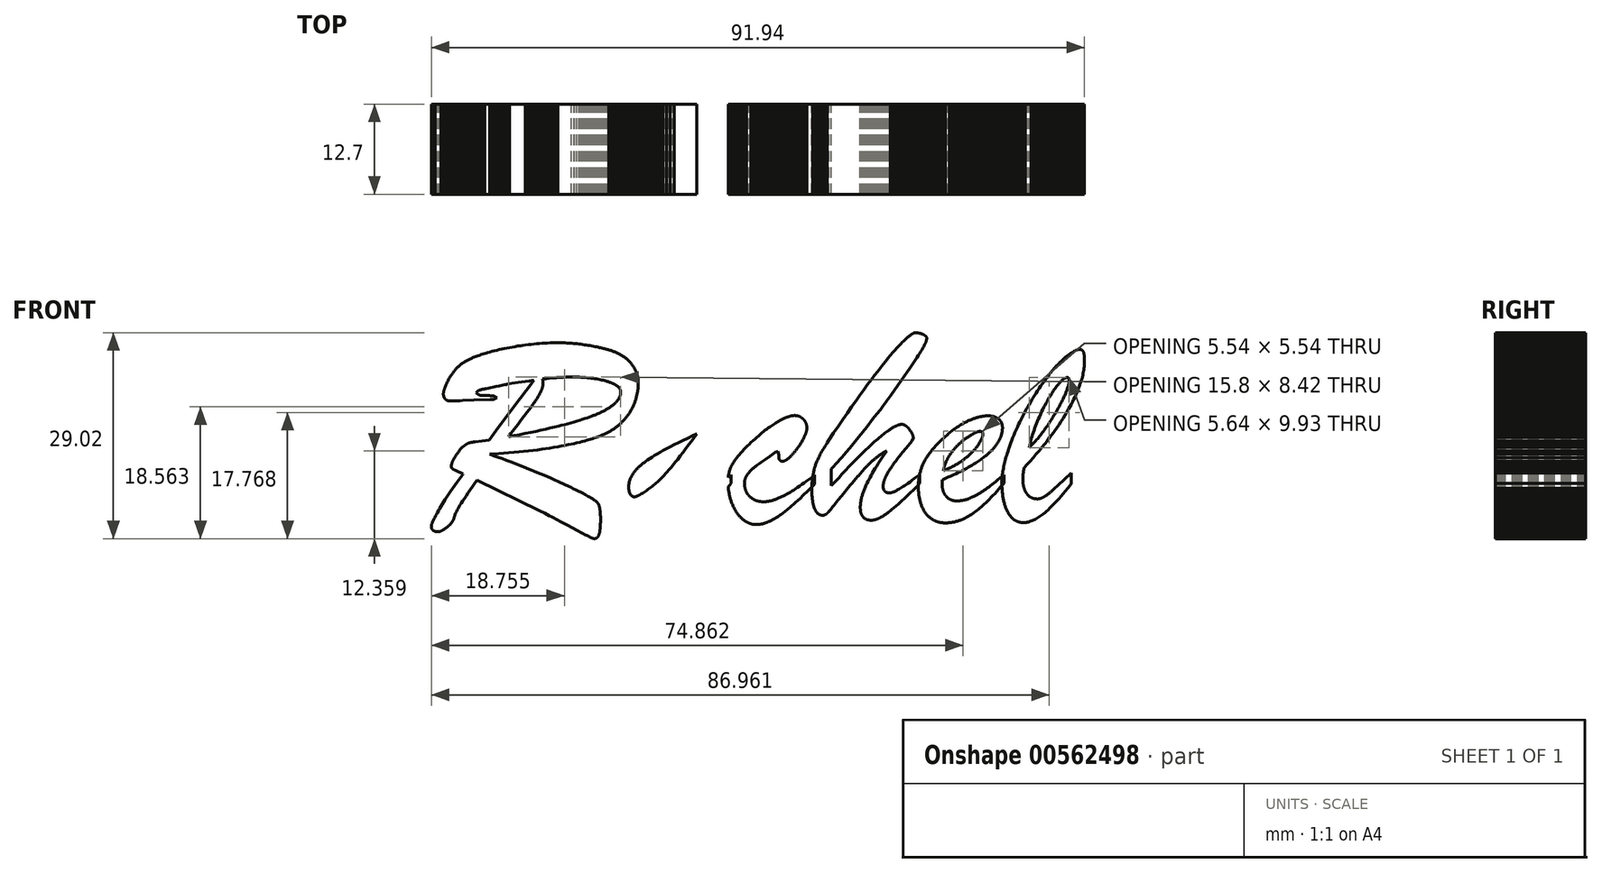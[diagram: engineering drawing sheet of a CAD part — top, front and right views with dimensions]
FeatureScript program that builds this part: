
annotation { "Feature Type Name" : "Feature", "Feature Type Description" : "" }
export const myFeature = defineFeature(function(context is Context, id is Id, definition is map)
    precondition{}
    {
        {
            var Q0;
            Q0=qCreatedBy(makeId("Front.planeOp"),FACE);
            var sketch = newSketch(context, id + "F0", { "sketchPlane" : qUnion([Q0])});
            skLineSegment(sketch, "E0", {"start": v(-45.97, -12.76) * mm, "end": v(-45.97, -12.8) * mm});
            skLineSegment(sketch, "E1", {"start": v(-45.97, -12.8) * mm, "end": v(-45.97, -12.83) * mm});
            skLineSegment(sketch, "E2", {"start": v(-45.97, -12.83) * mm, "end": v(-45.97, -12.86) * mm});
            skLineSegment(sketch, "E3", {"start": v(-45.97, -12.86) * mm, "end": v(-45.97, -12.9) * mm});
            skLineSegment(sketch, "E4", {"start": v(-45.97, -12.9) * mm, "end": v(-45.96, -12.92) * mm});
            skLineSegment(sketch, "E5", {"start": v(-45.96, -12.92) * mm, "end": v(-45.96, -12.95) * mm});
            skLineSegment(sketch, "E6", {"start": v(-45.96, -12.95) * mm, "end": v(-45.95, -12.98) * mm});
            skLineSegment(sketch, "E7", {"start": v(-45.95, -12.98) * mm, "end": v(-45.94, -13) * mm});
            skLineSegment(sketch, "E8", {"start": v(-45.94, -13) * mm, "end": v(-45.94, -13.03) * mm});
            skLineSegment(sketch, "E9", {"start": v(-45.94, -13.03) * mm, "end": v(-45.93, -13.05) * mm});
            skLineSegment(sketch, "E10", {"start": v(-45.93, -13.05) * mm, "end": v(-45.92, -13.08) * mm});
            skLineSegment(sketch, "E11", {"start": v(-45.92, -13.08) * mm, "end": v(-45.9, -13.1) * mm});
            skLineSegment(sketch, "E12", {"start": v(-45.9, -13.1) * mm, "end": v(-45.9, -13.13) * mm});
            skLineSegment(sketch, "E13", {"start": v(-45.9, -13.13) * mm, "end": v(-45.89, -13.15) * mm});
            skLineSegment(sketch, "E14", {"start": v(-45.89, -13.15) * mm, "end": v(-45.87, -13.17) * mm});
            skLineSegment(sketch, "E15", {"start": v(-45.87, -13.17) * mm, "end": v(-45.86, -13.2) * mm});
            skLineSegment(sketch, "E16", {"start": v(-45.86, -13.2) * mm, "end": v(-45.85, -13.21) * mm});
            skLineSegment(sketch, "E17", {"start": v(-45.85, -13.21) * mm, "end": v(-45.83, -13.23) * mm});
            skLineSegment(sketch, "E18", {"start": v(-45.83, -13.23) * mm, "end": v(-45.82, -13.25) * mm});
            skLineSegment(sketch, "E19", {"start": v(-45.82, -13.25) * mm, "end": v(-45.8, -13.27) * mm});
            skLineSegment(sketch, "E20", {"start": v(-45.8, -13.27) * mm, "end": v(-45.78, -13.29) * mm});
            skLineSegment(sketch, "E21", {"start": v(-45.78, -13.29) * mm, "end": v(-45.76, -13.3) * mm});
            skLineSegment(sketch, "E22", {"start": v(-45.76, -13.3) * mm, "end": v(-45.75, -13.32) * mm});
            skLineSegment(sketch, "E23", {"start": v(-45.75, -13.32) * mm, "end": v(-45.73, -13.34) * mm});
            skLineSegment(sketch, "E24", {"start": v(-45.73, -13.34) * mm, "end": v(-45.7, -13.35) * mm});
            skLineSegment(sketch, "E25", {"start": v(-45.7, -13.35) * mm, "end": v(-45.68, -13.37) * mm});
            skLineSegment(sketch, "E26", {"start": v(-45.68, -13.37) * mm, "end": v(-45.66, -13.38) * mm});
            skLineSegment(sketch, "E27", {"start": v(-45.66, -13.38) * mm, "end": v(-45.64, -13.4) * mm});
            skLineSegment(sketch, "E28", {"start": v(-45.64, -13.4) * mm, "end": v(-45.61, -13.4) * mm});
            skLineSegment(sketch, "E29", {"start": v(-45.61, -13.4) * mm, "end": v(-45.59, -13.42) * mm});
            skLineSegment(sketch, "E30", {"start": v(-45.59, -13.42) * mm, "end": v(-45.56, -13.43) * mm});
            skLineSegment(sketch, "E31", {"start": v(-45.56, -13.43) * mm, "end": v(-45.53, -13.45) * mm});
            skLineSegment(sketch, "E32", {"start": v(-45.53, -13.45) * mm, "end": v(-45.5, -13.46) * mm});
            skLineSegment(sketch, "E33", {"start": v(-45.5, -13.46) * mm, "end": v(-45.47, -13.47) * mm});
            skLineSegment(sketch, "E34", {"start": v(-45.47, -13.47) * mm, "end": v(-45.44, -13.48) * mm});
            skLineSegment(sketch, "E35", {"start": v(-45.44, -13.48) * mm, "end": v(-45.4, -13.49) * mm});
            skLineSegment(sketch, "E36", {"start": v(-45.4, -13.49) * mm, "end": v(-45.37, -13.5) * mm});
            skLineSegment(sketch, "E37", {"start": v(-45.37, -13.5) * mm, "end": v(-45.33, -13.5) * mm});
            skLineSegment(sketch, "E38", {"start": v(-45.33, -13.5) * mm, "end": v(-45.3, -13.5) * mm});
            skLineSegment(sketch, "E39", {"start": v(-45.3, -13.5) * mm, "end": v(-45.26, -13.52) * mm});
            skLineSegment(sketch, "E40", {"start": v(-45.26, -13.52) * mm, "end": v(-45.22, -13.52) * mm});
            skLineSegment(sketch, "E41", {"start": v(-45.22, -13.52) * mm, "end": v(-45.17, -13.53) * mm});
            skLineSegment(sketch, "E42", {"start": v(-45.17, -13.53) * mm, "end": v(-45.13, -13.53) * mm});
            skLineSegment(sketch, "E43", {"start": v(-45.13, -13.53) * mm, "end": v(-45.08, -13.53) * mm});
            skLineSegment(sketch, "E44", {"start": v(-45.08, -13.53) * mm, "end": v(-45.04, -13.53) * mm});
            skLineSegment(sketch, "E45", {"start": v(-45.04, -13.53) * mm, "end": v(-44.99, -13.53) * mm});
            skLineSegment(sketch, "E46", {"start": v(-44.99, -13.53) * mm, "end": v(-44.96, -13.53) * mm});
            skLineSegment(sketch, "E47", {"start": v(-44.27, 5.9) * mm, "end": v(-44.27, 5.88) * mm});
            skLineSegment(sketch, "E48", {"start": v(-44.27, 5.88) * mm, "end": v(-44.27, 5.85) * mm});
            skLineSegment(sketch, "E49", {"start": v(-44.27, 5.85) * mm, "end": v(-44.26, 5.81) * mm});
            skLineSegment(sketch, "E50", {"start": v(-44.26, 5.81) * mm, "end": v(-44.26, 5.78) * mm});
            skLineSegment(sketch, "E51", {"start": v(-44.26, 5.78) * mm, "end": v(-44.26, 5.75) * mm});
            skLineSegment(sketch, "E52", {"start": v(-44.26, 5.75) * mm, "end": v(-44.26, 5.72) * mm});
            skLineSegment(sketch, "E53", {"start": v(-44.26, 5.72) * mm, "end": v(-44.25, 5.7) * mm});
            skLineSegment(sketch, "E54", {"start": v(-44.25, 5.7) * mm, "end": v(-44.25, 5.67) * mm});
            skLineSegment(sketch, "E55", {"start": v(-44.25, 5.67) * mm, "end": v(-44.25, 5.64) * mm});
            skLineSegment(sketch, "E56", {"start": v(-44.25, 5.64) * mm, "end": v(-44.24, 5.61) * mm});
            skLineSegment(sketch, "E57", {"start": v(-44.24, 5.61) * mm, "end": v(-44.23, 5.59) * mm});
            skLineSegment(sketch, "E58", {"start": v(-44.23, 5.59) * mm, "end": v(-44.23, 5.56) * mm});
            skLineSegment(sketch, "E59", {"start": v(-44.23, 5.56) * mm, "end": v(-44.22, 5.54) * mm});
            skLineSegment(sketch, "E60", {"start": v(-44.22, 5.54) * mm, "end": v(-44.22, 5.51) * mm});
            skLineSegment(sketch, "E61", {"start": v(-44.22, 5.51) * mm, "end": v(-44.2, 5.5) * mm});
            skLineSegment(sketch, "E62", {"start": v(-44.2, 5.5) * mm, "end": v(-44.2, 5.47) * mm});
            skLineSegment(sketch, "E63", {"start": v(-44.2, 5.47) * mm, "end": v(-44.2, 5.45) * mm});
            skLineSegment(sketch, "E64", {"start": v(-44.2, 5.45) * mm, "end": v(-44.18, 5.42) * mm});
            skLineSegment(sketch, "E65", {"start": v(-44.18, 5.42) * mm, "end": v(-44.17, 5.4) * mm});
            skLineSegment(sketch, "E66", {"start": v(-44.17, 5.4) * mm, "end": v(-44.16, 5.38) * mm});
            skLineSegment(sketch, "E67", {"start": v(-44.16, 5.38) * mm, "end": v(-44.15, 5.36) * mm});
            skLineSegment(sketch, "E68", {"start": v(-44.15, 5.36) * mm, "end": v(-44.14, 5.34) * mm});
            skLineSegment(sketch, "E69", {"start": v(-44.14, 5.34) * mm, "end": v(-44.13, 5.32) * mm});
            skLineSegment(sketch, "E70", {"start": v(-44.13, 5.32) * mm, "end": v(-44.12, 5.3) * mm});
            skLineSegment(sketch, "E71", {"start": v(-44.12, 5.3) * mm, "end": v(-44.1, 5.29) * mm});
            skLineSegment(sketch, "E72", {"start": v(-44.1, 5.29) * mm, "end": v(-44.1, 5.27) * mm});
            skLineSegment(sketch, "E73", {"start": v(-44.1, 5.27) * mm, "end": v(-44.08, 5.25) * mm});
            skLineSegment(sketch, "E74", {"start": v(-44.08, 5.25) * mm, "end": v(-44.07, 5.23) * mm});
            skLineSegment(sketch, "E75", {"start": v(-44.07, 5.23) * mm, "end": v(-44.05, 5.21) * mm});
            skLineSegment(sketch, "E76", {"start": v(-44.05, 5.21) * mm, "end": v(-44.04, 5.2) * mm});
            skLineSegment(sketch, "E77", {"start": v(-44.04, 5.2) * mm, "end": v(-44.02, 5.18) * mm});
            skLineSegment(sketch, "E78", {"start": v(-44.02, 5.18) * mm, "end": v(-44, 5.16) * mm});
            skLineSegment(sketch, "E79", {"start": v(-43.13, -4.13) * mm, "end": v(-43.14, -4.15) * mm});
            skLineSegment(sketch, "E80", {"start": v(-43.14, -4.15) * mm, "end": v(-43.14, -4.18) * mm});
            skLineSegment(sketch, "E81", {"start": v(-43.14, -4.18) * mm, "end": v(-43.14, -4.2) * mm});
            skLineSegment(sketch, "E82", {"start": v(-43.14, -4.2) * mm, "end": v(-43.14, -4.23) * mm});
            skLineSegment(sketch, "E83", {"start": v(-43.14, -4.23) * mm, "end": v(-43.15, -4.25) * mm});
            skLineSegment(sketch, "E84", {"start": v(-43.15, -4.25) * mm, "end": v(-43.15, -4.27) * mm});
            skLineSegment(sketch, "E85", {"start": v(-43.15, -4.27) * mm, "end": v(-43.15, -4.3) * mm});
            skLineSegment(sketch, "E86", {"start": v(-43.15, -4.3) * mm, "end": v(-43.15, -4.32) * mm});
            skLineSegment(sketch, "E87", {"start": v(-43.15, -4.32) * mm, "end": v(-43.14, -4.34) * mm});
            skLineSegment(sketch, "E88", {"start": v(-43.14, -4.34) * mm, "end": v(-43.14, -4.36) * mm});
            skLineSegment(sketch, "E89", {"start": v(-43.14, -4.36) * mm, "end": v(-43.14, -4.38) * mm});
            skLineSegment(sketch, "E90", {"start": v(-43.14, -4.38) * mm, "end": v(-43.14, -4.4) * mm});
            skLineSegment(sketch, "E91", {"start": v(-43.14, -4.4) * mm, "end": v(-43.14, -4.41) * mm});
            skLineSegment(sketch, "E92", {"start": v(-43.14, -4.41) * mm, "end": v(-43.13, -4.43) * mm});
            skLineSegment(sketch, "E93", {"start": v(-43.13, -4.43) * mm, "end": v(-43.13, -4.45) * mm});
            skLineSegment(sketch, "E94", {"start": v(-43.13, -4.45) * mm, "end": v(-43.13, -4.46) * mm});
            skLineSegment(sketch, "E95", {"start": v(-43.13, -4.46) * mm, "end": v(-43.12, -4.48) * mm});
            skLineSegment(sketch, "E96", {"start": v(-43.12, -4.48) * mm, "end": v(-43.12, -4.5) * mm});
            skLineSegment(sketch, "E97", {"start": v(-43.12, -4.5) * mm, "end": v(-43.11, -4.5) * mm});
            skLineSegment(sketch, "E98", {"start": v(-43.11, -4.5) * mm, "end": v(-43.1, -4.52) * mm});
            skLineSegment(sketch, "E99", {"start": v(-43.1, -4.52) * mm, "end": v(-43.1, -4.53) * mm});
            skLineSegment(sketch, "E100", {"start": v(-43.1, -4.53) * mm, "end": v(-43.1, -4.55) * mm});
            skLineSegment(sketch, "E101", {"start": v(-43.1, -4.55) * mm, "end": v(-43.09, -4.56) * mm});
            skLineSegment(sketch, "E102", {"start": v(-43.09, -4.56) * mm, "end": v(-43.08, -4.57) * mm});
            skLineSegment(sketch, "E103", {"start": v(-43.08, -4.57) * mm, "end": v(-43.07, -4.58) * mm});
            skLineSegment(sketch, "E104", {"start": v(-43.07, -4.58) * mm, "end": v(-43.07, -4.6) * mm});
            skLineSegment(sketch, "E105", {"start": v(-43.07, -4.6) * mm, "end": v(-43.06, -4.6) * mm});
            skLineSegment(sketch, "E106", {"start": v(-43.06, -4.6) * mm, "end": v(-43.05, -4.62) * mm});
            skLineSegment(sketch, "E107", {"start": v(-43.05, -4.62) * mm, "end": v(-43.04, -4.63) * mm});
            skLineSegment(sketch, "E108", {"start": v(-43.04, -4.63) * mm, "end": v(-43.03, -4.64) * mm});
            skLineSegment(sketch, "E109", {"start": v(-43.03, -4.64) * mm, "end": v(-43.02, -4.65) * mm});
            skLineSegment(sketch, "E110", {"start": v(-43.02, -4.65) * mm, "end": v(-43.01, -4.66) * mm});
            skLineSegment(sketch, "E111", {"start": v(-43.01, -4.66) * mm, "end": v(-43, -4.67) * mm});
            skLineSegment(sketch, "E112", {"start": v(-43, -4.67) * mm, "end": v(-43, -4.67) * mm});
            skLineSegment(sketch, "E113", {"start": v(-43, -4.67) * mm, "end": v(-42.98, -4.68) * mm});
            skLineSegment(sketch, "E114", {"start": v(-42.98, -4.68) * mm, "end": v(-42.97, -4.7) * mm});
            skLineSegment(sketch, "E115", {"start": v(-42.97, -4.7) * mm, "end": v(-42.96, -4.7) * mm});
            skLineSegment(sketch, "E116", {"start": v(-42.96, -4.7) * mm, "end": v(-42.94, -4.7) * mm});
            skLineSegment(sketch, "E117", {"start": v(-42.94, -4.7) * mm, "end": v(-42.93, -4.71) * mm});
            skLineSegment(sketch, "E118", {"start": v(-42.93, -4.71) * mm, "end": v(-42.92, -4.72) * mm});
            skLineSegment(sketch, "E119", {"start": v(-43.9, 7.15) * mm, "end": v(-43.9, 7.13) * mm});
            skLineSegment(sketch, "E120", {"start": v(-43.9, 7.13) * mm, "end": v(-43.95, 7.02) * mm});
            skLineSegment(sketch, "E121", {"start": v(-43.95, 7.02) * mm, "end": v(-43.99, 6.92) * mm});
            skLineSegment(sketch, "E122", {"start": v(-43.99, 6.92) * mm, "end": v(-44.02, 6.83) * mm});
            skLineSegment(sketch, "E123", {"start": v(-44.02, 6.83) * mm, "end": v(-44.06, 6.74) * mm});
            skLineSegment(sketch, "E124", {"start": v(-44.06, 6.74) * mm, "end": v(-44.09, 6.65) * mm});
            skLineSegment(sketch, "E125", {"start": v(-44.09, 6.65) * mm, "end": v(-44.11, 6.57) * mm});
            skLineSegment(sketch, "E126", {"start": v(-44.11, 6.57) * mm, "end": v(-44.14, 6.5) * mm});
            skLineSegment(sketch, "E127", {"start": v(-44.14, 6.5) * mm, "end": v(-44.16, 6.43) * mm});
            skLineSegment(sketch, "E128", {"start": v(-44.16, 6.43) * mm, "end": v(-44.18, 6.36) * mm});
            skLineSegment(sketch, "E129", {"start": v(-44.18, 6.36) * mm, "end": v(-44.2, 6.3) * mm});
            skLineSegment(sketch, "E130", {"start": v(-44.2, 6.3) * mm, "end": v(-44.21, 6.24) * mm});
            skLineSegment(sketch, "E131", {"start": v(-44.21, 6.24) * mm, "end": v(-44.22, 6.2) * mm});
            skLineSegment(sketch, "E132", {"start": v(-44.22, 6.2) * mm, "end": v(-44.23, 6.14) * mm});
            skLineSegment(sketch, "E133", {"start": v(-44.23, 6.14) * mm, "end": v(-44.24, 6.1) * mm});
            skLineSegment(sketch, "E134", {"start": v(-44.24, 6.1) * mm, "end": v(-44.25, 6.06) * mm});
            skLineSegment(sketch, "E135", {"start": v(-44.25, 6.06) * mm, "end": v(-44.26, 6.02) * mm});
            skLineSegment(sketch, "E136", {"start": v(-44.26, 6.02) * mm, "end": v(-44.26, 5.98) * mm});
            skLineSegment(sketch, "E137", {"start": v(-44.26, 5.98) * mm, "end": v(-44.26, 5.95) * mm});
            skLineSegment(sketch, "E138", {"start": v(-44.26, 5.95) * mm, "end": v(-44.27, 5.92) * mm});
            skLineSegment(sketch, "E139", {"start": v(-44.27, 5.92) * mm, "end": v(-44.27, 5.9) * mm});
            skLineSegment(sketch, "E140", {"start": v(-42.82, 9) * mm, "end": v(-42.88, 8.91) * mm});
            skLineSegment(sketch, "E141", {"start": v(-42.88, 8.91) * mm, "end": v(-42.96, 8.8) * mm});
            skLineSegment(sketch, "E142", {"start": v(-42.96, 8.8) * mm, "end": v(-43.04, 8.7) * mm});
            skLineSegment(sketch, "E143", {"start": v(-43.04, 8.7) * mm, "end": v(-43.11, 8.58) * mm});
            skLineSegment(sketch, "E144", {"start": v(-43.11, 8.58) * mm, "end": v(-43.19, 8.47) * mm});
            skLineSegment(sketch, "E145", {"start": v(-43.19, 8.47) * mm, "end": v(-43.25, 8.37) * mm});
            skLineSegment(sketch, "E146", {"start": v(-43.25, 8.37) * mm, "end": v(-43.32, 8.26) * mm});
            skLineSegment(sketch, "E147", {"start": v(-43.32, 8.26) * mm, "end": v(-43.39, 8.15) * mm});
            skLineSegment(sketch, "E148", {"start": v(-43.39, 8.15) * mm, "end": v(-43.45, 8.05) * mm});
            skLineSegment(sketch, "E149", {"start": v(-43.45, 8.05) * mm, "end": v(-43.5, 7.95) * mm});
            skLineSegment(sketch, "E150", {"start": v(-43.5, 7.95) * mm, "end": v(-43.56, 7.84) * mm});
            skLineSegment(sketch, "E151", {"start": v(-43.56, 7.84) * mm, "end": v(-43.62, 7.74) * mm});
            skLineSegment(sketch, "E152", {"start": v(-43.62, 7.74) * mm, "end": v(-43.67, 7.64) * mm});
            skLineSegment(sketch, "E153", {"start": v(-43.67, 7.64) * mm, "end": v(-43.72, 7.54) * mm});
            skLineSegment(sketch, "E154", {"start": v(-43.72, 7.54) * mm, "end": v(-43.77, 7.44) * mm});
            skLineSegment(sketch, "E155", {"start": v(-43.77, 7.44) * mm, "end": v(-43.81, 7.35) * mm});
            skLineSegment(sketch, "E156", {"start": v(-43.81, 7.35) * mm, "end": v(-43.85, 7.25) * mm});
            skLineSegment(sketch, "E157", {"start": v(-43.85, 7.25) * mm, "end": v(-43.9, 7.15) * mm});
            skLineSegment(sketch, "E158", {"start": v(-42.72, -11.43) * mm, "end": v(-42.7, -11.33) * mm});
            skLineSegment(sketch, "E159", {"start": v(-42.7, -11.33) * mm, "end": v(-42.66, -11.23) * mm});
            skLineSegment(sketch, "E160", {"start": v(-42.66, -11.23) * mm, "end": v(-42.6, -11.1) * mm});
            skLineSegment(sketch, "E161", {"start": v(-42.6, -11.1) * mm, "end": v(-42.55, -10.97) * mm});
            skLineSegment(sketch, "E162", {"start": v(-42.55, -10.97) * mm, "end": v(-42.48, -10.82) * mm});
            skLineSegment(sketch, "E163", {"start": v(-42.48, -10.82) * mm, "end": v(-42.4, -10.65) * mm});
            skLineSegment(sketch, "E164", {"start": v(-42.4, -10.65) * mm, "end": v(-42.3, -10.47) * mm});
            skLineSegment(sketch, "E165", {"start": v(-42.3, -10.47) * mm, "end": v(-42.2, -10.26) * mm});
            skLineSegment(sketch, "E166", {"start": v(-42.2, -10.26) * mm, "end": v(-42.06, -10.03) * mm});
            skLineSegment(sketch, "E167", {"start": v(-42.06, -10.03) * mm, "end": v(-41.91, -9.78) * mm});
            skLineSegment(sketch, "E168", {"start": v(-41.91, -9.78) * mm, "end": v(-41.74, -9.5) * mm});
            skLineSegment(sketch, "E169", {"start": v(-41.74, -9.5) * mm, "end": v(-41.55, -9.2) * mm});
            skLineSegment(sketch, "E170", {"start": v(-41.55, -9.2) * mm, "end": v(-41.33, -8.85) * mm});
            skLineSegment(sketch, "E171", {"start": v(-41.33, -8.85) * mm, "end": v(-41.08, -8.48) * mm});
            skLineSegment(sketch, "E172", {"start": v(-41.08, -8.48) * mm, "end": v(-40.8, -8.07) * mm});
            skLineSegment(sketch, "E173", {"start": v(-40.8, -8.07) * mm, "end": v(-40.5, -7.63) * mm});
            skLineSegment(sketch, "E174", {"start": v(-40.5, -7.63) * mm, "end": v(-40.15, -7.14) * mm});
            skLineSegment(sketch, "E175", {"start": v(-40.15, -7.14) * mm, "end": v(-39.76, -6.6) * mm});
            skLineSegment(sketch, "E176", {"start": v(-39.76, -6.6) * mm, "end": v(-39.52, -6.27) * mm});
            skLineSegment(sketch, "E177", {"start": v(-44.78, -10.26) * mm, "end": v(-44.95, -10.56) * mm});
            skLineSegment(sketch, "E178", {"start": v(-44.95, -10.56) * mm, "end": v(-45.1, -10.83) * mm});
            skLineSegment(sketch, "E179", {"start": v(-45.1, -10.83) * mm, "end": v(-45.24, -11.07) * mm});
            skLineSegment(sketch, "E180", {"start": v(-45.24, -11.07) * mm, "end": v(-45.35, -11.29) * mm});
            skLineSegment(sketch, "E181", {"start": v(-45.35, -11.29) * mm, "end": v(-45.46, -11.48) * mm});
            skLineSegment(sketch, "E182", {"start": v(-45.46, -11.48) * mm, "end": v(-45.54, -11.65) * mm});
            skLineSegment(sketch, "E183", {"start": v(-45.54, -11.65) * mm, "end": v(-45.62, -11.8) * mm});
            skLineSegment(sketch, "E184", {"start": v(-45.62, -11.8) * mm, "end": v(-45.69, -11.95) * mm});
            skLineSegment(sketch, "E185", {"start": v(-45.69, -11.95) * mm, "end": v(-45.75, -12.07) * mm});
            skLineSegment(sketch, "E186", {"start": v(-45.75, -12.07) * mm, "end": v(-45.8, -12.18) * mm});
            skLineSegment(sketch, "E187", {"start": v(-45.8, -12.18) * mm, "end": v(-45.84, -12.28) * mm});
            skLineSegment(sketch, "E188", {"start": v(-45.84, -12.28) * mm, "end": v(-45.87, -12.36) * mm});
            skLineSegment(sketch, "E189", {"start": v(-45.87, -12.36) * mm, "end": v(-45.9, -12.44) * mm});
            skLineSegment(sketch, "E190", {"start": v(-45.9, -12.44) * mm, "end": v(-45.92, -12.5) * mm});
            skLineSegment(sketch, "E191", {"start": v(-45.92, -12.5) * mm, "end": v(-45.94, -12.56) * mm});
            skLineSegment(sketch, "E192", {"start": v(-45.94, -12.56) * mm, "end": v(-45.95, -12.62) * mm});
            skLineSegment(sketch, "E193", {"start": v(-45.95, -12.62) * mm, "end": v(-45.96, -12.66) * mm});
            skLineSegment(sketch, "E194", {"start": v(-45.96, -12.66) * mm, "end": v(-45.97, -12.7) * mm});
            skLineSegment(sketch, "E195", {"start": v(-45.97, -12.7) * mm, "end": v(-45.97, -12.73) * mm});
            skLineSegment(sketch, "E196", {"start": v(-45.97, -12.73) * mm, "end": v(-45.97, -12.76) * mm});
            skLineSegment(sketch, "E197", {"start": v(-42.49, -2.77) * mm, "end": v(-42.55, -2.86) * mm});
            skLineSegment(sketch, "E198", {"start": v(-42.55, -2.86) * mm, "end": v(-42.6, -2.95) * mm});
            skLineSegment(sketch, "E199", {"start": v(-42.6, -2.95) * mm, "end": v(-42.66, -3.04) * mm});
            skLineSegment(sketch, "E200", {"start": v(-42.66, -3.04) * mm, "end": v(-42.7, -3.12) * mm});
            skLineSegment(sketch, "E201", {"start": v(-42.7, -3.12) * mm, "end": v(-42.75, -3.2) * mm});
            skLineSegment(sketch, "E202", {"start": v(-42.75, -3.2) * mm, "end": v(-42.8, -3.28) * mm});
            skLineSegment(sketch, "E203", {"start": v(-42.8, -3.28) * mm, "end": v(-42.84, -3.35) * mm});
            skLineSegment(sketch, "E204", {"start": v(-42.84, -3.35) * mm, "end": v(-42.88, -3.42) * mm});
            skLineSegment(sketch, "E205", {"start": v(-42.88, -3.42) * mm, "end": v(-42.91, -3.5) * mm});
            skLineSegment(sketch, "E206", {"start": v(-42.91, -3.5) * mm, "end": v(-42.94, -3.56) * mm});
            skLineSegment(sketch, "E207", {"start": v(-42.94, -3.56) * mm, "end": v(-42.97, -3.62) * mm});
            skLineSegment(sketch, "E208", {"start": v(-42.97, -3.62) * mm, "end": v(-43, -3.68) * mm});
            skLineSegment(sketch, "E209", {"start": v(-43, -3.68) * mm, "end": v(-43.02, -3.74) * mm});
            skLineSegment(sketch, "E210", {"start": v(-43.02, -3.74) * mm, "end": v(-43.04, -3.79) * mm});
            skLineSegment(sketch, "E211", {"start": v(-43.04, -3.79) * mm, "end": v(-43.06, -3.84) * mm});
            skLineSegment(sketch, "E212", {"start": v(-43.06, -3.84) * mm, "end": v(-43.08, -3.89) * mm});
            skLineSegment(sketch, "E213", {"start": v(-43.08, -3.89) * mm, "end": v(-43.1, -3.93) * mm});
            skLineSegment(sketch, "E214", {"start": v(-43.1, -3.93) * mm, "end": v(-43.1, -3.98) * mm});
            skLineSegment(sketch, "E215", {"start": v(-43.1, -3.98) * mm, "end": v(-43.11, -4.02) * mm});
            skLineSegment(sketch, "E216", {"start": v(-43.11, -4.02) * mm, "end": v(-43.12, -4.06) * mm});
            skLineSegment(sketch, "E217", {"start": v(-43.12, -4.06) * mm, "end": v(-43.13, -4.1) * mm});
            skLineSegment(sketch, "E218", {"start": v(-43.13, -4.1) * mm, "end": v(-43.13, -4.13) * mm});
            skLineSegment(sketch, "E219", {"start": v(-39.68, 6.02) * mm, "end": v(-39.32, 6.37) * mm});
            skLineSegment(sketch, "E220", {"start": v(-30.27, 7.74) * mm, "end": v(-30.3, 8) * mm});
            skLineSegment(sketch, "E221", {"start": v(-30.25, 7.4) * mm, "end": v(-30.27, 7.74) * mm});
            skLineSegment(sketch, "E222", {"start": v(-30.6, 6.12) * mm, "end": v(-30.6, 6.13) * mm});
            skLineSegment(sketch, "E223", {"start": v(-30.6, 6.13) * mm, "end": v(-30.57, 6.2) * mm});
            skLineSegment(sketch, "E224", {"start": v(-30.57, 6.2) * mm, "end": v(-30.53, 6.27) * mm});
            skLineSegment(sketch, "E225", {"start": v(-30.53, 6.27) * mm, "end": v(-30.5, 6.34) * mm});
            skLineSegment(sketch, "E226", {"start": v(-30.5, 6.34) * mm, "end": v(-30.48, 6.4) * mm});
            skLineSegment(sketch, "E227", {"start": v(-30.48, 6.4) * mm, "end": v(-30.45, 6.46) * mm});
            skLineSegment(sketch, "E228", {"start": v(-30.45, 6.46) * mm, "end": v(-30.43, 6.52) * mm});
            skLineSegment(sketch, "E229", {"start": v(-30.43, 6.52) * mm, "end": v(-30.4, 6.58) * mm});
            skLineSegment(sketch, "E230", {"start": v(-30.4, 6.58) * mm, "end": v(-30.38, 6.64) * mm});
            skLineSegment(sketch, "E231", {"start": v(-30.38, 6.64) * mm, "end": v(-30.37, 6.7) * mm});
            skLineSegment(sketch, "E232", {"start": v(-30.37, 6.7) * mm, "end": v(-30.35, 6.75) * mm});
            skLineSegment(sketch, "E233", {"start": v(-30.35, 6.75) * mm, "end": v(-30.33, 6.8) * mm});
            skLineSegment(sketch, "E234", {"start": v(-30.33, 6.8) * mm, "end": v(-30.32, 6.85) * mm});
            skLineSegment(sketch, "E235", {"start": v(-30.32, 6.85) * mm, "end": v(-30.3, 6.9) * mm});
            skLineSegment(sketch, "E236", {"start": v(-30.3, 6.9) * mm, "end": v(-30.3, 6.95) * mm});
            skLineSegment(sketch, "E237", {"start": v(-30.3, 6.95) * mm, "end": v(-30.28, 7) * mm});
            skLineSegment(sketch, "E238", {"start": v(-30.28, 7) * mm, "end": v(-30.28, 7.04) * mm});
            skLineSegment(sketch, "E239", {"start": v(-30.28, 7.04) * mm, "end": v(-30.27, 7.09) * mm});
            skLineSegment(sketch, "E240", {"start": v(-30.27, 7.09) * mm, "end": v(-30.26, 7.13) * mm});
            skLineSegment(sketch, "E241", {"start": v(-30.26, 7.13) * mm, "end": v(-30.26, 7.17) * mm});
            skLineSegment(sketch, "E242", {"start": v(-30.26, 7.17) * mm, "end": v(-30.25, 7.21) * mm});
            skLineSegment(sketch, "E243", {"start": v(-30.25, 7.21) * mm, "end": v(-30.25, 7.25) * mm});
            skLineSegment(sketch, "E244", {"start": v(-30.25, 7.25) * mm, "end": v(-30.25, 7.3) * mm});
            skLineSegment(sketch, "E245", {"start": v(-30.25, 7.3) * mm, "end": v(-30.25, 7.33) * mm});
            skLineSegment(sketch, "E246", {"start": v(-30.25, 7.33) * mm, "end": v(-30.25, 7.37) * mm});
            skLineSegment(sketch, "E247", {"start": v(-30.25, 7.37) * mm, "end": v(-30.25, 7.4) * mm});
            skLineSegment(sketch, "E248", {"start": v(-31.5, 4.63) * mm, "end": v(-31.47, 4.67) * mm});
            skLineSegment(sketch, "E249", {"start": v(-31.47, 4.67) * mm, "end": v(-31.4, 4.79) * mm});
            skLineSegment(sketch, "E250", {"start": v(-31.4, 4.79) * mm, "end": v(-31.31, 4.9) * mm});
            skLineSegment(sketch, "E251", {"start": v(-31.31, 4.9) * mm, "end": v(-31.24, 5.02) * mm});
            skLineSegment(sketch, "E252", {"start": v(-31.24, 5.02) * mm, "end": v(-31.16, 5.14) * mm});
            skLineSegment(sketch, "E253", {"start": v(-31.16, 5.14) * mm, "end": v(-31.1, 5.25) * mm});
            skLineSegment(sketch, "E254", {"start": v(-31.1, 5.25) * mm, "end": v(-31.02, 5.37) * mm});
            skLineSegment(sketch, "E255", {"start": v(-31.02, 5.37) * mm, "end": v(-30.96, 5.48) * mm});
            skLineSegment(sketch, "E256", {"start": v(-30.96, 5.48) * mm, "end": v(-30.9, 5.59) * mm});
            skLineSegment(sketch, "E257", {"start": v(-30.9, 5.59) * mm, "end": v(-30.83, 5.7) * mm});
            skLineSegment(sketch, "E258", {"start": v(-30.83, 5.7) * mm, "end": v(-30.77, 5.8) * mm});
            skLineSegment(sketch, "E259", {"start": v(-30.77, 5.8) * mm, "end": v(-30.72, 5.9) * mm});
            skLineSegment(sketch, "E260", {"start": v(-30.72, 5.9) * mm, "end": v(-30.66, 6.01) * mm});
            skLineSegment(sketch, "E261", {"start": v(-30.66, 6.01) * mm, "end": v(-30.6, 6.12) * mm});
            skLineSegment(sketch, "E262", {"start": v(-36.53, 1.14) * mm, "end": v(-37.81, -0.61) * mm});
            skLineSegment(sketch, "E263", {"start": v(-41.47, -5.36) * mm, "end": v(-41.58, -5.51) * mm});
            skLineSegment(sketch, "E264", {"start": v(-41.58, -5.51) * mm, "end": v(-41.97, -6.03) * mm});
            skLineSegment(sketch, "E265", {"start": v(-41.97, -6.03) * mm, "end": v(-42.32, -6.52) * mm});
            skLineSegment(sketch, "E266", {"start": v(-42.32, -6.52) * mm, "end": v(-42.65, -6.98) * mm});
            skLineSegment(sketch, "E267", {"start": v(-42.65, -6.98) * mm, "end": v(-42.96, -7.42) * mm});
            skLineSegment(sketch, "E268", {"start": v(-42.96, -7.42) * mm, "end": v(-43.25, -7.84) * mm});
            skLineSegment(sketch, "E269", {"start": v(-43.25, -7.84) * mm, "end": v(-43.52, -8.24) * mm});
            skLineSegment(sketch, "E270", {"start": v(-43.52, -8.24) * mm, "end": v(-43.77, -8.62) * mm});
            skLineSegment(sketch, "E271", {"start": v(-43.77, -8.62) * mm, "end": v(-44, -8.98) * mm});
            skLineSegment(sketch, "E272", {"start": v(-44, -8.98) * mm, "end": v(-44.22, -9.32) * mm});
            skLineSegment(sketch, "E273", {"start": v(-44.22, -9.32) * mm, "end": v(-44.42, -9.65) * mm});
            skLineSegment(sketch, "E274", {"start": v(-44.42, -9.65) * mm, "end": v(-44.6, -9.96) * mm});
            skLineSegment(sketch, "E275", {"start": v(-44.6, -9.96) * mm, "end": v(-44.78, -10.26) * mm});
            skLineSegment(sketch, "E276", {"start": v(-35.14, 3) * mm, "end": v(-36.53, 1.14) * mm});
            skLineSegment(sketch, "E277", {"start": v(-31.99, 7.21) * mm, "end": v(-34.06, 4.45) * mm});
            skLineSegment(sketch, "E278", {"start": v(-34.06, 4.45) * mm, "end": v(-35.14, 3) * mm});
            skLineSegment(sketch, "E279", {"start": v(-31.54, 7.8) * mm, "end": v(-31.99, 7.21) * mm});
            skLineSegment(sketch, "E280", {"start": v(-41.6, -1.6) * mm, "end": v(-41.64, -1.64) * mm});
            skLineSegment(sketch, "E281", {"start": v(-41.64, -1.64) * mm, "end": v(-41.68, -1.68) * mm});
            skLineSegment(sketch, "E282", {"start": v(-41.68, -1.68) * mm, "end": v(-41.72, -1.73) * mm});
            skLineSegment(sketch, "E283", {"start": v(-41.72, -1.73) * mm, "end": v(-41.76, -1.77) * mm});
            skLineSegment(sketch, "E284", {"start": v(-41.76, -1.77) * mm, "end": v(-41.8, -1.83) * mm});
            skLineSegment(sketch, "E285", {"start": v(-41.8, -1.83) * mm, "end": v(-41.86, -1.89) * mm});
            skLineSegment(sketch, "E286", {"start": v(-41.86, -1.89) * mm, "end": v(-41.9, -1.95) * mm});
            skLineSegment(sketch, "E287", {"start": v(-41.9, -1.95) * mm, "end": v(-41.96, -2.02) * mm});
            skLineSegment(sketch, "E288", {"start": v(-41.96, -2.02) * mm, "end": v(-42.02, -2.1) * mm});
            skLineSegment(sketch, "E289", {"start": v(-42.02, -2.1) * mm, "end": v(-42.08, -2.18) * mm});
            skLineSegment(sketch, "E290", {"start": v(-42.08, -2.18) * mm, "end": v(-42.15, -2.27) * mm});
            skLineSegment(sketch, "E291", {"start": v(-42.15, -2.27) * mm, "end": v(-42.22, -2.37) * mm});
            skLineSegment(sketch, "E292", {"start": v(-42.22, -2.37) * mm, "end": v(-42.29, -2.47) * mm});
            skLineSegment(sketch, "E293", {"start": v(-42.29, -2.47) * mm, "end": v(-42.36, -2.58) * mm});
            skLineSegment(sketch, "E294", {"start": v(-42.36, -2.58) * mm, "end": v(-42.44, -2.7) * mm});
            skLineSegment(sketch, "E295", {"start": v(-42.44, -2.7) * mm, "end": v(-42.49, -2.77) * mm});
            skLineSegment(sketch, "E296", {"start": v(-41.23, 10.44) * mm, "end": v(-41.25, 10.43) * mm});
            skLineSegment(sketch, "E297", {"start": v(-41.25, 10.43) * mm, "end": v(-41.33, 10.38) * mm});
            skLineSegment(sketch, "E298", {"start": v(-41.33, 10.38) * mm, "end": v(-41.41, 10.33) * mm});
            skLineSegment(sketch, "E299", {"start": v(-41.41, 10.33) * mm, "end": v(-41.5, 10.27) * mm});
            skLineSegment(sketch, "E300", {"start": v(-41.5, 10.27) * mm, "end": v(-41.57, 10.22) * mm});
            skLineSegment(sketch, "E301", {"start": v(-41.57, 10.22) * mm, "end": v(-41.65, 10.16) * mm});
            skLineSegment(sketch, "E302", {"start": v(-41.65, 10.16) * mm, "end": v(-41.72, 10.1) * mm});
            skLineSegment(sketch, "E303", {"start": v(-41.72, 10.1) * mm, "end": v(-41.8, 10.05) * mm});
            skLineSegment(sketch, "E304", {"start": v(-41.8, 10.05) * mm, "end": v(-41.87, 10) * mm});
            skLineSegment(sketch, "E305", {"start": v(-41.87, 10) * mm, "end": v(-41.95, 9.93) * mm});
            skLineSegment(sketch, "E306", {"start": v(-41.95, 9.93) * mm, "end": v(-42.02, 9.87) * mm});
            skLineSegment(sketch, "E307", {"start": v(-42.02, 9.87) * mm, "end": v(-42.1, 9.8) * mm});
            skLineSegment(sketch, "E308", {"start": v(-42.1, 9.8) * mm, "end": v(-42.16, 9.74) * mm});
            skLineSegment(sketch, "E309", {"start": v(-42.16, 9.74) * mm, "end": v(-42.23, 9.67) * mm});
            skLineSegment(sketch, "E310", {"start": v(-42.23, 9.67) * mm, "end": v(-42.3, 9.6) * mm});
            skLineSegment(sketch, "E311", {"start": v(-42.3, 9.6) * mm, "end": v(-42.37, 9.53) * mm});
            skLineSegment(sketch, "E312", {"start": v(-42.37, 9.53) * mm, "end": v(-42.44, 9.46) * mm});
            skLineSegment(sketch, "E313", {"start": v(-42.44, 9.46) * mm, "end": v(-42.5, 9.39) * mm});
            skLineSegment(sketch, "E314", {"start": v(-42.5, 9.39) * mm, "end": v(-42.57, 9.31) * mm});
            skLineSegment(sketch, "E315", {"start": v(-42.57, 9.31) * mm, "end": v(-42.63, 9.24) * mm});
            skLineSegment(sketch, "E316", {"start": v(-42.63, 9.24) * mm, "end": v(-42.7, 9.16) * mm});
            skLineSegment(sketch, "E317", {"start": v(-42.7, 9.16) * mm, "end": v(-42.73, 9.12) * mm});
            skLineSegment(sketch, "E318", {"start": v(-42.73, 9.12) * mm, "end": v(-42.76, 9.08) * mm});
            skLineSegment(sketch, "E319", {"start": v(-42.76, 9.08) * mm, "end": v(-42.82, 9) * mm});
            skLineSegment(sketch, "E320", {"start": v(-44, 5.16) * mm, "end": v(-44, 5.15) * mm});
            skLineSegment(sketch, "E321", {"start": v(-44, 5.15) * mm, "end": v(-43.98, 5.13) * mm});
            skLineSegment(sketch, "E322", {"start": v(-43.98, 5.13) * mm, "end": v(-43.97, 5.12) * mm});
            skLineSegment(sketch, "E323", {"start": v(-43.97, 5.12) * mm, "end": v(-43.96, 5.11) * mm});
            skLineSegment(sketch, "E324", {"start": v(-43.96, 5.11) * mm, "end": v(-43.95, 5.1) * mm});
            skLineSegment(sketch, "E325", {"start": v(-43.95, 5.1) * mm, "end": v(-43.94, 5.09) * mm});
            skLineSegment(sketch, "E326", {"start": v(-43.94, 5.09) * mm, "end": v(-43.92, 5.08) * mm});
            skLineSegment(sketch, "E327", {"start": v(-43.92, 5.08) * mm, "end": v(-43.9, 5.06) * mm});
            skLineSegment(sketch, "E328", {"start": v(-43.9, 5.06) * mm, "end": v(-43.9, 5.05) * mm});
            skLineSegment(sketch, "E329", {"start": v(-43.9, 5.05) * mm, "end": v(-43.88, 5.04) * mm});
            skLineSegment(sketch, "E330", {"start": v(-43.88, 5.04) * mm, "end": v(-43.86, 5.03) * mm});
            skLineSegment(sketch, "E331", {"start": v(-43.86, 5.03) * mm, "end": v(-43.84, 5.02) * mm});
            skLineSegment(sketch, "E332", {"start": v(-43.84, 5.02) * mm, "end": v(-43.83, 5) * mm});
            skLineSegment(sketch, "E333", {"start": v(-43.83, 5) * mm, "end": v(-43.8, 5) * mm});
            skLineSegment(sketch, "E334", {"start": v(-43.8, 5) * mm, "end": v(-43.79, 4.99) * mm});
            skLineSegment(sketch, "E335", {"start": v(-43.79, 4.99) * mm, "end": v(-43.77, 4.98) * mm});
            skLineSegment(sketch, "E336", {"start": v(-43.77, 4.98) * mm, "end": v(-43.75, 4.97) * mm});
            skLineSegment(sketch, "E337", {"start": v(-43.75, 4.97) * mm, "end": v(-43.73, 4.96) * mm});
            skLineSegment(sketch, "E338", {"start": v(-43.73, 4.96) * mm, "end": v(-43.71, 4.95) * mm});
            skLineSegment(sketch, "E339", {"start": v(-43.71, 4.95) * mm, "end": v(-43.7, 4.94) * mm});
            skLineSegment(sketch, "E340", {"start": v(-43.7, 4.94) * mm, "end": v(-43.67, 4.94) * mm});
            skLineSegment(sketch, "E341", {"start": v(-43.67, 4.94) * mm, "end": v(-43.65, 4.93) * mm});
            skLineSegment(sketch, "E342", {"start": v(-43.65, 4.93) * mm, "end": v(-43.62, 4.92) * mm});
            skLineSegment(sketch, "E343", {"start": v(-43.62, 4.92) * mm, "end": v(-43.6, 4.92) * mm});
            skLineSegment(sketch, "E344", {"start": v(-43.6, 4.92) * mm, "end": v(-43.58, 4.91) * mm});
            skLineSegment(sketch, "E345", {"start": v(-43.58, 4.91) * mm, "end": v(-43.55, 4.9) * mm});
            skLineSegment(sketch, "E346", {"start": v(-43.55, 4.9) * mm, "end": v(-43.53, 4.9) * mm});
            skLineSegment(sketch, "E347", {"start": v(-43.53, 4.9) * mm, "end": v(-43.5, 4.9) * mm});
            skLineSegment(sketch, "E348", {"start": v(-43.5, 4.9) * mm, "end": v(-43.47, 4.9) * mm});
            skLineSegment(sketch, "E349", {"start": v(-43.47, 4.9) * mm, "end": v(-43.44, 4.9) * mm});
            skLineSegment(sketch, "E350", {"start": v(-43.44, 4.9) * mm, "end": v(-43.41, 4.9) * mm});
            skLineSegment(sketch, "E351", {"start": v(-43.41, 4.9) * mm, "end": v(-43.38, 4.89) * mm});
            skLineSegment(sketch, "E352", {"start": v(-43.38, 4.89) * mm, "end": v(-43.35, 4.89) * mm});
            skLineSegment(sketch, "E353", {"start": v(-43.35, 4.89) * mm, "end": v(-43.32, 4.89) * mm});
            skLineSegment(sketch, "E354", {"start": v(-43.32, 4.89) * mm, "end": v(-43.3, 4.89) * mm});
            skLineSegment(sketch, "E355", {"start": v(-32, 3.96) * mm, "end": v(-31.85, 4.15) * mm});
            skLineSegment(sketch, "E356", {"start": v(-31.85, 4.15) * mm, "end": v(-31.71, 4.33) * mm});
            skLineSegment(sketch, "E357", {"start": v(-31.71, 4.33) * mm, "end": v(-31.6, 4.5) * mm});
            skLineSegment(sketch, "E358", {"start": v(-31.6, 4.5) * mm, "end": v(-31.5, 4.63) * mm});
            skLineSegment(sketch, "E359", {"start": v(-33.34, 2.16) * mm, "end": v(-32.5, 3.3) * mm});
            skLineSegment(sketch, "E360", {"start": v(-32.5, 3.3) * mm, "end": v(-32, 3.96) * mm});
            skLineSegment(sketch, "E361", {"start": v(-35.12, -0.16) * mm, "end": v(-34.75, 0.33) * mm});
            skLineSegment(sketch, "E362", {"start": v(-33.76, 1.61) * mm, "end": v(-33.34, 2.16) * mm});
            skLineSegment(sketch, "E363", {"start": v(-34.75, 0.33) * mm, "end": v(-33.76, 1.61) * mm});
            skLineSegment(sketch, "E364", {"start": v(-42.92, -4.72) * mm, "end": v(-42.89, -4.74) * mm});
            skLineSegment(sketch, "E365", {"start": v(-42.89, -4.74) * mm, "end": v(-42.86, -4.76) * mm});
            skLineSegment(sketch, "E366", {"start": v(-42.86, -4.76) * mm, "end": v(-42.82, -4.78) * mm});
            skLineSegment(sketch, "E367", {"start": v(-42.82, -4.78) * mm, "end": v(-42.77, -4.8) * mm});
            skLineSegment(sketch, "E368", {"start": v(-42.77, -4.8) * mm, "end": v(-42.71, -4.83) * mm});
            skLineSegment(sketch, "E369", {"start": v(-42.71, -4.83) * mm, "end": v(-42.64, -4.87) * mm});
            skLineSegment(sketch, "E370", {"start": v(-42.64, -4.87) * mm, "end": v(-42.56, -4.9) * mm});
            skLineSegment(sketch, "E371", {"start": v(-42.56, -4.9) * mm, "end": v(-42.46, -4.95) * mm});
            skLineSegment(sketch, "E372", {"start": v(-42.46, -4.95) * mm, "end": v(-42.35, -5) * mm});
            skLineSegment(sketch, "E373", {"start": v(-42.35, -5) * mm, "end": v(-42.2, -5.06) * mm});
            skLineSegment(sketch, "E374", {"start": v(-42.2, -5.06) * mm, "end": v(-42.04, -5.13) * mm});
            skLineSegment(sketch, "E375", {"start": v(-42.04, -5.13) * mm, "end": v(-41.9, -5.18) * mm});
            skLineSegment(sketch, "E376", {"start": v(-41.9, -5.18) * mm, "end": v(-41.47, -5.36) * mm});
            skLineSegment(sketch, "E377", {"start": v(-22.15, -11.79) * mm, "end": v(-22.15, -11.65) * mm});
            skLineSegment(sketch, "E378", {"start": v(-22.15, -11.65) * mm, "end": v(-22.16, -11.5) * mm});
            skLineSegment(sketch, "E379", {"start": v(-22.16, -11.5) * mm, "end": v(-22.16, -11.36) * mm});
            skLineSegment(sketch, "E380", {"start": v(-22.16, -11.36) * mm, "end": v(-22.16, -11.23) * mm});
            skLineSegment(sketch, "E381", {"start": v(-22.16, -11.23) * mm, "end": v(-22.17, -11.1) * mm});
            skLineSegment(sketch, "E382", {"start": v(-22.17, -11.1) * mm, "end": v(-22.18, -10.98) * mm});
            skLineSegment(sketch, "E383", {"start": v(-22.18, -10.98) * mm, "end": v(-22.18, -10.86) * mm});
            skLineSegment(sketch, "E384", {"start": v(-22.18, -10.86) * mm, "end": v(-22.2, -10.75) * mm});
            skLineSegment(sketch, "E385", {"start": v(-22.2, -10.75) * mm, "end": v(-22.2, -10.64) * mm});
            skLineSegment(sketch, "E386", {"start": v(-22.2, -10.64) * mm, "end": v(-22.21, -10.55) * mm});
            skLineSegment(sketch, "E387", {"start": v(-22.21, -10.55) * mm, "end": v(-22.22, -10.45) * mm});
            skLineSegment(sketch, "E388", {"start": v(-22.22, -10.45) * mm, "end": v(-22.24, -10.37) * mm});
            skLineSegment(sketch, "E389", {"start": v(-22.24, -10.37) * mm, "end": v(-22.25, -10.29) * mm});
            skLineSegment(sketch, "E390", {"start": v(-22.25, -10.29) * mm, "end": v(-22.26, -10.21) * mm});
            skLineSegment(sketch, "E391", {"start": v(-22.26, -10.21) * mm, "end": v(-22.27, -10.14) * mm});
            skLineSegment(sketch, "E392", {"start": v(-22.27, -10.14) * mm, "end": v(-22.29, -10.08) * mm});
            skLineSegment(sketch, "E393", {"start": v(-22.29, -10.08) * mm, "end": v(-22.3, -10.02) * mm});
            skLineSegment(sketch, "E394", {"start": v(-40.95, -1.15) * mm, "end": v(-41.6, -1.6) * mm});
            skLineSegment(sketch, "E395", {"start": v(-23.86, -14.18) * mm, "end": v(-23.76, -14.23) * mm});
            skLineSegment(sketch, "E396", {"start": v(-23.76, -14.23) * mm, "end": v(-23.66, -14.28) * mm});
            skLineSegment(sketch, "E397", {"start": v(-23.66, -14.28) * mm, "end": v(-23.58, -14.31) * mm});
            skLineSegment(sketch, "E398", {"start": v(-23.58, -14.31) * mm, "end": v(-23.5, -14.35) * mm});
            skLineSegment(sketch, "E399", {"start": v(-23.5, -14.35) * mm, "end": v(-23.44, -14.38) * mm});
            skLineSegment(sketch, "E400", {"start": v(-23.44, -14.38) * mm, "end": v(-23.38, -14.4) * mm});
            skLineSegment(sketch, "E401", {"start": v(-23.38, -14.4) * mm, "end": v(-23.33, -14.42) * mm});
            skLineSegment(sketch, "E402", {"start": v(-23.33, -14.42) * mm, "end": v(-23.29, -14.44) * mm});
            skLineSegment(sketch, "E403", {"start": v(-23.29, -14.44) * mm, "end": v(-23.25, -14.46) * mm});
            skLineSegment(sketch, "E404", {"start": v(-23.25, -14.46) * mm, "end": v(-23.21, -14.47) * mm});
            skLineSegment(sketch, "E405", {"start": v(-23.21, -14.47) * mm, "end": v(-23.18, -14.48) * mm});
            skLineSegment(sketch, "E406", {"start": v(-23.18, -14.48) * mm, "end": v(-23.15, -14.49) * mm});
            skLineSegment(sketch, "E407", {"start": v(-23.15, -14.49) * mm, "end": v(-23.13, -14.5) * mm});
            skLineSegment(sketch, "E408", {"start": v(-23.13, -14.5) * mm, "end": v(-23.1, -14.5) * mm});
            skLineSegment(sketch, "E409", {"start": v(-23.1, -14.5) * mm, "end": v(-23.09, -14.5) * mm});
            skLineSegment(sketch, "E410", {"start": v(-23.09, -14.5) * mm, "end": v(-23.07, -14.5) * mm});
            skLineSegment(sketch, "E411", {"start": v(-23.07, -14.5) * mm, "end": v(-23.06, -14.5) * mm});
            skLineSegment(sketch, "E412", {"start": v(-23.06, -14.5) * mm, "end": v(-23.05, -14.5) * mm});
            skLineSegment(sketch, "E413", {"start": v(-39.52, -6.27) * mm, "end": v(-30.73, -10.57) * mm});
            skLineSegment(sketch, "E414", {"start": v(-30.73, -10.57) * mm, "end": v(-29.98, -10.94) * mm});
            skLineSegment(sketch, "E415", {"start": v(-24, -14.11) * mm, "end": v(-23.86, -14.18) * mm});
            skLineSegment(sketch, "E416", {"start": v(-29.98, -10.94) * mm, "end": v(-29.34, -11.26) * mm});
            skLineSegment(sketch, "E417", {"start": v(-29.34, -11.26) * mm, "end": v(-29.05, -11.4) * mm});
            skLineSegment(sketch, "E418", {"start": v(-29.05, -11.4) * mm, "end": v(-28.8, -11.54) * mm});
            skLineSegment(sketch, "E419", {"start": v(-24.51, -13.85) * mm, "end": v(-24.33, -13.94) * mm});
            skLineSegment(sketch, "E420", {"start": v(-24.33, -13.94) * mm, "end": v(-24.16, -14.03) * mm});
            skLineSegment(sketch, "E421", {"start": v(-24.16, -14.03) * mm, "end": v(-24, -14.11) * mm});
            skLineSegment(sketch, "E422", {"start": v(-28.8, -11.54) * mm, "end": v(-28.34, -11.78) * mm});
            skLineSegment(sketch, "E423", {"start": v(-28.34, -11.78) * mm, "end": v(-27.64, -12.15) * mm});
            skLineSegment(sketch, "E424", {"start": v(-24.9, -13.63) * mm, "end": v(-24.51, -13.85) * mm});
            skLineSegment(sketch, "E425", {"start": v(-27.64, -12.15) * mm, "end": v(-26.9, -12.55) * mm});
            skLineSegment(sketch, "E426", {"start": v(-25.35, -13.4) * mm, "end": v(-24.9, -13.63) * mm});
            skLineSegment(sketch, "E427", {"start": v(-26.9, -12.55) * mm, "end": v(-25.35, -13.4) * mm});
            skLineSegment(sketch, "E428", {"start": v(-20.17, -9) * mm, "end": v(-20.13, -9.1) * mm});
            skLineSegment(sketch, "E429", {"start": v(-20.13, -9.1) * mm, "end": v(-20.08, -9.21) * mm});
            skLineSegment(sketch, "E430", {"start": v(-20.08, -9.21) * mm, "end": v(-20.02, -9.33) * mm});
            skLineSegment(sketch, "E431", {"start": v(-20.02, -9.33) * mm, "end": v(-19.97, -9.45) * mm});
            skLineSegment(sketch, "E432", {"start": v(-19.97, -9.45) * mm, "end": v(-19.91, -9.56) * mm});
            skLineSegment(sketch, "E433", {"start": v(-19.91, -9.56) * mm, "end": v(-19.85, -9.68) * mm});
            skLineSegment(sketch, "E434", {"start": v(-19.85, -9.68) * mm, "end": v(-19.8, -9.79) * mm});
            skLineSegment(sketch, "E435", {"start": v(-19.8, -9.79) * mm, "end": v(-19.74, -9.9) * mm});
            skLineSegment(sketch, "E436", {"start": v(-19.74, -9.9) * mm, "end": v(-19.68, -10) * mm});
            skLineSegment(sketch, "E437", {"start": v(-19.68, -10) * mm, "end": v(-19.62, -10.1) * mm});
            skLineSegment(sketch, "E438", {"start": v(-19.62, -10.1) * mm, "end": v(-19.56, -10.2) * mm});
            skLineSegment(sketch, "E439", {"start": v(-19.56, -10.2) * mm, "end": v(-19.5, -10.3) * mm});
            skLineSegment(sketch, "E440", {"start": v(-19.5, -10.3) * mm, "end": v(-19.44, -10.38) * mm});
            skLineSegment(sketch, "E441", {"start": v(-19.44, -10.38) * mm, "end": v(-19.38, -10.47) * mm});
            skLineSegment(sketch, "E442", {"start": v(-19.38, -10.47) * mm, "end": v(-19.31, -10.56) * mm});
            skLineSegment(sketch, "E443", {"start": v(-19.31, -10.56) * mm, "end": v(-19.25, -10.65) * mm});
            skLineSegment(sketch, "E444", {"start": v(-19.25, -10.65) * mm, "end": v(-19.19, -10.73) * mm});
            skLineSegment(sketch, "E445", {"start": v(-19.19, -10.73) * mm, "end": v(-19.13, -10.8) * mm});
            skLineSegment(sketch, "E446", {"start": v(-19.13, -10.8) * mm, "end": v(-19.06, -10.88) * mm});
            skLineSegment(sketch, "E447", {"start": v(-19.06, -10.88) * mm, "end": v(-19, -10.96) * mm});
            skLineSegment(sketch, "E448", {"start": v(-22.3, -10.02) * mm, "end": v(-22.31, -9.99) * mm});
            skLineSegment(sketch, "E449", {"start": v(-22.31, -9.99) * mm, "end": v(-22.32, -9.95) * mm});
            skLineSegment(sketch, "E450", {"start": v(-22.32, -9.95) * mm, "end": v(-22.33, -9.92) * mm});
            skLineSegment(sketch, "E451", {"start": v(-22.33, -9.92) * mm, "end": v(-22.34, -9.88) * mm});
            skLineSegment(sketch, "E452", {"start": v(-22.34, -9.88) * mm, "end": v(-22.35, -9.85) * mm});
            skLineSegment(sketch, "E453", {"start": v(-22.35, -9.85) * mm, "end": v(-22.37, -9.82) * mm});
            skLineSegment(sketch, "E454", {"start": v(-22.37, -9.82) * mm, "end": v(-22.38, -9.79) * mm});
            skLineSegment(sketch, "E455", {"start": v(-22.38, -9.79) * mm, "end": v(-22.4, -9.75) * mm});
            skLineSegment(sketch, "E456", {"start": v(-22.4, -9.75) * mm, "end": v(-22.41, -9.72) * mm});
            skLineSegment(sketch, "E457", {"start": v(-22.41, -9.72) * mm, "end": v(-22.43, -9.7) * mm});
            skLineSegment(sketch, "E458", {"start": v(-22.43, -9.7) * mm, "end": v(-22.44, -9.66) * mm});
            skLineSegment(sketch, "E459", {"start": v(-22.44, -9.66) * mm, "end": v(-22.46, -9.63) * mm});
            skLineSegment(sketch, "E460", {"start": v(-22.46, -9.63) * mm, "end": v(-22.48, -9.6) * mm});
            skLineSegment(sketch, "E461", {"start": v(-22.48, -9.6) * mm, "end": v(-22.5, -9.57) * mm});
            skLineSegment(sketch, "E462", {"start": v(-22.5, -9.57) * mm, "end": v(-22.52, -9.54) * mm});
            skLineSegment(sketch, "E463", {"start": v(-22.52, -9.54) * mm, "end": v(-22.54, -9.51) * mm});
            skLineSegment(sketch, "E464", {"start": v(-22.54, -9.51) * mm, "end": v(-22.56, -9.48) * mm});
            skLineSegment(sketch, "E465", {"start": v(-22.56, -9.48) * mm, "end": v(-22.58, -9.45) * mm});
            skLineSegment(sketch, "E466", {"start": v(-22.58, -9.45) * mm, "end": v(-22.6, -9.43) * mm});
            skLineSegment(sketch, "E467", {"start": v(-22.6, -9.43) * mm, "end": v(-22.62, -9.4) * mm});
            skLineSegment(sketch, "E468", {"start": v(-22.62, -9.4) * mm, "end": v(-22.65, -9.37) * mm});
            skLineSegment(sketch, "E469", {"start": v(-22.65, -9.37) * mm, "end": v(-22.67, -9.34) * mm});
            skLineSegment(sketch, "E470", {"start": v(-22.67, -9.34) * mm, "end": v(-22.7, -9.32) * mm});
            skLineSegment(sketch, "E471", {"start": v(-22.7, -9.32) * mm, "end": v(-22.73, -9.29) * mm});
            skLineSegment(sketch, "E472", {"start": v(-22.73, -9.29) * mm, "end": v(-22.76, -9.26) * mm});
            skLineSegment(sketch, "E473", {"start": v(-22.76, -9.26) * mm, "end": v(-22.78, -9.24) * mm});
            skLineSegment(sketch, "E474", {"start": v(-22.78, -9.24) * mm, "end": v(-22.81, -9.2) * mm});
            skLineSegment(sketch, "E475", {"start": v(-22.81, -9.2) * mm, "end": v(-22.85, -9.18) * mm});
            skLineSegment(sketch, "E476", {"start": v(-22.85, -9.18) * mm, "end": v(-22.88, -9.16) * mm});
            skLineSegment(sketch, "E477", {"start": v(-20.66, -6.5) * mm, "end": v(-20.66, -6.57) * mm});
            skLineSegment(sketch, "E478", {"start": v(-20.66, -6.57) * mm, "end": v(-20.66, -6.69) * mm});
            skLineSegment(sketch, "E479", {"start": v(-20.66, -6.69) * mm, "end": v(-20.66, -6.8) * mm});
            skLineSegment(sketch, "E480", {"start": v(-20.66, -6.8) * mm, "end": v(-20.65, -6.93) * mm});
            skLineSegment(sketch, "E481", {"start": v(-20.65, -6.93) * mm, "end": v(-20.64, -7.04) * mm});
            skLineSegment(sketch, "E482", {"start": v(-20.64, -7.04) * mm, "end": v(-20.63, -7.16) * mm});
            skLineSegment(sketch, "E483", {"start": v(-20.63, -7.16) * mm, "end": v(-20.62, -7.27) * mm});
            skLineSegment(sketch, "E484", {"start": v(-20.62, -7.27) * mm, "end": v(-20.6, -7.39) * mm});
            skLineSegment(sketch, "E485", {"start": v(-20.6, -7.39) * mm, "end": v(-20.6, -7.5) * mm});
            skLineSegment(sketch, "E486", {"start": v(-20.6, -7.5) * mm, "end": v(-20.57, -7.61) * mm});
            skLineSegment(sketch, "E487", {"start": v(-20.57, -7.61) * mm, "end": v(-20.55, -7.72) * mm});
            skLineSegment(sketch, "E488", {"start": v(-20.55, -7.72) * mm, "end": v(-20.53, -7.84) * mm});
            skLineSegment(sketch, "E489", {"start": v(-20.53, -7.84) * mm, "end": v(-20.5, -7.95) * mm});
            skLineSegment(sketch, "E490", {"start": v(-20.5, -7.95) * mm, "end": v(-20.48, -8.05) * mm});
            skLineSegment(sketch, "E491", {"start": v(-20.48, -8.05) * mm, "end": v(-20.46, -8.16) * mm});
            skLineSegment(sketch, "E492", {"start": v(-20.46, -8.16) * mm, "end": v(-20.43, -8.27) * mm});
            skLineSegment(sketch, "E493", {"start": v(-20.43, -8.27) * mm, "end": v(-20.4, -8.38) * mm});
            skLineSegment(sketch, "E494", {"start": v(-20.4, -8.38) * mm, "end": v(-20.36, -8.48) * mm});
            skLineSegment(sketch, "E495", {"start": v(-20.36, -8.48) * mm, "end": v(-20.33, -8.6) * mm});
            skLineSegment(sketch, "E496", {"start": v(-20.33, -8.6) * mm, "end": v(-20.3, -8.7) * mm});
            skLineSegment(sketch, "E497", {"start": v(-20.3, -8.7) * mm, "end": v(-20.25, -8.8) * mm});
            skLineSegment(sketch, "E498", {"start": v(-20.25, -8.8) * mm, "end": v(-20.21, -8.9) * mm});
            skLineSegment(sketch, "E499", {"start": v(-20.21, -8.9) * mm, "end": v(-20.17, -9) * mm});
            skLineSegment(sketch, "E500", {"start": v(-19.31, 6.14) * mm, "end": v(-19.32, 6.09) * mm});
            skLineSegment(sketch, "E501", {"start": v(-19.32, 6.09) * mm, "end": v(-19.32, 6.04) * mm});
            skLineSegment(sketch, "E502", {"start": v(-19.32, 6.04) * mm, "end": v(-19.32, 5.99) * mm});
            skLineSegment(sketch, "E503", {"start": v(-19.32, 5.99) * mm, "end": v(-19.33, 5.94) * mm});
            skLineSegment(sketch, "E504", {"start": v(-19.33, 5.94) * mm, "end": v(-19.33, 5.89) * mm});
            skLineSegment(sketch, "E505", {"start": v(-19.33, 5.89) * mm, "end": v(-19.34, 5.84) * mm});
            skLineSegment(sketch, "E506", {"start": v(-19.34, 5.84) * mm, "end": v(-19.35, 5.79) * mm});
            skLineSegment(sketch, "E507", {"start": v(-19.35, 5.79) * mm, "end": v(-19.37, 5.74) * mm});
            skLineSegment(sketch, "E508", {"start": v(-19.37, 5.74) * mm, "end": v(-19.38, 5.69) * mm});
            skLineSegment(sketch, "E509", {"start": v(-19.38, 5.69) * mm, "end": v(-19.4, 5.64) * mm});
            skLineSegment(sketch, "E510", {"start": v(-19.4, 5.64) * mm, "end": v(-19.41, 5.59) * mm});
            skLineSegment(sketch, "E511", {"start": v(-19.41, 5.59) * mm, "end": v(-19.43, 5.54) * mm});
            skLineSegment(sketch, "E512", {"start": v(-19.43, 5.54) * mm, "end": v(-19.45, 5.48) * mm});
            skLineSegment(sketch, "E513", {"start": v(-19.45, 5.48) * mm, "end": v(-19.47, 5.43) * mm});
            skLineSegment(sketch, "E514", {"start": v(-19.47, 5.43) * mm, "end": v(-19.5, 5.38) * mm});
            skLineSegment(sketch, "E515", {"start": v(-19.5, 5.38) * mm, "end": v(-19.52, 5.33) * mm});
            skLineSegment(sketch, "E516", {"start": v(-19.52, 5.33) * mm, "end": v(-19.55, 5.28) * mm});
            skLineSegment(sketch, "E517", {"start": v(-19.55, 5.28) * mm, "end": v(-19.58, 5.23) * mm});
            skLineSegment(sketch, "E518", {"start": v(-19.58, 5.23) * mm, "end": v(-19.61, 5.17) * mm});
            skLineSegment(sketch, "E519", {"start": v(-19.61, 5.17) * mm, "end": v(-19.65, 5.12) * mm});
            skLineSegment(sketch, "E520", {"start": v(-19.65, 5.12) * mm, "end": v(-19.68, 5.07) * mm});
            skLineSegment(sketch, "E521", {"start": v(-19.68, 5.07) * mm, "end": v(-19.72, 5.01) * mm});
            skLineSegment(sketch, "E522", {"start": v(-19.72, 5.01) * mm, "end": v(-19.76, 4.96) * mm});
            skLineSegment(sketch, "E523", {"start": v(-19.76, 4.96) * mm, "end": v(-19.8, 4.9) * mm});
            skLineSegment(sketch, "E524", {"start": v(-19.8, 4.9) * mm, "end": v(-19.85, 4.85) * mm});
            skLineSegment(sketch, "E525", {"start": v(-19.85, 4.85) * mm, "end": v(-19.9, 4.8) * mm});
            skLineSegment(sketch, "E526", {"start": v(-19.9, 4.8) * mm, "end": v(-19.95, 4.74) * mm});
            skLineSegment(sketch, "E527", {"start": v(-19.95, 4.74) * mm, "end": v(-20, 4.68) * mm});
            skLineSegment(sketch, "E528", {"start": v(-20, 4.68) * mm, "end": v(-20.06, 4.62) * mm});
            skLineSegment(sketch, "E529", {"start": v(-20.06, 4.62) * mm, "end": v(-20.11, 4.57) * mm});
            skLineSegment(sketch, "E530", {"start": v(-20.11, 4.57) * mm, "end": v(-20.18, 4.51) * mm});
            skLineSegment(sketch, "E531", {"start": v(-20.18, 4.51) * mm, "end": v(-20.24, 4.45) * mm});
            skLineSegment(sketch, "E532", {"start": v(-20.24, 4.45) * mm, "end": v(-20.29, 4.4) * mm});
            skLineSegment(sketch, "E533", {"start": v(-37.24, 5.12) * mm, "end": v(-36.74, 5.36) * mm});
            skLineSegment(sketch, "E534", {"start": v(-38.1, 11.68) * mm, "end": v(-38.19, 11.65) * mm});
            skLineSegment(sketch, "E535", {"start": v(-38.19, 11.65) * mm, "end": v(-38.45, 11.57) * mm});
            skLineSegment(sketch, "E536", {"start": v(-38.45, 11.57) * mm, "end": v(-38.7, 11.5) * mm});
            skLineSegment(sketch, "E537", {"start": v(-38.7, 11.5) * mm, "end": v(-38.94, 11.41) * mm});
            skLineSegment(sketch, "E538", {"start": v(-38.94, 11.41) * mm, "end": v(-39.16, 11.34) * mm});
            skLineSegment(sketch, "E539", {"start": v(-39.16, 11.34) * mm, "end": v(-39.38, 11.26) * mm});
            skLineSegment(sketch, "E540", {"start": v(-39.38, 11.26) * mm, "end": v(-39.59, 11.19) * mm});
            skLineSegment(sketch, "E541", {"start": v(-39.59, 11.19) * mm, "end": v(-39.78, 11.11) * mm});
            skLineSegment(sketch, "E542", {"start": v(-39.78, 11.11) * mm, "end": v(-39.97, 11.04) * mm});
            skLineSegment(sketch, "E543", {"start": v(-39.97, 11.04) * mm, "end": v(-40.14, 10.97) * mm});
            skLineSegment(sketch, "E544", {"start": v(-40.14, 10.97) * mm, "end": v(-40.3, 10.9) * mm});
            skLineSegment(sketch, "E545", {"start": v(-40.3, 10.9) * mm, "end": v(-40.47, 10.83) * mm});
            skLineSegment(sketch, "E546", {"start": v(-40.47, 10.83) * mm, "end": v(-40.61, 10.76) * mm});
            skLineSegment(sketch, "E547", {"start": v(-40.61, 10.76) * mm, "end": v(-40.75, 10.7) * mm});
            skLineSegment(sketch, "E548", {"start": v(-40.75, 10.7) * mm, "end": v(-40.88, 10.63) * mm});
            skLineSegment(sketch, "E549", {"start": v(-40.88, 10.63) * mm, "end": v(-41, 10.57) * mm});
            skLineSegment(sketch, "E550", {"start": v(-41, 10.57) * mm, "end": v(-41.12, 10.5) * mm});
            skLineSegment(sketch, "E551", {"start": v(-41.12, 10.5) * mm, "end": v(-41.23, 10.44) * mm});
            skLineSegment(sketch, "E552", {"start": v(-22.88, -9.16) * mm, "end": v(-22.92, -9.12) * mm});
            skLineSegment(sketch, "E553", {"start": v(-22.92, -9.12) * mm, "end": v(-22.98, -9.08) * mm});
            skLineSegment(sketch, "E554", {"start": v(-22.98, -9.08) * mm, "end": v(-23.04, -9.04) * mm});
            skLineSegment(sketch, "E555", {"start": v(-23.04, -9.04) * mm, "end": v(-23.11, -9) * mm});
            skLineSegment(sketch, "E556", {"start": v(-23.11, -9) * mm, "end": v(-23.2, -8.94) * mm});
            skLineSegment(sketch, "E557", {"start": v(-23.2, -8.94) * mm, "end": v(-23.3, -8.87) * mm});
            skLineSegment(sketch, "E558", {"start": v(-23.3, -8.87) * mm, "end": v(-23.41, -8.8) * mm});
            skLineSegment(sketch, "E559", {"start": v(-23.41, -8.8) * mm, "end": v(-23.55, -8.73) * mm});
            skLineSegment(sketch, "E560", {"start": v(-23.55, -8.73) * mm, "end": v(-23.7, -8.64) * mm});
            skLineSegment(sketch, "E561", {"start": v(-23.7, -8.64) * mm, "end": v(-23.88, -8.54) * mm});
            skLineSegment(sketch, "E562", {"start": v(-23.88, -8.54) * mm, "end": v(-24.08, -8.43) * mm});
            skLineSegment(sketch, "E563", {"start": v(-24.08, -8.43) * mm, "end": v(-24.32, -8.3) * mm});
            skLineSegment(sketch, "E564", {"start": v(-24.32, -8.3) * mm, "end": v(-24.76, -8.06) * mm});
            skLineSegment(sketch, "E565", {"start": v(-19, -10.96) * mm, "end": v(-18.98, -10.98) * mm});
            skLineSegment(sketch, "E566", {"start": v(-18.98, -10.98) * mm, "end": v(-18.93, -11.04) * mm});
            skLineSegment(sketch, "E567", {"start": v(-18.93, -11.04) * mm, "end": v(-18.88, -11.09) * mm});
            skLineSegment(sketch, "E568", {"start": v(-18.88, -11.09) * mm, "end": v(-18.84, -11.14) * mm});
            skLineSegment(sketch, "E569", {"start": v(-18.84, -11.14) * mm, "end": v(-18.8, -11.19) * mm});
            skLineSegment(sketch, "E570", {"start": v(-18.8, -11.19) * mm, "end": v(-18.75, -11.23) * mm});
            skLineSegment(sketch, "E571", {"start": v(-18.75, -11.23) * mm, "end": v(-18.7, -11.28) * mm});
            skLineSegment(sketch, "E572", {"start": v(-18.7, -11.28) * mm, "end": v(-18.66, -11.32) * mm});
            skLineSegment(sketch, "E573", {"start": v(-18.66, -11.32) * mm, "end": v(-18.62, -11.35) * mm});
            skLineSegment(sketch, "E574", {"start": v(-18.62, -11.35) * mm, "end": v(-18.58, -11.39) * mm});
            skLineSegment(sketch, "E575", {"start": v(-18.58, -11.39) * mm, "end": v(-18.54, -11.42) * mm});
            skLineSegment(sketch, "E576", {"start": v(-18.54, -11.42) * mm, "end": v(-18.5, -11.45) * mm});
            skLineSegment(sketch, "E577", {"start": v(-18.5, -11.45) * mm, "end": v(-18.46, -11.48) * mm});
            skLineSegment(sketch, "E578", {"start": v(-18.46, -11.48) * mm, "end": v(-18.43, -11.5) * mm});
            skLineSegment(sketch, "E579", {"start": v(-18.43, -11.5) * mm, "end": v(-18.4, -11.53) * mm});
            skLineSegment(sketch, "E580", {"start": v(-18.4, -11.53) * mm, "end": v(-18.36, -11.55) * mm});
            skLineSegment(sketch, "E581", {"start": v(-18.36, -11.55) * mm, "end": v(-18.33, -11.57) * mm});
            skLineSegment(sketch, "E582", {"start": v(-18.33, -11.57) * mm, "end": v(-18.3, -11.6) * mm});
            skLineSegment(sketch, "E583", {"start": v(-18.3, -11.6) * mm, "end": v(-18.26, -11.6) * mm});
            skLineSegment(sketch, "E584", {"start": v(-18.26, -11.6) * mm, "end": v(-18.23, -11.62) * mm});
            skLineSegment(sketch, "E585", {"start": v(-18.23, -11.62) * mm, "end": v(-18.2, -11.64) * mm});
            skLineSegment(sketch, "E586", {"start": v(-18.2, -11.64) * mm, "end": v(-18.17, -11.65) * mm});
            skLineSegment(sketch, "E587", {"start": v(-18.17, -11.65) * mm, "end": v(-18.14, -11.66) * mm});
            skLineSegment(sketch, "E588", {"start": v(-18.14, -11.66) * mm, "end": v(-18.11, -11.67) * mm});
            skLineSegment(sketch, "E589", {"start": v(-18.11, -11.67) * mm, "end": v(-18.09, -11.68) * mm});
            skLineSegment(sketch, "E590", {"start": v(-18.09, -11.68) * mm, "end": v(-18.06, -11.69) * mm});
            skLineSegment(sketch, "E591", {"start": v(-18.06, -11.69) * mm, "end": v(-18.03, -11.7) * mm});
            skLineSegment(sketch, "E592", {"start": v(-18.03, -11.7) * mm, "end": v(-18, -11.7) * mm});
            skLineSegment(sketch, "E593", {"start": v(-18, -11.7) * mm, "end": v(-17.98, -11.7) * mm});
            skLineSegment(sketch, "E594", {"start": v(-17.98, -11.7) * mm, "end": v(-17.95, -11.7) * mm});
            skLineSegment(sketch, "E595", {"start": v(-17.95, -11.7) * mm, "end": v(-17.93, -11.7) * mm});
            skLineSegment(sketch, "E596", {"start": v(-17.93, -11.7) * mm, "end": v(-17.9, -11.7) * mm});
            skLineSegment(sketch, "E597", {"start": v(-17.97, -8.22) * mm, "end": v(-17.99, -8.19) * mm});
            skLineSegment(sketch, "E598", {"start": v(-17.99, -8.19) * mm, "end": v(-18, -8.16) * mm});
            skLineSegment(sketch, "E599", {"start": v(-18, -8.16) * mm, "end": v(-18.02, -8.12) * mm});
            skLineSegment(sketch, "E600", {"start": v(-18.02, -8.12) * mm, "end": v(-18.03, -8.1) * mm});
            skLineSegment(sketch, "E601", {"start": v(-18.03, -8.1) * mm, "end": v(-18.05, -8.06) * mm});
            skLineSegment(sketch, "E602", {"start": v(-18.05, -8.06) * mm, "end": v(-18.06, -8.02) * mm});
            skLineSegment(sketch, "E603", {"start": v(-18.06, -8.02) * mm, "end": v(-18.07, -7.99) * mm});
            skLineSegment(sketch, "E604", {"start": v(-18.07, -7.99) * mm, "end": v(-18.08, -7.95) * mm});
            skLineSegment(sketch, "E605", {"start": v(-18.08, -7.95) * mm, "end": v(-18.1, -7.91) * mm});
            skLineSegment(sketch, "E606", {"start": v(-18.1, -7.91) * mm, "end": v(-18.1, -7.88) * mm});
            skLineSegment(sketch, "E607", {"start": v(-18.1, -7.88) * mm, "end": v(-18.11, -7.84) * mm});
            skLineSegment(sketch, "E608", {"start": v(-18.11, -7.84) * mm, "end": v(-18.12, -7.8) * mm});
            skLineSegment(sketch, "E609", {"start": v(-18.12, -7.8) * mm, "end": v(-18.13, -7.76) * mm});
            skLineSegment(sketch, "E610", {"start": v(-18.13, -7.76) * mm, "end": v(-18.14, -7.72) * mm});
            skLineSegment(sketch, "E611", {"start": v(-18.14, -7.72) * mm, "end": v(-18.15, -7.67) * mm});
            skLineSegment(sketch, "E612", {"start": v(-18.15, -7.67) * mm, "end": v(-18.15, -7.63) * mm});
            skLineSegment(sketch, "E613", {"start": v(-18.15, -7.63) * mm, "end": v(-18.16, -7.58) * mm});
            skLineSegment(sketch, "E614", {"start": v(-18.16, -7.58) * mm, "end": v(-18.17, -7.53) * mm});
            skLineSegment(sketch, "E615", {"start": v(-18.17, -7.53) * mm, "end": v(-18.17, -7.48) * mm});
            skLineSegment(sketch, "E616", {"start": v(-18.17, -7.48) * mm, "end": v(-18.17, -7.43) * mm});
            skLineSegment(sketch, "E617", {"start": v(-18.17, -7.43) * mm, "end": v(-18.18, -7.38) * mm});
            skLineSegment(sketch, "E618", {"start": v(-18.18, -7.38) * mm, "end": v(-18.18, -7.32) * mm});
            skLineSegment(sketch, "E619", {"start": v(-18.18, -7.32) * mm, "end": v(-18.18, -7.27) * mm});
            skLineSegment(sketch, "E620", {"start": v(-18.18, -7.27) * mm, "end": v(-18.18, -7.2) * mm});
            skLineSegment(sketch, "E621", {"start": v(-18.18, -7.2) * mm, "end": v(-18.18, -7.16) * mm});
            skLineSegment(sketch, "E622", {"start": v(-16.83, 7.49) * mm, "end": v(-16.83, 7.58) * mm});
            skLineSegment(sketch, "E623", {"start": v(-16.83, 7.58) * mm, "end": v(-16.84, 7.63) * mm});
            skLineSegment(sketch, "E624", {"start": v(-16.84, 7.63) * mm, "end": v(-16.84, 7.68) * mm});
            skLineSegment(sketch, "E625", {"start": v(-16.84, 7.68) * mm, "end": v(-16.84, 7.77) * mm});
            skLineSegment(sketch, "E626", {"start": v(-16.84, 7.77) * mm, "end": v(-16.85, 7.87) * mm});
            skLineSegment(sketch, "E627", {"start": v(-16.85, 7.87) * mm, "end": v(-16.86, 7.96) * mm});
            skLineSegment(sketch, "E628", {"start": v(-16.86, 7.96) * mm, "end": v(-16.87, 8.05) * mm});
            skLineSegment(sketch, "E629", {"start": v(-16.87, 8.05) * mm, "end": v(-16.89, 8.15) * mm});
            skLineSegment(sketch, "E630", {"start": v(-16.89, 8.15) * mm, "end": v(-16.9, 8.24) * mm});
            skLineSegment(sketch, "E631", {"start": v(-16.9, 8.24) * mm, "end": v(-16.92, 8.33) * mm});
            skLineSegment(sketch, "E632", {"start": v(-16.92, 8.33) * mm, "end": v(-16.95, 8.42) * mm});
            skLineSegment(sketch, "E633", {"start": v(-16.95, 8.42) * mm, "end": v(-16.97, 8.51) * mm});
            skLineSegment(sketch, "E634", {"start": v(-16.97, 8.51) * mm, "end": v(-17, 8.6) * mm});
            skLineSegment(sketch, "E635", {"start": v(-17, 8.6) * mm, "end": v(-17.02, 8.7) * mm});
            skLineSegment(sketch, "E636", {"start": v(-17.02, 8.7) * mm, "end": v(-17.05, 8.79) * mm});
            skLineSegment(sketch, "E637", {"start": v(-17.05, 8.79) * mm, "end": v(-17.09, 8.88) * mm});
            skLineSegment(sketch, "E638", {"start": v(-17.09, 8.88) * mm, "end": v(-17.12, 8.97) * mm});
            skLineSegment(sketch, "E639", {"start": v(-17.12, 8.97) * mm, "end": v(-17.16, 9.06) * mm});
            skLineSegment(sketch, "E640", {"start": v(-17.16, 9.06) * mm, "end": v(-17.2, 9.15) * mm});
            skLineSegment(sketch, "E641", {"start": v(-17.2, 9.15) * mm, "end": v(-17.24, 9.24) * mm});
            skLineSegment(sketch, "E642", {"start": v(-17.24, 9.24) * mm, "end": v(-17.28, 9.33) * mm});
            skLineSegment(sketch, "E643", {"start": v(-17.28, 9.33) * mm, "end": v(-17.33, 9.42) * mm});
            skLineSegment(sketch, "E644", {"start": v(-17.33, 9.42) * mm, "end": v(-17.38, 9.5) * mm});
            skLineSegment(sketch, "E645", {"start": v(-17.38, 9.5) * mm, "end": v(-17.43, 9.6) * mm});
            skLineSegment(sketch, "E646", {"start": v(-17.43, 9.6) * mm, "end": v(-17.49, 9.69) * mm});
            skLineSegment(sketch, "E647", {"start": v(-17.49, 9.69) * mm, "end": v(-17.54, 9.77) * mm});
            skLineSegment(sketch, "E648", {"start": v(-17.54, 9.77) * mm, "end": v(-17.6, 9.86) * mm});
            skLineSegment(sketch, "E649", {"start": v(-17.6, 9.86) * mm, "end": v(-17.67, 9.95) * mm});
            skLineSegment(sketch, "E650", {"start": v(-17.67, 9.95) * mm, "end": v(-17.73, 10.04) * mm});
            skLineSegment(sketch, "E651", {"start": v(-17.73, 10.04) * mm, "end": v(-17.8, 10.13) * mm});
            skLineSegment(sketch, "E652", {"start": v(-17.8, 10.13) * mm, "end": v(-17.81, 10.14) * mm});
            skLineSegment(sketch, "E653", {"start": v(-18.18, -7.16) * mm, "end": v(-18.18, -7.07) * mm});
            skLineSegment(sketch, "E654", {"start": v(-18.18, -7.07) * mm, "end": v(-18.18, -6.97) * mm});
            skLineSegment(sketch, "E655", {"start": v(-18.18, -6.97) * mm, "end": v(-18.17, -6.93) * mm});
            skLineSegment(sketch, "E656", {"start": v(-18.17, -6.93) * mm, "end": v(-18.17, -6.88) * mm});
            skLineSegment(sketch, "E657", {"start": v(-18.17, -6.88) * mm, "end": v(-18.16, -6.79) * mm});
            skLineSegment(sketch, "E658", {"start": v(-18.16, -6.79) * mm, "end": v(-18.14, -6.7) * mm});
            skLineSegment(sketch, "E659", {"start": v(-18.14, -6.7) * mm, "end": v(-18.12, -6.6) * mm});
            skLineSegment(sketch, "E660", {"start": v(-18.12, -6.6) * mm, "end": v(-18.1, -6.5) * mm});
            skLineSegment(sketch, "E661", {"start": v(-18.1, -6.5) * mm, "end": v(-18.08, -6.4) * mm});
            skLineSegment(sketch, "E662", {"start": v(-18.08, -6.4) * mm, "end": v(-18.05, -6.31) * mm});
            skLineSegment(sketch, "E663", {"start": v(-18.05, -6.31) * mm, "end": v(-18.02, -6.22) * mm});
            skLineSegment(sketch, "E664", {"start": v(-18.02, -6.22) * mm, "end": v(-17.99, -6.12) * mm});
            skLineSegment(sketch, "E665", {"start": v(-17.99, -6.12) * mm, "end": v(-17.95, -6.03) * mm});
            skLineSegment(sketch, "E666", {"start": v(-17.95, -6.03) * mm, "end": v(-17.9, -5.93) * mm});
            skLineSegment(sketch, "E667", {"start": v(-17.9, -5.93) * mm, "end": v(-17.86, -5.84) * mm});
            skLineSegment(sketch, "E668", {"start": v(-17.86, -5.84) * mm, "end": v(-17.8, -5.74) * mm});
            skLineSegment(sketch, "E669", {"start": v(-17.8, -5.74) * mm, "end": v(-17.76, -5.64) * mm});
            skLineSegment(sketch, "E670", {"start": v(-17.76, -5.64) * mm, "end": v(-17.7, -5.54) * mm});
            skLineSegment(sketch, "E671", {"start": v(-17.7, -5.54) * mm, "end": v(-17.64, -5.45) * mm});
            skLineSegment(sketch, "E672", {"start": v(-17.64, -5.45) * mm, "end": v(-17.57, -5.35) * mm});
            skLineSegment(sketch, "E673", {"start": v(-17.57, -5.35) * mm, "end": v(-17.5, -5.25) * mm});
            skLineSegment(sketch, "E674", {"start": v(-17.5, -5.25) * mm, "end": v(-17.43, -5.15) * mm});
            skLineSegment(sketch, "E675", {"start": v(-17.43, -5.15) * mm, "end": v(-17.35, -5.05) * mm});
            skLineSegment(sketch, "E676", {"start": v(-17.35, -5.05) * mm, "end": v(-17.27, -4.95) * mm});
            skLineSegment(sketch, "E677", {"start": v(-17.27, -4.95) * mm, "end": v(-17.18, -4.84) * mm});
            skLineSegment(sketch, "E678", {"start": v(-17.18, -4.84) * mm, "end": v(-17.08, -4.74) * mm});
            skLineSegment(sketch, "E679", {"start": v(-17.08, -4.74) * mm, "end": v(-16.99, -4.64) * mm});
            skLineSegment(sketch, "E680", {"start": v(-16.99, -4.64) * mm, "end": v(-16.88, -4.53) * mm});
            skLineSegment(sketch, "E681", {"start": v(-16.88, -4.53) * mm, "end": v(-16.77, -4.43) * mm});
            skLineSegment(sketch, "E682", {"start": v(-16.77, -4.43) * mm, "end": v(-16.66, -4.32) * mm});
            skLineSegment(sketch, "E683", {"start": v(-16.66, -4.32) * mm, "end": v(-16.54, -4.21) * mm});
            skLineSegment(sketch, "E684", {"start": v(-16.54, -4.21) * mm, "end": v(-16.41, -4.1) * mm});
            skLineSegment(sketch, "E685", {"start": v(-16.41, -4.1) * mm, "end": v(-16.28, -4) * mm});
            skLineSegment(sketch, "E686", {"start": v(-16.28, -4) * mm, "end": v(-16.14, -3.89) * mm});
            skLineSegment(sketch, "E687", {"start": v(-16.14, -3.89) * mm, "end": v(-16, -3.78) * mm});
            skLineSegment(sketch, "E688", {"start": v(-16, -3.78) * mm, "end": v(-16, -3.77) * mm});
            skLineSegment(sketch, "E689", {"start": v(-22.33, -13.83) * mm, "end": v(-22.32, -13.77) * mm});
            skLineSegment(sketch, "E690", {"start": v(-22.32, -13.77) * mm, "end": v(-22.3, -13.7) * mm});
            skLineSegment(sketch, "E691", {"start": v(-22.3, -13.7) * mm, "end": v(-22.28, -13.63) * mm});
            skLineSegment(sketch, "E692", {"start": v(-22.28, -13.63) * mm, "end": v(-22.27, -13.55) * mm});
            skLineSegment(sketch, "E693", {"start": v(-22.27, -13.55) * mm, "end": v(-22.25, -13.46) * mm});
            skLineSegment(sketch, "E694", {"start": v(-22.25, -13.46) * mm, "end": v(-22.24, -13.37) * mm});
            skLineSegment(sketch, "E695", {"start": v(-22.24, -13.37) * mm, "end": v(-22.23, -13.28) * mm});
            skLineSegment(sketch, "E696", {"start": v(-22.23, -13.28) * mm, "end": v(-22.22, -13.17) * mm});
            skLineSegment(sketch, "E697", {"start": v(-22.22, -13.17) * mm, "end": v(-22.2, -13.06) * mm});
            skLineSegment(sketch, "E698", {"start": v(-22.2, -13.06) * mm, "end": v(-22.2, -12.94) * mm});
            skLineSegment(sketch, "E699", {"start": v(-22.2, -12.94) * mm, "end": v(-22.18, -12.82) * mm});
            skLineSegment(sketch, "E700", {"start": v(-22.18, -12.82) * mm, "end": v(-22.18, -12.68) * mm});
            skLineSegment(sketch, "E701", {"start": v(-22.18, -12.68) * mm, "end": v(-22.17, -12.54) * mm});
            skLineSegment(sketch, "E702", {"start": v(-22.17, -12.54) * mm, "end": v(-22.16, -12.4) * mm});
            skLineSegment(sketch, "E703", {"start": v(-22.16, -12.4) * mm, "end": v(-22.16, -12.24) * mm});
            skLineSegment(sketch, "E704", {"start": v(-22.16, -12.24) * mm, "end": v(-22.15, -12.07) * mm});
            skLineSegment(sketch, "E705", {"start": v(-22.15, -12.07) * mm, "end": v(-22.15, -11.9) * mm});
            skLineSegment(sketch, "E706", {"start": v(-22.15, -11.9) * mm, "end": v(-22.15, -11.79) * mm});
            skLineSegment(sketch, "E707", {"start": v(-20.49, -4.96) * mm, "end": v(-20.5, -5.02) * mm});
            skLineSegment(sketch, "E708", {"start": v(-20.5, -5.02) * mm, "end": v(-20.52, -5.09) * mm});
            skLineSegment(sketch, "E709", {"start": v(-20.52, -5.09) * mm, "end": v(-20.54, -5.15) * mm});
            skLineSegment(sketch, "E710", {"start": v(-20.54, -5.15) * mm, "end": v(-20.55, -5.22) * mm});
            skLineSegment(sketch, "E711", {"start": v(-20.55, -5.22) * mm, "end": v(-20.56, -5.3) * mm});
            skLineSegment(sketch, "E712", {"start": v(-20.56, -5.3) * mm, "end": v(-20.58, -5.37) * mm});
            skLineSegment(sketch, "E713", {"start": v(-20.58, -5.37) * mm, "end": v(-20.6, -5.44) * mm});
            skLineSegment(sketch, "E714", {"start": v(-20.6, -5.44) * mm, "end": v(-20.6, -5.52) * mm});
            skLineSegment(sketch, "E715", {"start": v(-20.6, -5.52) * mm, "end": v(-20.61, -5.6) * mm});
            skLineSegment(sketch, "E716", {"start": v(-20.61, -5.6) * mm, "end": v(-20.62, -5.69) * mm});
            skLineSegment(sketch, "E717", {"start": v(-20.62, -5.69) * mm, "end": v(-20.63, -5.77) * mm});
            skLineSegment(sketch, "E718", {"start": v(-20.63, -5.77) * mm, "end": v(-20.64, -5.86) * mm});
            skLineSegment(sketch, "E719", {"start": v(-20.64, -5.86) * mm, "end": v(-20.65, -5.95) * mm});
            skLineSegment(sketch, "E720", {"start": v(-20.65, -5.95) * mm, "end": v(-20.65, -6.04) * mm});
            skLineSegment(sketch, "E721", {"start": v(-20.65, -6.04) * mm, "end": v(-20.66, -6.14) * mm});
            skLineSegment(sketch, "E722", {"start": v(-20.66, -6.14) * mm, "end": v(-20.66, -6.24) * mm});
            skLineSegment(sketch, "E723", {"start": v(-20.66, -6.24) * mm, "end": v(-20.66, -6.34) * mm});
            skLineSegment(sketch, "E724", {"start": v(-20.66, -6.34) * mm, "end": v(-20.66, -6.45) * mm});
            skLineSegment(sketch, "E725", {"start": v(-20.66, -6.45) * mm, "end": v(-20.66, -6.5) * mm});
            skLineSegment(sketch, "E726", {"start": v(-17.33, 4.73) * mm, "end": v(-17.3, 4.83) * mm});
            skLineSegment(sketch, "E727", {"start": v(-17.3, 4.83) * mm, "end": v(-17.25, 4.97) * mm});
            skLineSegment(sketch, "E728", {"start": v(-17.25, 4.97) * mm, "end": v(-17.2, 5.1) * mm});
            skLineSegment(sketch, "E729", {"start": v(-17.2, 5.1) * mm, "end": v(-17.16, 5.24) * mm});
            skLineSegment(sketch, "E730", {"start": v(-17.16, 5.24) * mm, "end": v(-17.12, 5.38) * mm});
            skLineSegment(sketch, "E731", {"start": v(-17.12, 5.38) * mm, "end": v(-17.09, 5.51) * mm});
            skLineSegment(sketch, "E732", {"start": v(-17.09, 5.51) * mm, "end": v(-17.05, 5.65) * mm});
            skLineSegment(sketch, "E733", {"start": v(-17.05, 5.65) * mm, "end": v(-17.02, 5.78) * mm});
            skLineSegment(sketch, "E734", {"start": v(-17.02, 5.78) * mm, "end": v(-17, 5.91) * mm});
            skLineSegment(sketch, "E735", {"start": v(-17, 5.91) * mm, "end": v(-16.97, 6.05) * mm});
            skLineSegment(sketch, "E736", {"start": v(-16.97, 6.05) * mm, "end": v(-16.95, 6.18) * mm});
            skLineSegment(sketch, "E737", {"start": v(-16.95, 6.18) * mm, "end": v(-16.92, 6.31) * mm});
            skLineSegment(sketch, "E738", {"start": v(-16.92, 6.31) * mm, "end": v(-16.9, 6.44) * mm});
            skLineSegment(sketch, "E739", {"start": v(-16.9, 6.44) * mm, "end": v(-16.89, 6.57) * mm});
            skLineSegment(sketch, "E740", {"start": v(-16.89, 6.57) * mm, "end": v(-16.87, 6.7) * mm});
            skLineSegment(sketch, "E741", {"start": v(-16.87, 6.7) * mm, "end": v(-16.86, 6.83) * mm});
            skLineSegment(sketch, "E742", {"start": v(-16.86, 6.83) * mm, "end": v(-16.85, 6.96) * mm});
            skLineSegment(sketch, "E743", {"start": v(-16.85, 6.96) * mm, "end": v(-16.84, 7.1) * mm});
            skLineSegment(sketch, "E744", {"start": v(-16.84, 7.1) * mm, "end": v(-16.84, 7.23) * mm});
            skLineSegment(sketch, "E745", {"start": v(-16.84, 7.23) * mm, "end": v(-16.83, 7.36) * mm});
            skLineSegment(sketch, "E746", {"start": v(-16.83, 7.36) * mm, "end": v(-16.83, 7.49) * mm});
            skLineSegment(sketch, "E747", {"start": v(-20.29, 4.4) * mm, "end": v(-20.37, 4.34) * mm});
            skLineSegment(sketch, "E748", {"start": v(-20.37, 4.34) * mm, "end": v(-20.46, 4.27) * mm});
            skLineSegment(sketch, "E749", {"start": v(-20.46, 4.27) * mm, "end": v(-20.55, 4.2) * mm});
            skLineSegment(sketch, "E750", {"start": v(-20.55, 4.2) * mm, "end": v(-20.65, 4.12) * mm});
            skLineSegment(sketch, "E751", {"start": v(-20.65, 4.12) * mm, "end": v(-20.75, 4.05) * mm});
            skLineSegment(sketch, "E752", {"start": v(-20.75, 4.05) * mm, "end": v(-20.86, 3.98) * mm});
            skLineSegment(sketch, "E753", {"start": v(-20.86, 3.98) * mm, "end": v(-20.97, 3.9) * mm});
            skLineSegment(sketch, "E754", {"start": v(-20.97, 3.9) * mm, "end": v(-21.09, 3.83) * mm});
            skLineSegment(sketch, "E755", {"start": v(-21.09, 3.83) * mm, "end": v(-21.21, 3.75) * mm});
            skLineSegment(sketch, "E756", {"start": v(-21.21, 3.75) * mm, "end": v(-21.34, 3.68) * mm});
            skLineSegment(sketch, "E757", {"start": v(-21.34, 3.68) * mm, "end": v(-21.48, 3.6) * mm});
            skLineSegment(sketch, "E758", {"start": v(-21.48, 3.6) * mm, "end": v(-21.62, 3.53) * mm});
            skLineSegment(sketch, "E759", {"start": v(-21.62, 3.53) * mm, "end": v(-21.77, 3.45) * mm});
            skLineSegment(sketch, "E760", {"start": v(-21.77, 3.45) * mm, "end": v(-21.93, 3.37) * mm});
            skLineSegment(sketch, "E761", {"start": v(-21.93, 3.37) * mm, "end": v(-22.1, 3.3) * mm});
            skLineSegment(sketch, "E762", {"start": v(-22.1, 3.3) * mm, "end": v(-22.27, 3.21) * mm});
            skLineSegment(sketch, "E763", {"start": v(-22.27, 3.21) * mm, "end": v(-22.45, 3.13) * mm});
            skLineSegment(sketch, "E764", {"start": v(-22.45, 3.13) * mm, "end": v(-22.64, 3.05) * mm});
            skLineSegment(sketch, "E765", {"start": v(-22.64, 3.05) * mm, "end": v(-22.83, 2.97) * mm});
            skLineSegment(sketch, "E766", {"start": v(-22.83, 2.97) * mm, "end": v(-23.04, 2.88) * mm});
            skLineSegment(sketch, "E767", {"start": v(-23.04, 2.88) * mm, "end": v(-23.15, 2.84) * mm});
            skLineSegment(sketch, "E768", {"start": v(-39.32, 6.37) * mm, "end": v(-39.27, 6.4) * mm});
            skLineSegment(sketch, "E769", {"start": v(-39.27, 6.4) * mm, "end": v(-39.2, 6.41) * mm});
            skLineSegment(sketch, "E770", {"start": v(-39.2, 6.41) * mm, "end": v(-39.14, 6.43) * mm});
            skLineSegment(sketch, "E771", {"start": v(-39.14, 6.43) * mm, "end": v(-39.06, 6.45) * mm});
            skLineSegment(sketch, "E772", {"start": v(-39.06, 6.45) * mm, "end": v(-38.97, 6.48) * mm});
            skLineSegment(sketch, "E773", {"start": v(-38.97, 6.48) * mm, "end": v(-38.88, 6.5) * mm});
            skLineSegment(sketch, "E774", {"start": v(-38.88, 6.5) * mm, "end": v(-38.77, 6.53) * mm});
            skLineSegment(sketch, "E775", {"start": v(-38.77, 6.53) * mm, "end": v(-38.66, 6.55) * mm});
            skLineSegment(sketch, "E776", {"start": v(-38.66, 6.55) * mm, "end": v(-38.53, 6.58) * mm});
            skLineSegment(sketch, "E777", {"start": v(-38.53, 6.58) * mm, "end": v(-38.4, 6.61) * mm});
            skLineSegment(sketch, "E778", {"start": v(-38.4, 6.61) * mm, "end": v(-38.25, 6.64) * mm});
            skLineSegment(sketch, "E779", {"start": v(-34.83, -3.68) * mm, "end": v(-35.4, -3.46) * mm});
            skLineSegment(sketch, "E780", {"start": v(-35.4, -3.46) * mm, "end": v(-35.99, -3.24) * mm});
            skLineSegment(sketch, "E781", {"start": v(-35.99, -3.24) * mm, "end": v(-36.57, -3.03) * mm});
            skLineSegment(sketch, "E782", {"start": v(-36.57, -3.03) * mm, "end": v(-37.17, -2.81) * mm});
            skLineSegment(sketch, "E783", {"start": v(-37.17, -2.81) * mm, "end": v(-37.78, -2.6) * mm});
            skLineSegment(sketch, "E784", {"start": v(-33.7, -4.11) * mm, "end": v(-34.83, -3.68) * mm});
            skLineSegment(sketch, "E785", {"start": v(-32.61, -4.55) * mm, "end": v(-33.7, -4.11) * mm});
            skLineSegment(sketch, "E786", {"start": v(-28.78, -6.16) * mm, "end": v(-29.2, -5.97) * mm});
            skLineSegment(sketch, "E787", {"start": v(-29.2, -5.97) * mm, "end": v(-29.64, -5.78) * mm});
            skLineSegment(sketch, "E788", {"start": v(-29.64, -5.78) * mm, "end": v(-30.1, -5.59) * mm});
            skLineSegment(sketch, "E789", {"start": v(-30.1, -5.59) * mm, "end": v(-30.56, -5.39) * mm});
            skLineSegment(sketch, "E790", {"start": v(-30.56, -5.39) * mm, "end": v(-31.05, -5.18) * mm});
            skLineSegment(sketch, "E791", {"start": v(-31.05, -5.18) * mm, "end": v(-31.56, -4.97) * mm});
            skLineSegment(sketch, "E792", {"start": v(-31.56, -4.97) * mm, "end": v(-32.61, -4.55) * mm});
            skLineSegment(sketch, "E793", {"start": v(-27.98, -6.52) * mm, "end": v(-28.78, -6.16) * mm});
            skLineSegment(sketch, "E794", {"start": v(-27.26, -6.85) * mm, "end": v(-27.98, -6.52) * mm});
            skLineSegment(sketch, "E795", {"start": v(-24.76, -8.06) * mm, "end": v(-24.97, -7.95) * mm});
            skLineSegment(sketch, "E796", {"start": v(-24.97, -7.95) * mm, "end": v(-24.97, -7.95) * mm});
            skLineSegment(sketch, "E797", {"start": v(-24.97, -7.95) * mm, "end": v(-25.2, -7.83) * mm});
            skLineSegment(sketch, "E798", {"start": v(-25.2, -7.83) * mm, "end": v(-25.45, -7.71) * mm});
            skLineSegment(sketch, "E799", {"start": v(-25.45, -7.71) * mm, "end": v(-25.71, -7.58) * mm});
            skLineSegment(sketch, "E800", {"start": v(-25.71, -7.58) * mm, "end": v(-25.99, -7.45) * mm});
            skLineSegment(sketch, "E801", {"start": v(-25.99, -7.45) * mm, "end": v(-26.28, -7.3) * mm});
            skLineSegment(sketch, "E802", {"start": v(-26.28, -7.3) * mm, "end": v(-26.6, -7.16) * mm});
            skLineSegment(sketch, "E803", {"start": v(-26.6, -7.16) * mm, "end": v(-27.26, -6.85) * mm});
            skLineSegment(sketch, "E804", {"start": v(-39.24, 5.72) * mm, "end": v(-39.68, 6.02) * mm});
            skLineSegment(sketch, "E805", {"start": v(-12.1, -11.81) * mm, "end": v(-12.07, -11.84) * mm});
            skLineSegment(sketch, "E806", {"start": v(-12.07, -11.84) * mm, "end": v(-12.06, -11.86) * mm});
            skLineSegment(sketch, "E807", {"start": v(-12.06, -11.86) * mm, "end": v(-12.04, -11.9) * mm});
            skLineSegment(sketch, "E808", {"start": v(-12.04, -11.9) * mm, "end": v(-12.01, -11.92) * mm});
            skLineSegment(sketch, "E809", {"start": v(-12.01, -11.92) * mm, "end": v(-12, -11.94) * mm});
            skLineSegment(sketch, "E810", {"start": v(-12, -11.94) * mm, "end": v(-11.97, -11.96) * mm});
            skLineSegment(sketch, "E811", {"start": v(-11.97, -11.96) * mm, "end": v(-11.95, -11.99) * mm});
            skLineSegment(sketch, "E812", {"start": v(-11.95, -11.99) * mm, "end": v(-11.92, -12) * mm});
            skLineSegment(sketch, "E813", {"start": v(-11.92, -12) * mm, "end": v(-11.91, -12.02) * mm});
            skLineSegment(sketch, "E814", {"start": v(-11.91, -12.02) * mm, "end": v(-11.9, -12.03) * mm});
            skLineSegment(sketch, "E815", {"start": v(-11.9, -12.03) * mm, "end": v(-11.88, -12.05) * mm});
            skLineSegment(sketch, "E816", {"start": v(-11.88, -12.05) * mm, "end": v(-11.85, -12.07) * mm});
            skLineSegment(sketch, "E817", {"start": v(-11.85, -12.07) * mm, "end": v(-11.82, -12.09) * mm});
            skLineSegment(sketch, "E818", {"start": v(-11.82, -12.09) * mm, "end": v(-11.8, -12.1) * mm});
            skLineSegment(sketch, "E819", {"start": v(-11.8, -12.1) * mm, "end": v(-11.77, -12.13) * mm});
            skLineSegment(sketch, "E820", {"start": v(-11.77, -12.13) * mm, "end": v(-11.74, -12.14) * mm});
            skLineSegment(sketch, "E821", {"start": v(-11.74, -12.14) * mm, "end": v(-11.71, -12.16) * mm});
            skLineSegment(sketch, "E822", {"start": v(-11.71, -12.16) * mm, "end": v(-11.68, -12.17) * mm});
            skLineSegment(sketch, "E823", {"start": v(-11.68, -12.17) * mm, "end": v(-11.65, -12.19) * mm});
            skLineSegment(sketch, "E824", {"start": v(-11.65, -12.19) * mm, "end": v(-11.62, -12.2) * mm});
            skLineSegment(sketch, "E825", {"start": v(-11.62, -12.2) * mm, "end": v(-11.6, -12.22) * mm});
            skLineSegment(sketch, "E826", {"start": v(-11.6, -12.22) * mm, "end": v(-11.56, -12.23) * mm});
            skLineSegment(sketch, "E827", {"start": v(-11.56, -12.23) * mm, "end": v(-11.52, -12.24) * mm});
            skLineSegment(sketch, "E828", {"start": v(-11.52, -12.24) * mm, "end": v(-11.49, -12.25) * mm});
            skLineSegment(sketch, "E829", {"start": v(-11.49, -12.25) * mm, "end": v(-11.45, -12.26) * mm});
            skLineSegment(sketch, "E830", {"start": v(-11.45, -12.26) * mm, "end": v(-11.42, -12.27) * mm});
            skLineSegment(sketch, "E831", {"start": v(-11.42, -12.27) * mm, "end": v(-11.38, -12.28) * mm});
            skLineSegment(sketch, "E832", {"start": v(-11.38, -12.28) * mm, "end": v(-11.34, -12.29) * mm});
            skLineSegment(sketch, "E833", {"start": v(-11.34, -12.29) * mm, "end": v(-11.3, -12.3) * mm});
            skLineSegment(sketch, "E834", {"start": v(-11.3, -12.3) * mm, "end": v(-11.27, -12.3) * mm});
            skLineSegment(sketch, "E835", {"start": v(-11.27, -12.3) * mm, "end": v(-11.22, -12.3) * mm});
            skLineSegment(sketch, "E836", {"start": v(-11.22, -12.3) * mm, "end": v(-11.18, -12.31) * mm});
            skLineSegment(sketch, "E837", {"start": v(-11.18, -12.31) * mm, "end": v(-11.14, -12.32) * mm});
            skLineSegment(sketch, "E838", {"start": v(-11.14, -12.32) * mm, "end": v(-11.1, -12.32) * mm});
            skLineSegment(sketch, "E839", {"start": v(-11.1, -12.32) * mm, "end": v(-11.05, -12.32) * mm});
            skLineSegment(sketch, "E840", {"start": v(-11.05, -12.32) * mm, "end": v(-11, -12.32) * mm});
            skLineSegment(sketch, "E841", {"start": v(-11, -12.32) * mm, "end": v(-10.98, -12.32) * mm});
            skLineSegment(sketch, "E842", {"start": v(-12.4, -10.32) * mm, "end": v(-12.4, -10.37) * mm});
            skLineSegment(sketch, "E843", {"start": v(-12.4, -10.37) * mm, "end": v(-12.4, -10.45) * mm});
            skLineSegment(sketch, "E844", {"start": v(-12.4, -10.45) * mm, "end": v(-12.4, -10.54) * mm});
            skLineSegment(sketch, "E845", {"start": v(-12.4, -10.54) * mm, "end": v(-12.4, -10.62) * mm});
            skLineSegment(sketch, "E846", {"start": v(-12.4, -10.62) * mm, "end": v(-12.4, -10.7) * mm});
            skLineSegment(sketch, "E847", {"start": v(-12.4, -10.7) * mm, "end": v(-12.39, -10.77) * mm});
            skLineSegment(sketch, "E848", {"start": v(-12.39, -10.77) * mm, "end": v(-12.38, -10.84) * mm});
            skLineSegment(sketch, "E849", {"start": v(-12.38, -10.84) * mm, "end": v(-12.38, -10.91) * mm});
            skLineSegment(sketch, "E850", {"start": v(-12.38, -10.91) * mm, "end": v(-12.37, -10.98) * mm});
            skLineSegment(sketch, "E851", {"start": v(-12.37, -10.98) * mm, "end": v(-12.36, -11.04) * mm});
            skLineSegment(sketch, "E852", {"start": v(-12.36, -11.04) * mm, "end": v(-12.35, -11.1) * mm});
            skLineSegment(sketch, "E853", {"start": v(-12.35, -11.1) * mm, "end": v(-12.34, -11.16) * mm});
            skLineSegment(sketch, "E854", {"start": v(-12.34, -11.16) * mm, "end": v(-12.33, -11.22) * mm});
            skLineSegment(sketch, "E855", {"start": v(-12.33, -11.22) * mm, "end": v(-12.31, -11.27) * mm});
            skLineSegment(sketch, "E856", {"start": v(-12.31, -11.27) * mm, "end": v(-12.3, -11.33) * mm});
            skLineSegment(sketch, "E857", {"start": v(-12.3, -11.33) * mm, "end": v(-12.29, -11.38) * mm});
            skLineSegment(sketch, "E858", {"start": v(-12.29, -11.38) * mm, "end": v(-12.27, -11.42) * mm});
            skLineSegment(sketch, "E859", {"start": v(-12.27, -11.42) * mm, "end": v(-12.26, -11.47) * mm});
            skLineSegment(sketch, "E860", {"start": v(-12.26, -11.47) * mm, "end": v(-12.24, -11.51) * mm});
            skLineSegment(sketch, "E861", {"start": v(-12.24, -11.51) * mm, "end": v(-12.22, -11.56) * mm});
            skLineSegment(sketch, "E862", {"start": v(-12.22, -11.56) * mm, "end": v(-12.2, -11.6) * mm});
            skLineSegment(sketch, "E863", {"start": v(-12.2, -11.6) * mm, "end": v(-12.2, -11.64) * mm});
            skLineSegment(sketch, "E864", {"start": v(-12.2, -11.64) * mm, "end": v(-12.17, -11.68) * mm});
            skLineSegment(sketch, "E865", {"start": v(-12.17, -11.68) * mm, "end": v(-12.15, -11.71) * mm});
            skLineSegment(sketch, "E866", {"start": v(-12.15, -11.71) * mm, "end": v(-12.13, -11.75) * mm});
            skLineSegment(sketch, "E867", {"start": v(-12.13, -11.75) * mm, "end": v(-12.11, -11.78) * mm});
            skLineSegment(sketch, "E868", {"start": v(-12.11, -11.78) * mm, "end": v(-12.1, -11.81) * mm});
            skLineSegment(sketch, "E869", {"start": v(-19.8, -3.66) * mm, "end": v(-19.84, -3.72) * mm});
            skLineSegment(sketch, "E870", {"start": v(-19.84, -3.72) * mm, "end": v(-19.89, -3.78) * mm});
            skLineSegment(sketch, "E871", {"start": v(-19.89, -3.78) * mm, "end": v(-19.93, -3.84) * mm});
            skLineSegment(sketch, "E872", {"start": v(-19.93, -3.84) * mm, "end": v(-19.97, -3.9) * mm});
            skLineSegment(sketch, "E873", {"start": v(-19.97, -3.9) * mm, "end": v(-20.01, -3.96) * mm});
            skLineSegment(sketch, "E874", {"start": v(-20.01, -3.96) * mm, "end": v(-20.05, -4.01) * mm});
            skLineSegment(sketch, "E875", {"start": v(-20.05, -4.01) * mm, "end": v(-20.09, -4.07) * mm});
            skLineSegment(sketch, "E876", {"start": v(-20.09, -4.07) * mm, "end": v(-20.12, -4.13) * mm});
            skLineSegment(sketch, "E877", {"start": v(-20.12, -4.13) * mm, "end": v(-20.16, -4.19) * mm});
            skLineSegment(sketch, "E878", {"start": v(-20.16, -4.19) * mm, "end": v(-20.19, -4.25) * mm});
            skLineSegment(sketch, "E879", {"start": v(-20.19, -4.25) * mm, "end": v(-20.22, -4.3) * mm});
            skLineSegment(sketch, "E880", {"start": v(-20.22, -4.3) * mm, "end": v(-20.25, -4.36) * mm});
            skLineSegment(sketch, "E881", {"start": v(-20.25, -4.36) * mm, "end": v(-20.28, -4.42) * mm});
            skLineSegment(sketch, "E882", {"start": v(-20.28, -4.42) * mm, "end": v(-20.3, -4.48) * mm});
            skLineSegment(sketch, "E883", {"start": v(-20.3, -4.48) * mm, "end": v(-20.33, -4.54) * mm});
            skLineSegment(sketch, "E884", {"start": v(-20.33, -4.54) * mm, "end": v(-20.36, -4.6) * mm});
            skLineSegment(sketch, "E885", {"start": v(-20.36, -4.6) * mm, "end": v(-20.38, -4.65) * mm});
            skLineSegment(sketch, "E886", {"start": v(-20.38, -4.65) * mm, "end": v(-20.4, -4.71) * mm});
            skLineSegment(sketch, "E887", {"start": v(-20.4, -4.71) * mm, "end": v(-20.43, -4.77) * mm});
            skLineSegment(sketch, "E888", {"start": v(-20.43, -4.77) * mm, "end": v(-20.45, -4.83) * mm});
            skLineSegment(sketch, "E889", {"start": v(-20.45, -4.83) * mm, "end": v(-20.46, -4.89) * mm});
            skLineSegment(sketch, "E890", {"start": v(-20.46, -4.89) * mm, "end": v(-20.48, -4.95) * mm});
            skLineSegment(sketch, "E891", {"start": v(-20.48, -4.95) * mm, "end": v(-20.49, -4.96) * mm});
            skLineSegment(sketch, "E892", {"start": v(-18.82, 2.25) * mm, "end": v(-18.8, 2.26) * mm});
            skLineSegment(sketch, "E893", {"start": v(-18.8, 2.26) * mm, "end": v(-18.72, 2.36) * mm});
            skLineSegment(sketch, "E894", {"start": v(-18.72, 2.36) * mm, "end": v(-18.63, 2.46) * mm});
            skLineSegment(sketch, "E895", {"start": v(-18.63, 2.46) * mm, "end": v(-18.54, 2.57) * mm});
            skLineSegment(sketch, "E896", {"start": v(-18.54, 2.57) * mm, "end": v(-18.46, 2.68) * mm});
            skLineSegment(sketch, "E897", {"start": v(-18.46, 2.68) * mm, "end": v(-18.38, 2.78) * mm});
            skLineSegment(sketch, "E898", {"start": v(-18.38, 2.78) * mm, "end": v(-18.3, 2.9) * mm});
            skLineSegment(sketch, "E899", {"start": v(-18.3, 2.9) * mm, "end": v(-18.22, 3) * mm});
            skLineSegment(sketch, "E900", {"start": v(-18.22, 3) * mm, "end": v(-18.15, 3.1) * mm});
            skLineSegment(sketch, "E901", {"start": v(-18.15, 3.1) * mm, "end": v(-18.07, 3.22) * mm});
            skLineSegment(sketch, "E902", {"start": v(-18.07, 3.22) * mm, "end": v(-18, 3.33) * mm});
            skLineSegment(sketch, "E903", {"start": v(-18, 3.33) * mm, "end": v(-17.94, 3.44) * mm});
            skLineSegment(sketch, "E904", {"start": v(-17.94, 3.44) * mm, "end": v(-17.87, 3.55) * mm});
            skLineSegment(sketch, "E905", {"start": v(-17.87, 3.55) * mm, "end": v(-17.8, 3.67) * mm});
            skLineSegment(sketch, "E906", {"start": v(-17.8, 3.67) * mm, "end": v(-17.74, 3.78) * mm});
            skLineSegment(sketch, "E907", {"start": v(-17.74, 3.78) * mm, "end": v(-17.71, 3.84) * mm});
            skLineSegment(sketch, "E908", {"start": v(-17.71, 3.84) * mm, "end": v(-17.68, 3.9) * mm});
            skLineSegment(sketch, "E909", {"start": v(-17.68, 3.9) * mm, "end": v(-17.63, 4.01) * mm});
            skLineSegment(sketch, "E910", {"start": v(-17.63, 4.01) * mm, "end": v(-17.57, 4.13) * mm});
            skLineSegment(sketch, "E911", {"start": v(-17.57, 4.13) * mm, "end": v(-17.52, 4.25) * mm});
            skLineSegment(sketch, "E912", {"start": v(-17.52, 4.25) * mm, "end": v(-17.47, 4.37) * mm});
            skLineSegment(sketch, "E913", {"start": v(-17.47, 4.37) * mm, "end": v(-17.42, 4.49) * mm});
            skLineSegment(sketch, "E914", {"start": v(-17.42, 4.49) * mm, "end": v(-17.37, 4.6) * mm});
            skLineSegment(sketch, "E915", {"start": v(-17.37, 4.6) * mm, "end": v(-17.33, 4.73) * mm});
            skLineSegment(sketch, "E916", {"start": v(-43.79, -12.92) * mm, "end": v(-43.75, -12.89) * mm});
            skLineSegment(sketch, "E917", {"start": v(-43.75, -12.89) * mm, "end": v(-43.7, -12.85) * mm});
            skLineSegment(sketch, "E918", {"start": v(-43.7, -12.85) * mm, "end": v(-43.64, -12.8) * mm});
            skLineSegment(sketch, "E919", {"start": v(-43.64, -12.8) * mm, "end": v(-43.58, -12.76) * mm});
            skLineSegment(sketch, "E920", {"start": v(-43.58, -12.76) * mm, "end": v(-43.53, -12.72) * mm});
            skLineSegment(sketch, "E921", {"start": v(-43.53, -12.72) * mm, "end": v(-43.48, -12.67) * mm});
            skLineSegment(sketch, "E922", {"start": v(-43.48, -12.67) * mm, "end": v(-43.43, -12.63) * mm});
            skLineSegment(sketch, "E923", {"start": v(-43.43, -12.63) * mm, "end": v(-43.39, -12.58) * mm});
            skLineSegment(sketch, "E924", {"start": v(-43.39, -12.58) * mm, "end": v(-43.34, -12.53) * mm});
            skLineSegment(sketch, "E925", {"start": v(-43.34, -12.53) * mm, "end": v(-43.3, -12.49) * mm});
            skLineSegment(sketch, "E926", {"start": v(-43.3, -12.49) * mm, "end": v(-43.26, -12.44) * mm});
            skLineSegment(sketch, "E927", {"start": v(-43.26, -12.44) * mm, "end": v(-43.22, -12.4) * mm});
            skLineSegment(sketch, "E928", {"start": v(-43.22, -12.4) * mm, "end": v(-43.18, -12.34) * mm});
            skLineSegment(sketch, "E929", {"start": v(-43.18, -12.34) * mm, "end": v(-43.14, -12.3) * mm});
            skLineSegment(sketch, "E930", {"start": v(-43.14, -12.3) * mm, "end": v(-43.1, -12.25) * mm});
            skLineSegment(sketch, "E931", {"start": v(-43.1, -12.25) * mm, "end": v(-43.07, -12.2) * mm});
            skLineSegment(sketch, "E932", {"start": v(-43.07, -12.2) * mm, "end": v(-43.03, -12.15) * mm});
            skLineSegment(sketch, "E933", {"start": v(-43.03, -12.15) * mm, "end": v(-43, -12.1) * mm});
            skLineSegment(sketch, "E934", {"start": v(-43, -12.1) * mm, "end": v(-42.97, -12.04) * mm});
            skLineSegment(sketch, "E935", {"start": v(-42.97, -12.04) * mm, "end": v(-42.94, -12) * mm});
            skLineSegment(sketch, "E936", {"start": v(-42.94, -12) * mm, "end": v(-42.91, -11.94) * mm});
            skLineSegment(sketch, "E937", {"start": v(-42.91, -11.94) * mm, "end": v(-42.89, -11.88) * mm});
            skLineSegment(sketch, "E938", {"start": v(-42.89, -11.88) * mm, "end": v(-42.86, -11.83) * mm});
            skLineSegment(sketch, "E939", {"start": v(-42.86, -11.83) * mm, "end": v(-42.84, -11.77) * mm});
            skLineSegment(sketch, "E940", {"start": v(-42.84, -11.77) * mm, "end": v(-42.81, -11.72) * mm});
            skLineSegment(sketch, "E941", {"start": v(-42.81, -11.72) * mm, "end": v(-42.8, -11.66) * mm});
            skLineSegment(sketch, "E942", {"start": v(-42.8, -11.66) * mm, "end": v(-42.77, -11.6) * mm});
            skLineSegment(sketch, "E943", {"start": v(-42.77, -11.6) * mm, "end": v(-42.75, -11.55) * mm});
            skLineSegment(sketch, "E944", {"start": v(-42.75, -11.55) * mm, "end": v(-42.74, -11.49) * mm});
            skLineSegment(sketch, "E945", {"start": v(-42.74, -11.49) * mm, "end": v(-42.72, -11.43) * mm});
            skLineSegment(sketch, "E946", {"start": v(37.36, -12.24) * mm, "end": v(37.49, -12.24) * mm});
            skLineSegment(sketch, "E947", {"start": v(37.49, -12.24) * mm, "end": v(37.62, -12.23) * mm});
            skLineSegment(sketch, "E948", {"start": v(37.62, -12.23) * mm, "end": v(37.76, -12.21) * mm});
            skLineSegment(sketch, "E949", {"start": v(37.76, -12.21) * mm, "end": v(37.9, -12.19) * mm});
            skLineSegment(sketch, "E950", {"start": v(37.9, -12.19) * mm, "end": v(38.05, -12.15) * mm});
            skLineSegment(sketch, "E951", {"start": v(38.05, -12.15) * mm, "end": v(38.2, -12.11) * mm});
            skLineSegment(sketch, "E952", {"start": v(38.2, -12.11) * mm, "end": v(38.35, -12.06) * mm});
            skLineSegment(sketch, "E953", {"start": v(38.35, -12.06) * mm, "end": v(38.5, -12) * mm});
            skLineSegment(sketch, "E954", {"start": v(38.5, -12) * mm, "end": v(38.67, -11.94) * mm});
            skLineSegment(sketch, "E955", {"start": v(38.67, -11.94) * mm, "end": v(38.84, -11.86) * mm});
            skLineSegment(sketch, "E956", {"start": v(38.84, -11.86) * mm, "end": v(39.01, -11.77) * mm});
            skLineSegment(sketch, "E957", {"start": v(39.01, -11.77) * mm, "end": v(39.2, -11.67) * mm});
            skLineSegment(sketch, "E958", {"start": v(39.2, -11.67) * mm, "end": v(39.38, -11.56) * mm});
            skLineSegment(sketch, "E959", {"start": v(39.38, -11.56) * mm, "end": v(39.57, -11.44) * mm});
            skLineSegment(sketch, "E960", {"start": v(39.57, -11.44) * mm, "end": v(39.76, -11.3) * mm});
            skLineSegment(sketch, "E961", {"start": v(39.76, -11.3) * mm, "end": v(39.96, -11.16) * mm});
            skLineSegment(sketch, "E962", {"start": v(39.96, -11.16) * mm, "end": v(40.17, -11) * mm});
            skLineSegment(sketch, "E963", {"start": v(40.17, -11) * mm, "end": v(40.39, -10.83) * mm});
            skLineSegment(sketch, "E964", {"start": v(40.39, -10.83) * mm, "end": v(40.61, -10.64) * mm});
            skLineSegment(sketch, "E965", {"start": v(40.61, -10.64) * mm, "end": v(40.84, -10.44) * mm});
            skLineSegment(sketch, "E966", {"start": v(40.84, -10.44) * mm, "end": v(41.08, -10.22) * mm});
            skLineSegment(sketch, "E967", {"start": v(41.08, -10.22) * mm, "end": v(41.33, -9.98) * mm});
            skLineSegment(sketch, "E968", {"start": v(41.33, -9.98) * mm, "end": v(41.58, -9.73) * mm});
            skLineSegment(sketch, "E969", {"start": v(41.58, -9.73) * mm, "end": v(41.85, -9.45) * mm});
            skLineSegment(sketch, "E970", {"start": v(41.85, -9.45) * mm, "end": v(42.12, -9.16) * mm});
            skLineSegment(sketch, "E971", {"start": v(42.12, -9.16) * mm, "end": v(42.4, -8.85) * mm});
            skLineSegment(sketch, "E972", {"start": v(42.4, -8.85) * mm, "end": v(42.69, -8.52) * mm});
            skLineSegment(sketch, "E973", {"start": v(42.69, -8.52) * mm, "end": v(42.99, -8.16) * mm});
            skLineSegment(sketch, "E974", {"start": v(42.99, -8.16) * mm, "end": v(43.3, -7.78) * mm});
            skLineSegment(sketch, "E975", {"start": v(43.3, -7.78) * mm, "end": v(43.62, -7.38) * mm});
            skLineSegment(sketch, "E976", {"start": v(43.62, -7.38) * mm, "end": v(43.95, -6.96) * mm});
            skLineSegment(sketch, "E977", {"start": v(43.95, -6.96) * mm, "end": v(44.1, -6.75) * mm});
            skLineSegment(sketch, "E978", {"start": v(-23.05, -14.5) * mm, "end": v(-23.02, -14.5) * mm});
            skLineSegment(sketch, "E979", {"start": v(-23.02, -14.5) * mm, "end": v(-23, -14.5) * mm});
            skLineSegment(sketch, "E980", {"start": v(-23, -14.5) * mm, "end": v(-22.97, -14.5) * mm});
            skLineSegment(sketch, "E981", {"start": v(-22.97, -14.5) * mm, "end": v(-22.95, -14.5) * mm});
            skLineSegment(sketch, "E982", {"start": v(-22.95, -14.5) * mm, "end": v(-22.93, -14.5) * mm});
            skLineSegment(sketch, "E983", {"start": v(-22.93, -14.5) * mm, "end": v(-22.9, -14.5) * mm});
            skLineSegment(sketch, "E984", {"start": v(-22.9, -14.5) * mm, "end": v(-22.88, -14.49) * mm});
            skLineSegment(sketch, "E985", {"start": v(-22.88, -14.49) * mm, "end": v(-22.86, -14.48) * mm});
            skLineSegment(sketch, "E986", {"start": v(-22.86, -14.48) * mm, "end": v(-22.84, -14.48) * mm});
            skLineSegment(sketch, "E987", {"start": v(-22.84, -14.48) * mm, "end": v(-22.82, -14.47) * mm});
            skLineSegment(sketch, "E988", {"start": v(-22.82, -14.47) * mm, "end": v(-22.8, -14.46) * mm});
            skLineSegment(sketch, "E989", {"start": v(-22.8, -14.46) * mm, "end": v(-22.79, -14.46) * mm});
            skLineSegment(sketch, "E990", {"start": v(-22.79, -14.46) * mm, "end": v(-22.78, -14.45) * mm});
            skLineSegment(sketch, "E991", {"start": v(-22.78, -14.45) * mm, "end": v(-22.76, -14.45) * mm});
            skLineSegment(sketch, "E992", {"start": v(-22.76, -14.45) * mm, "end": v(-22.74, -14.44) * mm});
            skLineSegment(sketch, "E993", {"start": v(-22.74, -14.44) * mm, "end": v(-22.72, -14.43) * mm});
            skLineSegment(sketch, "E994", {"start": v(-22.72, -14.43) * mm, "end": v(-22.7, -14.41) * mm});
            skLineSegment(sketch, "E995", {"start": v(-22.7, -14.41) * mm, "end": v(-22.68, -14.4) * mm});
            skLineSegment(sketch, "E996", {"start": v(-22.68, -14.4) * mm, "end": v(-22.67, -14.39) * mm});
            skLineSegment(sketch, "E997", {"start": v(-22.67, -14.39) * mm, "end": v(-22.65, -14.38) * mm});
            skLineSegment(sketch, "E998", {"start": v(-22.65, -14.38) * mm, "end": v(-22.63, -14.36) * mm});
            skLineSegment(sketch, "E999", {"start": v(-22.63, -14.36) * mm, "end": v(-22.61, -14.35) * mm});
            skLineSegment(sketch, "E1000", {"start": v(-22.61, -14.35) * mm, "end": v(-22.6, -14.33) * mm});
            skLineSegment(sketch, "E1001", {"start": v(-22.6, -14.33) * mm, "end": v(-22.58, -14.32) * mm});
            skLineSegment(sketch, "E1002", {"start": v(-22.58, -14.32) * mm, "end": v(-22.56, -14.3) * mm});
            skLineSegment(sketch, "E1003", {"start": v(-22.56, -14.3) * mm, "end": v(-22.55, -14.28) * mm});
            skLineSegment(sketch, "E1004", {"start": v(-22.55, -14.28) * mm, "end": v(-22.53, -14.26) * mm});
            skLineSegment(sketch, "E1005", {"start": v(-22.53, -14.26) * mm, "end": v(-22.52, -14.24) * mm});
            skLineSegment(sketch, "E1006", {"start": v(-22.52, -14.24) * mm, "end": v(-22.5, -14.22) * mm});
            skLineSegment(sketch, "E1007", {"start": v(-22.5, -14.22) * mm, "end": v(-22.49, -14.2) * mm});
            skLineSegment(sketch, "E1008", {"start": v(-22.49, -14.2) * mm, "end": v(-22.47, -14.18) * mm});
            skLineSegment(sketch, "E1009", {"start": v(-22.47, -14.18) * mm, "end": v(-22.46, -14.15) * mm});
            skLineSegment(sketch, "E1010", {"start": v(-22.46, -14.15) * mm, "end": v(-22.45, -14.13) * mm});
            skLineSegment(sketch, "E1011", {"start": v(-22.45, -14.13) * mm, "end": v(-22.43, -14.1) * mm});
            skLineSegment(sketch, "E1012", {"start": v(-22.43, -14.1) * mm, "end": v(-22.42, -14.08) * mm});
            skLineSegment(sketch, "E1013", {"start": v(-22.42, -14.08) * mm, "end": v(-22.4, -14.05) * mm});
            skLineSegment(sketch, "E1014", {"start": v(-22.4, -14.05) * mm, "end": v(-22.4, -14.02) * mm});
            skLineSegment(sketch, "E1015", {"start": v(-22.4, -14.02) * mm, "end": v(-22.38, -13.99) * mm});
            skLineSegment(sketch, "E1016", {"start": v(-22.38, -13.99) * mm, "end": v(-22.37, -13.96) * mm});
            skLineSegment(sketch, "E1017", {"start": v(-22.37, -13.96) * mm, "end": v(-22.36, -13.92) * mm});
            skLineSegment(sketch, "E1018", {"start": v(-22.36, -13.92) * mm, "end": v(-22.35, -13.9) * mm});
            skLineSegment(sketch, "E1019", {"start": v(-22.35, -13.9) * mm, "end": v(-22.34, -13.86) * mm});
            skLineSegment(sketch, "E1020", {"start": v(-22.34, -13.86) * mm, "end": v(-22.33, -13.83) * mm});
            skLineSegment(sketch, "E1021", {"start": v(26.42, -12.28) * mm, "end": v(26.56, -12.28) * mm});
            skLineSegment(sketch, "E1022", {"start": v(26.56, -12.28) * mm, "end": v(26.7, -12.28) * mm});
            skLineSegment(sketch, "E1023", {"start": v(26.7, -12.28) * mm, "end": v(26.83, -12.27) * mm});
            skLineSegment(sketch, "E1024", {"start": v(26.83, -12.27) * mm, "end": v(26.97, -12.26) * mm});
            skLineSegment(sketch, "E1025", {"start": v(26.97, -12.26) * mm, "end": v(27.1, -12.24) * mm});
            skLineSegment(sketch, "E1026", {"start": v(27.1, -12.24) * mm, "end": v(27.24, -12.22) * mm});
            skLineSegment(sketch, "E1027", {"start": v(27.24, -12.22) * mm, "end": v(27.38, -12.2) * mm});
            skLineSegment(sketch, "E1028", {"start": v(27.38, -12.2) * mm, "end": v(27.52, -12.18) * mm});
            skLineSegment(sketch, "E1029", {"start": v(27.52, -12.18) * mm, "end": v(27.66, -12.15) * mm});
            skLineSegment(sketch, "E1030", {"start": v(27.66, -12.15) * mm, "end": v(27.8, -12.11) * mm});
            skLineSegment(sketch, "E1031", {"start": v(27.8, -12.11) * mm, "end": v(27.93, -12.08) * mm});
            skLineSegment(sketch, "E1032", {"start": v(27.93, -12.08) * mm, "end": v(28.07, -12.04) * mm});
            skLineSegment(sketch, "E1033", {"start": v(28.07, -12.04) * mm, "end": v(28.21, -12) * mm});
            skLineSegment(sketch, "E1034", {"start": v(28.21, -12) * mm, "end": v(28.35, -11.95) * mm});
            skLineSegment(sketch, "E1035", {"start": v(28.35, -11.95) * mm, "end": v(28.5, -11.9) * mm});
            skLineSegment(sketch, "E1036", {"start": v(28.5, -11.9) * mm, "end": v(28.63, -11.84) * mm});
            skLineSegment(sketch, "E1037", {"start": v(28.63, -11.84) * mm, "end": v(28.78, -11.78) * mm});
            skLineSegment(sketch, "E1038", {"start": v(28.78, -11.78) * mm, "end": v(28.92, -11.72) * mm});
            skLineSegment(sketch, "E1039", {"start": v(28.92, -11.72) * mm, "end": v(29.06, -11.65) * mm});
            skLineSegment(sketch, "E1040", {"start": v(29.06, -11.65) * mm, "end": v(29.2, -11.58) * mm});
            skLineSegment(sketch, "E1041", {"start": v(29.2, -11.58) * mm, "end": v(29.35, -11.5) * mm});
            skLineSegment(sketch, "E1042", {"start": v(29.35, -11.5) * mm, "end": v(29.5, -11.43) * mm});
            skLineSegment(sketch, "E1043", {"start": v(29.5, -11.43) * mm, "end": v(29.64, -11.34) * mm});
            skLineSegment(sketch, "E1044", {"start": v(29.64, -11.34) * mm, "end": v(29.8, -11.26) * mm});
            skLineSegment(sketch, "E1045", {"start": v(29.8, -11.26) * mm, "end": v(29.94, -11.16) * mm});
            skLineSegment(sketch, "E1046", {"start": v(29.94, -11.16) * mm, "end": v(30.09, -11.07) * mm});
            skLineSegment(sketch, "E1047", {"start": v(30.09, -11.07) * mm, "end": v(30.24, -10.97) * mm});
            skLineSegment(sketch, "E1048", {"start": v(30.24, -10.97) * mm, "end": v(30.4, -10.86) * mm});
            skLineSegment(sketch, "E1049", {"start": v(30.4, -10.86) * mm, "end": v(30.4, -10.85) * mm});
            skLineSegment(sketch, "E1050", {"start": v(-0.26, -12.52) * mm, "end": v(-0.33, -12.52) * mm});
            skLineSegment(sketch, "E1051", {"start": v(-0.33, -12.52) * mm, "end": v(-0.4, -12.52) * mm});
            skLineSegment(sketch, "E1052", {"start": v(-0.4, -12.52) * mm, "end": v(-0.46, -12.51) * mm});
            skLineSegment(sketch, "E1053", {"start": v(-0.46, -12.51) * mm, "end": v(-0.53, -12.5) * mm});
            skLineSegment(sketch, "E1054", {"start": v(-0.53, -12.5) * mm, "end": v(-0.6, -12.5) * mm});
            skLineSegment(sketch, "E1055", {"start": v(-0.6, -12.5) * mm, "end": v(-0.66, -12.5) * mm});
            skLineSegment(sketch, "E1056", {"start": v(-0.66, -12.5) * mm, "end": v(-0.73, -12.48) * mm});
            skLineSegment(sketch, "E1057", {"start": v(-0.73, -12.48) * mm, "end": v(-0.8, -12.47) * mm});
            skLineSegment(sketch, "E1058", {"start": v(-0.8, -12.47) * mm, "end": v(-0.86, -12.45) * mm});
            skLineSegment(sketch, "E1059", {"start": v(-0.86, -12.45) * mm, "end": v(-0.93, -12.44) * mm});
            skLineSegment(sketch, "E1060", {"start": v(-0.93, -12.44) * mm, "end": v(-1, -12.42) * mm});
            skLineSegment(sketch, "E1061", {"start": v(-1, -12.42) * mm, "end": v(-1.06, -12.4) * mm});
            skLineSegment(sketch, "E1062", {"start": v(-1.06, -12.4) * mm, "end": v(-1.13, -12.38) * mm});
            skLineSegment(sketch, "E1063", {"start": v(-1.13, -12.38) * mm, "end": v(-1.19, -12.35) * mm});
            skLineSegment(sketch, "E1064", {"start": v(-1.19, -12.35) * mm, "end": v(-1.25, -12.33) * mm});
            skLineSegment(sketch, "E1065", {"start": v(-1.25, -12.33) * mm, "end": v(-1.32, -12.3) * mm});
            skLineSegment(sketch, "E1066", {"start": v(-1.32, -12.3) * mm, "end": v(-1.38, -12.27) * mm});
            skLineSegment(sketch, "E1067", {"start": v(-1.38, -12.27) * mm, "end": v(-1.45, -12.24) * mm});
            skLineSegment(sketch, "E1068", {"start": v(-1.45, -12.24) * mm, "end": v(-1.51, -12.2) * mm});
            skLineSegment(sketch, "E1069", {"start": v(-1.51, -12.2) * mm, "end": v(-1.57, -12.18) * mm});
            skLineSegment(sketch, "E1070", {"start": v(-1.57, -12.18) * mm, "end": v(-1.64, -12.14) * mm});
            skLineSegment(sketch, "E1071", {"start": v(-1.64, -12.14) * mm, "end": v(-1.7, -12.1) * mm});
            skLineSegment(sketch, "E1072", {"start": v(-1.7, -12.1) * mm, "end": v(-1.76, -12.06) * mm});
            skLineSegment(sketch, "E1073", {"start": v(-1.76, -12.06) * mm, "end": v(-1.83, -12.02) * mm});
            skLineSegment(sketch, "E1074", {"start": v(-1.83, -12.02) * mm, "end": v(-1.89, -11.98) * mm});
            skLineSegment(sketch, "E1075", {"start": v(-1.89, -11.98) * mm, "end": v(-1.95, -11.93) * mm});
            skLineSegment(sketch, "E1076", {"start": v(-1.95, -11.93) * mm, "end": v(-2.01, -11.88) * mm});
            skLineSegment(sketch, "E1077", {"start": v(-2.01, -11.88) * mm, "end": v(-2.08, -11.83) * mm});
            skLineSegment(sketch, "E1078", {"start": v(-2.08, -11.83) * mm, "end": v(-2.14, -11.78) * mm});
            skLineSegment(sketch, "E1079", {"start": v(-2.14, -11.78) * mm, "end": v(-2.2, -11.73) * mm});
            skLineSegment(sketch, "E1080", {"start": v(-2.2, -11.73) * mm, "end": v(-2.26, -11.67) * mm});
            skLineSegment(sketch, "E1081", {"start": v(-2.26, -11.67) * mm, "end": v(-2.26, -11.67) * mm});
            skLineSegment(sketch, "E1082", {"start": v(-36.74, 5.36) * mm, "end": v(-37.12, 5.58) * mm});
            skLineSegment(sketch, "E1083", {"start": v(-9.49, -6.67) * mm, "end": v(-9.49, -6.62) * mm});
            skLineSegment(sketch, "E1084", {"start": v(-9.49, -6.62) * mm, "end": v(-9.49, -6.54) * mm});
            skLineSegment(sketch, "E1085", {"start": v(-9.49, -6.54) * mm, "end": v(-9.48, -6.47) * mm});
            skLineSegment(sketch, "E1086", {"start": v(-9.48, -6.47) * mm, "end": v(-9.48, -6.4) * mm});
            skLineSegment(sketch, "E1087", {"start": v(-9.48, -6.4) * mm, "end": v(-9.48, -6.34) * mm});
            skLineSegment(sketch, "E1088", {"start": v(-9.48, -6.34) * mm, "end": v(-9.47, -6.27) * mm});
            skLineSegment(sketch, "E1089", {"start": v(-9.47, -6.27) * mm, "end": v(-9.46, -6.2) * mm});
            skLineSegment(sketch, "E1090", {"start": v(-9.46, -6.2) * mm, "end": v(-9.45, -6.15) * mm});
            skLineSegment(sketch, "E1091", {"start": v(-9.45, -6.15) * mm, "end": v(-9.44, -6.08) * mm});
            skLineSegment(sketch, "E1092", {"start": v(-9.44, -6.08) * mm, "end": v(-9.43, -6.02) * mm});
            skLineSegment(sketch, "E1093", {"start": v(-9.43, -6.02) * mm, "end": v(-9.42, -5.97) * mm});
            skLineSegment(sketch, "E1094", {"start": v(-9.42, -5.97) * mm, "end": v(-9.41, -5.9) * mm});
            skLineSegment(sketch, "E1095", {"start": v(-9.41, -5.9) * mm, "end": v(-9.4, -5.85) * mm});
            skLineSegment(sketch, "E1096", {"start": v(-9.4, -5.85) * mm, "end": v(-9.38, -5.8) * mm});
            skLineSegment(sketch, "E1097", {"start": v(-9.38, -5.8) * mm, "end": v(-9.37, -5.74) * mm});
            skLineSegment(sketch, "E1098", {"start": v(-9.37, -5.74) * mm, "end": v(-9.35, -5.69) * mm});
            skLineSegment(sketch, "E1099", {"start": v(-9.35, -5.69) * mm, "end": v(-9.33, -5.64) * mm});
            skLineSegment(sketch, "E1100", {"start": v(-9.33, -5.64) * mm, "end": v(-9.32, -5.59) * mm});
            skLineSegment(sketch, "E1101", {"start": v(-9.32, -5.59) * mm, "end": v(-9.3, -5.54) * mm});
            skLineSegment(sketch, "E1102", {"start": v(-9.3, -5.54) * mm, "end": v(-9.28, -5.49) * mm});
            skLineSegment(sketch, "E1103", {"start": v(-9.28, -5.49) * mm, "end": v(-9.26, -5.44) * mm});
            skLineSegment(sketch, "E1104", {"start": v(-9.26, -5.44) * mm, "end": v(-9.23, -5.39) * mm});
            skLineSegment(sketch, "E1105", {"start": v(-9.23, -5.39) * mm, "end": v(-9.2, -5.34) * mm});
            skLineSegment(sketch, "E1106", {"start": v(-9.2, -5.34) * mm, "end": v(-9.19, -5.3) * mm});
            skLineSegment(sketch, "E1107", {"start": v(-9.19, -5.3) * mm, "end": v(-9.16, -5.25) * mm});
            skLineSegment(sketch, "E1108", {"start": v(-9.16, -5.25) * mm, "end": v(-9.13, -5.2) * mm});
            skLineSegment(sketch, "E1109", {"start": v(-9.13, -5.2) * mm, "end": v(-9.1, -5.16) * mm});
            skLineSegment(sketch, "E1110", {"start": v(-18.14, -1.94) * mm, "end": v(-18.33, -2.12) * mm});
            skLineSegment(sketch, "E1111", {"start": v(-18.33, -2.12) * mm, "end": v(-18.51, -2.3) * mm});
            skLineSegment(sketch, "E1112", {"start": v(-18.51, -2.3) * mm, "end": v(-18.69, -2.47) * mm});
            skLineSegment(sketch, "E1113", {"start": v(-18.69, -2.47) * mm, "end": v(-18.85, -2.63) * mm});
            skLineSegment(sketch, "E1114", {"start": v(-18.85, -2.63) * mm, "end": v(-19, -2.78) * mm});
            skLineSegment(sketch, "E1115", {"start": v(-19, -2.78) * mm, "end": v(-19.13, -2.92) * mm});
            skLineSegment(sketch, "E1116", {"start": v(-19.13, -2.92) * mm, "end": v(-19.26, -3.05) * mm});
            skLineSegment(sketch, "E1117", {"start": v(-19.26, -3.05) * mm, "end": v(-19.37, -3.17) * mm});
            skLineSegment(sketch, "E1118", {"start": v(-19.37, -3.17) * mm, "end": v(-19.47, -3.28) * mm});
            skLineSegment(sketch, "E1119", {"start": v(-19.47, -3.28) * mm, "end": v(-19.57, -3.39) * mm});
            skLineSegment(sketch, "E1120", {"start": v(-19.57, -3.39) * mm, "end": v(-19.65, -3.49) * mm});
            skLineSegment(sketch, "E1121", {"start": v(-19.65, -3.49) * mm, "end": v(-19.73, -3.58) * mm});
            skLineSegment(sketch, "E1122", {"start": v(-19.73, -3.58) * mm, "end": v(-19.8, -3.66) * mm});
            skLineSegment(sketch, "E1123", {"start": v(-21.22, 0.4) * mm, "end": v(-21.1, 0.47) * mm});
            skLineSegment(sketch, "E1124", {"start": v(-21.1, 0.47) * mm, "end": v(-20.96, 0.54) * mm});
            skLineSegment(sketch, "E1125", {"start": v(-20.96, 0.54) * mm, "end": v(-20.84, 0.6) * mm});
            skLineSegment(sketch, "E1126", {"start": v(-20.84, 0.6) * mm, "end": v(-20.71, 0.68) * mm});
            skLineSegment(sketch, "E1127", {"start": v(-20.71, 0.68) * mm, "end": v(-20.6, 0.75) * mm});
            skLineSegment(sketch, "E1128", {"start": v(-20.6, 0.75) * mm, "end": v(-20.47, 0.83) * mm});
            skLineSegment(sketch, "E1129", {"start": v(-20.47, 0.83) * mm, "end": v(-20.35, 0.9) * mm});
            skLineSegment(sketch, "E1130", {"start": v(-20.35, 0.9) * mm, "end": v(-20.24, 0.99) * mm});
            skLineSegment(sketch, "E1131", {"start": v(-20.24, 0.99) * mm, "end": v(-20.12, 1.07) * mm});
            skLineSegment(sketch, "E1132", {"start": v(-20.12, 1.07) * mm, "end": v(-20.01, 1.15) * mm});
            skLineSegment(sketch, "E1133", {"start": v(-20.01, 1.15) * mm, "end": v(-19.9, 1.24) * mm});
            skLineSegment(sketch, "E1134", {"start": v(-19.9, 1.24) * mm, "end": v(-19.79, 1.32) * mm});
            skLineSegment(sketch, "E1135", {"start": v(-19.79, 1.32) * mm, "end": v(-19.68, 1.41) * mm});
            skLineSegment(sketch, "E1136", {"start": v(-19.68, 1.41) * mm, "end": v(-19.57, 1.5) * mm});
            skLineSegment(sketch, "E1137", {"start": v(-19.57, 1.5) * mm, "end": v(-19.47, 1.6) * mm});
            skLineSegment(sketch, "E1138", {"start": v(-19.47, 1.6) * mm, "end": v(-19.37, 1.69) * mm});
            skLineSegment(sketch, "E1139", {"start": v(-19.37, 1.69) * mm, "end": v(-19.26, 1.79) * mm});
            skLineSegment(sketch, "E1140", {"start": v(-19.26, 1.79) * mm, "end": v(-19.16, 1.88) * mm});
            skLineSegment(sketch, "E1141", {"start": v(-19.16, 1.88) * mm, "end": v(-19.06, 1.98) * mm});
            skLineSegment(sketch, "E1142", {"start": v(-19.06, 1.98) * mm, "end": v(-18.96, 2.09) * mm});
            skLineSegment(sketch, "E1143", {"start": v(-18.96, 2.09) * mm, "end": v(-18.87, 2.2) * mm});
            skLineSegment(sketch, "E1144", {"start": v(-18.87, 2.2) * mm, "end": v(-18.82, 2.25) * mm});
            skLineSegment(sketch, "E1145", {"start": v(-23.15, 2.84) * mm, "end": v(-23.43, 2.73) * mm});
            skLineSegment(sketch, "E1146", {"start": v(-23.43, 2.73) * mm, "end": v(-23.72, 2.62) * mm});
            skLineSegment(sketch, "E1147", {"start": v(-23.72, 2.62) * mm, "end": v(-24.04, 2.51) * mm});
            skLineSegment(sketch, "E1148", {"start": v(-24.04, 2.51) * mm, "end": v(-24.37, 2.4) * mm});
            skLineSegment(sketch, "E1149", {"start": v(-24.37, 2.4) * mm, "end": v(-24.72, 2.29) * mm});
            skLineSegment(sketch, "E1150", {"start": v(-24.72, 2.29) * mm, "end": v(-25.08, 2.17) * mm});
            skLineSegment(sketch, "E1151", {"start": v(-25.08, 2.17) * mm, "end": v(-25.47, 2.05) * mm});
            skLineSegment(sketch, "E1152", {"start": v(-25.47, 2.05) * mm, "end": v(-25.87, 1.93) * mm});
            skLineSegment(sketch, "E1153", {"start": v(-25.87, 1.93) * mm, "end": v(-26.3, 1.81) * mm});
            skLineSegment(sketch, "E1154", {"start": v(-26.3, 1.81) * mm, "end": v(-26.73, 1.7) * mm});
            skLineSegment(sketch, "E1155", {"start": v(-26.73, 1.7) * mm, "end": v(-27.2, 1.57) * mm});
            skLineSegment(sketch, "E1156", {"start": v(-27.2, 1.57) * mm, "end": v(-27.68, 1.45) * mm});
            skLineSegment(sketch, "E1157", {"start": v(-27.68, 1.45) * mm, "end": v(-28, 1.36) * mm});
            skLineSegment(sketch, "E1158", {"start": v(-10.98, -12.32) * mm, "end": v(-10.87, -12.32) * mm});
            skLineSegment(sketch, "E1159", {"start": v(-10.87, -12.32) * mm, "end": v(-10.75, -12.3) * mm});
            skLineSegment(sketch, "E1160", {"start": v(-10.75, -12.3) * mm, "end": v(-10.62, -12.29) * mm});
            skLineSegment(sketch, "E1161", {"start": v(-10.62, -12.29) * mm, "end": v(-10.5, -12.26) * mm});
            skLineSegment(sketch, "E1162", {"start": v(-10.5, -12.26) * mm, "end": v(-10.35, -12.23) * mm});
            skLineSegment(sketch, "E1163", {"start": v(-10.35, -12.23) * mm, "end": v(-10.2, -12.18) * mm});
            skLineSegment(sketch, "E1164", {"start": v(-10.2, -12.18) * mm, "end": v(-10.05, -12.12) * mm});
            skLineSegment(sketch, "E1165", {"start": v(-10.05, -12.12) * mm, "end": v(-9.9, -12.05) * mm});
            skLineSegment(sketch, "E1166", {"start": v(-9.9, -12.05) * mm, "end": v(-9.72, -11.97) * mm});
            skLineSegment(sketch, "E1167", {"start": v(-9.72, -11.97) * mm, "end": v(-9.54, -11.88) * mm});
            skLineSegment(sketch, "E1168", {"start": v(-9.54, -11.88) * mm, "end": v(-9.34, -11.78) * mm});
            skLineSegment(sketch, "E1169", {"start": v(-9.34, -11.78) * mm, "end": v(-9.14, -11.66) * mm});
            skLineSegment(sketch, "E1170", {"start": v(-9.14, -11.66) * mm, "end": v(-8.93, -11.52) * mm});
            skLineSegment(sketch, "E1171", {"start": v(-8.93, -11.52) * mm, "end": v(-8.7, -11.37) * mm});
            skLineSegment(sketch, "E1172", {"start": v(-8.7, -11.37) * mm, "end": v(-8.46, -11.2) * mm});
            skLineSegment(sketch, "E1173", {"start": v(-8.46, -11.2) * mm, "end": v(-8.21, -11.02) * mm});
            skLineSegment(sketch, "E1174", {"start": v(-8.21, -11.02) * mm, "end": v(-7.95, -10.8) * mm});
            skLineSegment(sketch, "E1175", {"start": v(-7.95, -10.8) * mm, "end": v(-7.67, -10.58) * mm});
            skLineSegment(sketch, "E1176", {"start": v(-7.67, -10.58) * mm, "end": v(-7.38, -10.34) * mm});
            skLineSegment(sketch, "E1177", {"start": v(-7.38, -10.34) * mm, "end": v(-7.07, -10.07) * mm});
            skLineSegment(sketch, "E1178", {"start": v(-7.07, -10.07) * mm, "end": v(-6.74, -9.77) * mm});
            skLineSegment(sketch, "E1179", {"start": v(-6.74, -9.77) * mm, "end": v(-6.4, -9.46) * mm});
            skLineSegment(sketch, "E1180", {"start": v(-6.4, -9.46) * mm, "end": v(-6.05, -9.11) * mm});
            skLineSegment(sketch, "E1181", {"start": v(-6.05, -9.11) * mm, "end": v(-5.67, -8.74) * mm});
            skLineSegment(sketch, "E1182", {"start": v(-5.67, -8.74) * mm, "end": v(-5.28, -8.35) * mm});
            skLineSegment(sketch, "E1183", {"start": v(-5.28, -8.35) * mm, "end": v(-4.87, -7.92) * mm});
            skLineSegment(sketch, "E1184", {"start": v(-4.87, -7.92) * mm, "end": v(-4.44, -7.46) * mm});
            skLineSegment(sketch, "E1185", {"start": v(-4.44, -7.46) * mm, "end": v(-4, -6.97) * mm});
            skLineSegment(sketch, "E1186", {"start": v(-4, -6.97) * mm, "end": v(-3.8, -6.75) * mm});
            skLineSegment(sketch, "E1187", {"start": v(-44.96, -13.53) * mm, "end": v(-44.94, -13.53) * mm});
            skLineSegment(sketch, "E1188", {"start": v(-44.94, -13.53) * mm, "end": v(-44.92, -13.53) * mm});
            skLineSegment(sketch, "E1189", {"start": v(-44.92, -13.53) * mm, "end": v(-44.9, -13.53) * mm});
            skLineSegment(sketch, "E1190", {"start": v(-44.9, -13.53) * mm, "end": v(-44.87, -13.53) * mm});
            skLineSegment(sketch, "E1191", {"start": v(-44.87, -13.53) * mm, "end": v(-44.85, -13.52) * mm});
            skLineSegment(sketch, "E1192", {"start": v(-44.85, -13.52) * mm, "end": v(-44.82, -13.51) * mm});
            skLineSegment(sketch, "E1193", {"start": v(-44.82, -13.51) * mm, "end": v(-44.79, -13.5) * mm});
            skLineSegment(sketch, "E1194", {"start": v(-44.79, -13.5) * mm, "end": v(-44.76, -13.5) * mm});
            skLineSegment(sketch, "E1195", {"start": v(-44.76, -13.5) * mm, "end": v(-44.73, -13.48) * mm});
            skLineSegment(sketch, "E1196", {"start": v(-44.73, -13.48) * mm, "end": v(-44.7, -13.47) * mm});
            skLineSegment(sketch, "E1197", {"start": v(-44.7, -13.47) * mm, "end": v(-44.66, -13.46) * mm});
            skLineSegment(sketch, "E1198", {"start": v(-44.66, -13.46) * mm, "end": v(-44.62, -13.44) * mm});
            skLineSegment(sketch, "E1199", {"start": v(-44.62, -13.44) * mm, "end": v(-44.58, -13.42) * mm});
            skLineSegment(sketch, "E1200", {"start": v(-44.58, -13.42) * mm, "end": v(-44.53, -13.4) * mm});
            skLineSegment(sketch, "E1201", {"start": v(-44.53, -13.4) * mm, "end": v(-44.48, -13.37) * mm});
            skLineSegment(sketch, "E1202", {"start": v(-44.48, -13.37) * mm, "end": v(-44.43, -13.34) * mm});
            skLineSegment(sketch, "E1203", {"start": v(-44.43, -13.34) * mm, "end": v(-44.38, -13.31) * mm});
            skLineSegment(sketch, "E1204", {"start": v(-44.38, -13.31) * mm, "end": v(-44.32, -13.28) * mm});
            skLineSegment(sketch, "E1205", {"start": v(-44.32, -13.28) * mm, "end": v(-44.26, -13.24) * mm});
            skLineSegment(sketch, "E1206", {"start": v(-44.26, -13.24) * mm, "end": v(-44.2, -13.2) * mm});
            skLineSegment(sketch, "E1207", {"start": v(-44.2, -13.2) * mm, "end": v(-44.12, -13.15) * mm});
            skLineSegment(sketch, "E1208", {"start": v(-44.12, -13.15) * mm, "end": v(-44.04, -13.1) * mm});
            skLineSegment(sketch, "E1209", {"start": v(-44.04, -13.1) * mm, "end": v(-43.96, -13.04) * mm});
            skLineSegment(sketch, "E1210", {"start": v(-43.96, -13.04) * mm, "end": v(-43.86, -12.97) * mm});
            skLineSegment(sketch, "E1211", {"start": v(-43.86, -12.97) * mm, "end": v(-43.79, -12.92) * mm});
            skLineSegment(sketch, "E1212", {"start": v(-17.9, -11.7) * mm, "end": v(-17.85, -11.7) * mm});
            skLineSegment(sketch, "E1213", {"start": v(-17.85, -11.7) * mm, "end": v(-17.8, -11.7) * mm});
            skLineSegment(sketch, "E1214", {"start": v(-17.8, -11.7) * mm, "end": v(-17.75, -11.7) * mm});
            skLineSegment(sketch, "E1215", {"start": v(-17.75, -11.7) * mm, "end": v(-17.7, -11.7) * mm});
            skLineSegment(sketch, "E1216", {"start": v(-17.7, -11.7) * mm, "end": v(-17.63, -11.68) * mm});
            skLineSegment(sketch, "E1217", {"start": v(-17.63, -11.68) * mm, "end": v(-17.58, -11.67) * mm});
            skLineSegment(sketch, "E1218", {"start": v(-17.58, -11.67) * mm, "end": v(-17.51, -11.65) * mm});
            skLineSegment(sketch, "E1219", {"start": v(-17.51, -11.65) * mm, "end": v(-17.45, -11.63) * mm});
            skLineSegment(sketch, "E1220", {"start": v(-17.45, -11.63) * mm, "end": v(-17.39, -11.61) * mm});
            skLineSegment(sketch, "E1221", {"start": v(-17.39, -11.61) * mm, "end": v(-17.32, -11.6) * mm});
            skLineSegment(sketch, "E1222", {"start": v(-17.32, -11.6) * mm, "end": v(-17.26, -11.56) * mm});
            skLineSegment(sketch, "E1223", {"start": v(-17.26, -11.56) * mm, "end": v(-17.19, -11.53) * mm});
            skLineSegment(sketch, "E1224", {"start": v(-17.19, -11.53) * mm, "end": v(-17.12, -11.5) * mm});
            skLineSegment(sketch, "E1225", {"start": v(-17.12, -11.5) * mm, "end": v(-17.04, -11.47) * mm});
            skLineSegment(sketch, "E1226", {"start": v(-17.04, -11.47) * mm, "end": v(-16.97, -11.43) * mm});
            skLineSegment(sketch, "E1227", {"start": v(-16.97, -11.43) * mm, "end": v(-16.9, -11.38) * mm});
            skLineSegment(sketch, "E1228", {"start": v(-16.9, -11.38) * mm, "end": v(-16.81, -11.34) * mm});
            skLineSegment(sketch, "E1229", {"start": v(-16.81, -11.34) * mm, "end": v(-16.73, -11.29) * mm});
            skLineSegment(sketch, "E1230", {"start": v(-16.73, -11.29) * mm, "end": v(-16.65, -11.23) * mm});
            skLineSegment(sketch, "E1231", {"start": v(-16.65, -11.23) * mm, "end": v(-16.56, -11.17) * mm});
            skLineSegment(sketch, "E1232", {"start": v(-16.56, -11.17) * mm, "end": v(-16.47, -11.11) * mm});
            skLineSegment(sketch, "E1233", {"start": v(-16.47, -11.11) * mm, "end": v(-16.38, -11.04) * mm});
            skLineSegment(sketch, "E1234", {"start": v(-16.38, -11.04) * mm, "end": v(-16.3, -10.97) * mm});
            skLineSegment(sketch, "E1235", {"start": v(-16.3, -10.97) * mm, "end": v(-16.2, -10.9) * mm});
            skLineSegment(sketch, "E1236", {"start": v(-16.2, -10.9) * mm, "end": v(-16.1, -10.81) * mm});
            skLineSegment(sketch, "E1237", {"start": v(-16.1, -10.81) * mm, "end": v(-16, -10.73) * mm});
            skLineSegment(sketch, "E1238", {"start": v(-16, -10.73) * mm, "end": v(-15.9, -10.64) * mm});
            skLineSegment(sketch, "E1239", {"start": v(-15.9, -10.64) * mm, "end": v(-15.79, -10.54) * mm});
            skLineSegment(sketch, "E1240", {"start": v(-15.79, -10.54) * mm, "end": v(-15.68, -10.44) * mm});
            skLineSegment(sketch, "E1241", {"start": v(-15.68, -10.44) * mm, "end": v(-15.59, -10.35) * mm});
            skLineSegment(sketch, "E1242", {"start": v(9.13, -11.21) * mm, "end": v(9.15, -11.21) * mm});
            skLineSegment(sketch, "E1243", {"start": v(9.15, -11.21) * mm, "end": v(9.17, -11.21) * mm});
            skLineSegment(sketch, "E1244", {"start": v(9.17, -11.21) * mm, "end": v(9.2, -11.2) * mm});
            skLineSegment(sketch, "E1245", {"start": v(9.2, -11.2) * mm, "end": v(9.22, -11.2) * mm});
            skLineSegment(sketch, "E1246", {"start": v(9.22, -11.2) * mm, "end": v(9.24, -11.2) * mm});
            skLineSegment(sketch, "E1247", {"start": v(9.24, -11.2) * mm, "end": v(9.26, -11.2) * mm});
            skLineSegment(sketch, "E1248", {"start": v(9.26, -11.2) * mm, "end": v(9.29, -11.2) * mm});
            skLineSegment(sketch, "E1249", {"start": v(9.29, -11.2) * mm, "end": v(9.3, -11.19) * mm});
            skLineSegment(sketch, "E1250", {"start": v(9.3, -11.19) * mm, "end": v(9.33, -11.18) * mm});
            skLineSegment(sketch, "E1251", {"start": v(9.33, -11.18) * mm, "end": v(9.35, -11.17) * mm});
            skLineSegment(sketch, "E1252", {"start": v(9.35, -11.17) * mm, "end": v(9.38, -11.17) * mm});
            skLineSegment(sketch, "E1253", {"start": v(9.38, -11.17) * mm, "end": v(9.4, -11.16) * mm});
            skLineSegment(sketch, "E1254", {"start": v(9.4, -11.16) * mm, "end": v(9.43, -11.15) * mm});
            skLineSegment(sketch, "E1255", {"start": v(9.43, -11.15) * mm, "end": v(9.45, -11.14) * mm});
            skLineSegment(sketch, "E1256", {"start": v(9.45, -11.14) * mm, "end": v(9.48, -11.12) * mm});
            skLineSegment(sketch, "E1257", {"start": v(9.48, -11.12) * mm, "end": v(9.5, -11.11) * mm});
            skLineSegment(sketch, "E1258", {"start": v(9.5, -11.11) * mm, "end": v(9.53, -11.1) * mm});
            skLineSegment(sketch, "E1259", {"start": v(9.53, -11.1) * mm, "end": v(9.55, -11.08) * mm});
            skLineSegment(sketch, "E1260", {"start": v(9.55, -11.08) * mm, "end": v(9.58, -11.07) * mm});
            skLineSegment(sketch, "E1261", {"start": v(9.58, -11.07) * mm, "end": v(9.6, -11.05) * mm});
            skLineSegment(sketch, "E1262", {"start": v(9.6, -11.05) * mm, "end": v(9.63, -11.03) * mm});
            skLineSegment(sketch, "E1263", {"start": v(9.63, -11.03) * mm, "end": v(9.65, -11.01) * mm});
            skLineSegment(sketch, "E1264", {"start": v(9.65, -11.01) * mm, "end": v(9.68, -11) * mm});
            skLineSegment(sketch, "E1265", {"start": v(9.68, -11) * mm, "end": v(9.7, -10.97) * mm});
            skLineSegment(sketch, "E1266", {"start": v(9.7, -10.97) * mm, "end": v(9.73, -10.95) * mm});
            skLineSegment(sketch, "E1267", {"start": v(9.73, -10.95) * mm, "end": v(9.76, -10.93) * mm});
            skLineSegment(sketch, "E1268", {"start": v(9.76, -10.93) * mm, "end": v(9.79, -10.9) * mm});
            skLineSegment(sketch, "E1269", {"start": v(9.79, -10.9) * mm, "end": v(9.81, -10.88) * mm});
            skLineSegment(sketch, "E1270", {"start": v(9.81, -10.88) * mm, "end": v(9.84, -10.85) * mm});
            skLineSegment(sketch, "E1271", {"start": v(9.84, -10.85) * mm, "end": v(9.87, -10.82) * mm});
            skLineSegment(sketch, "E1272", {"start": v(9.87, -10.82) * mm, "end": v(9.9, -10.8) * mm});
            skLineSegment(sketch, "E1273", {"start": v(9.9, -10.8) * mm, "end": v(9.93, -10.77) * mm});
            skLineSegment(sketch, "E1274", {"start": v(9.93, -10.77) * mm, "end": v(9.93, -10.76) * mm});
            skLineSegment(sketch, "E1275", {"start": v(15.96, -11.9) * mm, "end": v(16, -11.9) * mm});
            skLineSegment(sketch, "E1276", {"start": v(16, -11.9) * mm, "end": v(16.05, -11.9) * mm});
            skLineSegment(sketch, "E1277", {"start": v(16.05, -11.9) * mm, "end": v(16.1, -11.9) * mm});
            skLineSegment(sketch, "E1278", {"start": v(16.1, -11.9) * mm, "end": v(16.15, -11.9) * mm});
            skLineSegment(sketch, "E1279", {"start": v(16.15, -11.9) * mm, "end": v(16.2, -11.89) * mm});
            skLineSegment(sketch, "E1280", {"start": v(16.2, -11.89) * mm, "end": v(16.25, -11.88) * mm});
            skLineSegment(sketch, "E1281", {"start": v(16.25, -11.88) * mm, "end": v(16.3, -11.87) * mm});
            skLineSegment(sketch, "E1282", {"start": v(16.3, -11.87) * mm, "end": v(16.36, -11.86) * mm});
            skLineSegment(sketch, "E1283", {"start": v(16.36, -11.86) * mm, "end": v(16.41, -11.85) * mm});
            skLineSegment(sketch, "E1284", {"start": v(16.41, -11.85) * mm, "end": v(16.47, -11.83) * mm});
            skLineSegment(sketch, "E1285", {"start": v(16.47, -11.83) * mm, "end": v(16.53, -11.82) * mm});
            skLineSegment(sketch, "E1286", {"start": v(16.53, -11.82) * mm, "end": v(16.58, -11.8) * mm});
            skLineSegment(sketch, "E1287", {"start": v(16.58, -11.8) * mm, "end": v(16.64, -11.78) * mm});
            skLineSegment(sketch, "E1288", {"start": v(16.64, -11.78) * mm, "end": v(16.7, -11.76) * mm});
            skLineSegment(sketch, "E1289", {"start": v(16.7, -11.76) * mm, "end": v(16.77, -11.74) * mm});
            skLineSegment(sketch, "E1290", {"start": v(16.77, -11.74) * mm, "end": v(16.83, -11.71) * mm});
            skLineSegment(sketch, "E1291", {"start": v(16.83, -11.71) * mm, "end": v(16.9, -11.68) * mm});
            skLineSegment(sketch, "E1292", {"start": v(16.9, -11.68) * mm, "end": v(16.96, -11.65) * mm});
            skLineSegment(sketch, "E1293", {"start": v(16.96, -11.65) * mm, "end": v(17.03, -11.62) * mm});
            skLineSegment(sketch, "E1294", {"start": v(17.03, -11.62) * mm, "end": v(17.1, -11.59) * mm});
            skLineSegment(sketch, "E1295", {"start": v(17.1, -11.59) * mm, "end": v(17.18, -11.55) * mm});
            skLineSegment(sketch, "E1296", {"start": v(17.18, -11.55) * mm, "end": v(17.25, -11.51) * mm});
            skLineSegment(sketch, "E1297", {"start": v(17.25, -11.51) * mm, "end": v(17.33, -11.47) * mm});
            skLineSegment(sketch, "E1298", {"start": v(17.33, -11.47) * mm, "end": v(17.4, -11.43) * mm});
            skLineSegment(sketch, "E1299", {"start": v(17.4, -11.43) * mm, "end": v(17.49, -11.38) * mm});
            skLineSegment(sketch, "E1300", {"start": v(17.49, -11.38) * mm, "end": v(17.55, -11.34) * mm});
            skLineSegment(sketch, "E1301", {"start": v(0.83, -9.3) * mm, "end": v(0.93, -9.3) * mm});
            skLineSegment(sketch, "E1302", {"start": v(0.93, -9.3) * mm, "end": v(1.02, -9.3) * mm});
            skLineSegment(sketch, "E1303", {"start": v(1.02, -9.3) * mm, "end": v(1.11, -9.3) * mm});
            skLineSegment(sketch, "E1304", {"start": v(1.11, -9.3) * mm, "end": v(1.21, -9.29) * mm});
            skLineSegment(sketch, "E1305", {"start": v(1.21, -9.29) * mm, "end": v(1.31, -9.27) * mm});
            skLineSegment(sketch, "E1306", {"start": v(1.31, -9.27) * mm, "end": v(1.41, -9.26) * mm});
            skLineSegment(sketch, "E1307", {"start": v(1.41, -9.26) * mm, "end": v(1.52, -9.24) * mm});
            skLineSegment(sketch, "E1308", {"start": v(1.52, -9.24) * mm, "end": v(1.62, -9.22) * mm});
            skLineSegment(sketch, "E1309", {"start": v(1.62, -9.22) * mm, "end": v(1.73, -9.2) * mm});
            skLineSegment(sketch, "E1310", {"start": v(1.73, -9.2) * mm, "end": v(1.84, -9.17) * mm});
            skLineSegment(sketch, "E1311", {"start": v(1.84, -9.17) * mm, "end": v(1.96, -9.14) * mm});
            skLineSegment(sketch, "E1312", {"start": v(1.96, -9.14) * mm, "end": v(2.08, -9.1) * mm});
            skLineSegment(sketch, "E1313", {"start": v(2.08, -9.1) * mm, "end": v(2.2, -9.07) * mm});
            skLineSegment(sketch, "E1314", {"start": v(2.2, -9.07) * mm, "end": v(2.32, -9.03) * mm});
            skLineSegment(sketch, "E1315", {"start": v(2.32, -9.03) * mm, "end": v(2.44, -8.99) * mm});
            skLineSegment(sketch, "E1316", {"start": v(2.44, -8.99) * mm, "end": v(2.57, -8.94) * mm});
            skLineSegment(sketch, "E1317", {"start": v(2.57, -8.94) * mm, "end": v(2.7, -8.89) * mm});
            skLineSegment(sketch, "E1318", {"start": v(2.7, -8.89) * mm, "end": v(2.84, -8.83) * mm});
            skLineSegment(sketch, "E1319", {"start": v(2.84, -8.83) * mm, "end": v(2.98, -8.77) * mm});
            skLineSegment(sketch, "E1320", {"start": v(2.98, -8.77) * mm, "end": v(3.12, -8.7) * mm});
            skLineSegment(sketch, "E1321", {"start": v(3.12, -8.7) * mm, "end": v(3.27, -8.64) * mm});
            skLineSegment(sketch, "E1322", {"start": v(3.27, -8.64) * mm, "end": v(3.42, -8.57) * mm});
            skLineSegment(sketch, "E1323", {"start": v(3.42, -8.57) * mm, "end": v(3.57, -8.5) * mm});
            skLineSegment(sketch, "E1324", {"start": v(3.57, -8.5) * mm, "end": v(3.73, -8.4) * mm});
            skLineSegment(sketch, "E1325", {"start": v(3.73, -8.4) * mm, "end": v(3.83, -8.35) * mm});
            skLineSegment(sketch, "E1326", {"start": v(-2.26, -11.67) * mm, "end": v(-2.34, -11.6) * mm});
            skLineSegment(sketch, "E1327", {"start": v(-2.34, -11.6) * mm, "end": v(-2.4, -11.53) * mm});
            skLineSegment(sketch, "E1328", {"start": v(-2.4, -11.53) * mm, "end": v(-2.48, -11.45) * mm});
            skLineSegment(sketch, "E1329", {"start": v(-2.48, -11.45) * mm, "end": v(-2.55, -11.38) * mm});
            skLineSegment(sketch, "E1330", {"start": v(-2.55, -11.38) * mm, "end": v(-2.61, -11.3) * mm});
            skLineSegment(sketch, "E1331", {"start": v(-2.61, -11.3) * mm, "end": v(-2.68, -11.22) * mm});
            skLineSegment(sketch, "E1332", {"start": v(-2.68, -11.22) * mm, "end": v(-2.75, -11.14) * mm});
            skLineSegment(sketch, "E1333", {"start": v(-2.75, -11.14) * mm, "end": v(-2.81, -11.06) * mm});
            skLineSegment(sketch, "E1334", {"start": v(-2.81, -11.06) * mm, "end": v(-2.88, -10.97) * mm});
            skLineSegment(sketch, "E1335", {"start": v(-2.88, -10.97) * mm, "end": v(-2.94, -10.89) * mm});
            skLineSegment(sketch, "E1336", {"start": v(-2.94, -10.89) * mm, "end": v(-3, -10.8) * mm});
            skLineSegment(sketch, "E1337", {"start": v(-3, -10.8) * mm, "end": v(-3.06, -10.7) * mm});
            skLineSegment(sketch, "E1338", {"start": v(-3.06, -10.7) * mm, "end": v(-3.12, -10.61) * mm});
            skLineSegment(sketch, "E1339", {"start": v(-3.12, -10.61) * mm, "end": v(-3.18, -10.52) * mm});
            skLineSegment(sketch, "E1340", {"start": v(-3.18, -10.52) * mm, "end": v(-3.23, -10.42) * mm});
            skLineSegment(sketch, "E1341", {"start": v(-3.23, -10.42) * mm, "end": v(-3.29, -10.32) * mm});
            skLineSegment(sketch, "E1342", {"start": v(-3.29, -10.32) * mm, "end": v(-3.34, -10.22) * mm});
            skLineSegment(sketch, "E1343", {"start": v(-3.34, -10.22) * mm, "end": v(-3.4, -10.11) * mm});
            skLineSegment(sketch, "E1344", {"start": v(-3.4, -10.11) * mm, "end": v(-3.45, -10) * mm});
            skLineSegment(sketch, "E1345", {"start": v(-3.45, -10) * mm, "end": v(-3.5, -9.9) * mm});
            skLineSegment(sketch, "E1346", {"start": v(-3.5, -9.9) * mm, "end": v(-3.55, -9.78) * mm});
            skLineSegment(sketch, "E1347", {"start": v(-3.55, -9.78) * mm, "end": v(-3.6, -9.67) * mm});
            skLineSegment(sketch, "E1348", {"start": v(-3.6, -9.67) * mm, "end": v(-3.65, -9.55) * mm});
            skLineSegment(sketch, "E1349", {"start": v(-3.65, -9.55) * mm, "end": v(-3.7, -9.43) * mm});
            skLineSegment(sketch, "E1350", {"start": v(-3.7, -9.43) * mm, "end": v(-3.7, -9.4) * mm});
            skLineSegment(sketch, "E1351", {"start": v(-6.35, 1.63) * mm, "end": v(-6.35, 1.65) * mm});
            skLineSegment(sketch, "E1352", {"start": v(-6.35, 1.65) * mm, "end": v(-6.35, 1.66) * mm});
            skLineSegment(sketch, "E1353", {"start": v(-6.35, 1.66) * mm, "end": v(-6.35, 1.68) * mm});
            skLineSegment(sketch, "E1354", {"start": v(-6.35, 1.68) * mm, "end": v(-6.36, 1.7) * mm});
            skLineSegment(sketch, "E1355", {"start": v(-6.36, 1.7) * mm, "end": v(-6.36, 1.71) * mm});
            skLineSegment(sketch, "E1356", {"start": v(-6.36, 1.71) * mm, "end": v(-6.36, 1.73) * mm});
            skLineSegment(sketch, "E1357", {"start": v(-6.36, 1.73) * mm, "end": v(-6.37, 1.76) * mm});
            skLineSegment(sketch, "E1358", {"start": v(-6.37, 1.76) * mm, "end": v(-6.37, 1.78) * mm});
            skLineSegment(sketch, "E1359", {"start": v(-6.37, 1.78) * mm, "end": v(-6.38, 1.8) * mm});
            skLineSegment(sketch, "E1360", {"start": v(-6.38, 1.8) * mm, "end": v(-6.39, 1.83) * mm});
            skLineSegment(sketch, "E1361", {"start": v(-6.39, 1.83) * mm, "end": v(-6.4, 1.86) * mm});
            skLineSegment(sketch, "E1362", {"start": v(-6.4, 1.86) * mm, "end": v(-6.4, 1.89) * mm});
            skLineSegment(sketch, "E1363", {"start": v(-6.4, 1.89) * mm, "end": v(-6.42, 1.92) * mm});
            skLineSegment(sketch, "E1364", {"start": v(-6.42, 1.92) * mm, "end": v(-6.43, 1.96) * mm});
            skLineSegment(sketch, "E1365", {"start": v(-6.43, 1.96) * mm, "end": v(-6.44, 2) * mm});
            skLineSegment(sketch, "E1366", {"start": v(-6.44, 2) * mm, "end": v(-6.46, 2.03) * mm});
            skLineSegment(sketch, "E1367", {"start": v(-6.46, 2.03) * mm, "end": v(-6.48, 2.08) * mm});
            skLineSegment(sketch, "E1368", {"start": v(-6.48, 2.08) * mm, "end": v(-6.5, 2.13) * mm});
            skLineSegment(sketch, "E1369", {"start": v(-6.5, 2.13) * mm, "end": v(-6.52, 2.18) * mm});
            skLineSegment(sketch, "E1370", {"start": v(-6.52, 2.18) * mm, "end": v(-6.54, 2.24) * mm});
            skLineSegment(sketch, "E1371", {"start": v(-6.54, 2.24) * mm, "end": v(-6.57, 2.3) * mm});
            skLineSegment(sketch, "E1372", {"start": v(-11.27, -5.77) * mm, "end": v(-11.34, -5.96) * mm});
            skLineSegment(sketch, "E1373", {"start": v(-11.34, -5.96) * mm, "end": v(-11.46, -6.28) * mm});
            skLineSegment(sketch, "E1374", {"start": v(-11.46, -6.28) * mm, "end": v(-11.57, -6.6) * mm});
            skLineSegment(sketch, "E1375", {"start": v(-11.57, -6.6) * mm, "end": v(-11.68, -6.9) * mm});
            skLineSegment(sketch, "E1376", {"start": v(-11.68, -6.9) * mm, "end": v(-11.77, -7.18) * mm});
            skLineSegment(sketch, "E1377", {"start": v(-11.77, -7.18) * mm, "end": v(-11.86, -7.45) * mm});
            skLineSegment(sketch, "E1378", {"start": v(-11.86, -7.45) * mm, "end": v(-11.94, -7.72) * mm});
            skLineSegment(sketch, "E1379", {"start": v(-11.94, -7.72) * mm, "end": v(-12, -7.97) * mm});
            skLineSegment(sketch, "E1380", {"start": v(-12, -7.97) * mm, "end": v(-12.07, -8.2) * mm});
            skLineSegment(sketch, "E1381", {"start": v(-12.07, -8.2) * mm, "end": v(-12.13, -8.44) * mm});
            skLineSegment(sketch, "E1382", {"start": v(-12.13, -8.44) * mm, "end": v(-12.18, -8.66) * mm});
            skLineSegment(sketch, "E1383", {"start": v(-12.18, -8.66) * mm, "end": v(-12.23, -8.86) * mm});
            skLineSegment(sketch, "E1384", {"start": v(-12.23, -8.86) * mm, "end": v(-12.27, -9.06) * mm});
            skLineSegment(sketch, "E1385", {"start": v(-12.27, -9.06) * mm, "end": v(-12.3, -9.25) * mm});
            skLineSegment(sketch, "E1386", {"start": v(-12.3, -9.25) * mm, "end": v(-12.33, -9.43) * mm});
            skLineSegment(sketch, "E1387", {"start": v(-12.33, -9.43) * mm, "end": v(-12.36, -9.6) * mm});
            skLineSegment(sketch, "E1388", {"start": v(-12.36, -9.6) * mm, "end": v(-12.37, -9.76) * mm});
            skLineSegment(sketch, "E1389", {"start": v(-12.37, -9.76) * mm, "end": v(-12.39, -9.91) * mm});
            skLineSegment(sketch, "E1390", {"start": v(-12.39, -9.91) * mm, "end": v(-12.4, -10.05) * mm});
            skLineSegment(sketch, "E1391", {"start": v(-12.4, -10.05) * mm, "end": v(-12.4, -10.2) * mm});
            skLineSegment(sketch, "E1392", {"start": v(-12.4, -10.2) * mm, "end": v(-12.4, -10.32) * mm});
            skLineSegment(sketch, "E1393", {"start": v(-6.63, 1.1) * mm, "end": v(-6.35, 1.63) * mm});
            skLineSegment(sketch, "E1394", {"start": v(-8.63, 0.24) * mm, "end": v(-9.2, -0.53) * mm});
            skLineSegment(sketch, "E1395", {"start": v(-9.2, -0.53) * mm, "end": v(-9.66, -1.16) * mm});
            skLineSegment(sketch, "E1396", {"start": v(-9.66, -1.16) * mm, "end": v(-10.1, -1.77) * mm});
            skLineSegment(sketch, "E1397", {"start": v(-10.1, -1.77) * mm, "end": v(-10.53, -2.34) * mm});
            skLineSegment(sketch, "E1398", {"start": v(-10.53, -2.34) * mm, "end": v(-10.93, -2.86) * mm});
            skLineSegment(sketch, "E1399", {"start": v(-10.93, -2.86) * mm, "end": v(-11.3, -3.33) * mm});
            skLineSegment(sketch, "E1400", {"start": v(-11.3, -3.33) * mm, "end": v(-11.63, -3.76) * mm});
            skLineSegment(sketch, "E1401", {"start": v(-11.63, -3.76) * mm, "end": v(-11.95, -4.15) * mm});
            skLineSegment(sketch, "E1402", {"start": v(-11.95, -4.15) * mm, "end": v(-12.25, -4.5) * mm});
            skLineSegment(sketch, "E1403", {"start": v(-12.25, -4.5) * mm, "end": v(-12.52, -4.84) * mm});
            skLineSegment(sketch, "E1404", {"start": v(-12.52, -4.84) * mm, "end": v(-12.78, -5.14) * mm});
            skLineSegment(sketch, "E1405", {"start": v(-12.78, -5.14) * mm, "end": v(-12.85, -5.21) * mm});
            skLineSegment(sketch, "E1406", {"start": v(-12.85, -5.21) * mm, "end": v(-13.03, -5.4) * mm});
            skLineSegment(sketch, "E1407", {"start": v(-13.03, -5.4) * mm, "end": v(-13.2, -5.6) * mm});
            skLineSegment(sketch, "E1408", {"start": v(-13.2, -5.6) * mm, "end": v(-13.39, -5.8) * mm});
            skLineSegment(sketch, "E1409", {"start": v(-13.39, -5.8) * mm, "end": v(-13.57, -5.98) * mm});
            skLineSegment(sketch, "E1410", {"start": v(-13.57, -5.98) * mm, "end": v(-13.75, -6.16) * mm});
            skLineSegment(sketch, "E1411", {"start": v(-13.75, -6.16) * mm, "end": v(-13.94, -6.33) * mm});
            skLineSegment(sketch, "E1412", {"start": v(-13.94, -6.33) * mm, "end": v(-14.12, -6.5) * mm});
            skLineSegment(sketch, "E1413", {"start": v(-14.12, -6.5) * mm, "end": v(-14.3, -6.67) * mm});
            skLineSegment(sketch, "E1414", {"start": v(-14.3, -6.67) * mm, "end": v(-14.5, -6.83) * mm});
            skLineSegment(sketch, "E1415", {"start": v(-14.5, -6.83) * mm, "end": v(-14.68, -6.99) * mm});
            skLineSegment(sketch, "E1416", {"start": v(-14.68, -6.99) * mm, "end": v(-14.87, -7.14) * mm});
            skLineSegment(sketch, "E1417", {"start": v(-14.87, -7.14) * mm, "end": v(-15.06, -7.29) * mm});
            skLineSegment(sketch, "E1418", {"start": v(-15.06, -7.29) * mm, "end": v(-15.25, -7.43) * mm});
            skLineSegment(sketch, "E1419", {"start": v(-15.25, -7.43) * mm, "end": v(-15.44, -7.57) * mm});
            skLineSegment(sketch, "E1420", {"start": v(-15.44, -7.57) * mm, "end": v(-15.63, -7.7) * mm});
            skLineSegment(sketch, "E1421", {"start": v(-15.63, -7.7) * mm, "end": v(-15.82, -7.84) * mm});
            skLineSegment(sketch, "E1422", {"start": v(-15.82, -7.84) * mm, "end": v(-16.02, -7.96) * mm});
            skLineSegment(sketch, "E1423", {"start": v(-16.02, -7.96) * mm, "end": v(-16.2, -8.09) * mm});
            skLineSegment(sketch, "E1424", {"start": v(-16.2, -8.09) * mm, "end": v(-16.4, -8.2) * mm});
            skLineSegment(sketch, "E1425", {"start": v(-16.4, -8.2) * mm, "end": v(-16.6, -8.32) * mm});
            skLineSegment(sketch, "E1426", {"start": v(-16, -3.77) * mm, "end": v(-15.75, -3.6) * mm});
            skLineSegment(sketch, "E1427", {"start": v(-15.75, -3.6) * mm, "end": v(-15.5, -3.41) * mm});
            skLineSegment(sketch, "E1428", {"start": v(-15.5, -3.41) * mm, "end": v(-15.2, -3.22) * mm});
            skLineSegment(sketch, "E1429", {"start": v(-15.2, -3.22) * mm, "end": v(-14.89, -3.02) * mm});
            skLineSegment(sketch, "E1430", {"start": v(-14.89, -3.02) * mm, "end": v(-14.55, -2.8) * mm});
            skLineSegment(sketch, "E1431", {"start": v(-14.55, -2.8) * mm, "end": v(-14.17, -2.58) * mm});
            skLineSegment(sketch, "E1432", {"start": v(-14.17, -2.58) * mm, "end": v(-13.77, -2.35) * mm});
            skLineSegment(sketch, "E1433", {"start": v(-13.77, -2.35) * mm, "end": v(-13.33, -2.1) * mm});
            skLineSegment(sketch, "E1434", {"start": v(-13.33, -2.1) * mm, "end": v(-12.86, -1.84) * mm});
            skLineSegment(sketch, "E1435", {"start": v(-12.86, -1.84) * mm, "end": v(-12.35, -1.57) * mm});
            skLineSegment(sketch, "E1436", {"start": v(-12.35, -1.57) * mm, "end": v(-11.8, -1.29) * mm});
            skLineSegment(sketch, "E1437", {"start": v(-11.8, -1.29) * mm, "end": v(-11.21, -0.99) * mm});
            skLineSegment(sketch, "E1438", {"start": v(-11.21, -0.99) * mm, "end": v(-10.58, -0.68) * mm});
            skLineSegment(sketch, "E1439", {"start": v(-10.58, -0.68) * mm, "end": v(-9.9, -0.35) * mm});
            skLineSegment(sketch, "E1440", {"start": v(-9.9, -0.35) * mm, "end": v(-9.17, 0) * mm});
            skLineSegment(sketch, "E1441", {"start": v(-9.17, 0) * mm, "end": v(-8.63, 0.24) * mm});
            skLineSegment(sketch, "E1442", {"start": v(-12.29, 2.12) * mm, "end": v(-12.56, 1.99) * mm});
            skLineSegment(sketch, "E1443", {"start": v(-12.56, 1.99) * mm, "end": v(-12.84, 1.85) * mm});
            skLineSegment(sketch, "E1444", {"start": v(-12.84, 1.85) * mm, "end": v(-13.13, 1.7) * mm});
            skLineSegment(sketch, "E1445", {"start": v(-13.13, 1.7) * mm, "end": v(-13.41, 1.55) * mm});
            skLineSegment(sketch, "E1446", {"start": v(-13.41, 1.55) * mm, "end": v(-13.7, 1.38) * mm});
            skLineSegment(sketch, "E1447", {"start": v(-13.7, 1.38) * mm, "end": v(-13.99, 1.21) * mm});
            skLineSegment(sketch, "E1448", {"start": v(-13.99, 1.21) * mm, "end": v(-14.28, 1.03) * mm});
            skLineSegment(sketch, "E1449", {"start": v(-14.28, 1.03) * mm, "end": v(-14.57, 0.85) * mm});
            skLineSegment(sketch, "E1450", {"start": v(-14.57, 0.85) * mm, "end": v(-14.87, 0.65) * mm});
            skLineSegment(sketch, "E1451", {"start": v(-14.87, 0.65) * mm, "end": v(-15.17, 0.45) * mm});
            skLineSegment(sketch, "E1452", {"start": v(-15.17, 0.45) * mm, "end": v(-15.47, 0.23) * mm});
            skLineSegment(sketch, "E1453", {"start": v(-15.47, 0.23) * mm, "end": v(-15.78, 0.01) * mm});
            skLineSegment(sketch, "E1454", {"start": v(-15.78, 0.01) * mm, "end": v(-16.09, -0.22) * mm});
            skLineSegment(sketch, "E1455", {"start": v(-16.09, -0.22) * mm, "end": v(-16.4, -0.46) * mm});
            skLineSegment(sketch, "E1456", {"start": v(-16.4, -0.46) * mm, "end": v(-16.71, -0.71) * mm});
            skLineSegment(sketch, "E1457", {"start": v(-16.71, -0.71) * mm, "end": v(-17.03, -0.97) * mm});
            skLineSegment(sketch, "E1458", {"start": v(-17.03, -0.97) * mm, "end": v(-17.35, -1.24) * mm});
            skLineSegment(sketch, "E1459", {"start": v(-17.35, -1.24) * mm, "end": v(-17.67, -1.52) * mm});
            skLineSegment(sketch, "E1460", {"start": v(-17.67, -1.52) * mm, "end": v(-18, -1.81) * mm});
            skLineSegment(sketch, "E1461", {"start": v(-18, -1.81) * mm, "end": v(-18.14, -1.94) * mm});
            skLineSegment(sketch, "E1462", {"start": v(28, -9.19) * mm, "end": v(28, -9.19) * mm});
            skLineSegment(sketch, "E1463", {"start": v(28, -9.19) * mm, "end": v(27.95, -9.19) * mm});
            skLineSegment(sketch, "E1464", {"start": v(27.95, -9.19) * mm, "end": v(27.89, -9.18) * mm});
            skLineSegment(sketch, "E1465", {"start": v(27.89, -9.18) * mm, "end": v(27.83, -9.18) * mm});
            skLineSegment(sketch, "E1466", {"start": v(27.83, -9.18) * mm, "end": v(27.77, -9.18) * mm});
            skLineSegment(sketch, "E1467", {"start": v(27.77, -9.18) * mm, "end": v(27.72, -9.17) * mm});
            skLineSegment(sketch, "E1468", {"start": v(27.72, -9.17) * mm, "end": v(27.67, -9.16) * mm});
            skLineSegment(sketch, "E1469", {"start": v(27.67, -9.16) * mm, "end": v(27.61, -9.16) * mm});
            skLineSegment(sketch, "E1470", {"start": v(27.61, -9.16) * mm, "end": v(27.56, -9.15) * mm});
            skLineSegment(sketch, "E1471", {"start": v(27.56, -9.15) * mm, "end": v(27.5, -9.14) * mm});
            skLineSegment(sketch, "E1472", {"start": v(27.5, -9.14) * mm, "end": v(27.46, -9.13) * mm});
            skLineSegment(sketch, "E1473", {"start": v(27.46, -9.13) * mm, "end": v(27.4, -9.11) * mm});
            skLineSegment(sketch, "E1474", {"start": v(27.4, -9.11) * mm, "end": v(27.36, -9.1) * mm});
            skLineSegment(sketch, "E1475", {"start": v(27.36, -9.1) * mm, "end": v(27.31, -9.08) * mm});
            skLineSegment(sketch, "E1476", {"start": v(27.31, -9.08) * mm, "end": v(27.27, -9.07) * mm});
            skLineSegment(sketch, "E1477", {"start": v(27.27, -9.07) * mm, "end": v(27.22, -9.05) * mm});
            skLineSegment(sketch, "E1478", {"start": v(27.22, -9.05) * mm, "end": v(27.17, -9.03) * mm});
            skLineSegment(sketch, "E1479", {"start": v(27.17, -9.03) * mm, "end": v(27.13, -9.01) * mm});
            skLineSegment(sketch, "E1480", {"start": v(27.13, -9.01) * mm, "end": v(27.09, -9) * mm});
            skLineSegment(sketch, "E1481", {"start": v(27.09, -9) * mm, "end": v(27.04, -8.97) * mm});
            skLineSegment(sketch, "E1482", {"start": v(27.04, -8.97) * mm, "end": v(27, -8.95) * mm});
            skLineSegment(sketch, "E1483", {"start": v(27, -8.95) * mm, "end": v(26.96, -8.92) * mm});
            skLineSegment(sketch, "E1484", {"start": v(26.96, -8.92) * mm, "end": v(26.92, -8.9) * mm});
            skLineSegment(sketch, "E1485", {"start": v(26.92, -8.9) * mm, "end": v(26.87, -8.87) * mm});
            skLineSegment(sketch, "E1486", {"start": v(26.87, -8.87) * mm, "end": v(26.83, -8.84) * mm});
            skLineSegment(sketch, "E1487", {"start": v(26.83, -8.84) * mm, "end": v(26.8, -8.81) * mm});
            skLineSegment(sketch, "E1488", {"start": v(26.8, -8.81) * mm, "end": v(26.76, -8.78) * mm});
            skLineSegment(sketch, "E1489", {"start": v(26.76, -8.78) * mm, "end": v(26.72, -8.75) * mm});
            skLineSegment(sketch, "E1490", {"start": v(26.72, -8.75) * mm, "end": v(26.68, -8.72) * mm});
            skLineSegment(sketch, "E1491", {"start": v(26.68, -8.72) * mm, "end": v(26.64, -8.69) * mm});
            skLineSegment(sketch, "E1492", {"start": v(26.64, -8.69) * mm, "end": v(26.6, -8.65) * mm});
            skLineSegment(sketch, "E1493", {"start": v(26.6, -8.65) * mm, "end": v(26.57, -8.62) * mm});
            skLineSegment(sketch, "E1494", {"start": v(26.57, -8.62) * mm, "end": v(26.53, -8.58) * mm});
            skLineSegment(sketch, "E1495", {"start": v(26.53, -8.58) * mm, "end": v(26.5, -8.54) * mm});
            skLineSegment(sketch, "E1496", {"start": v(39.34, -8.9) * mm, "end": v(39.3, -8.9) * mm});
            skLineSegment(sketch, "E1497", {"start": v(39.3, -8.9) * mm, "end": v(39.25, -8.9) * mm});
            skLineSegment(sketch, "E1498", {"start": v(39.25, -8.9) * mm, "end": v(39.2, -8.9) * mm});
            skLineSegment(sketch, "E1499", {"start": v(39.2, -8.9) * mm, "end": v(39.14, -8.9) * mm});
            skLineSegment(sketch, "E1500", {"start": v(39.14, -8.9) * mm, "end": v(39.08, -8.9) * mm});
            skLineSegment(sketch, "E1501", {"start": v(39.08, -8.9) * mm, "end": v(39.03, -8.89) * mm});
            skLineSegment(sketch, "E1502", {"start": v(39.03, -8.89) * mm, "end": v(38.98, -8.88) * mm});
            skLineSegment(sketch, "E1503", {"start": v(38.98, -8.88) * mm, "end": v(38.93, -8.87) * mm});
            skLineSegment(sketch, "E1504", {"start": v(38.93, -8.87) * mm, "end": v(38.88, -8.86) * mm});
            skLineSegment(sketch, "E1505", {"start": v(38.88, -8.86) * mm, "end": v(38.83, -8.85) * mm});
            skLineSegment(sketch, "E1506", {"start": v(38.83, -8.85) * mm, "end": v(38.78, -8.84) * mm});
            skLineSegment(sketch, "E1507", {"start": v(38.78, -8.84) * mm, "end": v(38.73, -8.82) * mm});
            skLineSegment(sketch, "E1508", {"start": v(38.73, -8.82) * mm, "end": v(38.69, -8.8) * mm});
            skLineSegment(sketch, "E1509", {"start": v(38.69, -8.8) * mm, "end": v(38.64, -8.8) * mm});
            skLineSegment(sketch, "E1510", {"start": v(38.64, -8.8) * mm, "end": v(38.6, -8.77) * mm});
            skLineSegment(sketch, "E1511", {"start": v(38.6, -8.77) * mm, "end": v(38.55, -8.75) * mm});
            skLineSegment(sketch, "E1512", {"start": v(38.55, -8.75) * mm, "end": v(38.5, -8.73) * mm});
            skLineSegment(sketch, "E1513", {"start": v(38.5, -8.73) * mm, "end": v(38.47, -8.71) * mm});
            skLineSegment(sketch, "E1514", {"start": v(38.47, -8.71) * mm, "end": v(38.42, -8.7) * mm});
            skLineSegment(sketch, "E1515", {"start": v(38.42, -8.7) * mm, "end": v(38.38, -8.67) * mm});
            skLineSegment(sketch, "E1516", {"start": v(38.38, -8.67) * mm, "end": v(38.34, -8.64) * mm});
            skLineSegment(sketch, "E1517", {"start": v(38.34, -8.64) * mm, "end": v(38.32, -8.63) * mm});
            skLineSegment(sketch, "E1518", {"start": v(38.32, -8.63) * mm, "end": v(38.3, -8.62) * mm});
            skLineSegment(sketch, "E1519", {"start": v(38.3, -8.62) * mm, "end": v(38.26, -8.59) * mm});
            skLineSegment(sketch, "E1520", {"start": v(38.26, -8.59) * mm, "end": v(38.22, -8.56) * mm});
            skLineSegment(sketch, "E1521", {"start": v(38.22, -8.56) * mm, "end": v(38.19, -8.53) * mm});
            skLineSegment(sketch, "E1522", {"start": v(38.19, -8.53) * mm, "end": v(38.15, -8.5) * mm});
            skLineSegment(sketch, "E1523", {"start": v(38.15, -8.5) * mm, "end": v(38.11, -8.47) * mm});
            skLineSegment(sketch, "E1524", {"start": v(38.11, -8.47) * mm, "end": v(38.08, -8.44) * mm});
            skLineSegment(sketch, "E1525", {"start": v(38.08, -8.44) * mm, "end": v(38.04, -8.4) * mm});
            skLineSegment(sketch, "E1526", {"start": v(38.04, -8.4) * mm, "end": v(38, -8.37) * mm});
            skLineSegment(sketch, "E1527", {"start": v(38, -8.37) * mm, "end": v(37.97, -8.33) * mm});
            skLineSegment(sketch, "E1528", {"start": v(37.97, -8.33) * mm, "end": v(37.94, -8.29) * mm});
            skLineSegment(sketch, "E1529", {"start": v(37.94, -8.29) * mm, "end": v(37.9, -8.25) * mm});
            skLineSegment(sketch, "E1530", {"start": v(37.9, -8.25) * mm, "end": v(37.87, -8.2) * mm});
            skLineSegment(sketch, "E1531", {"start": v(37.87, -8.2) * mm, "end": v(37.84, -8.16) * mm});
            skLineSegment(sketch, "E1532", {"start": v(37.84, -8.16) * mm, "end": v(37.81, -8.12) * mm});
            skLineSegment(sketch, "E1533", {"start": v(18.52, -8.06) * mm, "end": v(18.48, -8.06) * mm});
            skLineSegment(sketch, "E1534", {"start": v(18.48, -8.06) * mm, "end": v(18.44, -8.05) * mm});
            skLineSegment(sketch, "E1535", {"start": v(18.44, -8.05) * mm, "end": v(18.4, -8.05) * mm});
            skLineSegment(sketch, "E1536", {"start": v(18.4, -8.05) * mm, "end": v(18.36, -8.05) * mm});
            skLineSegment(sketch, "E1537", {"start": v(18.36, -8.05) * mm, "end": v(18.33, -8.04) * mm});
            skLineSegment(sketch, "E1538", {"start": v(18.33, -8.04) * mm, "end": v(18.3, -8.04) * mm});
            skLineSegment(sketch, "E1539", {"start": v(18.3, -8.04) * mm, "end": v(18.26, -8.03) * mm});
            skLineSegment(sketch, "E1540", {"start": v(18.26, -8.03) * mm, "end": v(18.23, -8.03) * mm});
            skLineSegment(sketch, "E1541", {"start": v(18.23, -8.03) * mm, "end": v(18.2, -8.02) * mm});
            skLineSegment(sketch, "E1542", {"start": v(18.2, -8.02) * mm, "end": v(18.16, -8.01) * mm});
            skLineSegment(sketch, "E1543", {"start": v(18.16, -8.01) * mm, "end": v(18.14, -8) * mm});
            skLineSegment(sketch, "E1544", {"start": v(18.14, -8) * mm, "end": v(18.1, -8) * mm});
            skLineSegment(sketch, "E1545", {"start": v(18.1, -8) * mm, "end": v(18.08, -7.98) * mm});
            skLineSegment(sketch, "E1546", {"start": v(18.08, -7.98) * mm, "end": v(18.05, -7.97) * mm});
            skLineSegment(sketch, "E1547", {"start": v(18.05, -7.97) * mm, "end": v(18.03, -7.96) * mm});
            skLineSegment(sketch, "E1548", {"start": v(18.03, -7.96) * mm, "end": v(18, -7.95) * mm});
            skLineSegment(sketch, "E1549", {"start": v(18, -7.95) * mm, "end": v(17.98, -7.93) * mm});
            skLineSegment(sketch, "E1550", {"start": v(17.98, -7.93) * mm, "end": v(17.96, -7.92) * mm});
            skLineSegment(sketch, "E1551", {"start": v(17.96, -7.92) * mm, "end": v(17.94, -7.9) * mm});
            skLineSegment(sketch, "E1552", {"start": v(17.94, -7.9) * mm, "end": v(17.92, -7.89) * mm});
            skLineSegment(sketch, "E1553", {"start": v(17.92, -7.89) * mm, "end": v(17.9, -7.87) * mm});
            skLineSegment(sketch, "E1554", {"start": v(17.9, -7.87) * mm, "end": v(17.88, -7.86) * mm});
            skLineSegment(sketch, "E1555", {"start": v(17.88, -7.86) * mm, "end": v(17.86, -7.84) * mm});
            skLineSegment(sketch, "E1556", {"start": v(17.86, -7.84) * mm, "end": v(17.84, -7.82) * mm});
            skLineSegment(sketch, "E1557", {"start": v(17.84, -7.82) * mm, "end": v(17.83, -7.8) * mm});
            skLineSegment(sketch, "E1558", {"start": v(17.83, -7.8) * mm, "end": v(17.8, -7.78) * mm});
            skLineSegment(sketch, "E1559", {"start": v(17.8, -7.78) * mm, "end": v(17.8, -7.76) * mm});
            skLineSegment(sketch, "E1560", {"start": v(17.8, -7.76) * mm, "end": v(17.78, -7.74) * mm});
            skLineSegment(sketch, "E1561", {"start": v(17.78, -7.74) * mm, "end": v(17.76, -7.72) * mm});
            skLineSegment(sketch, "E1562", {"start": v(17.76, -7.72) * mm, "end": v(17.75, -7.7) * mm});
            skLineSegment(sketch, "E1563", {"start": v(17.75, -7.7) * mm, "end": v(17.74, -7.67) * mm});
            skLineSegment(sketch, "E1564", {"start": v(17.74, -7.67) * mm, "end": v(17.72, -7.64) * mm});
            skLineSegment(sketch, "E1565", {"start": v(17.72, -7.64) * mm, "end": v(17.71, -7.62) * mm});
            skLineSegment(sketch, "E1566", {"start": v(17.71, -7.62) * mm, "end": v(17.7, -7.6) * mm});
            skLineSegment(sketch, "E1567", {"start": v(17.7, -7.6) * mm, "end": v(17.7, -7.56) * mm});
            skLineSegment(sketch, "E1568", {"start": v(17.7, -7.56) * mm, "end": v(17.68, -7.53) * mm});
            skLineSegment(sketch, "E1569", {"start": v(17.68, -7.53) * mm, "end": v(17.67, -7.5) * mm});
            skLineSegment(sketch, "E1570", {"start": v(17.67, -7.5) * mm, "end": v(17.66, -7.47) * mm});
            skLineSegment(sketch, "E1571", {"start": v(17.66, -7.47) * mm, "end": v(17.66, -7.44) * mm});
            skLineSegment(sketch, "E1572", {"start": v(17.66, -7.44) * mm, "end": v(17.65, -7.4) * mm});
            skLineSegment(sketch, "E1573", {"start": v(17.65, -7.4) * mm, "end": v(17.64, -7.37) * mm});
            skLineSegment(sketch, "E1574", {"start": v(17.64, -7.37) * mm, "end": v(17.64, -7.33) * mm});
            skLineSegment(sketch, "E1575", {"start": v(17.64, -7.33) * mm, "end": v(17.63, -7.3) * mm});
            skLineSegment(sketch, "E1576", {"start": v(17.63, -7.3) * mm, "end": v(17.63, -7.25) * mm});
            skLineSegment(sketch, "E1577", {"start": v(17.63, -7.25) * mm, "end": v(17.63, -7.21) * mm});
            skLineSegment(sketch, "E1578", {"start": v(17.63, -7.21) * mm, "end": v(17.63, -7.17) * mm});
            skLineSegment(sketch, "E1579", {"start": v(17.63, -7.17) * mm, "end": v(17.63, -7.12) * mm});
            skLineSegment(sketch, "E1580", {"start": v(17.63, -7.12) * mm, "end": v(17.63, -7.12) * mm});
            skLineSegment(sketch, "E1581", {"start": v(-8.14, -8.14) * mm, "end": v(-8.2, -8.13) * mm});
            skLineSegment(sketch, "E1582", {"start": v(-8.2, -8.13) * mm, "end": v(-8.26, -8.13) * mm});
            skLineSegment(sketch, "E1583", {"start": v(-8.26, -8.13) * mm, "end": v(-8.32, -8.13) * mm});
            skLineSegment(sketch, "E1584", {"start": v(-8.32, -8.13) * mm, "end": v(-8.38, -8.12) * mm});
            skLineSegment(sketch, "E1585", {"start": v(-8.38, -8.12) * mm, "end": v(-8.43, -8.12) * mm});
            skLineSegment(sketch, "E1586", {"start": v(-8.43, -8.12) * mm, "end": v(-8.48, -8.1) * mm});
            skLineSegment(sketch, "E1587", {"start": v(-8.48, -8.1) * mm, "end": v(-8.53, -8.1) * mm});
            skLineSegment(sketch, "E1588", {"start": v(-8.53, -8.1) * mm, "end": v(-8.58, -8.09) * mm});
            skLineSegment(sketch, "E1589", {"start": v(-8.58, -8.09) * mm, "end": v(-8.63, -8.08) * mm});
            skLineSegment(sketch, "E1590", {"start": v(-8.63, -8.08) * mm, "end": v(-8.67, -8.07) * mm});
            skLineSegment(sketch, "E1591", {"start": v(-8.67, -8.07) * mm, "end": v(-8.72, -8.05) * mm});
            skLineSegment(sketch, "E1592", {"start": v(-8.72, -8.05) * mm, "end": v(-8.76, -8.04) * mm});
            skLineSegment(sketch, "E1593", {"start": v(-8.76, -8.04) * mm, "end": v(-8.8, -8.02) * mm});
            skLineSegment(sketch, "E1594", {"start": v(-8.8, -8.02) * mm, "end": v(-8.84, -8) * mm});
            skLineSegment(sketch, "E1595", {"start": v(-8.84, -8) * mm, "end": v(-8.88, -7.98) * mm});
            skLineSegment(sketch, "E1596", {"start": v(-8.88, -7.98) * mm, "end": v(-8.91, -7.96) * mm});
            skLineSegment(sketch, "E1597", {"start": v(-8.91, -7.96) * mm, "end": v(-8.95, -7.94) * mm});
            skLineSegment(sketch, "E1598", {"start": v(-8.95, -7.94) * mm, "end": v(-8.98, -7.92) * mm});
            skLineSegment(sketch, "E1599", {"start": v(-8.98, -7.92) * mm, "end": v(-9.01, -7.9) * mm});
            skLineSegment(sketch, "E1600", {"start": v(-9.01, -7.9) * mm, "end": v(-9.05, -7.88) * mm});
            skLineSegment(sketch, "E1601", {"start": v(-9.05, -7.88) * mm, "end": v(-9.08, -7.85) * mm});
            skLineSegment(sketch, "E1602", {"start": v(-9.08, -7.85) * mm, "end": v(-9.1, -7.82) * mm});
            skLineSegment(sketch, "E1603", {"start": v(-9.1, -7.82) * mm, "end": v(-9.13, -7.8) * mm});
            skLineSegment(sketch, "E1604", {"start": v(-9.13, -7.8) * mm, "end": v(-9.16, -7.77) * mm});
            skLineSegment(sketch, "E1605", {"start": v(-9.16, -7.77) * mm, "end": v(-9.19, -7.74) * mm});
            skLineSegment(sketch, "E1606", {"start": v(-9.19, -7.74) * mm, "end": v(-9.21, -7.7) * mm});
            skLineSegment(sketch, "E1607", {"start": v(-9.21, -7.7) * mm, "end": v(-9.24, -7.67) * mm});
            skLineSegment(sketch, "E1608", {"start": v(-9.24, -7.67) * mm, "end": v(-9.26, -7.64) * mm});
            skLineSegment(sketch, "E1609", {"start": v(-9.26, -7.64) * mm, "end": v(-9.28, -7.6) * mm});
            skLineSegment(sketch, "E1610", {"start": v(-9.28, -7.6) * mm, "end": v(-9.3, -7.57) * mm});
            skLineSegment(sketch, "E1611", {"start": v(-9.3, -7.57) * mm, "end": v(-9.32, -7.53) * mm});
            skLineSegment(sketch, "E1612", {"start": v(-9.32, -7.53) * mm, "end": v(-9.34, -7.5) * mm});
            skLineSegment(sketch, "E1613", {"start": v(-9.34, -7.5) * mm, "end": v(-9.36, -7.45) * mm});
            skLineSegment(sketch, "E1614", {"start": v(-9.36, -7.45) * mm, "end": v(-9.37, -7.4) * mm});
            skLineSegment(sketch, "E1615", {"start": v(-9.37, -7.4) * mm, "end": v(-9.4, -7.36) * mm});
            skLineSegment(sketch, "E1616", {"start": v(-9.4, -7.36) * mm, "end": v(-9.4, -7.32) * mm});
            skLineSegment(sketch, "E1617", {"start": v(-9.4, -7.32) * mm, "end": v(-9.42, -7.27) * mm});
            skLineSegment(sketch, "E1618", {"start": v(-9.42, -7.27) * mm, "end": v(-9.43, -7.22) * mm});
            skLineSegment(sketch, "E1619", {"start": v(-9.43, -7.22) * mm, "end": v(-9.44, -7.17) * mm});
            skLineSegment(sketch, "E1620", {"start": v(-9.44, -7.17) * mm, "end": v(-9.45, -7.11) * mm});
            skLineSegment(sketch, "E1621", {"start": v(-9.45, -7.11) * mm, "end": v(-9.46, -7.06) * mm});
            skLineSegment(sketch, "E1622", {"start": v(-9.46, -7.06) * mm, "end": v(-9.47, -7) * mm});
            skLineSegment(sketch, "E1623", {"start": v(-9.47, -7) * mm, "end": v(-9.48, -6.94) * mm});
            skLineSegment(sketch, "E1624", {"start": v(-9.48, -6.94) * mm, "end": v(-9.48, -6.87) * mm});
            skLineSegment(sketch, "E1625", {"start": v(-9.48, -6.87) * mm, "end": v(-9.49, -6.8) * mm});
            skLineSegment(sketch, "E1626", {"start": v(-9.49, -6.8) * mm, "end": v(-9.49, -6.74) * mm});
            skLineSegment(sketch, "E1627", {"start": v(-9.49, -6.74) * mm, "end": v(-9.49, -6.67) * mm});
            skLineSegment(sketch, "E1628", {"start": v(-17.37, -8.61) * mm, "end": v(-17.4, -8.61) * mm});
            skLineSegment(sketch, "E1629", {"start": v(-17.4, -8.61) * mm, "end": v(-17.41, -8.61) * mm});
            skLineSegment(sketch, "E1630", {"start": v(-17.41, -8.61) * mm, "end": v(-17.43, -8.6) * mm});
            skLineSegment(sketch, "E1631", {"start": v(-17.43, -8.6) * mm, "end": v(-17.45, -8.6) * mm});
            skLineSegment(sketch, "E1632", {"start": v(-17.45, -8.6) * mm, "end": v(-17.47, -8.6) * mm});
            skLineSegment(sketch, "E1633", {"start": v(-17.47, -8.6) * mm, "end": v(-17.5, -8.6) * mm});
            skLineSegment(sketch, "E1634", {"start": v(-17.5, -8.6) * mm, "end": v(-17.51, -8.6) * mm});
            skLineSegment(sketch, "E1635", {"start": v(-17.51, -8.6) * mm, "end": v(-17.53, -8.6) * mm});
            skLineSegment(sketch, "E1636", {"start": v(-17.53, -8.6) * mm, "end": v(-17.55, -8.6) * mm});
            skLineSegment(sketch, "E1637", {"start": v(-17.55, -8.6) * mm, "end": v(-17.57, -8.59) * mm});
            skLineSegment(sketch, "E1638", {"start": v(-17.57, -8.59) * mm, "end": v(-17.58, -8.58) * mm});
            skLineSegment(sketch, "E1639", {"start": v(-17.58, -8.58) * mm, "end": v(-17.6, -8.57) * mm});
            skLineSegment(sketch, "E1640", {"start": v(-17.6, -8.57) * mm, "end": v(-17.62, -8.57) * mm});
            skLineSegment(sketch, "E1641", {"start": v(-17.62, -8.57) * mm, "end": v(-17.63, -8.56) * mm});
            skLineSegment(sketch, "E1642", {"start": v(-17.63, -8.56) * mm, "end": v(-17.65, -8.55) * mm});
            skLineSegment(sketch, "E1643", {"start": v(-17.65, -8.55) * mm, "end": v(-17.67, -8.54) * mm});
            skLineSegment(sketch, "E1644", {"start": v(-17.67, -8.54) * mm, "end": v(-17.68, -8.54) * mm});
            skLineSegment(sketch, "E1645", {"start": v(-17.68, -8.54) * mm, "end": v(-17.7, -8.53) * mm});
            skLineSegment(sketch, "E1646", {"start": v(-17.7, -8.53) * mm, "end": v(-17.71, -8.52) * mm});
            skLineSegment(sketch, "E1647", {"start": v(-17.71, -8.52) * mm, "end": v(-17.73, -8.5) * mm});
            skLineSegment(sketch, "E1648", {"start": v(-17.73, -8.5) * mm, "end": v(-17.74, -8.5) * mm});
            skLineSegment(sketch, "E1649", {"start": v(-17.74, -8.5) * mm, "end": v(-17.76, -8.48) * mm});
            skLineSegment(sketch, "E1650", {"start": v(-17.76, -8.48) * mm, "end": v(-17.77, -8.47) * mm});
            skLineSegment(sketch, "E1651", {"start": v(-17.77, -8.47) * mm, "end": v(-17.79, -8.46) * mm});
            skLineSegment(sketch, "E1652", {"start": v(-17.79, -8.46) * mm, "end": v(-17.8, -8.45) * mm});
            skLineSegment(sketch, "E1653", {"start": v(-17.8, -8.45) * mm, "end": v(-17.82, -8.43) * mm});
            skLineSegment(sketch, "E1654", {"start": v(-17.82, -8.43) * mm, "end": v(-17.83, -8.42) * mm});
            skLineSegment(sketch, "E1655", {"start": v(-17.83, -8.42) * mm, "end": v(-17.85, -8.4) * mm});
            skLineSegment(sketch, "E1656", {"start": v(-17.85, -8.4) * mm, "end": v(-17.86, -8.39) * mm});
            skLineSegment(sketch, "E1657", {"start": v(-17.86, -8.39) * mm, "end": v(-17.87, -8.37) * mm});
            skLineSegment(sketch, "E1658", {"start": v(-17.87, -8.37) * mm, "end": v(-17.89, -8.35) * mm});
            skLineSegment(sketch, "E1659", {"start": v(-17.89, -8.35) * mm, "end": v(-17.9, -8.34) * mm});
            skLineSegment(sketch, "E1660", {"start": v(-17.9, -8.34) * mm, "end": v(-17.91, -8.32) * mm});
            skLineSegment(sketch, "E1661", {"start": v(-17.91, -8.32) * mm, "end": v(-17.93, -8.3) * mm});
            skLineSegment(sketch, "E1662", {"start": v(-17.93, -8.3) * mm, "end": v(-17.94, -8.28) * mm});
            skLineSegment(sketch, "E1663", {"start": v(-17.94, -8.28) * mm, "end": v(-17.95, -8.26) * mm});
            skLineSegment(sketch, "E1664", {"start": v(-17.95, -8.26) * mm, "end": v(-17.96, -8.23) * mm});
            skLineSegment(sketch, "E1665", {"start": v(-17.96, -8.23) * mm, "end": v(-17.97, -8.22) * mm});
            skLineSegment(sketch, "E1666", {"start": v(-1.14, -8.58) * mm, "end": v(-1.1, -8.63) * mm});
            skLineSegment(sketch, "E1667", {"start": v(-1.1, -8.63) * mm, "end": v(-1.04, -8.67) * mm});
            skLineSegment(sketch, "E1668", {"start": v(-1.04, -8.67) * mm, "end": v(-1, -8.71) * mm});
            skLineSegment(sketch, "E1669", {"start": v(-1, -8.71) * mm, "end": v(-0.94, -8.75) * mm});
            skLineSegment(sketch, "E1670", {"start": v(-0.94, -8.75) * mm, "end": v(-0.9, -8.8) * mm});
            skLineSegment(sketch, "E1671", {"start": v(-0.9, -8.8) * mm, "end": v(-0.84, -8.83) * mm});
            skLineSegment(sketch, "E1672", {"start": v(-0.84, -8.83) * mm, "end": v(-0.79, -8.87) * mm});
            skLineSegment(sketch, "E1673", {"start": v(-0.79, -8.87) * mm, "end": v(-0.76, -8.88) * mm});
            skLineSegment(sketch, "E1674", {"start": v(-0.76, -8.88) * mm, "end": v(-0.73, -8.9) * mm});
            skLineSegment(sketch, "E1675", {"start": v(-0.73, -8.9) * mm, "end": v(-0.68, -8.93) * mm});
            skLineSegment(sketch, "E1676", {"start": v(-0.68, -8.93) * mm, "end": v(-0.62, -8.97) * mm});
            skLineSegment(sketch, "E1677", {"start": v(-0.62, -8.97) * mm, "end": v(-0.57, -9) * mm});
            skLineSegment(sketch, "E1678", {"start": v(-0.57, -9) * mm, "end": v(-0.5, -9.03) * mm});
            skLineSegment(sketch, "E1679", {"start": v(-0.5, -9.03) * mm, "end": v(-0.45, -9.05) * mm});
            skLineSegment(sketch, "E1680", {"start": v(-0.45, -9.05) * mm, "end": v(-0.4, -9.08) * mm});
            skLineSegment(sketch, "E1681", {"start": v(-0.4, -9.08) * mm, "end": v(-0.33, -9.1) * mm});
            skLineSegment(sketch, "E1682", {"start": v(-0.33, -9.1) * mm, "end": v(-0.27, -9.13) * mm});
            skLineSegment(sketch, "E1683", {"start": v(-0.27, -9.13) * mm, "end": v(-0.2, -9.15) * mm});
            skLineSegment(sketch, "E1684", {"start": v(-0.2, -9.15) * mm, "end": v(-0.14, -9.17) * mm});
            skLineSegment(sketch, "E1685", {"start": v(-0.14, -9.17) * mm, "end": v(-0.08, -9.19) * mm});
            skLineSegment(sketch, "E1686", {"start": v(-0.08, -9.19) * mm, "end": v(-0.01, -9.2) * mm});
            skLineSegment(sketch, "E1687", {"start": v(-0.01, -9.2) * mm, "end": v(0.06, -9.22) * mm});
            skLineSegment(sketch, "E1688", {"start": v(0.06, -9.22) * mm, "end": v(0.13, -9.24) * mm});
            skLineSegment(sketch, "E1689", {"start": v(0.13, -9.24) * mm, "end": v(0.2, -9.25) * mm});
            skLineSegment(sketch, "E1690", {"start": v(0.2, -9.25) * mm, "end": v(0.27, -9.26) * mm});
            skLineSegment(sketch, "E1691", {"start": v(0.27, -9.26) * mm, "end": v(0.34, -9.27) * mm});
            skLineSegment(sketch, "E1692", {"start": v(0.34, -9.27) * mm, "end": v(0.41, -9.28) * mm});
            skLineSegment(sketch, "E1693", {"start": v(0.41, -9.28) * mm, "end": v(0.5, -9.3) * mm});
            skLineSegment(sketch, "E1694", {"start": v(0.5, -9.3) * mm, "end": v(0.57, -9.3) * mm});
            skLineSegment(sketch, "E1695", {"start": v(0.57, -9.3) * mm, "end": v(0.65, -9.3) * mm});
            skLineSegment(sketch, "E1696", {"start": v(0.65, -9.3) * mm, "end": v(0.73, -9.3) * mm});
            skLineSegment(sketch, "E1697", {"start": v(0.73, -9.3) * mm, "end": v(0.8, -9.3) * mm});
            skLineSegment(sketch, "E1698", {"start": v(0.8, -9.3) * mm, "end": v(0.83, -9.3) * mm});
            skLineSegment(sketch, "E1699", {"start": v(-17.81, 10.14) * mm, "end": v(-17.88, 10.23) * mm});
            skLineSegment(sketch, "E1700", {"start": v(-17.88, 10.23) * mm, "end": v(-17.95, 10.3) * mm});
            skLineSegment(sketch, "E1701", {"start": v(-17.95, 10.3) * mm, "end": v(-18.02, 10.4) * mm});
            skLineSegment(sketch, "E1702", {"start": v(-18.02, 10.4) * mm, "end": v(-18.1, 10.47) * mm});
            skLineSegment(sketch, "E1703", {"start": v(-18.1, 10.47) * mm, "end": v(-18.18, 10.55) * mm});
            skLineSegment(sketch, "E1704", {"start": v(-18.18, 10.55) * mm, "end": v(-18.26, 10.63) * mm});
            skLineSegment(sketch, "E1705", {"start": v(-18.26, 10.63) * mm, "end": v(-18.34, 10.7) * mm});
            skLineSegment(sketch, "E1706", {"start": v(-18.34, 10.7) * mm, "end": v(-18.42, 10.78) * mm});
            skLineSegment(sketch, "E1707", {"start": v(-18.42, 10.78) * mm, "end": v(-18.51, 10.86) * mm});
            skLineSegment(sketch, "E1708", {"start": v(-18.51, 10.86) * mm, "end": v(-18.6, 10.93) * mm});
            skLineSegment(sketch, "E1709", {"start": v(-18.6, 10.93) * mm, "end": v(-18.7, 11) * mm});
            skLineSegment(sketch, "E1710", {"start": v(-18.7, 11) * mm, "end": v(-18.8, 11.07) * mm});
            skLineSegment(sketch, "E1711", {"start": v(-18.8, 11.07) * mm, "end": v(-18.9, 11.14) * mm});
            skLineSegment(sketch, "E1712", {"start": v(-18.9, 11.14) * mm, "end": v(-19, 11.2) * mm});
            skLineSegment(sketch, "E1713", {"start": v(-19, 11.2) * mm, "end": v(-19.1, 11.27) * mm});
            skLineSegment(sketch, "E1714", {"start": v(-19.1, 11.27) * mm, "end": v(-19.2, 11.34) * mm});
            skLineSegment(sketch, "E1715", {"start": v(-19.2, 11.34) * mm, "end": v(-19.31, 11.4) * mm});
            skLineSegment(sketch, "E1716", {"start": v(-19.31, 11.4) * mm, "end": v(-19.42, 11.46) * mm});
            skLineSegment(sketch, "E1717", {"start": v(-19.42, 11.46) * mm, "end": v(-19.54, 11.52) * mm});
            skLineSegment(sketch, "E1718", {"start": v(-19.54, 11.52) * mm, "end": v(-19.65, 11.58) * mm});
            skLineSegment(sketch, "E1719", {"start": v(-19.65, 11.58) * mm, "end": v(-19.77, 11.64) * mm});
            skLineSegment(sketch, "E1720", {"start": v(-19.77, 11.64) * mm, "end": v(-19.9, 11.7) * mm});
            skLineSegment(sketch, "E1721", {"start": v(-19.9, 11.7) * mm, "end": v(-20.02, 11.75) * mm});
            skLineSegment(sketch, "E1722", {"start": v(-20.02, 11.75) * mm, "end": v(-20.15, 11.8) * mm});
            skLineSegment(sketch, "E1723", {"start": v(-20.15, 11.8) * mm, "end": v(-20.28, 11.85) * mm});
            skLineSegment(sketch, "E1724", {"start": v(-20.28, 11.85) * mm, "end": v(-20.42, 11.9) * mm});
            skLineSegment(sketch, "E1725", {"start": v(-20.42, 11.9) * mm, "end": v(-20.56, 11.95) * mm});
            skLineSegment(sketch, "E1726", {"start": v(-20.56, 11.95) * mm, "end": v(-20.56, 11.95) * mm});
            skLineSegment(sketch, "E1727", {"start": v(-7.21, -0.22) * mm, "end": v(-7.32, 0.02) * mm});
            skLineSegment(sketch, "E1728", {"start": v(-7.32, 0.02) * mm, "end": v(-7.36, 0.1) * mm});
            skLineSegment(sketch, "E1729", {"start": v(-7.36, 0.1) * mm, "end": v(-7.4, 0.2) * mm});
            skLineSegment(sketch, "E1730", {"start": v(-7.4, 0.2) * mm, "end": v(-7.44, 0.28) * mm});
            skLineSegment(sketch, "E1731", {"start": v(-7.44, 0.28) * mm, "end": v(-7.47, 0.36) * mm});
            skLineSegment(sketch, "E1732", {"start": v(-7.47, 0.36) * mm, "end": v(-7.5, 0.44) * mm});
            skLineSegment(sketch, "E1733", {"start": v(-7.5, 0.44) * mm, "end": v(-7.53, 0.51) * mm});
            skLineSegment(sketch, "E1734", {"start": v(-7.53, 0.51) * mm, "end": v(-7.56, 0.58) * mm});
            skLineSegment(sketch, "E1735", {"start": v(-7.56, 0.58) * mm, "end": v(-7.58, 0.64) * mm});
            skLineSegment(sketch, "E1736", {"start": v(-7.58, 0.64) * mm, "end": v(-7.6, 0.7) * mm});
            skLineSegment(sketch, "E1737", {"start": v(-7.13, -0.4) * mm, "end": v(-7.21, -0.22) * mm});
            skLineSegment(sketch, "E1738", {"start": v(-6.9, -0.93) * mm, "end": v(-6.93, -0.87) * mm});
            skLineSegment(sketch, "E1739", {"start": v(-6.93, -0.87) * mm, "end": v(-6.96, -0.8) * mm});
            skLineSegment(sketch, "E1740", {"start": v(-6.96, -0.8) * mm, "end": v(-6.99, -0.73) * mm});
            skLineSegment(sketch, "E1741", {"start": v(-6.99, -0.73) * mm, "end": v(-7.02, -0.66) * mm});
            skLineSegment(sketch, "E1742", {"start": v(-7.02, -0.66) * mm, "end": v(-7.06, -0.58) * mm});
            skLineSegment(sketch, "E1743", {"start": v(-7.06, -0.58) * mm, "end": v(-7.13, -0.4) * mm});
            skLineSegment(sketch, "E1744", {"start": v(-3.7, -9.4) * mm, "end": v(-3.75, -9.28) * mm});
            skLineSegment(sketch, "E1745", {"start": v(-3.75, -9.28) * mm, "end": v(-3.8, -9.15) * mm});
            skLineSegment(sketch, "E1746", {"start": v(-3.8, -9.15) * mm, "end": v(-3.83, -9.02) * mm});
            skLineSegment(sketch, "E1747", {"start": v(-3.83, -9.02) * mm, "end": v(-3.87, -8.9) * mm});
            skLineSegment(sketch, "E1748", {"start": v(-3.87, -8.9) * mm, "end": v(-3.9, -8.76) * mm});
            skLineSegment(sketch, "E1749", {"start": v(-3.9, -8.76) * mm, "end": v(-3.94, -8.63) * mm});
            skLineSegment(sketch, "E1750", {"start": v(-3.94, -8.63) * mm, "end": v(-3.98, -8.5) * mm});
            skLineSegment(sketch, "E1751", {"start": v(-3.98, -8.5) * mm, "end": v(-4, -8.36) * mm});
            skLineSegment(sketch, "E1752", {"start": v(-4, -8.36) * mm, "end": v(-4.04, -8.22) * mm});
            skLineSegment(sketch, "E1753", {"start": v(-4.04, -8.22) * mm, "end": v(-4.06, -8.09) * mm});
            skLineSegment(sketch, "E1754", {"start": v(-4.06, -8.09) * mm, "end": v(-4.09, -7.95) * mm});
            skLineSegment(sketch, "E1755", {"start": v(-4.09, -7.95) * mm, "end": v(-4.11, -7.8) * mm});
            skLineSegment(sketch, "E1756", {"start": v(-4.11, -7.8) * mm, "end": v(-4.13, -7.66) * mm});
            skLineSegment(sketch, "E1757", {"start": v(-4.13, -7.66) * mm, "end": v(-4.15, -7.52) * mm});
            skLineSegment(sketch, "E1758", {"start": v(-4.15, -7.52) * mm, "end": v(-4.16, -7.37) * mm});
            skLineSegment(sketch, "E1759", {"start": v(-4.16, -7.37) * mm, "end": v(-4.18, -7.22) * mm});
            skLineSegment(sketch, "E1760", {"start": v(-4.18, -7.22) * mm, "end": v(-4.19, -7.08) * mm});
            skLineSegment(sketch, "E1761", {"start": v(-4.19, -7.08) * mm, "end": v(-4.2, -6.92) * mm});
            skLineSegment(sketch, "E1762", {"start": v(-4.2, -6.92) * mm, "end": v(-4.2, -6.77) * mm});
            skLineSegment(sketch, "E1763", {"start": v(-4.2, -6.77) * mm, "end": v(-4.2, -6.62) * mm});
            skLineSegment(sketch, "E1764", {"start": v(-4.2, -6.62) * mm, "end": v(-4.2, -6.46) * mm});
            skLineSegment(sketch, "E1765", {"start": v(-4.2, -6.46) * mm, "end": v(-4.2, -6.43) * mm});
            skLineSegment(sketch, "E1766", {"start": v(-6.79, -1.47) * mm, "end": v(-6.9, -0.93) * mm});
            skLineSegment(sketch, "E1767", {"start": v(-3.8, -6.75) * mm, "end": v(-3.8, -5.54) * mm});
            skLineSegment(sketch, "E1768", {"start": v(-4.2, -6.43) * mm, "end": v(-4.2, -6.38) * mm});
            skLineSegment(sketch, "E1769", {"start": v(-4.2, -6.38) * mm, "end": v(-4.2, -6.27) * mm});
            skLineSegment(sketch, "E1770", {"start": v(-4.2, -6.27) * mm, "end": v(-4.2, -6.16) * mm});
            skLineSegment(sketch, "E1771", {"start": v(-4.2, -6.16) * mm, "end": v(-4.2, -6.06) * mm});
            skLineSegment(sketch, "E1772", {"start": v(-4.2, -6.06) * mm, "end": v(-4.19, -5.96) * mm});
            skLineSegment(sketch, "E1773", {"start": v(-4.19, -5.96) * mm, "end": v(-4.18, -5.85) * mm});
            skLineSegment(sketch, "E1774", {"start": v(-4.18, -5.85) * mm, "end": v(-4.17, -5.75) * mm});
            skLineSegment(sketch, "E1775", {"start": v(-4.17, -5.75) * mm, "end": v(-4.15, -5.65) * mm});
            skLineSegment(sketch, "E1776", {"start": v(-4.15, -5.65) * mm, "end": v(-4.14, -5.55) * mm});
            skLineSegment(sketch, "E1777", {"start": v(-4.14, -5.55) * mm, "end": v(-4.12, -5.46) * mm});
            skLineSegment(sketch, "E1778", {"start": v(-4.12, -5.46) * mm, "end": v(-4.1, -5.36) * mm});
            skLineSegment(sketch, "E1779", {"start": v(-4.1, -5.36) * mm, "end": v(-4.08, -5.27) * mm});
            skLineSegment(sketch, "E1780", {"start": v(-4.08, -5.27) * mm, "end": v(-4.06, -5.17) * mm});
            skLineSegment(sketch, "E1781", {"start": v(-4.06, -5.17) * mm, "end": v(-4.04, -5.08) * mm});
            skLineSegment(sketch, "E1782", {"start": v(-4.04, -5.08) * mm, "end": v(-4.01, -4.99) * mm});
            skLineSegment(sketch, "E1783", {"start": v(-4.01, -4.99) * mm, "end": v(-3.98, -4.9) * mm});
            skLineSegment(sketch, "E1784", {"start": v(-3.98, -4.9) * mm, "end": v(-3.96, -4.8) * mm});
            skLineSegment(sketch, "E1785", {"start": v(-3.96, -4.8) * mm, "end": v(-3.92, -4.72) * mm});
            skLineSegment(sketch, "E1786", {"start": v(-3.92, -4.72) * mm, "end": v(-3.9, -4.63) * mm});
            skLineSegment(sketch, "E1787", {"start": v(-3.9, -4.63) * mm, "end": v(-3.87, -4.58) * mm});
            skLineSegment(sketch, "E1788", {"start": v(-3.87, -4.58) * mm, "end": v(-3.86, -4.54) * mm});
            skLineSegment(sketch, "E1789", {"start": v(-3.86, -4.54) * mm, "end": v(-3.82, -4.45) * mm});
            skLineSegment(sketch, "E1790", {"start": v(-3.82, -4.45) * mm, "end": v(-3.78, -4.37) * mm});
            skLineSegment(sketch, "E1791", {"start": v(-3.78, -4.37) * mm, "end": v(-3.74, -4.28) * mm});
            skLineSegment(sketch, "E1792", {"start": v(-3.74, -4.28) * mm, "end": v(-3.7, -4.2) * mm});
            skLineSegment(sketch, "E1793", {"start": v(-3.7, -4.2) * mm, "end": v(-3.65, -4.11) * mm});
            skLineSegment(sketch, "E1794", {"start": v(-3.65, -4.11) * mm, "end": v(-3.6, -4.03) * mm});
            skLineSegment(sketch, "E1795", {"start": v(-9.1, -5.16) * mm, "end": v(-9.04, -5.06) * mm});
            skLineSegment(sketch, "E1796", {"start": v(-9.04, -5.06) * mm, "end": v(-8.96, -4.93) * mm});
            skLineSegment(sketch, "E1797", {"start": v(-8.96, -4.93) * mm, "end": v(-8.86, -4.79) * mm});
            skLineSegment(sketch, "E1798", {"start": v(-8.86, -4.79) * mm, "end": v(-8.82, -4.74) * mm});
            skLineSegment(sketch, "E1799", {"start": v(-8.82, -4.74) * mm, "end": v(-8.7, -4.57) * mm});
            skLineSegment(sketch, "E1800", {"start": v(-8.7, -4.57) * mm, "end": v(-8.58, -4.38) * mm});
            skLineSegment(sketch, "E1801", {"start": v(-7.71, -3.19) * mm, "end": v(-7.61, -3.05) * mm});
            skLineSegment(sketch, "E1802", {"start": v(-7.61, -3.05) * mm, "end": v(-7.52, -2.91) * mm});
            skLineSegment(sketch, "E1803", {"start": v(-7.52, -2.91) * mm, "end": v(-7.43, -2.79) * mm});
            skLineSegment(sketch, "E1804", {"start": v(-7.43, -2.79) * mm, "end": v(-7.36, -2.67) * mm});
            skLineSegment(sketch, "E1805", {"start": v(-7.36, -2.67) * mm, "end": v(-7.28, -2.56) * mm});
            skLineSegment(sketch, "E1806", {"start": v(-7.28, -2.56) * mm, "end": v(-7.22, -2.46) * mm});
            skLineSegment(sketch, "E1807", {"start": v(-7.22, -2.46) * mm, "end": v(-7.16, -2.37) * mm});
            skLineSegment(sketch, "E1808", {"start": v(-7.16, -2.37) * mm, "end": v(-7.1, -2.28) * mm});
            skLineSegment(sketch, "E1809", {"start": v(-7.1, -2.28) * mm, "end": v(-7.06, -2.2) * mm});
            skLineSegment(sketch, "E1810", {"start": v(-7.06, -2.2) * mm, "end": v(-7.02, -2.12) * mm});
            skLineSegment(sketch, "E1811", {"start": v(-7.02, -2.12) * mm, "end": v(-6.98, -2.05) * mm});
            skLineSegment(sketch, "E1812", {"start": v(-6.98, -2.05) * mm, "end": v(-6.95, -1.98) * mm});
            skLineSegment(sketch, "E1813", {"start": v(-6.95, -1.98) * mm, "end": v(-6.92, -1.92) * mm});
            skLineSegment(sketch, "E1814", {"start": v(-6.92, -1.92) * mm, "end": v(-6.9, -1.86) * mm});
            skLineSegment(sketch, "E1815", {"start": v(-6.9, -1.86) * mm, "end": v(-6.87, -1.8) * mm});
            skLineSegment(sketch, "E1816", {"start": v(-6.87, -1.8) * mm, "end": v(-6.85, -1.76) * mm});
            skLineSegment(sketch, "E1817", {"start": v(-6.85, -1.76) * mm, "end": v(-6.84, -1.71) * mm});
            skLineSegment(sketch, "E1818", {"start": v(-6.84, -1.71) * mm, "end": v(-6.82, -1.67) * mm});
            skLineSegment(sketch, "E1819", {"start": v(-6.82, -1.67) * mm, "end": v(-6.81, -1.63) * mm});
            skLineSegment(sketch, "E1820", {"start": v(-6.81, -1.63) * mm, "end": v(-6.8, -1.6) * mm});
            skLineSegment(sketch, "E1821", {"start": v(-6.8, -1.6) * mm, "end": v(-6.8, -1.56) * mm});
            skLineSegment(sketch, "E1822", {"start": v(-6.8, -1.56) * mm, "end": v(-6.8, -1.52) * mm});
            skLineSegment(sketch, "E1823", {"start": v(-6.8, -1.52) * mm, "end": v(-6.79, -1.5) * mm});
            skLineSegment(sketch, "E1824", {"start": v(-6.79, -1.5) * mm, "end": v(-6.79, -1.47) * mm});
            skLineSegment(sketch, "E1825", {"start": v(-8.58, -4.38) * mm, "end": v(-8.28, -3.97) * mm});
            skLineSegment(sketch, "E1826", {"start": v(-8.28, -3.97) * mm, "end": v(-7.71, -3.19) * mm});
            skLineSegment(sketch, "E1827", {"start": v(-12.38, -6.99) * mm, "end": v(-11.27, -5.77) * mm});
            skLineSegment(sketch, "E1828", {"start": v(-15.59, -10.35) * mm, "end": v(-15.32, -10.1) * mm});
            skLineSegment(sketch, "E1829", {"start": v(-15.32, -10.1) * mm, "end": v(-15.01, -9.78) * mm});
            skLineSegment(sketch, "E1830", {"start": v(-15.01, -9.78) * mm, "end": v(-14.97, -9.73) * mm});
            skLineSegment(sketch, "E1831", {"start": v(-14.97, -9.73) * mm, "end": v(-14.6, -9.37) * mm});
            skLineSegment(sketch, "E1832", {"start": v(-14.6, -9.37) * mm, "end": v(-14.22, -8.97) * mm});
            skLineSegment(sketch, "E1833", {"start": v(-14.22, -8.97) * mm, "end": v(-13.8, -8.53) * mm});
            skLineSegment(sketch, "E1834", {"start": v(-13.8, -8.53) * mm, "end": v(-13.36, -8.05) * mm});
            skLineSegment(sketch, "E1835", {"start": v(-13.36, -8.05) * mm, "end": v(-12.38, -6.99) * mm});
            skLineSegment(sketch, "E1836", {"start": v(-7.6, 0.7) * mm, "end": v(-7.47, 0.74) * mm});
            skLineSegment(sketch, "E1837", {"start": v(-7.47, 0.74) * mm, "end": v(-7.35, 0.79) * mm});
            skLineSegment(sketch, "E1838", {"start": v(-7.35, 0.79) * mm, "end": v(-7.25, 0.82) * mm});
            skLineSegment(sketch, "E1839", {"start": v(-7.25, 0.82) * mm, "end": v(-7.16, 0.86) * mm});
            skLineSegment(sketch, "E1840", {"start": v(-7.16, 0.86) * mm, "end": v(-7.09, 0.88) * mm});
            skLineSegment(sketch, "E1841", {"start": v(-7.09, 0.88) * mm, "end": v(-7.02, 0.91) * mm});
            skLineSegment(sketch, "E1842", {"start": v(-7.02, 0.91) * mm, "end": v(-6.96, 0.94) * mm});
            skLineSegment(sketch, "E1843", {"start": v(-6.96, 0.94) * mm, "end": v(-6.9, 0.96) * mm});
            skLineSegment(sketch, "E1844", {"start": v(-6.9, 0.96) * mm, "end": v(-6.85, 0.98) * mm});
            skLineSegment(sketch, "E1845", {"start": v(-6.85, 0.98) * mm, "end": v(-6.8, 1) * mm});
            skLineSegment(sketch, "E1846", {"start": v(-6.8, 1) * mm, "end": v(-6.76, 1.02) * mm});
            skLineSegment(sketch, "E1847", {"start": v(-6.76, 1.02) * mm, "end": v(-6.73, 1.04) * mm});
            skLineSegment(sketch, "E1848", {"start": v(-6.73, 1.04) * mm, "end": v(-6.7, 1.06) * mm});
            skLineSegment(sketch, "E1849", {"start": v(-6.7, 1.06) * mm, "end": v(-6.66, 1.08) * mm});
            skLineSegment(sketch, "E1850", {"start": v(-6.66, 1.08) * mm, "end": v(-6.63, 1.1) * mm});
            skLineSegment(sketch, "E1851", {"start": v(3.47, -3.6) * mm, "end": v(3.45, -3.6) * mm});
            skLineSegment(sketch, "E1852", {"start": v(3.45, -3.6) * mm, "end": v(3.43, -3.6) * mm});
            skLineSegment(sketch, "E1853", {"start": v(3.43, -3.6) * mm, "end": v(3.4, -3.6) * mm});
            skLineSegment(sketch, "E1854", {"start": v(3.4, -3.6) * mm, "end": v(3.38, -3.6) * mm});
            skLineSegment(sketch, "E1855", {"start": v(3.38, -3.6) * mm, "end": v(3.36, -3.6) * mm});
            skLineSegment(sketch, "E1856", {"start": v(3.36, -3.6) * mm, "end": v(3.34, -3.6) * mm});
            skLineSegment(sketch, "E1857", {"start": v(3.34, -3.6) * mm, "end": v(3.32, -3.6) * mm});
            skLineSegment(sketch, "E1858", {"start": v(3.32, -3.6) * mm, "end": v(3.3, -3.6) * mm});
            skLineSegment(sketch, "E1859", {"start": v(3.3, -3.6) * mm, "end": v(3.28, -3.59) * mm});
            skLineSegment(sketch, "E1860", {"start": v(3.28, -3.59) * mm, "end": v(3.27, -3.58) * mm});
            skLineSegment(sketch, "E1861", {"start": v(3.27, -3.58) * mm, "end": v(3.25, -3.58) * mm});
            skLineSegment(sketch, "E1862", {"start": v(3.25, -3.58) * mm, "end": v(3.23, -3.57) * mm});
            skLineSegment(sketch, "E1863", {"start": v(3.23, -3.57) * mm, "end": v(3.22, -3.57) * mm});
            skLineSegment(sketch, "E1864", {"start": v(3.22, -3.57) * mm, "end": v(3.2, -3.56) * mm});
            skLineSegment(sketch, "E1865", {"start": v(3.2, -3.56) * mm, "end": v(3.19, -3.55) * mm});
            skLineSegment(sketch, "E1866", {"start": v(3.19, -3.55) * mm, "end": v(3.17, -3.55) * mm});
            skLineSegment(sketch, "E1867", {"start": v(3.17, -3.55) * mm, "end": v(3.16, -3.54) * mm});
            skLineSegment(sketch, "E1868", {"start": v(3.16, -3.54) * mm, "end": v(3.15, -3.53) * mm});
            skLineSegment(sketch, "E1869", {"start": v(3.15, -3.53) * mm, "end": v(3.14, -3.52) * mm});
            skLineSegment(sketch, "E1870", {"start": v(3.14, -3.52) * mm, "end": v(3.12, -3.51) * mm});
            skLineSegment(sketch, "E1871", {"start": v(3.12, -3.51) * mm, "end": v(3.11, -3.5) * mm});
            skLineSegment(sketch, "E1872", {"start": v(3.11, -3.5) * mm, "end": v(3.1, -3.5) * mm});
            skLineSegment(sketch, "E1873", {"start": v(3.1, -3.5) * mm, "end": v(3.1, -3.48) * mm});
            skLineSegment(sketch, "E1874", {"start": v(3.1, -3.48) * mm, "end": v(3.08, -3.47) * mm});
            skLineSegment(sketch, "E1875", {"start": v(3.08, -3.47) * mm, "end": v(3.07, -3.46) * mm});
            skLineSegment(sketch, "E1876", {"start": v(3.07, -3.46) * mm, "end": v(3.06, -3.45) * mm});
            skLineSegment(sketch, "E1877", {"start": v(3.06, -3.45) * mm, "end": v(3.05, -3.44) * mm});
            skLineSegment(sketch, "E1878", {"start": v(3.05, -3.44) * mm, "end": v(3.04, -3.42) * mm});
            skLineSegment(sketch, "E1879", {"start": v(3.04, -3.42) * mm, "end": v(3.04, -3.41) * mm});
            skLineSegment(sketch, "E1880", {"start": v(3.04, -3.41) * mm, "end": v(3.03, -3.4) * mm});
            skLineSegment(sketch, "E1881", {"start": v(3.03, -3.4) * mm, "end": v(3.02, -3.38) * mm});
            skLineSegment(sketch, "E1882", {"start": v(3.02, -3.38) * mm, "end": v(3.01, -3.37) * mm});
            skLineSegment(sketch, "E1883", {"start": v(3.01, -3.37) * mm, "end": v(3, -3.35) * mm});
            skLineSegment(sketch, "E1884", {"start": v(3, -3.35) * mm, "end": v(3, -3.34) * mm});
            skLineSegment(sketch, "E1885", {"start": v(3, -3.34) * mm, "end": v(3, -3.32) * mm});
            skLineSegment(sketch, "E1886", {"start": v(3, -3.32) * mm, "end": v(2.99, -3.3) * mm});
            skLineSegment(sketch, "E1887", {"start": v(2.99, -3.3) * mm, "end": v(2.98, -3.28) * mm});
            skLineSegment(sketch, "E1888", {"start": v(2.98, -3.28) * mm, "end": v(2.98, -3.27) * mm});
            skLineSegment(sketch, "E1889", {"start": v(2.98, -3.27) * mm, "end": v(2.97, -3.25) * mm});
            skLineSegment(sketch, "E1890", {"start": v(2.97, -3.25) * mm, "end": v(2.97, -3.22) * mm});
            skLineSegment(sketch, "E1891", {"start": v(2.97, -3.22) * mm, "end": v(2.97, -3.2) * mm});
            skLineSegment(sketch, "E1892", {"start": v(2.97, -3.2) * mm, "end": v(2.96, -3.18) * mm});
            skLineSegment(sketch, "E1893", {"start": v(2.96, -3.18) * mm, "end": v(2.96, -3.16) * mm});
            skLineSegment(sketch, "E1894", {"start": v(2.96, -3.16) * mm, "end": v(2.96, -3.13) * mm});
            skLineSegment(sketch, "E1895", {"start": v(2.96, -3.13) * mm, "end": v(2.96, -3.1) * mm});
            skLineSegment(sketch, "E1896", {"start": v(2.96, -3.1) * mm, "end": v(2.96, -3.08) * mm});
            skLineSegment(sketch, "E1897", {"start": v(2.96, -3.08) * mm, "end": v(2.96, -3.05) * mm});
            skLineSegment(sketch, "E1898", {"start": v(-7.13, 3.1) * mm, "end": v(-7.14, 3.12) * mm});
            skLineSegment(sketch, "E1899", {"start": v(-7.14, 3.12) * mm, "end": v(-7.17, 3.14) * mm});
            skLineSegment(sketch, "E1900", {"start": v(-7.17, 3.14) * mm, "end": v(-7.2, 3.16) * mm});
            skLineSegment(sketch, "E1901", {"start": v(-7.2, 3.16) * mm, "end": v(-7.22, 3.18) * mm});
            skLineSegment(sketch, "E1902", {"start": v(-7.22, 3.18) * mm, "end": v(-7.24, 3.2) * mm});
            skLineSegment(sketch, "E1903", {"start": v(-7.24, 3.2) * mm, "end": v(-7.26, 3.22) * mm});
            skLineSegment(sketch, "E1904", {"start": v(-7.26, 3.22) * mm, "end": v(-7.29, 3.24) * mm});
            skLineSegment(sketch, "E1905", {"start": v(-7.29, 3.24) * mm, "end": v(-7.31, 3.26) * mm});
            skLineSegment(sketch, "E1906", {"start": v(-7.31, 3.26) * mm, "end": v(-7.34, 3.27) * mm});
            skLineSegment(sketch, "E1907", {"start": v(-7.34, 3.27) * mm, "end": v(-7.36, 3.3) * mm});
            skLineSegment(sketch, "E1908", {"start": v(-7.36, 3.3) * mm, "end": v(-7.38, 3.3) * mm});
            skLineSegment(sketch, "E1909", {"start": v(-7.38, 3.3) * mm, "end": v(-7.4, 3.32) * mm});
            skLineSegment(sketch, "E1910", {"start": v(-7.4, 3.32) * mm, "end": v(-7.43, 3.33) * mm});
            skLineSegment(sketch, "E1911", {"start": v(-7.43, 3.33) * mm, "end": v(-7.46, 3.35) * mm});
            skLineSegment(sketch, "E1912", {"start": v(-7.46, 3.35) * mm, "end": v(-7.48, 3.36) * mm});
            skLineSegment(sketch, "E1913", {"start": v(-7.48, 3.36) * mm, "end": v(-7.5, 3.37) * mm});
            skLineSegment(sketch, "E1914", {"start": v(-7.5, 3.37) * mm, "end": v(-7.53, 3.38) * mm});
            skLineSegment(sketch, "E1915", {"start": v(-7.53, 3.38) * mm, "end": v(-7.55, 3.4) * mm});
            skLineSegment(sketch, "E1916", {"start": v(-7.55, 3.4) * mm, "end": v(-7.58, 3.4) * mm});
            skLineSegment(sketch, "E1917", {"start": v(-7.58, 3.4) * mm, "end": v(-7.6, 3.4) * mm});
            skLineSegment(sketch, "E1918", {"start": v(-7.6, 3.4) * mm, "end": v(-7.63, 3.42) * mm});
            skLineSegment(sketch, "E1919", {"start": v(-7.63, 3.42) * mm, "end": v(-7.65, 3.42) * mm});
            skLineSegment(sketch, "E1920", {"start": v(-7.65, 3.42) * mm, "end": v(-7.67, 3.43) * mm});
            skLineSegment(sketch, "E1921", {"start": v(-7.67, 3.43) * mm, "end": v(-7.7, 3.44) * mm});
            skLineSegment(sketch, "E1922", {"start": v(-7.7, 3.44) * mm, "end": v(-7.72, 3.44) * mm});
            skLineSegment(sketch, "E1923", {"start": v(-7.72, 3.44) * mm, "end": v(-7.75, 3.44) * mm});
            skLineSegment(sketch, "E1924", {"start": v(-7.75, 3.44) * mm, "end": v(-7.77, 3.45) * mm});
            skLineSegment(sketch, "E1925", {"start": v(-7.77, 3.45) * mm, "end": v(-7.8, 3.45) * mm});
            skLineSegment(sketch, "E1926", {"start": v(-7.8, 3.45) * mm, "end": v(-7.82, 3.45) * mm});
            skLineSegment(sketch, "E1927", {"start": v(-7.82, 3.45) * mm, "end": v(-7.85, 3.46) * mm});
            skLineSegment(sketch, "E1928", {"start": v(-7.85, 3.46) * mm, "end": v(-7.87, 3.46) * mm});
            skLineSegment(sketch, "E1929", {"start": v(-7.87, 3.46) * mm, "end": v(-7.9, 3.46) * mm});
            skLineSegment(sketch, "E1930", {"start": v(-6.57, 2.3) * mm, "end": v(-6.6, 2.35) * mm});
            skLineSegment(sketch, "E1931", {"start": v(-6.6, 2.35) * mm, "end": v(-6.61, 2.39) * mm});
            skLineSegment(sketch, "E1932", {"start": v(-6.61, 2.39) * mm, "end": v(-6.63, 2.43) * mm});
            skLineSegment(sketch, "E1933", {"start": v(-6.63, 2.43) * mm, "end": v(-6.66, 2.47) * mm});
            skLineSegment(sketch, "E1934", {"start": v(-6.66, 2.47) * mm, "end": v(-6.68, 2.5) * mm});
            skLineSegment(sketch, "E1935", {"start": v(-6.68, 2.5) * mm, "end": v(-6.7, 2.55) * mm});
            skLineSegment(sketch, "E1936", {"start": v(-6.7, 2.55) * mm, "end": v(-6.72, 2.59) * mm});
            skLineSegment(sketch, "E1937", {"start": v(-6.72, 2.59) * mm, "end": v(-6.75, 2.62) * mm});
            skLineSegment(sketch, "E1938", {"start": v(-6.75, 2.62) * mm, "end": v(-6.77, 2.66) * mm});
            skLineSegment(sketch, "E1939", {"start": v(-6.77, 2.66) * mm, "end": v(-6.8, 2.7) * mm});
            skLineSegment(sketch, "E1940", {"start": v(-6.8, 2.7) * mm, "end": v(-6.82, 2.74) * mm});
            skLineSegment(sketch, "E1941", {"start": v(-6.82, 2.74) * mm, "end": v(-6.85, 2.77) * mm});
            skLineSegment(sketch, "E1942", {"start": v(-6.85, 2.77) * mm, "end": v(-6.87, 2.8) * mm});
            skLineSegment(sketch, "E1943", {"start": v(-6.87, 2.8) * mm, "end": v(-6.9, 2.84) * mm});
            skLineSegment(sketch, "E1944", {"start": v(-6.9, 2.84) * mm, "end": v(-6.93, 2.88) * mm});
            skLineSegment(sketch, "E1945", {"start": v(-6.93, 2.88) * mm, "end": v(-6.96, 2.92) * mm});
            skLineSegment(sketch, "E1946", {"start": v(-6.96, 2.92) * mm, "end": v(-6.99, 2.95) * mm});
            skLineSegment(sketch, "E1947", {"start": v(-6.99, 2.95) * mm, "end": v(-7.02, 2.99) * mm});
            skLineSegment(sketch, "E1948", {"start": v(-7.02, 2.99) * mm, "end": v(-7.05, 3.02) * mm});
            skLineSegment(sketch, "E1949", {"start": v(-7.05, 3.02) * mm, "end": v(-7.08, 3.05) * mm});
            skLineSegment(sketch, "E1950", {"start": v(-7.08, 3.05) * mm, "end": v(-7.11, 3.09) * mm});
            skLineSegment(sketch, "E1951", {"start": v(-7.11, 3.09) * mm, "end": v(-7.13, 3.1) * mm});
            skLineSegment(sketch, "E1952", {"start": v(-1.89, -6.67) * mm, "end": v(-1.89, -6.68) * mm});
            skLineSegment(sketch, "E1953", {"start": v(-1.89, -6.68) * mm, "end": v(-1.88, -6.76) * mm});
            skLineSegment(sketch, "E1954", {"start": v(-1.88, -6.76) * mm, "end": v(-1.88, -6.84) * mm});
            skLineSegment(sketch, "E1955", {"start": v(-1.88, -6.84) * mm, "end": v(-1.88, -6.91) * mm});
            skLineSegment(sketch, "E1956", {"start": v(-1.88, -6.91) * mm, "end": v(-1.87, -6.99) * mm});
            skLineSegment(sketch, "E1957", {"start": v(-1.87, -6.99) * mm, "end": v(-1.86, -7.06) * mm});
            skLineSegment(sketch, "E1958", {"start": v(-1.86, -7.06) * mm, "end": v(-1.86, -7.13) * mm});
            skLineSegment(sketch, "E1959", {"start": v(-1.86, -7.13) * mm, "end": v(-1.85, -7.2) * mm});
            skLineSegment(sketch, "E1960", {"start": v(-1.85, -7.2) * mm, "end": v(-1.83, -7.27) * mm});
            skLineSegment(sketch, "E1961", {"start": v(-1.83, -7.27) * mm, "end": v(-1.82, -7.33) * mm});
            skLineSegment(sketch, "E1962", {"start": v(-1.82, -7.33) * mm, "end": v(-1.8, -7.4) * mm});
            skLineSegment(sketch, "E1963", {"start": v(-1.8, -7.4) * mm, "end": v(-1.8, -7.46) * mm});
            skLineSegment(sketch, "E1964", {"start": v(-1.8, -7.46) * mm, "end": v(-1.77, -7.53) * mm});
            skLineSegment(sketch, "E1965", {"start": v(-1.77, -7.53) * mm, "end": v(-1.76, -7.59) * mm});
            skLineSegment(sketch, "E1966", {"start": v(-1.76, -7.59) * mm, "end": v(-1.74, -7.65) * mm});
            skLineSegment(sketch, "E1967", {"start": v(-1.74, -7.65) * mm, "end": v(-1.71, -7.71) * mm});
            skLineSegment(sketch, "E1968", {"start": v(-1.71, -7.71) * mm, "end": v(-1.7, -7.77) * mm});
            skLineSegment(sketch, "E1969", {"start": v(-1.7, -7.77) * mm, "end": v(-1.67, -7.83) * mm});
            skLineSegment(sketch, "E1970", {"start": v(-1.67, -7.83) * mm, "end": v(-1.64, -7.88) * mm});
            skLineSegment(sketch, "E1971", {"start": v(-1.64, -7.88) * mm, "end": v(-1.62, -7.94) * mm});
            skLineSegment(sketch, "E1972", {"start": v(-1.62, -7.94) * mm, "end": v(-1.59, -8) * mm});
            skLineSegment(sketch, "E1973", {"start": v(-1.59, -8) * mm, "end": v(-1.56, -8.05) * mm});
            skLineSegment(sketch, "E1974", {"start": v(-1.56, -8.05) * mm, "end": v(-1.53, -8.1) * mm});
            skLineSegment(sketch, "E1975", {"start": v(-1.53, -8.1) * mm, "end": v(-1.5, -8.15) * mm});
            skLineSegment(sketch, "E1976", {"start": v(-1.5, -8.15) * mm, "end": v(-1.46, -8.2) * mm});
            skLineSegment(sketch, "E1977", {"start": v(-1.46, -8.2) * mm, "end": v(-1.43, -8.25) * mm});
            skLineSegment(sketch, "E1978", {"start": v(-1.43, -8.25) * mm, "end": v(-1.4, -8.3) * mm});
            skLineSegment(sketch, "E1979", {"start": v(-1.4, -8.3) * mm, "end": v(-1.35, -8.35) * mm});
            skLineSegment(sketch, "E1980", {"start": v(-1.35, -8.35) * mm, "end": v(-1.31, -8.4) * mm});
            skLineSegment(sketch, "E1981", {"start": v(-1.31, -8.4) * mm, "end": v(-1.27, -8.45) * mm});
            skLineSegment(sketch, "E1982", {"start": v(-1.27, -8.45) * mm, "end": v(-1.23, -8.5) * mm});
            skLineSegment(sketch, "E1983", {"start": v(-1.23, -8.5) * mm, "end": v(-1.19, -8.54) * mm});
            skLineSegment(sketch, "E1984", {"start": v(-1.19, -8.54) * mm, "end": v(-1.14, -8.58) * mm});
            skLineSegment(sketch, "E1985", {"start": v(-3.6, -4.03) * mm, "end": v(-3.55, -3.93) * mm});
            skLineSegment(sketch, "E1986", {"start": v(-3.55, -3.93) * mm, "end": v(-3.49, -3.82) * mm});
            skLineSegment(sketch, "E1987", {"start": v(-3.49, -3.82) * mm, "end": v(-3.41, -3.71) * mm});
            skLineSegment(sketch, "E1988", {"start": v(-3.41, -3.71) * mm, "end": v(-3.34, -3.6) * mm});
            skLineSegment(sketch, "E1989", {"start": v(-3.34, -3.6) * mm, "end": v(-3.25, -3.47) * mm});
            skLineSegment(sketch, "E1990", {"start": v(-3.25, -3.47) * mm, "end": v(-3.16, -3.35) * mm});
            skLineSegment(sketch, "E1991", {"start": v(-3.16, -3.35) * mm, "end": v(-3.06, -3.22) * mm});
            skLineSegment(sketch, "E1992", {"start": v(-3.06, -3.22) * mm, "end": v(-2.95, -3.08) * mm});
            skLineSegment(sketch, "E1993", {"start": v(-2.95, -3.08) * mm, "end": v(-2.84, -2.94) * mm});
            skLineSegment(sketch, "E1994", {"start": v(-2.84, -2.94) * mm, "end": v(-2.72, -2.79) * mm});
            skLineSegment(sketch, "E1995", {"start": v(-2.72, -2.79) * mm, "end": v(-2.58, -2.64) * mm});
            skLineSegment(sketch, "E1996", {"start": v(-2.58, -2.64) * mm, "end": v(-2.44, -2.48) * mm});
            skLineSegment(sketch, "E1997", {"start": v(-2.44, -2.48) * mm, "end": v(-2.3, -2.31) * mm});
            skLineSegment(sketch, "E1998", {"start": v(-2.3, -2.31) * mm, "end": v(-2.14, -2.14) * mm});
            skLineSegment(sketch, "E1999", {"start": v(-2.14, -2.14) * mm, "end": v(-1.97, -1.96) * mm});
            skLineSegment(sketch, "E2000", {"start": v(-1.97, -1.96) * mm, "end": v(-1.8, -1.78) * mm});
            skLineSegment(sketch, "E2001", {"start": v(-1.8, -1.78) * mm, "end": v(-1.6, -1.6) * mm});
            skLineSegment(sketch, "E2002", {"start": v(-1.6, -1.6) * mm, "end": v(-1.4, -1.4) * mm});
            skLineSegment(sketch, "E2003", {"start": v(-1.4, -1.4) * mm, "end": v(-1.24, -1.24) * mm});
            skLineSegment(sketch, "E2004", {"start": v(-1.24, -1.24) * mm, "end": v(-0.96, -0.97) * mm});
            skLineSegment(sketch, "E2005", {"start": v(-0.96, -0.97) * mm, "end": v(-0.69, -0.72) * mm});
            skLineSegment(sketch, "E2006", {"start": v(-0.69, -0.72) * mm, "end": v(-0.43, -0.47) * mm});
            skLineSegment(sketch, "E2007", {"start": v(-0.43, -0.47) * mm, "end": v(-0.17, -0.24) * mm});
            skLineSegment(sketch, "E2008", {"start": v(-0.17, -0.24) * mm, "end": v(0.08, -0.03) * mm});
            skLineSegment(sketch, "E2009", {"start": v(0.08, -0.03) * mm, "end": v(0.32, 0.18) * mm});
            skLineSegment(sketch, "E2010", {"start": v(0.32, 0.18) * mm, "end": v(0.56, 0.38) * mm});
            skLineSegment(sketch, "E2011", {"start": v(0.56, 0.38) * mm, "end": v(0.8, 0.57) * mm});
            skLineSegment(sketch, "E2012", {"start": v(0.8, 0.57) * mm, "end": v(1.02, 0.75) * mm});
            skLineSegment(sketch, "E2013", {"start": v(1.02, 0.75) * mm, "end": v(1.24, 0.91) * mm});
            skLineSegment(sketch, "E2014", {"start": v(1.24, 0.91) * mm, "end": v(1.45, 1.07) * mm});
            skLineSegment(sketch, "E2015", {"start": v(1.45, 1.07) * mm, "end": v(1.66, 1.23) * mm});
            skLineSegment(sketch, "E2016", {"start": v(1.66, 1.23) * mm, "end": v(1.86, 1.37) * mm});
            skLineSegment(sketch, "E2017", {"start": v(1.86, 1.37) * mm, "end": v(2.06, 1.5) * mm});
            skLineSegment(sketch, "E2018", {"start": v(2.06, 1.5) * mm, "end": v(2.25, 1.63) * mm});
            skLineSegment(sketch, "E2019", {"start": v(2.25, 1.63) * mm, "end": v(2.44, 1.75) * mm});
            skLineSegment(sketch, "E2020", {"start": v(2.44, 1.75) * mm, "end": v(2.5, 1.78) * mm});
            skLineSegment(sketch, "E2021", {"start": v(2.5, 1.78) * mm, "end": v(2.66, 1.88) * mm});
            skLineSegment(sketch, "E2022", {"start": v(2.66, 1.88) * mm, "end": v(2.82, 1.98) * mm});
            skLineSegment(sketch, "E2023", {"start": v(2.82, 1.98) * mm, "end": v(2.97, 2.06) * mm});
            skLineSegment(sketch, "E2024", {"start": v(2.97, 2.06) * mm, "end": v(3.11, 2.14) * mm});
            skLineSegment(sketch, "E2025", {"start": v(3.11, 2.14) * mm, "end": v(3.26, 2.22) * mm});
            skLineSegment(sketch, "E2026", {"start": v(3.26, 2.22) * mm, "end": v(3.4, 2.29) * mm});
            skLineSegment(sketch, "E2027", {"start": v(3.4, 2.29) * mm, "end": v(3.52, 2.35) * mm});
            skLineSegment(sketch, "E2028", {"start": v(3.52, 2.35) * mm, "end": v(3.64, 2.41) * mm});
            skLineSegment(sketch, "E2029", {"start": v(3.64, 2.41) * mm, "end": v(3.76, 2.47) * mm});
            skLineSegment(sketch, "E2030", {"start": v(3.76, 2.47) * mm, "end": v(3.88, 2.52) * mm});
            skLineSegment(sketch, "E2031", {"start": v(3.88, 2.52) * mm, "end": v(4, 2.56) * mm});
            skLineSegment(sketch, "E2032", {"start": v(4, 2.56) * mm, "end": v(4.1, 2.6) * mm});
            skLineSegment(sketch, "E2033", {"start": v(4.1, 2.6) * mm, "end": v(4.2, 2.64) * mm});
            skLineSegment(sketch, "E2034", {"start": v(4.2, 2.64) * mm, "end": v(4.3, 2.68) * mm});
            skLineSegment(sketch, "E2035", {"start": v(4.3, 2.68) * mm, "end": v(4.4, 2.7) * mm});
            skLineSegment(sketch, "E2036", {"start": v(4.4, 2.7) * mm, "end": v(4.49, 2.74) * mm});
            skLineSegment(sketch, "E2037", {"start": v(4.49, 2.74) * mm, "end": v(4.58, 2.76) * mm});
            skLineSegment(sketch, "E2038", {"start": v(4.58, 2.76) * mm, "end": v(4.66, 2.78) * mm});
            skLineSegment(sketch, "E2039", {"start": v(4.66, 2.78) * mm, "end": v(4.75, 2.8) * mm});
            skLineSegment(sketch, "E2040", {"start": v(4.75, 2.8) * mm, "end": v(4.83, 2.81) * mm});
            skLineSegment(sketch, "E2041", {"start": v(4.83, 2.81) * mm, "end": v(4.9, 2.82) * mm});
            skLineSegment(sketch, "E2042", {"start": v(4.9, 2.82) * mm, "end": v(4.98, 2.83) * mm});
            skLineSegment(sketch, "E2043", {"start": v(4.98, 2.83) * mm, "end": v(5.05, 2.84) * mm});
            skLineSegment(sketch, "E2044", {"start": v(5.05, 2.84) * mm, "end": v(5.11, 2.84) * mm});
            skLineSegment(sketch, "E2045", {"start": v(5.11, 2.84) * mm, "end": v(5.18, 2.84) * mm});
            skLineSegment(sketch, "E2046", {"start": v(-16.6, -8.32) * mm, "end": v(-16.65, -8.35) * mm});
            skLineSegment(sketch, "E2047", {"start": v(-16.65, -8.35) * mm, "end": v(-16.7, -8.37) * mm});
            skLineSegment(sketch, "E2048", {"start": v(-16.7, -8.37) * mm, "end": v(-16.74, -8.4) * mm});
            skLineSegment(sketch, "E2049", {"start": v(-16.74, -8.4) * mm, "end": v(-16.78, -8.42) * mm});
            skLineSegment(sketch, "E2050", {"start": v(-16.78, -8.42) * mm, "end": v(-16.83, -8.44) * mm});
            skLineSegment(sketch, "E2051", {"start": v(-16.83, -8.44) * mm, "end": v(-16.83, -8.44) * mm});
            skLineSegment(sketch, "E2052", {"start": v(-16.83, -8.44) * mm, "end": v(-16.87, -8.46) * mm});
            skLineSegment(sketch, "E2053", {"start": v(-16.87, -8.46) * mm, "end": v(-16.9, -8.48) * mm});
            skLineSegment(sketch, "E2054", {"start": v(-16.9, -8.48) * mm, "end": v(-16.95, -8.5) * mm});
            skLineSegment(sketch, "E2055", {"start": v(-16.95, -8.5) * mm, "end": v(-16.98, -8.51) * mm});
            skLineSegment(sketch, "E2056", {"start": v(-16.98, -8.51) * mm, "end": v(-17.02, -8.53) * mm});
            skLineSegment(sketch, "E2057", {"start": v(-17.02, -8.53) * mm, "end": v(-17.05, -8.54) * mm});
            skLineSegment(sketch, "E2058", {"start": v(-17.05, -8.54) * mm, "end": v(-17.09, -8.55) * mm});
            skLineSegment(sketch, "E2059", {"start": v(-17.09, -8.55) * mm, "end": v(-17.12, -8.56) * mm});
            skLineSegment(sketch, "E2060", {"start": v(-17.12, -8.56) * mm, "end": v(-17.15, -8.57) * mm});
            skLineSegment(sketch, "E2061", {"start": v(-17.15, -8.57) * mm, "end": v(-17.18, -8.58) * mm});
            skLineSegment(sketch, "E2062", {"start": v(-17.18, -8.58) * mm, "end": v(-17.2, -8.59) * mm});
            skLineSegment(sketch, "E2063", {"start": v(-17.2, -8.59) * mm, "end": v(-17.23, -8.6) * mm});
            skLineSegment(sketch, "E2064", {"start": v(-17.23, -8.6) * mm, "end": v(-17.25, -8.6) * mm});
            skLineSegment(sketch, "E2065", {"start": v(-17.25, -8.6) * mm, "end": v(-17.28, -8.6) * mm});
            skLineSegment(sketch, "E2066", {"start": v(-17.28, -8.6) * mm, "end": v(-17.3, -8.6) * mm});
            skLineSegment(sketch, "E2067", {"start": v(-17.3, -8.6) * mm, "end": v(-17.32, -8.6) * mm});
            skLineSegment(sketch, "E2068", {"start": v(-17.32, -8.6) * mm, "end": v(-17.34, -8.61) * mm});
            skLineSegment(sketch, "E2069", {"start": v(-17.34, -8.61) * mm, "end": v(-17.35, -8.61) * mm});
            skLineSegment(sketch, "E2070", {"start": v(-17.35, -8.61) * mm, "end": v(-17.37, -8.61) * mm});
            skLineSegment(sketch, "E2071", {"start": v(-37.78, -2.6) * mm, "end": v(-37.26, -2.57) * mm});
            skLineSegment(sketch, "E2072", {"start": v(-37.26, -2.57) * mm, "end": v(-36.5, -2.52) * mm});
            skLineSegment(sketch, "E2073", {"start": v(-36.5, -2.52) * mm, "end": v(-35.77, -2.47) * mm});
            skLineSegment(sketch, "E2074", {"start": v(-35.77, -2.47) * mm, "end": v(-35.05, -2.42) * mm});
            skLineSegment(sketch, "E2075", {"start": v(-35.05, -2.42) * mm, "end": v(-34.34, -2.36) * mm});
            skLineSegment(sketch, "E2076", {"start": v(-34.34, -2.36) * mm, "end": v(-33.65, -2.3) * mm});
            skLineSegment(sketch, "E2077", {"start": v(-33.65, -2.3) * mm, "end": v(-32.96, -2.22) * mm});
            skLineSegment(sketch, "E2078", {"start": v(-32.96, -2.22) * mm, "end": v(-32.3, -2.15) * mm});
            skLineSegment(sketch, "E2079", {"start": v(-32.3, -2.15) * mm, "end": v(-31.64, -2.07) * mm});
            skLineSegment(sketch, "E2080", {"start": v(-31.64, -2.07) * mm, "end": v(-31, -1.99) * mm});
            skLineSegment(sketch, "E2081", {"start": v(-31, -1.99) * mm, "end": v(-30.37, -1.9) * mm});
            skLineSegment(sketch, "E2082", {"start": v(-37.12, 5.58) * mm, "end": v(-37.16, 5.59) * mm});
            skLineSegment(sketch, "E2083", {"start": v(-37.16, 5.59) * mm, "end": v(-37.21, 5.6) * mm});
            skLineSegment(sketch, "E2084", {"start": v(-37.21, 5.6) * mm, "end": v(-37.26, 5.6) * mm});
            skLineSegment(sketch, "E2085", {"start": v(-37.26, 5.6) * mm, "end": v(-37.32, 5.6) * mm});
            skLineSegment(sketch, "E2086", {"start": v(-37.32, 5.6) * mm, "end": v(-37.38, 5.61) * mm});
            skLineSegment(sketch, "E2087", {"start": v(-37.38, 5.61) * mm, "end": v(-37.45, 5.62) * mm});
            skLineSegment(sketch, "E2088", {"start": v(-37.45, 5.62) * mm, "end": v(-37.52, 5.62) * mm});
            skLineSegment(sketch, "E2089", {"start": v(-37.52, 5.62) * mm, "end": v(-37.6, 5.63) * mm});
            skLineSegment(sketch, "E2090", {"start": v(-37.6, 5.63) * mm, "end": v(-37.67, 5.63) * mm});
            skLineSegment(sketch, "E2091", {"start": v(-37.67, 5.63) * mm, "end": v(-37.76, 5.63) * mm});
            skLineSegment(sketch, "E2092", {"start": v(-37.76, 5.63) * mm, "end": v(-37.85, 5.64) * mm});
            skLineSegment(sketch, "E2093", {"start": v(-37.85, 5.64) * mm, "end": v(-37.94, 5.64) * mm});
            skLineSegment(sketch, "E2094", {"start": v(-37.94, 5.64) * mm, "end": v(-38.04, 5.64) * mm});
            skLineSegment(sketch, "E2095", {"start": v(-38.04, 5.64) * mm, "end": v(-38.25, 5.64) * mm});
            skLineSegment(sketch, "E2096", {"start": v(2.98, -2.76) * mm, "end": v(2.96, -3.05) * mm});
            skLineSegment(sketch, "E2097", {"start": v(-1.46, -5.46) * mm, "end": v(-1.47, -5.46) * mm});
            skLineSegment(sketch, "E2098", {"start": v(-1.47, -5.46) * mm, "end": v(-1.5, -5.5) * mm});
            skLineSegment(sketch, "E2099", {"start": v(-1.5, -5.5) * mm, "end": v(-1.53, -5.55) * mm});
            skLineSegment(sketch, "E2100", {"start": v(-1.53, -5.55) * mm, "end": v(-1.56, -5.6) * mm});
            skLineSegment(sketch, "E2101", {"start": v(-1.56, -5.6) * mm, "end": v(-1.58, -5.64) * mm});
            skLineSegment(sketch, "E2102", {"start": v(-1.58, -5.64) * mm, "end": v(-1.6, -5.68) * mm});
            skLineSegment(sketch, "E2103", {"start": v(-1.6, -5.68) * mm, "end": v(-1.63, -5.73) * mm});
            skLineSegment(sketch, "E2104", {"start": v(-1.63, -5.73) * mm, "end": v(-1.66, -5.77) * mm});
            skLineSegment(sketch, "E2105", {"start": v(-1.66, -5.77) * mm, "end": v(-1.68, -5.81) * mm});
            skLineSegment(sketch, "E2106", {"start": v(-1.68, -5.81) * mm, "end": v(-1.7, -5.86) * mm});
            skLineSegment(sketch, "E2107", {"start": v(-1.7, -5.86) * mm, "end": v(-1.72, -5.9) * mm});
            skLineSegment(sketch, "E2108", {"start": v(-1.72, -5.9) * mm, "end": v(-1.74, -5.94) * mm});
            skLineSegment(sketch, "E2109", {"start": v(-1.74, -5.94) * mm, "end": v(-1.75, -5.98) * mm});
            skLineSegment(sketch, "E2110", {"start": v(-1.75, -5.98) * mm, "end": v(-1.77, -6.03) * mm});
            skLineSegment(sketch, "E2111", {"start": v(-1.77, -6.03) * mm, "end": v(-1.79, -6.07) * mm});
            skLineSegment(sketch, "E2112", {"start": v(-1.79, -6.07) * mm, "end": v(-1.8, -6.11) * mm});
            skLineSegment(sketch, "E2113", {"start": v(-1.8, -6.11) * mm, "end": v(-1.81, -6.15) * mm});
            skLineSegment(sketch, "E2114", {"start": v(-1.81, -6.15) * mm, "end": v(-1.82, -6.2) * mm});
            skLineSegment(sketch, "E2115", {"start": v(-1.82, -6.2) * mm, "end": v(-1.83, -6.24) * mm});
            skLineSegment(sketch, "E2116", {"start": v(-1.83, -6.24) * mm, "end": v(-1.84, -6.28) * mm});
            skLineSegment(sketch, "E2117", {"start": v(-1.84, -6.28) * mm, "end": v(-1.85, -6.32) * mm});
            skLineSegment(sketch, "E2118", {"start": v(-1.85, -6.32) * mm, "end": v(-1.86, -6.36) * mm});
            skLineSegment(sketch, "E2119", {"start": v(-1.86, -6.36) * mm, "end": v(-1.87, -6.4) * mm});
            skLineSegment(sketch, "E2120", {"start": v(-1.87, -6.4) * mm, "end": v(-1.87, -6.45) * mm});
            skLineSegment(sketch, "E2121", {"start": v(-1.87, -6.45) * mm, "end": v(-1.88, -6.5) * mm});
            skLineSegment(sketch, "E2122", {"start": v(-1.88, -6.5) * mm, "end": v(-1.88, -6.54) * mm});
            skLineSegment(sketch, "E2123", {"start": v(-1.88, -6.54) * mm, "end": v(-1.88, -6.58) * mm});
            skLineSegment(sketch, "E2124", {"start": v(-1.88, -6.58) * mm, "end": v(-1.89, -6.62) * mm});
            skLineSegment(sketch, "E2125", {"start": v(-1.89, -6.62) * mm, "end": v(-1.89, -6.67) * mm});
            skLineSegment(sketch, "E2126", {"start": v(-3.8, -5.54) * mm, "end": v(-3.93, -5.66) * mm});
            skLineSegment(sketch, "E2127", {"start": v(-3.93, -5.66) * mm, "end": v(-4.2, -5.88) * mm});
            skLineSegment(sketch, "E2128", {"start": v(-4.2, -5.88) * mm, "end": v(-4.45, -6.1) * mm});
            skLineSegment(sketch, "E2129", {"start": v(-4.45, -6.1) * mm, "end": v(-4.69, -6.3) * mm});
            skLineSegment(sketch, "E2130", {"start": v(-4.69, -6.3) * mm, "end": v(-4.92, -6.48) * mm});
            skLineSegment(sketch, "E2131", {"start": v(-4.92, -6.48) * mm, "end": v(-5.14, -6.65) * mm});
            skLineSegment(sketch, "E2132", {"start": v(-5.14, -6.65) * mm, "end": v(-5.35, -6.8) * mm});
            skLineSegment(sketch, "E2133", {"start": v(-5.35, -6.8) * mm, "end": v(-5.56, -6.96) * mm});
            skLineSegment(sketch, "E2134", {"start": v(-5.56, -6.96) * mm, "end": v(-5.75, -7.1) * mm});
            skLineSegment(sketch, "E2135", {"start": v(-5.75, -7.1) * mm, "end": v(-5.94, -7.22) * mm});
            skLineSegment(sketch, "E2136", {"start": v(-5.94, -7.22) * mm, "end": v(-6.11, -7.33) * mm});
            skLineSegment(sketch, "E2137", {"start": v(-6.11, -7.33) * mm, "end": v(-6.28, -7.44) * mm});
            skLineSegment(sketch, "E2138", {"start": v(-6.28, -7.44) * mm, "end": v(-6.45, -7.54) * mm});
            skLineSegment(sketch, "E2139", {"start": v(-6.45, -7.54) * mm, "end": v(-6.6, -7.63) * mm});
            skLineSegment(sketch, "E2140", {"start": v(-6.6, -7.63) * mm, "end": v(-6.75, -7.7) * mm});
            skLineSegment(sketch, "E2141", {"start": v(-6.75, -7.7) * mm, "end": v(-6.89, -7.78) * mm});
            skLineSegment(sketch, "E2142", {"start": v(-6.89, -7.78) * mm, "end": v(-7.02, -7.84) * mm});
            skLineSegment(sketch, "E2143", {"start": v(-7.02, -7.84) * mm, "end": v(-7.15, -7.9) * mm});
            skLineSegment(sketch, "E2144", {"start": v(-7.15, -7.9) * mm, "end": v(-7.27, -7.95) * mm});
            skLineSegment(sketch, "E2145", {"start": v(-7.27, -7.95) * mm, "end": v(-7.4, -7.99) * mm});
            skLineSegment(sketch, "E2146", {"start": v(-7.4, -7.99) * mm, "end": v(-7.5, -8.02) * mm});
            skLineSegment(sketch, "E2147", {"start": v(-7.5, -8.02) * mm, "end": v(-7.6, -8.06) * mm});
            skLineSegment(sketch, "E2148", {"start": v(-7.6, -8.06) * mm, "end": v(-7.7, -8.08) * mm});
            skLineSegment(sketch, "E2149", {"start": v(-7.7, -8.08) * mm, "end": v(-7.8, -8.1) * mm});
            skLineSegment(sketch, "E2150", {"start": v(-7.8, -8.1) * mm, "end": v(-7.9, -8.12) * mm});
            skLineSegment(sketch, "E2151", {"start": v(-7.9, -8.12) * mm, "end": v(-7.98, -8.13) * mm});
            skLineSegment(sketch, "E2152", {"start": v(-7.98, -8.13) * mm, "end": v(-8.06, -8.13) * mm});
            skLineSegment(sketch, "E2153", {"start": v(-8.06, -8.13) * mm, "end": v(-8.14, -8.14) * mm});
            skLineSegment(sketch, "E2154", {"start": v(-0.3, -4.32) * mm, "end": v(-0.38, -4.38) * mm});
            skLineSegment(sketch, "E2155", {"start": v(-0.38, -4.38) * mm, "end": v(-0.47, -4.45) * mm});
            skLineSegment(sketch, "E2156", {"start": v(-0.47, -4.45) * mm, "end": v(-0.55, -4.52) * mm});
            skLineSegment(sketch, "E2157", {"start": v(-0.55, -4.52) * mm, "end": v(-0.63, -4.59) * mm});
            skLineSegment(sketch, "E2158", {"start": v(-0.63, -4.59) * mm, "end": v(-0.7, -4.65) * mm});
            skLineSegment(sketch, "E2159", {"start": v(-0.7, -4.65) * mm, "end": v(-0.78, -4.72) * mm});
            skLineSegment(sketch, "E2160", {"start": v(-0.78, -4.72) * mm, "end": v(-0.85, -4.78) * mm});
            skLineSegment(sketch, "E2161", {"start": v(-0.85, -4.78) * mm, "end": v(-0.91, -4.84) * mm});
            skLineSegment(sketch, "E2162", {"start": v(-0.91, -4.84) * mm, "end": v(-0.98, -4.9) * mm});
            skLineSegment(sketch, "E2163", {"start": v(-0.98, -4.9) * mm, "end": v(-1.04, -4.96) * mm});
            skLineSegment(sketch, "E2164", {"start": v(-1.04, -4.96) * mm, "end": v(-1.1, -5.02) * mm});
            skLineSegment(sketch, "E2165", {"start": v(-1.1, -5.02) * mm, "end": v(-1.15, -5.08) * mm});
            skLineSegment(sketch, "E2166", {"start": v(-1.15, -5.08) * mm, "end": v(-1.2, -5.13) * mm});
            skLineSegment(sketch, "E2167", {"start": v(-1.2, -5.13) * mm, "end": v(-1.25, -5.19) * mm});
            skLineSegment(sketch, "E2168", {"start": v(-1.25, -5.19) * mm, "end": v(-1.3, -5.25) * mm});
            skLineSegment(sketch, "E2169", {"start": v(-1.3, -5.25) * mm, "end": v(-1.34, -5.3) * mm});
            skLineSegment(sketch, "E2170", {"start": v(-1.34, -5.3) * mm, "end": v(-1.39, -5.35) * mm});
            skLineSegment(sketch, "E2171", {"start": v(-1.39, -5.35) * mm, "end": v(-1.43, -5.4) * mm});
            skLineSegment(sketch, "E2172", {"start": v(-1.43, -5.4) * mm, "end": v(-1.46, -5.46) * mm});
            skLineSegment(sketch, "E2173", {"start": v(0.48, -3.74) * mm, "end": v(0.25, -3.9) * mm});
            skLineSegment(sketch, "E2174", {"start": v(0.25, -3.9) * mm, "end": v(0.04, -4.06) * mm});
            skLineSegment(sketch, "E2175", {"start": v(0.04, -4.06) * mm, "end": v(-0.14, -4.2) * mm});
            skLineSegment(sketch, "E2176", {"start": v(-0.14, -4.2) * mm, "end": v(-0.3, -4.32) * mm});
            skLineSegment(sketch, "E2177", {"start": v(1.03, -3.34) * mm, "end": v(0.48, -3.74) * mm});
            skLineSegment(sketch, "E2178", {"start": v(1.67, -2.89) * mm, "end": v(1.03, -3.34) * mm});
            skLineSegment(sketch, "E2179", {"start": v(2.42, -2.36) * mm, "end": v(1.67, -2.89) * mm});
            skLineSegment(sketch, "E2180", {"start": v(2.42, -2.36) * mm, "end": v(2.82, -2.22) * mm});
            skLineSegment(sketch, "E2181", {"start": v(-30.37, -1.9) * mm, "end": v(-29.85, -1.83) * mm});
            skLineSegment(sketch, "E2182", {"start": v(-29.85, -1.83) * mm, "end": v(-29.27, -1.74) * mm});
            skLineSegment(sketch, "E2183", {"start": v(-29.27, -1.74) * mm, "end": v(-28.71, -1.65) * mm});
            skLineSegment(sketch, "E2184", {"start": v(-28.71, -1.65) * mm, "end": v(-28.18, -1.56) * mm});
            skLineSegment(sketch, "E2185", {"start": v(-28.18, -1.56) * mm, "end": v(-27.68, -1.46) * mm});
            skLineSegment(sketch, "E2186", {"start": v(-27.68, -1.46) * mm, "end": v(-27.2, -1.37) * mm});
            skLineSegment(sketch, "E2187", {"start": v(-27.2, -1.37) * mm, "end": v(-26.73, -1.28) * mm});
            skLineSegment(sketch, "E2188", {"start": v(-26.73, -1.28) * mm, "end": v(-26.29, -1.19) * mm});
            skLineSegment(sketch, "E2189", {"start": v(-26.29, -1.19) * mm, "end": v(-25.87, -1.1) * mm});
            skLineSegment(sketch, "E2190", {"start": v(-25.87, -1.1) * mm, "end": v(-25.46, -1) * mm});
            skLineSegment(sketch, "E2191", {"start": v(-25.46, -1) * mm, "end": v(-25.08, -0.91) * mm});
            skLineSegment(sketch, "E2192", {"start": v(-25.08, -0.91) * mm, "end": v(-24.71, -0.82) * mm});
            skLineSegment(sketch, "E2193", {"start": v(20.23, 1.6) * mm, "end": v(20.19, 1.6) * mm});
            skLineSegment(sketch, "E2194", {"start": v(20.19, 1.6) * mm, "end": v(20.15, 1.59) * mm});
            skLineSegment(sketch, "E2195", {"start": v(20.15, 1.59) * mm, "end": v(20.1, 1.58) * mm});
            skLineSegment(sketch, "E2196", {"start": v(20.1, 1.58) * mm, "end": v(20.06, 1.58) * mm});
            skLineSegment(sketch, "E2197", {"start": v(20.06, 1.58) * mm, "end": v(20.01, 1.57) * mm});
            skLineSegment(sketch, "E2198", {"start": v(20.01, 1.57) * mm, "end": v(19.96, 1.56) * mm});
            skLineSegment(sketch, "E2199", {"start": v(19.96, 1.56) * mm, "end": v(19.9, 1.54) * mm});
            skLineSegment(sketch, "E2200", {"start": v(19.9, 1.54) * mm, "end": v(19.85, 1.53) * mm});
            skLineSegment(sketch, "E2201", {"start": v(19.85, 1.53) * mm, "end": v(19.8, 1.5) * mm});
            skLineSegment(sketch, "E2202", {"start": v(19.8, 1.5) * mm, "end": v(19.74, 1.49) * mm});
            skLineSegment(sketch, "E2203", {"start": v(19.74, 1.49) * mm, "end": v(19.67, 1.46) * mm});
            skLineSegment(sketch, "E2204", {"start": v(19.67, 1.46) * mm, "end": v(19.6, 1.44) * mm});
            skLineSegment(sketch, "E2205", {"start": v(19.6, 1.44) * mm, "end": v(19.53, 1.4) * mm});
            skLineSegment(sketch, "E2206", {"start": v(19.53, 1.4) * mm, "end": v(19.46, 1.37) * mm});
            skLineSegment(sketch, "E2207", {"start": v(19.46, 1.37) * mm, "end": v(19.38, 1.33) * mm});
            skLineSegment(sketch, "E2208", {"start": v(19.38, 1.33) * mm, "end": v(19.3, 1.29) * mm});
            skLineSegment(sketch, "E2209", {"start": v(19.3, 1.29) * mm, "end": v(19.21, 1.24) * mm});
            skLineSegment(sketch, "E2210", {"start": v(19.21, 1.24) * mm, "end": v(19.12, 1.2) * mm});
            skLineSegment(sketch, "E2211", {"start": v(19.12, 1.2) * mm, "end": v(19.02, 1.14) * mm});
            skLineSegment(sketch, "E2212", {"start": v(19.02, 1.14) * mm, "end": v(18.92, 1.07) * mm});
            skLineSegment(sketch, "E2213", {"start": v(18.92, 1.07) * mm, "end": v(18.81, 1) * mm});
            skLineSegment(sketch, "E2214", {"start": v(18.81, 1) * mm, "end": v(18.7, 0.94) * mm});
            skLineSegment(sketch, "E2215", {"start": v(18.7, 0.94) * mm, "end": v(18.58, 0.86) * mm});
            skLineSegment(sketch, "E2216", {"start": v(18.58, 0.86) * mm, "end": v(18.45, 0.77) * mm});
            skLineSegment(sketch, "E2217", {"start": v(18.45, 0.77) * mm, "end": v(18.32, 0.68) * mm});
            skLineSegment(sketch, "E2218", {"start": v(18.32, 0.68) * mm, "end": v(18.24, 0.62) * mm});
            skLineSegment(sketch, "E2219", {"start": v(-7.9, 3.46) * mm, "end": v(-8.02, 3.46) * mm});
            skLineSegment(sketch, "E2220", {"start": v(-8.02, 3.46) * mm, "end": v(-8.14, 3.45) * mm});
            skLineSegment(sketch, "E2221", {"start": v(-8.14, 3.45) * mm, "end": v(-8.26, 3.44) * mm});
            skLineSegment(sketch, "E2222", {"start": v(-8.26, 3.44) * mm, "end": v(-8.4, 3.43) * mm});
            skLineSegment(sketch, "E2223", {"start": v(-8.4, 3.43) * mm, "end": v(-8.53, 3.4) * mm});
            skLineSegment(sketch, "E2224", {"start": v(-8.53, 3.4) * mm, "end": v(-8.68, 3.39) * mm});
            skLineSegment(sketch, "E2225", {"start": v(-8.68, 3.39) * mm, "end": v(-8.83, 3.36) * mm});
            skLineSegment(sketch, "E2226", {"start": v(-8.83, 3.36) * mm, "end": v(-9, 3.33) * mm});
            skLineSegment(sketch, "E2227", {"start": v(-9, 3.33) * mm, "end": v(-9.16, 3.29) * mm});
            skLineSegment(sketch, "E2228", {"start": v(-9.16, 3.29) * mm, "end": v(-9.33, 3.24) * mm});
            skLineSegment(sketch, "E2229", {"start": v(-9.33, 3.24) * mm, "end": v(-9.51, 3.2) * mm});
            skLineSegment(sketch, "E2230", {"start": v(-9.51, 3.2) * mm, "end": v(-9.7, 3.14) * mm});
            skLineSegment(sketch, "E2231", {"start": v(-9.7, 3.14) * mm, "end": v(-9.9, 3.08) * mm});
            skLineSegment(sketch, "E2232", {"start": v(-9.9, 3.08) * mm, "end": v(-10.11, 3.01) * mm});
            skLineSegment(sketch, "E2233", {"start": v(-10.11, 3.01) * mm, "end": v(-10.33, 2.94) * mm});
            skLineSegment(sketch, "E2234", {"start": v(-10.33, 2.94) * mm, "end": v(-10.56, 2.85) * mm});
            skLineSegment(sketch, "E2235", {"start": v(-10.56, 2.85) * mm, "end": v(-10.8, 2.76) * mm});
            skLineSegment(sketch, "E2236", {"start": v(-10.8, 2.76) * mm, "end": v(-11.04, 2.67) * mm});
            skLineSegment(sketch, "E2237", {"start": v(-11.04, 2.67) * mm, "end": v(-11.3, 2.56) * mm});
            skLineSegment(sketch, "E2238", {"start": v(-11.3, 2.56) * mm, "end": v(-11.57, 2.44) * mm});
            skLineSegment(sketch, "E2239", {"start": v(-11.57, 2.44) * mm, "end": v(-11.85, 2.32) * mm});
            skLineSegment(sketch, "E2240", {"start": v(-11.85, 2.32) * mm, "end": v(-12.14, 2.19) * mm});
            skLineSegment(sketch, "E2241", {"start": v(-12.14, 2.19) * mm, "end": v(-12.29, 2.12) * mm});
            skLineSegment(sketch, "E2242", {"start": v(32.4, 2.8) * mm, "end": v(32.3, 2.8) * mm});
            skLineSegment(sketch, "E2243", {"start": v(32.3, 2.8) * mm, "end": v(32.2, 2.8) * mm});
            skLineSegment(sketch, "E2244", {"start": v(32.2, 2.8) * mm, "end": v(32.1, 2.8) * mm});
            skLineSegment(sketch, "E2245", {"start": v(32.1, 2.8) * mm, "end": v(32, 2.78) * mm});
            skLineSegment(sketch, "E2246", {"start": v(32, 2.78) * mm, "end": v(31.9, 2.77) * mm});
            skLineSegment(sketch, "E2247", {"start": v(31.9, 2.77) * mm, "end": v(31.79, 2.76) * mm});
            skLineSegment(sketch, "E2248", {"start": v(31.79, 2.76) * mm, "end": v(31.68, 2.75) * mm});
            skLineSegment(sketch, "E2249", {"start": v(31.68, 2.75) * mm, "end": v(31.57, 2.73) * mm});
            skLineSegment(sketch, "E2250", {"start": v(31.57, 2.73) * mm, "end": v(31.46, 2.7) * mm});
            skLineSegment(sketch, "E2251", {"start": v(31.46, 2.7) * mm, "end": v(31.35, 2.69) * mm});
            skLineSegment(sketch, "E2252", {"start": v(31.35, 2.69) * mm, "end": v(31.24, 2.66) * mm});
            skLineSegment(sketch, "E2253", {"start": v(31.24, 2.66) * mm, "end": v(31.12, 2.63) * mm});
            skLineSegment(sketch, "E2254", {"start": v(31.12, 2.63) * mm, "end": v(31, 2.6) * mm});
            skLineSegment(sketch, "E2255", {"start": v(31, 2.6) * mm, "end": v(30.89, 2.57) * mm});
            skLineSegment(sketch, "E2256", {"start": v(30.89, 2.57) * mm, "end": v(30.76, 2.53) * mm});
            skLineSegment(sketch, "E2257", {"start": v(30.76, 2.53) * mm, "end": v(30.64, 2.5) * mm});
            skLineSegment(sketch, "E2258", {"start": v(30.64, 2.5) * mm, "end": v(30.51, 2.45) * mm});
            skLineSegment(sketch, "E2259", {"start": v(30.51, 2.45) * mm, "end": v(30.38, 2.4) * mm});
            skLineSegment(sketch, "E2260", {"start": v(30.38, 2.4) * mm, "end": v(30.25, 2.36) * mm});
            skLineSegment(sketch, "E2261", {"start": v(30.25, 2.36) * mm, "end": v(30.12, 2.3) * mm});
            skLineSegment(sketch, "E2262", {"start": v(30.12, 2.3) * mm, "end": v(29.98, 2.25) * mm});
            skLineSegment(sketch, "E2263", {"start": v(29.98, 2.25) * mm, "end": v(29.84, 2.2) * mm});
            skLineSegment(sketch, "E2264", {"start": v(29.84, 2.2) * mm, "end": v(29.74, 2.15) * mm});
            skLineSegment(sketch, "E2265", {"start": v(5.18, 2.84) * mm, "end": v(5.23, 2.84) * mm});
            skLineSegment(sketch, "E2266", {"start": v(5.23, 2.84) * mm, "end": v(5.27, 2.84) * mm});
            skLineSegment(sketch, "E2267", {"start": v(5.27, 2.84) * mm, "end": v(5.31, 2.84) * mm});
            skLineSegment(sketch, "E2268", {"start": v(5.31, 2.84) * mm, "end": v(5.35, 2.83) * mm});
            skLineSegment(sketch, "E2269", {"start": v(5.35, 2.83) * mm, "end": v(5.4, 2.83) * mm});
            skLineSegment(sketch, "E2270", {"start": v(5.4, 2.83) * mm, "end": v(5.44, 2.82) * mm});
            skLineSegment(sketch, "E2271", {"start": v(5.44, 2.82) * mm, "end": v(5.48, 2.82) * mm});
            skLineSegment(sketch, "E2272", {"start": v(5.48, 2.82) * mm, "end": v(5.52, 2.8) * mm});
            skLineSegment(sketch, "E2273", {"start": v(5.52, 2.8) * mm, "end": v(5.56, 2.8) * mm});
            skLineSegment(sketch, "E2274", {"start": v(5.56, 2.8) * mm, "end": v(5.6, 2.8) * mm});
            skLineSegment(sketch, "E2275", {"start": v(5.6, 2.8) * mm, "end": v(5.64, 2.78) * mm});
            skLineSegment(sketch, "E2276", {"start": v(5.64, 2.78) * mm, "end": v(5.68, 2.77) * mm});
            skLineSegment(sketch, "E2277", {"start": v(5.68, 2.77) * mm, "end": v(5.72, 2.76) * mm});
            skLineSegment(sketch, "E2278", {"start": v(5.72, 2.76) * mm, "end": v(5.76, 2.74) * mm});
            skLineSegment(sketch, "E2279", {"start": v(5.76, 2.74) * mm, "end": v(5.8, 2.73) * mm});
            skLineSegment(sketch, "E2280", {"start": v(5.8, 2.73) * mm, "end": v(5.83, 2.71) * mm});
            skLineSegment(sketch, "E2281", {"start": v(5.83, 2.71) * mm, "end": v(5.87, 2.7) * mm});
            skLineSegment(sketch, "E2282", {"start": v(5.87, 2.7) * mm, "end": v(5.9, 2.68) * mm});
            skLineSegment(sketch, "E2283", {"start": v(5.9, 2.68) * mm, "end": v(5.94, 2.66) * mm});
            skLineSegment(sketch, "E2284", {"start": v(5.94, 2.66) * mm, "end": v(5.98, 2.64) * mm});
            skLineSegment(sketch, "E2285", {"start": v(5.98, 2.64) * mm, "end": v(6.01, 2.62) * mm});
            skLineSegment(sketch, "E2286", {"start": v(6.01, 2.62) * mm, "end": v(6.05, 2.6) * mm});
            skLineSegment(sketch, "E2287", {"start": v(6.05, 2.6) * mm, "end": v(6.08, 2.58) * mm});
            skLineSegment(sketch, "E2288", {"start": v(6.08, 2.58) * mm, "end": v(6.12, 2.56) * mm});
            skLineSegment(sketch, "E2289", {"start": v(6.12, 2.56) * mm, "end": v(6.15, 2.53) * mm});
            skLineSegment(sketch, "E2290", {"start": v(6.15, 2.53) * mm, "end": v(6.19, 2.5) * mm});
            skLineSegment(sketch, "E2291", {"start": v(6.19, 2.5) * mm, "end": v(6.22, 2.48) * mm});
            skLineSegment(sketch, "E2292", {"start": v(6.22, 2.48) * mm, "end": v(6.26, 2.45) * mm});
            skLineSegment(sketch, "E2293", {"start": v(6.26, 2.45) * mm, "end": v(6.29, 2.42) * mm});
            skLineSegment(sketch, "E2294", {"start": v(6.29, 2.42) * mm, "end": v(6.32, 2.4) * mm});
            skLineSegment(sketch, "E2295", {"start": v(6.32, 2.4) * mm, "end": v(6.36, 2.36) * mm});
            skLineSegment(sketch, "E2296", {"start": v(6.36, 2.36) * mm, "end": v(6.38, 2.34) * mm});
            skLineSegment(sketch, "E2297", {"start": v(31.24, 0.62) * mm, "end": v(31.26, 0.62) * mm});
            skLineSegment(sketch, "E2298", {"start": v(31.26, 0.62) * mm, "end": v(31.28, 0.62) * mm});
            skLineSegment(sketch, "E2299", {"start": v(31.28, 0.62) * mm, "end": v(31.3, 0.62) * mm});
            skLineSegment(sketch, "E2300", {"start": v(31.3, 0.62) * mm, "end": v(31.32, 0.61) * mm});
            skLineSegment(sketch, "E2301", {"start": v(31.32, 0.61) * mm, "end": v(31.33, 0.61) * mm});
            skLineSegment(sketch, "E2302", {"start": v(31.33, 0.61) * mm, "end": v(31.35, 0.61) * mm});
            skLineSegment(sketch, "E2303", {"start": v(31.35, 0.61) * mm, "end": v(31.36, 0.6) * mm});
            skLineSegment(sketch, "E2304", {"start": v(31.36, 0.6) * mm, "end": v(31.38, 0.6) * mm});
            skLineSegment(sketch, "E2305", {"start": v(31.38, 0.6) * mm, "end": v(31.4, 0.6) * mm});
            skLineSegment(sketch, "E2306", {"start": v(31.4, 0.6) * mm, "end": v(31.4, 0.6) * mm});
            skLineSegment(sketch, "E2307", {"start": v(31.4, 0.6) * mm, "end": v(31.42, 0.6) * mm});
            skLineSegment(sketch, "E2308", {"start": v(31.42, 0.6) * mm, "end": v(31.43, 0.59) * mm});
            skLineSegment(sketch, "E2309", {"start": v(31.43, 0.59) * mm, "end": v(31.44, 0.58) * mm});
            skLineSegment(sketch, "E2310", {"start": v(31.44, 0.58) * mm, "end": v(31.46, 0.58) * mm});
            skLineSegment(sketch, "E2311", {"start": v(31.46, 0.58) * mm, "end": v(31.47, 0.57) * mm});
            skLineSegment(sketch, "E2312", {"start": v(31.47, 0.57) * mm, "end": v(31.48, 0.56) * mm});
            skLineSegment(sketch, "E2313", {"start": v(31.48, 0.56) * mm, "end": v(31.5, 0.56) * mm});
            skLineSegment(sketch, "E2314", {"start": v(31.5, 0.56) * mm, "end": v(31.5, 0.55) * mm});
            skLineSegment(sketch, "E2315", {"start": v(31.5, 0.55) * mm, "end": v(31.51, 0.54) * mm});
            skLineSegment(sketch, "E2316", {"start": v(31.51, 0.54) * mm, "end": v(31.52, 0.54) * mm});
            skLineSegment(sketch, "E2317", {"start": v(31.52, 0.54) * mm, "end": v(31.53, 0.53) * mm});
            skLineSegment(sketch, "E2318", {"start": v(31.53, 0.53) * mm, "end": v(31.54, 0.52) * mm});
            skLineSegment(sketch, "E2319", {"start": v(31.54, 0.52) * mm, "end": v(31.55, 0.51) * mm});
            skLineSegment(sketch, "E2320", {"start": v(31.55, 0.51) * mm, "end": v(31.56, 0.5) * mm});
            skLineSegment(sketch, "E2321", {"start": v(31.56, 0.5) * mm, "end": v(31.57, 0.5) * mm});
            skLineSegment(sketch, "E2322", {"start": v(31.57, 0.5) * mm, "end": v(31.57, 0.48) * mm});
            skLineSegment(sketch, "E2323", {"start": v(31.57, 0.48) * mm, "end": v(31.58, 0.47) * mm});
            skLineSegment(sketch, "E2324", {"start": v(31.58, 0.47) * mm, "end": v(31.59, 0.46) * mm});
            skLineSegment(sketch, "E2325", {"start": v(31.59, 0.46) * mm, "end": v(31.6, 0.45) * mm});
            skLineSegment(sketch, "E2326", {"start": v(31.6, 0.45) * mm, "end": v(31.6, 0.44) * mm});
            skLineSegment(sketch, "E2327", {"start": v(31.6, 0.44) * mm, "end": v(31.6, 0.43) * mm});
            skLineSegment(sketch, "E2328", {"start": v(31.6, 0.43) * mm, "end": v(31.61, 0.41) * mm});
            skLineSegment(sketch, "E2329", {"start": v(31.61, 0.41) * mm, "end": v(31.62, 0.4) * mm});
            skLineSegment(sketch, "E2330", {"start": v(31.62, 0.4) * mm, "end": v(31.63, 0.39) * mm});
            skLineSegment(sketch, "E2331", {"start": v(31.63, 0.39) * mm, "end": v(31.63, 0.37) * mm});
            skLineSegment(sketch, "E2332", {"start": v(31.63, 0.37) * mm, "end": v(31.63, 0.36) * mm});
            skLineSegment(sketch, "E2333", {"start": v(31.63, 0.36) * mm, "end": v(31.64, 0.34) * mm});
            skLineSegment(sketch, "E2334", {"start": v(31.64, 0.34) * mm, "end": v(31.64, 0.33) * mm});
            skLineSegment(sketch, "E2335", {"start": v(31.64, 0.33) * mm, "end": v(31.65, 0.31) * mm});
            skLineSegment(sketch, "E2336", {"start": v(31.65, 0.31) * mm, "end": v(31.65, 0.3) * mm});
            skLineSegment(sketch, "E2337", {"start": v(31.65, 0.3) * mm, "end": v(31.65, 0.28) * mm});
            skLineSegment(sketch, "E2338", {"start": v(31.65, 0.28) * mm, "end": v(31.66, 0.26) * mm});
            skLineSegment(sketch, "E2339", {"start": v(31.66, 0.26) * mm, "end": v(31.66, 0.24) * mm});
            skLineSegment(sketch, "E2340", {"start": v(31.66, 0.24) * mm, "end": v(31.66, 0.22) * mm});
            skLineSegment(sketch, "E2341", {"start": v(31.66, 0.22) * mm, "end": v(31.66, 0.2) * mm});
            skLineSegment(sketch, "E2342", {"start": v(31.66, 0.2) * mm, "end": v(31.66, 0.18) * mm});
            skLineSegment(sketch, "E2343", {"start": v(31.66, 0.18) * mm, "end": v(31.66, 0.16) * mm});
            skLineSegment(sketch, "E2344", {"start": v(-21.34, 7.69) * mm, "end": v(-21.34, 7.68) * mm});
            skLineSegment(sketch, "E2345", {"start": v(-21.34, 7.68) * mm, "end": v(-21.2, 7.65) * mm});
            skLineSegment(sketch, "E2346", {"start": v(-21.2, 7.65) * mm, "end": v(-21.08, 7.6) * mm});
            skLineSegment(sketch, "E2347", {"start": v(-21.08, 7.6) * mm, "end": v(-20.97, 7.57) * mm});
            skLineSegment(sketch, "E2348", {"start": v(-20.97, 7.57) * mm, "end": v(-20.86, 7.53) * mm});
            skLineSegment(sketch, "E2349", {"start": v(-20.86, 7.53) * mm, "end": v(-20.75, 7.5) * mm});
            skLineSegment(sketch, "E2350", {"start": v(-20.75, 7.5) * mm, "end": v(-20.65, 7.46) * mm});
            skLineSegment(sketch, "E2351", {"start": v(-20.65, 7.46) * mm, "end": v(-20.55, 7.42) * mm});
            skLineSegment(sketch, "E2352", {"start": v(-20.55, 7.42) * mm, "end": v(-20.46, 7.38) * mm});
            skLineSegment(sketch, "E2353", {"start": v(-20.46, 7.38) * mm, "end": v(-20.38, 7.34) * mm});
            skLineSegment(sketch, "E2354", {"start": v(-20.38, 7.34) * mm, "end": v(-20.3, 7.3) * mm});
            skLineSegment(sketch, "E2355", {"start": v(-20.3, 7.3) * mm, "end": v(-20.22, 7.26) * mm});
            skLineSegment(sketch, "E2356", {"start": v(-20.22, 7.26) * mm, "end": v(-20.15, 7.22) * mm});
            skLineSegment(sketch, "E2357", {"start": v(-20.15, 7.22) * mm, "end": v(-20.08, 7.19) * mm});
            skLineSegment(sketch, "E2358", {"start": v(-20.08, 7.19) * mm, "end": v(-20.01, 7.15) * mm});
            skLineSegment(sketch, "E2359", {"start": v(-20.01, 7.15) * mm, "end": v(-19.95, 7.1) * mm});
            skLineSegment(sketch, "E2360", {"start": v(-19.95, 7.1) * mm, "end": v(-19.9, 7.07) * mm});
            skLineSegment(sketch, "E2361", {"start": v(-19.9, 7.07) * mm, "end": v(-19.84, 7.03) * mm});
            skLineSegment(sketch, "E2362", {"start": v(-19.84, 7.03) * mm, "end": v(-19.79, 6.99) * mm});
            skLineSegment(sketch, "E2363", {"start": v(-19.79, 6.99) * mm, "end": v(-19.74, 6.95) * mm});
            skLineSegment(sketch, "E2364", {"start": v(-19.74, 6.95) * mm, "end": v(-19.7, 6.91) * mm});
            skLineSegment(sketch, "E2365", {"start": v(-19.7, 6.91) * mm, "end": v(-19.65, 6.87) * mm});
            skLineSegment(sketch, "E2366", {"start": v(-19.65, 6.87) * mm, "end": v(-19.61, 6.83) * mm});
            skLineSegment(sketch, "E2367", {"start": v(-19.61, 6.83) * mm, "end": v(-19.58, 6.8) * mm});
            skLineSegment(sketch, "E2368", {"start": v(-19.58, 6.8) * mm, "end": v(-19.55, 6.75) * mm});
            skLineSegment(sketch, "E2369", {"start": v(-19.55, 6.75) * mm, "end": v(-19.51, 6.71) * mm});
            skLineSegment(sketch, "E2370", {"start": v(-19.51, 6.71) * mm, "end": v(-19.49, 6.67) * mm});
            skLineSegment(sketch, "E2371", {"start": v(-19.49, 6.67) * mm, "end": v(-19.46, 6.63) * mm});
            skLineSegment(sketch, "E2372", {"start": v(-19.46, 6.63) * mm, "end": v(-19.44, 6.6) * mm});
            skLineSegment(sketch, "E2373", {"start": v(-19.44, 6.6) * mm, "end": v(-19.41, 6.55) * mm});
            skLineSegment(sketch, "E2374", {"start": v(-19.41, 6.55) * mm, "end": v(-19.4, 6.51) * mm});
            skLineSegment(sketch, "E2375", {"start": v(-19.4, 6.51) * mm, "end": v(-19.38, 6.47) * mm});
            skLineSegment(sketch, "E2376", {"start": v(-19.38, 6.47) * mm, "end": v(-19.36, 6.43) * mm});
            skLineSegment(sketch, "E2377", {"start": v(-19.36, 6.43) * mm, "end": v(-19.35, 6.4) * mm});
            skLineSegment(sketch, "E2378", {"start": v(-19.35, 6.4) * mm, "end": v(-19.34, 6.35) * mm});
            skLineSegment(sketch, "E2379", {"start": v(-19.34, 6.35) * mm, "end": v(-19.33, 6.33) * mm});
            skLineSegment(sketch, "E2380", {"start": v(-19.33, 6.33) * mm, "end": v(-19.33, 6.3) * mm});
            skLineSegment(sketch, "E2381", {"start": v(-19.33, 6.3) * mm, "end": v(-19.32, 6.27) * mm});
            skLineSegment(sketch, "E2382", {"start": v(-19.32, 6.27) * mm, "end": v(-19.32, 6.22) * mm});
            skLineSegment(sketch, "E2383", {"start": v(-19.32, 6.22) * mm, "end": v(-19.32, 6.18) * mm});
            skLineSegment(sketch, "E2384", {"start": v(-19.32, 6.18) * mm, "end": v(-19.31, 6.14) * mm});
            skLineSegment(sketch, "E2385", {"start": v(2.82, -2.22) * mm, "end": v(2.98, -2.76) * mm});
            skLineSegment(sketch, "E2386", {"start": v(6.24, -0.71) * mm, "end": v(6.16, -0.85) * mm});
            skLineSegment(sketch, "E2387", {"start": v(6.16, -0.85) * mm, "end": v(6.09, -0.98) * mm});
            skLineSegment(sketch, "E2388", {"start": v(6.09, -0.98) * mm, "end": v(6, -1.1) * mm});
            skLineSegment(sketch, "E2389", {"start": v(6, -1.1) * mm, "end": v(5.93, -1.23) * mm});
            skLineSegment(sketch, "E2390", {"start": v(5.93, -1.23) * mm, "end": v(5.85, -1.36) * mm});
            skLineSegment(sketch, "E2391", {"start": v(5.85, -1.36) * mm, "end": v(5.77, -1.48) * mm});
            skLineSegment(sketch, "E2392", {"start": v(5.77, -1.48) * mm, "end": v(5.69, -1.6) * mm});
            skLineSegment(sketch, "E2393", {"start": v(5.69, -1.6) * mm, "end": v(5.6, -1.72) * mm});
            skLineSegment(sketch, "E2394", {"start": v(5.6, -1.72) * mm, "end": v(5.52, -1.83) * mm});
            skLineSegment(sketch, "E2395", {"start": v(5.52, -1.83) * mm, "end": v(5.44, -1.94) * mm});
            skLineSegment(sketch, "E2396", {"start": v(5.44, -1.94) * mm, "end": v(5.36, -2.06) * mm});
            skLineSegment(sketch, "E2397", {"start": v(5.36, -2.06) * mm, "end": v(5.27, -2.16) * mm});
            skLineSegment(sketch, "E2398", {"start": v(5.27, -2.16) * mm, "end": v(5.18, -2.27) * mm});
            skLineSegment(sketch, "E2399", {"start": v(5.18, -2.27) * mm, "end": v(5.1, -2.38) * mm});
            skLineSegment(sketch, "E2400", {"start": v(5.1, -2.38) * mm, "end": v(5, -2.48) * mm});
            skLineSegment(sketch, "E2401", {"start": v(5, -2.48) * mm, "end": v(4.92, -2.58) * mm});
            skLineSegment(sketch, "E2402", {"start": v(4.92, -2.58) * mm, "end": v(4.82, -2.68) * mm});
            skLineSegment(sketch, "E2403", {"start": v(4.82, -2.68) * mm, "end": v(4.76, -2.75) * mm});
            skLineSegment(sketch, "E2404", {"start": v(20.02, 12.85) * mm, "end": v(19.78, 12.6) * mm});
            skLineSegment(sketch, "E2405", {"start": v(19.78, 12.6) * mm, "end": v(19.52, 12.31) * mm});
            skLineSegment(sketch, "E2406", {"start": v(19.52, 12.31) * mm, "end": v(19.25, 12) * mm});
            skLineSegment(sketch, "E2407", {"start": v(19.25, 12) * mm, "end": v(18.96, 11.67) * mm});
            skLineSegment(sketch, "E2408", {"start": v(18.96, 11.67) * mm, "end": v(18.65, 11.31) * mm});
            skLineSegment(sketch, "E2409", {"start": v(18.65, 11.31) * mm, "end": v(18.33, 10.92) * mm});
            skLineSegment(sketch, "E2410", {"start": v(18.33, 10.92) * mm, "end": v(17.98, 10.5) * mm});
            skLineSegment(sketch, "E2411", {"start": v(17.98, 10.5) * mm, "end": v(17.62, 10.05) * mm});
            skLineSegment(sketch, "E2412", {"start": v(17.62, 10.05) * mm, "end": v(17.24, 9.57) * mm});
            skLineSegment(sketch, "E2413", {"start": v(17.24, 9.57) * mm, "end": v(16.83, 9.05) * mm});
            skLineSegment(sketch, "E2414", {"start": v(16.83, 9.05) * mm, "end": v(16.4, 8.5) * mm});
            skLineSegment(sketch, "E2415", {"start": v(16.4, 8.5) * mm, "end": v(15.96, 7.9) * mm});
            skLineSegment(sketch, "E2416", {"start": v(15.96, 7.9) * mm, "end": v(15.42, 7.16) * mm});
            skLineSegment(sketch, "E2417", {"start": v(4.76, -2.75) * mm, "end": v(4.7, -2.81) * mm});
            skLineSegment(sketch, "E2418", {"start": v(4.7, -2.81) * mm, "end": v(4.63, -2.88) * mm});
            skLineSegment(sketch, "E2419", {"start": v(4.63, -2.88) * mm, "end": v(4.57, -2.94) * mm});
            skLineSegment(sketch, "E2420", {"start": v(4.57, -2.94) * mm, "end": v(4.5, -3) * mm});
            skLineSegment(sketch, "E2421", {"start": v(4.5, -3) * mm, "end": v(4.45, -3.06) * mm});
            skLineSegment(sketch, "E2422", {"start": v(4.45, -3.06) * mm, "end": v(4.4, -3.11) * mm});
            skLineSegment(sketch, "E2423", {"start": v(4.4, -3.11) * mm, "end": v(4.34, -3.16) * mm});
            skLineSegment(sketch, "E2424", {"start": v(4.34, -3.16) * mm, "end": v(4.28, -3.2) * mm});
            skLineSegment(sketch, "E2425", {"start": v(4.28, -3.2) * mm, "end": v(4.23, -3.25) * mm});
            skLineSegment(sketch, "E2426", {"start": v(4.23, -3.25) * mm, "end": v(4.18, -3.29) * mm});
            skLineSegment(sketch, "E2427", {"start": v(4.18, -3.29) * mm, "end": v(4.13, -3.32) * mm});
            skLineSegment(sketch, "E2428", {"start": v(4.13, -3.32) * mm, "end": v(4.09, -3.36) * mm});
            skLineSegment(sketch, "E2429", {"start": v(4.09, -3.36) * mm, "end": v(4.04, -3.39) * mm});
            skLineSegment(sketch, "E2430", {"start": v(4.04, -3.39) * mm, "end": v(4, -3.42) * mm});
            skLineSegment(sketch, "E2431", {"start": v(4, -3.42) * mm, "end": v(3.96, -3.44) * mm});
            skLineSegment(sketch, "E2432", {"start": v(3.96, -3.44) * mm, "end": v(3.92, -3.47) * mm});
            skLineSegment(sketch, "E2433", {"start": v(3.92, -3.47) * mm, "end": v(3.88, -3.49) * mm});
            skLineSegment(sketch, "E2434", {"start": v(3.88, -3.49) * mm, "end": v(3.84, -3.5) * mm});
            skLineSegment(sketch, "E2435", {"start": v(3.84, -3.5) * mm, "end": v(3.8, -3.53) * mm});
            skLineSegment(sketch, "E2436", {"start": v(3.8, -3.53) * mm, "end": v(3.77, -3.54) * mm});
            skLineSegment(sketch, "E2437", {"start": v(3.77, -3.54) * mm, "end": v(3.74, -3.55) * mm});
            skLineSegment(sketch, "E2438", {"start": v(3.74, -3.55) * mm, "end": v(3.7, -3.57) * mm});
            skLineSegment(sketch, "E2439", {"start": v(3.7, -3.57) * mm, "end": v(3.67, -3.58) * mm});
            skLineSegment(sketch, "E2440", {"start": v(3.67, -3.58) * mm, "end": v(3.64, -3.59) * mm});
            skLineSegment(sketch, "E2441", {"start": v(3.64, -3.59) * mm, "end": v(3.61, -3.6) * mm});
            skLineSegment(sketch, "E2442", {"start": v(3.61, -3.6) * mm, "end": v(3.58, -3.6) * mm});
            skLineSegment(sketch, "E2443", {"start": v(3.58, -3.6) * mm, "end": v(3.55, -3.6) * mm});
            skLineSegment(sketch, "E2444", {"start": v(3.55, -3.6) * mm, "end": v(3.53, -3.6) * mm});
            skLineSegment(sketch, "E2445", {"start": v(3.53, -3.6) * mm, "end": v(3.5, -3.6) * mm});
            skLineSegment(sketch, "E2446", {"start": v(3.5, -3.6) * mm, "end": v(3.47, -3.6) * mm});
            skLineSegment(sketch, "E2447", {"start": v(-24.71, -0.82) * mm, "end": v(-24.66, -0.8) * mm});
            skLineSegment(sketch, "E2448", {"start": v(-24.66, -0.8) * mm, "end": v(-24.36, -0.72) * mm});
            skLineSegment(sketch, "E2449", {"start": v(-24.36, -0.72) * mm, "end": v(-24.06, -0.64) * mm});
            skLineSegment(sketch, "E2450", {"start": v(-24.06, -0.64) * mm, "end": v(-23.78, -0.56) * mm});
            skLineSegment(sketch, "E2451", {"start": v(-23.78, -0.56) * mm, "end": v(-23.52, -0.48) * mm});
            skLineSegment(sketch, "E2452", {"start": v(-23.52, -0.48) * mm, "end": v(-23.26, -0.4) * mm});
            skLineSegment(sketch, "E2453", {"start": v(-23.26, -0.4) * mm, "end": v(-23.02, -0.32) * mm});
            skLineSegment(sketch, "E2454", {"start": v(-23.02, -0.32) * mm, "end": v(-22.79, -0.24) * mm});
            skLineSegment(sketch, "E2455", {"start": v(-22.79, -0.24) * mm, "end": v(-22.57, -0.17) * mm});
            skLineSegment(sketch, "E2456", {"start": v(-22.57, -0.17) * mm, "end": v(-22.36, -0.1) * mm});
            skLineSegment(sketch, "E2457", {"start": v(-22.36, -0.1) * mm, "end": v(-22.16, -0.02) * mm});
            skLineSegment(sketch, "E2458", {"start": v(-22.16, -0.02) * mm, "end": v(-21.98, 0.06) * mm});
            skLineSegment(sketch, "E2459", {"start": v(-21.98, 0.06) * mm, "end": v(-21.8, 0.13) * mm});
            skLineSegment(sketch, "E2460", {"start": v(-21.8, 0.13) * mm, "end": v(-21.64, 0.2) * mm});
            skLineSegment(sketch, "E2461", {"start": v(-21.64, 0.2) * mm, "end": v(-21.5, 0.27) * mm});
            skLineSegment(sketch, "E2462", {"start": v(-21.5, 0.27) * mm, "end": v(-21.35, 0.33) * mm});
            skLineSegment(sketch, "E2463", {"start": v(-21.35, 0.33) * mm, "end": v(-21.22, 0.4) * mm});
            skLineSegment(sketch, "E2464", {"start": v(-40.16, -0.91) * mm, "end": v(-40.16, -0.91) * mm});
            skLineSegment(sketch, "E2465", {"start": v(-40.16, -0.91) * mm, "end": v(-40.2, -0.92) * mm});
            skLineSegment(sketch, "E2466", {"start": v(-40.2, -0.92) * mm, "end": v(-40.25, -0.92) * mm});
            skLineSegment(sketch, "E2467", {"start": v(-40.25, -0.92) * mm, "end": v(-40.3, -0.93) * mm});
            skLineSegment(sketch, "E2468", {"start": v(-40.3, -0.93) * mm, "end": v(-40.34, -0.94) * mm});
            skLineSegment(sketch, "E2469", {"start": v(-40.34, -0.94) * mm, "end": v(-40.38, -0.95) * mm});
            skLineSegment(sketch, "E2470", {"start": v(-40.38, -0.95) * mm, "end": v(-40.42, -0.96) * mm});
            skLineSegment(sketch, "E2471", {"start": v(-40.42, -0.96) * mm, "end": v(-40.47, -0.97) * mm});
            skLineSegment(sketch, "E2472", {"start": v(-40.47, -0.97) * mm, "end": v(-40.5, -0.98) * mm});
            skLineSegment(sketch, "E2473", {"start": v(-40.5, -0.98) * mm, "end": v(-40.55, -1) * mm});
            skLineSegment(sketch, "E2474", {"start": v(-40.55, -1) * mm, "end": v(-40.59, -1) * mm});
            skLineSegment(sketch, "E2475", {"start": v(-40.59, -1) * mm, "end": v(-40.63, -1.02) * mm});
            skLineSegment(sketch, "E2476", {"start": v(-40.63, -1.02) * mm, "end": v(-40.67, -1.03) * mm});
            skLineSegment(sketch, "E2477", {"start": v(-40.67, -1.03) * mm, "end": v(-40.7, -1.04) * mm});
            skLineSegment(sketch, "E2478", {"start": v(-40.7, -1.04) * mm, "end": v(-40.74, -1.06) * mm});
            skLineSegment(sketch, "E2479", {"start": v(-40.74, -1.06) * mm, "end": v(-40.78, -1.07) * mm});
            skLineSegment(sketch, "E2480", {"start": v(-40.78, -1.07) * mm, "end": v(-40.81, -1.09) * mm});
            skLineSegment(sketch, "E2481", {"start": v(-40.81, -1.09) * mm, "end": v(-40.85, -1.1) * mm});
            skLineSegment(sketch, "E2482", {"start": v(-40.85, -1.1) * mm, "end": v(-40.88, -1.12) * mm});
            skLineSegment(sketch, "E2483", {"start": v(-40.88, -1.12) * mm, "end": v(-40.92, -1.13) * mm});
            skLineSegment(sketch, "E2484", {"start": v(-40.92, -1.13) * mm, "end": v(-40.95, -1.15) * mm});
            skLineSegment(sketch, "E2485", {"start": v(-40.06, -0.9) * mm, "end": v(-40.16, -0.91) * mm});
            skLineSegment(sketch, "E2486", {"start": v(-39.77, -0.86) * mm, "end": v(-40.06, -0.9) * mm});
            skLineSegment(sketch, "E2487", {"start": v(-38.84, -0.74) * mm, "end": v(-39.77, -0.86) * mm});
            skLineSegment(sketch, "E2488", {"start": v(-37.81, -0.61) * mm, "end": v(-38.84, -0.74) * mm});
            skLineSegment(sketch, "E2489", {"start": v(-39.96, 5) * mm, "end": v(-37.69, 5.1) * mm});
            skLineSegment(sketch, "E2490", {"start": v(-41.93, 4.92) * mm, "end": v(-41.55, 4.94) * mm});
            skLineSegment(sketch, "E2491", {"start": v(-41.55, 4.94) * mm, "end": v(-39.96, 5) * mm});
            skLineSegment(sketch, "E2492", {"start": v(-43.02, 4.89) * mm, "end": v(-42.92, 4.89) * mm});
            skLineSegment(sketch, "E2493", {"start": v(-42.92, 4.89) * mm, "end": v(-42.8, 4.9) * mm});
            skLineSegment(sketch, "E2494", {"start": v(-42.8, 4.9) * mm, "end": v(-42.67, 4.9) * mm});
            skLineSegment(sketch, "E2495", {"start": v(-42.67, 4.9) * mm, "end": v(-42.54, 4.9) * mm});
            skLineSegment(sketch, "E2496", {"start": v(-42.54, 4.9) * mm, "end": v(-42.4, 4.9) * mm});
            skLineSegment(sketch, "E2497", {"start": v(-42.4, 4.9) * mm, "end": v(-42.25, 4.9) * mm});
            skLineSegment(sketch, "E2498", {"start": v(-42.25, 4.9) * mm, "end": v(-41.93, 4.92) * mm});
            skLineSegment(sketch, "E2499", {"start": v(-43.2, 4.89) * mm, "end": v(-43.02, 4.89) * mm});
            skLineSegment(sketch, "E2500", {"start": v(-43.3, 4.89) * mm, "end": v(-43.2, 4.89) * mm});
            skLineSegment(sketch, "E2501", {"start": v(-38.25, 5.64) * mm, "end": v(-38.35, 5.64) * mm});
            skLineSegment(sketch, "E2502", {"start": v(-38.35, 5.64) * mm, "end": v(-38.44, 5.64) * mm});
            skLineSegment(sketch, "E2503", {"start": v(-38.44, 5.64) * mm, "end": v(-38.53, 5.65) * mm});
            skLineSegment(sketch, "E2504", {"start": v(-38.53, 5.65) * mm, "end": v(-38.6, 5.65) * mm});
            skLineSegment(sketch, "E2505", {"start": v(-38.6, 5.65) * mm, "end": v(-38.69, 5.65) * mm});
            skLineSegment(sketch, "E2506", {"start": v(-38.69, 5.65) * mm, "end": v(-38.76, 5.66) * mm});
            skLineSegment(sketch, "E2507", {"start": v(-38.76, 5.66) * mm, "end": v(-38.83, 5.66) * mm});
            skLineSegment(sketch, "E2508", {"start": v(-38.83, 5.66) * mm, "end": v(-38.89, 5.67) * mm});
            skLineSegment(sketch, "E2509", {"start": v(-38.89, 5.67) * mm, "end": v(-38.95, 5.67) * mm});
            skLineSegment(sketch, "E2510", {"start": v(-38.95, 5.67) * mm, "end": v(-39, 5.68) * mm});
            skLineSegment(sketch, "E2511", {"start": v(-39, 5.68) * mm, "end": v(-39.06, 5.69) * mm});
            skLineSegment(sketch, "E2512", {"start": v(-39.06, 5.69) * mm, "end": v(-39.1, 5.7) * mm});
            skLineSegment(sketch, "E2513", {"start": v(-39.1, 5.7) * mm, "end": v(-39.16, 5.7) * mm});
            skLineSegment(sketch, "E2514", {"start": v(-39.16, 5.7) * mm, "end": v(-39.2, 5.71) * mm});
            skLineSegment(sketch, "E2515", {"start": v(-39.2, 5.71) * mm, "end": v(-39.24, 5.72) * mm});
            skLineSegment(sketch, "E2516", {"start": v(-20.56, 11.95) * mm, "end": v(-20.68, 12) * mm});
            skLineSegment(sketch, "E2517", {"start": v(-20.68, 12) * mm, "end": v(-20.82, 12.03) * mm});
            skLineSegment(sketch, "E2518", {"start": v(-20.82, 12.03) * mm, "end": v(-20.96, 12.08) * mm});
            skLineSegment(sketch, "E2519", {"start": v(-20.96, 12.08) * mm, "end": v(-21.11, 12.12) * mm});
            skLineSegment(sketch, "E2520", {"start": v(-21.11, 12.12) * mm, "end": v(-21.27, 12.17) * mm});
            skLineSegment(sketch, "E2521", {"start": v(-21.27, 12.17) * mm, "end": v(-21.43, 12.2) * mm});
            skLineSegment(sketch, "E2522", {"start": v(-21.43, 12.2) * mm, "end": v(-21.6, 12.25) * mm});
            skLineSegment(sketch, "E2523", {"start": v(-21.6, 12.25) * mm, "end": v(-21.76, 12.3) * mm});
            skLineSegment(sketch, "E2524", {"start": v(-21.76, 12.3) * mm, "end": v(-21.93, 12.34) * mm});
            skLineSegment(sketch, "E2525", {"start": v(-21.93, 12.34) * mm, "end": v(-22.1, 12.38) * mm});
            skLineSegment(sketch, "E2526", {"start": v(-22.1, 12.38) * mm, "end": v(-22.29, 12.42) * mm});
            skLineSegment(sketch, "E2527", {"start": v(-22.29, 12.42) * mm, "end": v(-22.47, 12.46) * mm});
            skLineSegment(sketch, "E2528", {"start": v(6.38, 2.34) * mm, "end": v(6.4, 2.31) * mm});
            skLineSegment(sketch, "E2529", {"start": v(6.4, 2.31) * mm, "end": v(6.44, 2.28) * mm});
            skLineSegment(sketch, "E2530", {"start": v(6.44, 2.28) * mm, "end": v(6.47, 2.25) * mm});
            skLineSegment(sketch, "E2531", {"start": v(6.47, 2.25) * mm, "end": v(6.5, 2.21) * mm});
            skLineSegment(sketch, "E2532", {"start": v(6.5, 2.21) * mm, "end": v(6.52, 2.18) * mm});
            skLineSegment(sketch, "E2533", {"start": v(6.52, 2.18) * mm, "end": v(6.55, 2.14) * mm});
            skLineSegment(sketch, "E2534", {"start": v(6.55, 2.14) * mm, "end": v(6.57, 2.1) * mm});
            skLineSegment(sketch, "E2535", {"start": v(6.57, 2.1) * mm, "end": v(6.6, 2.07) * mm});
            skLineSegment(sketch, "E2536", {"start": v(6.6, 2.07) * mm, "end": v(6.62, 2.04) * mm});
            skLineSegment(sketch, "E2537", {"start": v(6.62, 2.04) * mm, "end": v(6.64, 2) * mm});
            skLineSegment(sketch, "E2538", {"start": v(6.64, 2) * mm, "end": v(6.67, 1.97) * mm});
            skLineSegment(sketch, "E2539", {"start": v(6.67, 1.97) * mm, "end": v(6.69, 1.93) * mm});
            skLineSegment(sketch, "E2540", {"start": v(6.69, 1.93) * mm, "end": v(6.7, 1.9) * mm});
            skLineSegment(sketch, "E2541", {"start": v(6.7, 1.9) * mm, "end": v(6.72, 1.86) * mm});
            skLineSegment(sketch, "E2542", {"start": v(6.72, 1.86) * mm, "end": v(6.74, 1.82) * mm});
            skLineSegment(sketch, "E2543", {"start": v(6.74, 1.82) * mm, "end": v(6.76, 1.78) * mm});
            skLineSegment(sketch, "E2544", {"start": v(6.76, 1.78) * mm, "end": v(6.77, 1.74) * mm});
            skLineSegment(sketch, "E2545", {"start": v(6.77, 1.74) * mm, "end": v(6.79, 1.7) * mm});
            skLineSegment(sketch, "E2546", {"start": v(6.79, 1.7) * mm, "end": v(6.8, 1.66) * mm});
            skLineSegment(sketch, "E2547", {"start": v(6.8, 1.66) * mm, "end": v(6.81, 1.62) * mm});
            skLineSegment(sketch, "E2548", {"start": v(6.81, 1.62) * mm, "end": v(6.83, 1.58) * mm});
            skLineSegment(sketch, "E2549", {"start": v(6.83, 1.58) * mm, "end": v(6.84, 1.54) * mm});
            skLineSegment(sketch, "E2550", {"start": v(6.84, 1.54) * mm, "end": v(6.85, 1.5) * mm});
            skLineSegment(sketch, "E2551", {"start": v(6.85, 1.5) * mm, "end": v(6.85, 1.45) * mm});
            skLineSegment(sketch, "E2552", {"start": v(6.85, 1.45) * mm, "end": v(6.86, 1.41) * mm});
            skLineSegment(sketch, "E2553", {"start": v(6.86, 1.41) * mm, "end": v(6.87, 1.37) * mm});
            skLineSegment(sketch, "E2554", {"start": v(6.87, 1.37) * mm, "end": v(6.87, 1.32) * mm});
            skLineSegment(sketch, "E2555", {"start": v(6.87, 1.32) * mm, "end": v(6.88, 1.28) * mm});
            skLineSegment(sketch, "E2556", {"start": v(6.88, 1.28) * mm, "end": v(6.88, 1.23) * mm});
            skLineSegment(sketch, "E2557", {"start": v(6.88, 1.23) * mm, "end": v(6.89, 1.19) * mm});
            skLineSegment(sketch, "E2558", {"start": v(6.89, 1.19) * mm, "end": v(6.89, 1.14) * mm});
            skLineSegment(sketch, "E2559", {"start": v(6.89, 1.14) * mm, "end": v(6.89, 1.1) * mm});
            skLineSegment(sketch, "E2560", {"start": v(7.58, -7.4) * mm, "end": v(7.58, -7.6) * mm});
            skLineSegment(sketch, "E2561", {"start": v(7.58, -7.6) * mm, "end": v(7.59, -7.82) * mm});
            skLineSegment(sketch, "E2562", {"start": v(7.59, -7.82) * mm, "end": v(7.6, -8.04) * mm});
            skLineSegment(sketch, "E2563", {"start": v(7.6, -8.04) * mm, "end": v(7.6, -8.25) * mm});
            skLineSegment(sketch, "E2564", {"start": v(7.6, -8.25) * mm, "end": v(7.62, -8.45) * mm});
            skLineSegment(sketch, "E2565", {"start": v(7.62, -8.45) * mm, "end": v(7.63, -8.64) * mm});
            skLineSegment(sketch, "E2566", {"start": v(7.63, -8.64) * mm, "end": v(7.65, -8.82) * mm});
            skLineSegment(sketch, "E2567", {"start": v(7.65, -8.82) * mm, "end": v(7.67, -8.99) * mm});
            skLineSegment(sketch, "E2568", {"start": v(7.67, -8.99) * mm, "end": v(7.7, -9.15) * mm});
            skLineSegment(sketch, "E2569", {"start": v(7.7, -9.15) * mm, "end": v(7.71, -9.3) * mm});
            skLineSegment(sketch, "E2570", {"start": v(7.71, -9.3) * mm, "end": v(7.74, -9.45) * mm});
            skLineSegment(sketch, "E2571", {"start": v(7.74, -9.45) * mm, "end": v(7.77, -9.58) * mm});
            skLineSegment(sketch, "E2572", {"start": v(7.77, -9.58) * mm, "end": v(7.8, -9.7) * mm});
            skLineSegment(sketch, "E2573", {"start": v(7.8, -9.7) * mm, "end": v(7.83, -9.83) * mm});
            skLineSegment(sketch, "E2574", {"start": v(7.83, -9.83) * mm, "end": v(7.86, -9.94) * mm});
            skLineSegment(sketch, "E2575", {"start": v(7.86, -9.94) * mm, "end": v(7.9, -10.05) * mm});
            skLineSegment(sketch, "E2576", {"start": v(7.9, -10.05) * mm, "end": v(7.93, -10.15) * mm});
            skLineSegment(sketch, "E2577", {"start": v(7.93, -10.15) * mm, "end": v(7.96, -10.25) * mm});
            skLineSegment(sketch, "E2578", {"start": v(7.96, -10.25) * mm, "end": v(8, -10.33) * mm});
            skLineSegment(sketch, "E2579", {"start": v(8, -10.33) * mm, "end": v(8.04, -10.42) * mm});
            skLineSegment(sketch, "E2580", {"start": v(8.04, -10.42) * mm, "end": v(8.08, -10.5) * mm});
            skLineSegment(sketch, "E2581", {"start": v(8.08, -10.5) * mm, "end": v(8.12, -10.57) * mm});
            skLineSegment(sketch, "E2582", {"start": v(8.12, -10.57) * mm, "end": v(8.16, -10.63) * mm});
            skLineSegment(sketch, "E2583", {"start": v(8.16, -10.63) * mm, "end": v(8.2, -10.7) * mm});
            skLineSegment(sketch, "E2584", {"start": v(8.2, -10.7) * mm, "end": v(8.25, -10.76) * mm});
            skLineSegment(sketch, "E2585", {"start": v(8.25, -10.76) * mm, "end": v(8.29, -10.81) * mm});
            skLineSegment(sketch, "E2586", {"start": v(8.29, -10.81) * mm, "end": v(8.33, -10.86) * mm});
            skLineSegment(sketch, "E2587", {"start": v(8.33, -10.86) * mm, "end": v(8.38, -10.9) * mm});
            skLineSegment(sketch, "E2588", {"start": v(8.38, -10.9) * mm, "end": v(8.43, -10.95) * mm});
            skLineSegment(sketch, "E2589", {"start": v(8.43, -10.95) * mm, "end": v(8.47, -10.99) * mm});
            skLineSegment(sketch, "E2590", {"start": v(8.47, -10.99) * mm, "end": v(8.52, -11.03) * mm});
            skLineSegment(sketch, "E2591", {"start": v(8.52, -11.03) * mm, "end": v(8.57, -11.06) * mm});
            skLineSegment(sketch, "E2592", {"start": v(8.57, -11.06) * mm, "end": v(8.62, -11.09) * mm});
            skLineSegment(sketch, "E2593", {"start": v(8.62, -11.09) * mm, "end": v(8.67, -11.11) * mm});
            skLineSegment(sketch, "E2594", {"start": v(8.67, -11.11) * mm, "end": v(8.72, -11.14) * mm});
            skLineSegment(sketch, "E2595", {"start": v(8.72, -11.14) * mm, "end": v(8.78, -11.16) * mm});
            skLineSegment(sketch, "E2596", {"start": v(8.78, -11.16) * mm, "end": v(8.83, -11.17) * mm});
            skLineSegment(sketch, "E2597", {"start": v(8.83, -11.17) * mm, "end": v(8.89, -11.19) * mm});
            skLineSegment(sketch, "E2598", {"start": v(8.89, -11.19) * mm, "end": v(8.95, -11.2) * mm});
            skLineSegment(sketch, "E2599", {"start": v(8.95, -11.2) * mm, "end": v(9, -11.2) * mm});
            skLineSegment(sketch, "E2600", {"start": v(9, -11.2) * mm, "end": v(9.07, -11.21) * mm});
            skLineSegment(sketch, "E2601", {"start": v(9.07, -11.21) * mm, "end": v(9.13, -11.21) * mm});
            skLineSegment(sketch, "E2602", {"start": v(7.98, -6.87) * mm, "end": v(7.98, -5.54) * mm});
            skLineSegment(sketch, "E2603", {"start": v(6.89, 1.1) * mm, "end": v(6.89, 1.05) * mm});
            skLineSegment(sketch, "E2604", {"start": v(6.89, 1.05) * mm, "end": v(6.88, 1) * mm});
            skLineSegment(sketch, "E2605", {"start": v(6.88, 1) * mm, "end": v(6.88, 0.95) * mm});
            skLineSegment(sketch, "E2606", {"start": v(6.88, 0.95) * mm, "end": v(6.88, 0.9) * mm});
            skLineSegment(sketch, "E2607", {"start": v(6.88, 0.9) * mm, "end": v(6.87, 0.85) * mm});
            skLineSegment(sketch, "E2608", {"start": v(6.87, 0.85) * mm, "end": v(6.86, 0.8) * mm});
            skLineSegment(sketch, "E2609", {"start": v(6.86, 0.8) * mm, "end": v(6.85, 0.74) * mm});
            skLineSegment(sketch, "E2610", {"start": v(6.85, 0.74) * mm, "end": v(6.83, 0.68) * mm});
            skLineSegment(sketch, "E2611", {"start": v(6.83, 0.68) * mm, "end": v(6.82, 0.62) * mm});
            skLineSegment(sketch, "E2612", {"start": v(6.82, 0.62) * mm, "end": v(6.8, 0.55) * mm});
            skLineSegment(sketch, "E2613", {"start": v(6.8, 0.55) * mm, "end": v(6.78, 0.48) * mm});
            skLineSegment(sketch, "E2614", {"start": v(6.78, 0.48) * mm, "end": v(6.76, 0.41) * mm});
            skLineSegment(sketch, "E2615", {"start": v(6.76, 0.41) * mm, "end": v(6.73, 0.34) * mm});
            skLineSegment(sketch, "E2616", {"start": v(6.73, 0.34) * mm, "end": v(6.7, 0.27) * mm});
            skLineSegment(sketch, "E2617", {"start": v(6.7, 0.27) * mm, "end": v(6.68, 0.19) * mm});
            skLineSegment(sketch, "E2618", {"start": v(6.68, 0.19) * mm, "end": v(6.64, 0.1) * mm});
            skLineSegment(sketch, "E2619", {"start": v(6.64, 0.1) * mm, "end": v(6.6, 0.02) * mm});
            skLineSegment(sketch, "E2620", {"start": v(6.6, 0.02) * mm, "end": v(6.57, -0.07) * mm});
            skLineSegment(sketch, "E2621", {"start": v(6.57, -0.07) * mm, "end": v(6.52, -0.16) * mm});
            skLineSegment(sketch, "E2622", {"start": v(6.52, -0.16) * mm, "end": v(6.48, -0.26) * mm});
            skLineSegment(sketch, "E2623", {"start": v(6.48, -0.26) * mm, "end": v(6.43, -0.36) * mm});
            skLineSegment(sketch, "E2624", {"start": v(6.43, -0.36) * mm, "end": v(6.37, -0.46) * mm});
            skLineSegment(sketch, "E2625", {"start": v(6.37, -0.46) * mm, "end": v(6.32, -0.57) * mm});
            skLineSegment(sketch, "E2626", {"start": v(6.32, -0.57) * mm, "end": v(6.25, -0.69) * mm});
            skLineSegment(sketch, "E2627", {"start": v(6.25, -0.69) * mm, "end": v(6.24, -0.71) * mm});
            skLineSegment(sketch, "E2628", {"start": v(7.95, -4.64) * mm, "end": v(7.93, -4.71) * mm});
            skLineSegment(sketch, "E2629", {"start": v(7.93, -4.71) * mm, "end": v(7.9, -4.9) * mm});
            skLineSegment(sketch, "E2630", {"start": v(7.9, -4.9) * mm, "end": v(7.85, -5.07) * mm});
            skLineSegment(sketch, "E2631", {"start": v(7.85, -5.07) * mm, "end": v(7.82, -5.24) * mm});
            skLineSegment(sketch, "E2632", {"start": v(7.82, -5.24) * mm, "end": v(7.78, -5.41) * mm});
            skLineSegment(sketch, "E2633", {"start": v(7.78, -5.41) * mm, "end": v(7.75, -5.58) * mm});
            skLineSegment(sketch, "E2634", {"start": v(7.75, -5.58) * mm, "end": v(7.72, -5.74) * mm});
            skLineSegment(sketch, "E2635", {"start": v(7.72, -5.74) * mm, "end": v(7.7, -5.9) * mm});
            skLineSegment(sketch, "E2636", {"start": v(7.7, -5.9) * mm, "end": v(7.68, -6.06) * mm});
            skLineSegment(sketch, "E2637", {"start": v(7.68, -6.06) * mm, "end": v(7.66, -6.22) * mm});
            skLineSegment(sketch, "E2638", {"start": v(7.66, -6.22) * mm, "end": v(7.64, -6.38) * mm});
            skLineSegment(sketch, "E2639", {"start": v(7.64, -6.38) * mm, "end": v(7.62, -6.53) * mm});
            skLineSegment(sketch, "E2640", {"start": v(7.62, -6.53) * mm, "end": v(7.61, -6.68) * mm});
            skLineSegment(sketch, "E2641", {"start": v(7.61, -6.68) * mm, "end": v(7.6, -6.83) * mm});
            skLineSegment(sketch, "E2642", {"start": v(7.6, -6.83) * mm, "end": v(7.6, -6.97) * mm});
            skLineSegment(sketch, "E2643", {"start": v(7.6, -6.97) * mm, "end": v(7.59, -7.12) * mm});
            skLineSegment(sketch, "E2644", {"start": v(7.59, -7.12) * mm, "end": v(7.58, -7.26) * mm});
            skLineSegment(sketch, "E2645", {"start": v(7.58, -7.26) * mm, "end": v(7.58, -7.4) * mm});
            skLineSegment(sketch, "E2646", {"start": v(9.96, -0.7) * mm, "end": v(9.77, -0.97) * mm});
            skLineSegment(sketch, "E2647", {"start": v(9.77, -0.97) * mm, "end": v(9.6, -1.25) * mm});
            skLineSegment(sketch, "E2648", {"start": v(9.6, -1.25) * mm, "end": v(9.43, -1.5) * mm});
            skLineSegment(sketch, "E2649", {"start": v(9.43, -1.5) * mm, "end": v(9.28, -1.76) * mm});
            skLineSegment(sketch, "E2650", {"start": v(9.28, -1.76) * mm, "end": v(9.14, -2) * mm});
            skLineSegment(sketch, "E2651", {"start": v(9.14, -2) * mm, "end": v(9, -2.23) * mm});
            skLineSegment(sketch, "E2652", {"start": v(9, -2.23) * mm, "end": v(8.88, -2.46) * mm});
            skLineSegment(sketch, "E2653", {"start": v(8.88, -2.46) * mm, "end": v(8.76, -2.67) * mm});
            skLineSegment(sketch, "E2654", {"start": v(8.76, -2.67) * mm, "end": v(8.66, -2.88) * mm});
            skLineSegment(sketch, "E2655", {"start": v(8.66, -2.88) * mm, "end": v(8.56, -3.07) * mm});
            skLineSegment(sketch, "E2656", {"start": v(8.56, -3.07) * mm, "end": v(8.47, -3.26) * mm});
            skLineSegment(sketch, "E2657", {"start": v(8.47, -3.26) * mm, "end": v(8.38, -3.44) * mm});
            skLineSegment(sketch, "E2658", {"start": v(8.38, -3.44) * mm, "end": v(8.3, -3.62) * mm});
            skLineSegment(sketch, "E2659", {"start": v(8.3, -3.62) * mm, "end": v(8.24, -3.78) * mm});
            skLineSegment(sketch, "E2660", {"start": v(8.24, -3.78) * mm, "end": v(8.18, -3.94) * mm});
            skLineSegment(sketch, "E2661", {"start": v(8.18, -3.94) * mm, "end": v(8.12, -4.1) * mm});
            skLineSegment(sketch, "E2662", {"start": v(8.12, -4.1) * mm, "end": v(8.07, -4.24) * mm});
            skLineSegment(sketch, "E2663", {"start": v(8.07, -4.24) * mm, "end": v(8.02, -4.38) * mm});
            skLineSegment(sketch, "E2664", {"start": v(8.02, -4.38) * mm, "end": v(7.99, -4.51) * mm});
            skLineSegment(sketch, "E2665", {"start": v(7.99, -4.51) * mm, "end": v(7.95, -4.64) * mm});
            skLineSegment(sketch, "E2666", {"start": v(15.42, 7.16) * mm, "end": v(14.9, 6.45) * mm});
            skLineSegment(sketch, "E2667", {"start": v(14.9, 6.45) * mm, "end": v(14.35, 5.69) * mm});
            skLineSegment(sketch, "E2668", {"start": v(14.35, 5.69) * mm, "end": v(13.78, 4.9) * mm});
            skLineSegment(sketch, "E2669", {"start": v(13.78, 4.9) * mm, "end": v(13.2, 4.06) * mm});
            skLineSegment(sketch, "E2670", {"start": v(13.2, 4.06) * mm, "end": v(12.6, 3.2) * mm});
            skLineSegment(sketch, "E2671", {"start": v(12.6, 3.2) * mm, "end": v(11.97, 2.29) * mm});
            skLineSegment(sketch, "E2672", {"start": v(11.97, 2.29) * mm, "end": v(11.33, 1.35) * mm});
            skLineSegment(sketch, "E2673", {"start": v(11.33, 1.35) * mm, "end": v(10.67, 0.37) * mm});
            skLineSegment(sketch, "E2674", {"start": v(10.67, 0.37) * mm, "end": v(9.96, -0.7) * mm});
            skLineSegment(sketch, "E2675", {"start": v(3.83, -8.35) * mm, "end": v(4.05, -8.23) * mm});
            skLineSegment(sketch, "E2676", {"start": v(4.05, -8.23) * mm, "end": v(4.28, -8.1) * mm});
            skLineSegment(sketch, "E2677", {"start": v(4.28, -8.1) * mm, "end": v(4.52, -7.96) * mm});
            skLineSegment(sketch, "E2678", {"start": v(4.52, -7.96) * mm, "end": v(4.77, -7.8) * mm});
            skLineSegment(sketch, "E2679", {"start": v(4.77, -7.8) * mm, "end": v(5.03, -7.64) * mm});
            skLineSegment(sketch, "E2680", {"start": v(5.03, -7.64) * mm, "end": v(5.3, -7.47) * mm});
            skLineSegment(sketch, "E2681", {"start": v(5.3, -7.47) * mm, "end": v(5.58, -7.28) * mm});
            skLineSegment(sketch, "E2682", {"start": v(5.58, -7.28) * mm, "end": v(5.88, -7.08) * mm});
            skLineSegment(sketch, "E2683", {"start": v(5.88, -7.08) * mm, "end": v(6.19, -6.86) * mm});
            skLineSegment(sketch, "E2684", {"start": v(6.19, -6.86) * mm, "end": v(6.5, -6.64) * mm});
            skLineSegment(sketch, "E2685", {"start": v(6.5, -6.64) * mm, "end": v(6.84, -6.4) * mm});
            skLineSegment(sketch, "E2686", {"start": v(6.84, -6.4) * mm, "end": v(7.2, -6.13) * mm});
            skLineSegment(sketch, "E2687", {"start": v(7.2, -6.13) * mm, "end": v(7.56, -5.86) * mm});
            skLineSegment(sketch, "E2688", {"start": v(7.56, -5.86) * mm, "end": v(7.94, -5.57) * mm});
            skLineSegment(sketch, "E2689", {"start": v(7.94, -5.57) * mm, "end": v(7.98, -5.54) * mm});
            skLineSegment(sketch, "E2690", {"start": v(-28, 1.36) * mm, "end": v(-28.6, 1.22) * mm});
            skLineSegment(sketch, "E2691", {"start": v(-28.6, 1.22) * mm, "end": v(-29.23, 1.07) * mm});
            skLineSegment(sketch, "E2692", {"start": v(-29.23, 1.07) * mm, "end": v(-29.88, 0.92) * mm});
            skLineSegment(sketch, "E2693", {"start": v(-29.88, 0.92) * mm, "end": v(-30.56, 0.77) * mm});
            skLineSegment(sketch, "E2694", {"start": v(-30.56, 0.77) * mm, "end": v(-31.26, 0.61) * mm});
            skLineSegment(sketch, "E2695", {"start": v(-31.26, 0.61) * mm, "end": v(-31.98, 0.46) * mm});
            skLineSegment(sketch, "E2696", {"start": v(-31.98, 0.46) * mm, "end": v(-32.73, 0.3) * mm});
            skLineSegment(sketch, "E2697", {"start": v(-32.73, 0.3) * mm, "end": v(-33.5, 0.15) * mm});
            skLineSegment(sketch, "E2698", {"start": v(-33.5, 0.15) * mm, "end": v(-34.3, 0) * mm});
            skLineSegment(sketch, "E2699", {"start": v(-34.3, 0) * mm, "end": v(-35.12, -0.16) * mm});
            skLineSegment(sketch, "E2700", {"start": v(-37.35, 5.12) * mm, "end": v(-37.24, 5.12) * mm});
            skLineSegment(sketch, "E2701", {"start": v(-37.69, 5.1) * mm, "end": v(-37.35, 5.12) * mm});
            skLineSegment(sketch, "E2702", {"start": v(-27.67, 8.21) * mm, "end": v(-27.39, 8.23) * mm});
            skLineSegment(sketch, "E2703", {"start": v(-27.39, 8.23) * mm, "end": v(-27, 8.24) * mm});
            skLineSegment(sketch, "E2704", {"start": v(-27, 8.24) * mm, "end": v(-26.87, 8.25) * mm});
            skLineSegment(sketch, "E2705", {"start": v(-26.87, 8.25) * mm, "end": v(-26.74, 8.25) * mm});
            skLineSegment(sketch, "E2706", {"start": v(-26.74, 8.25) * mm, "end": v(-26.62, 8.26) * mm});
            skLineSegment(sketch, "E2707", {"start": v(-26.62, 8.26) * mm, "end": v(-26.5, 8.26) * mm});
            skLineSegment(sketch, "E2708", {"start": v(-26.5, 8.26) * mm, "end": v(-26.37, 8.26) * mm});
            skLineSegment(sketch, "E2709", {"start": v(-26.37, 8.26) * mm, "end": v(-26.26, 8.26) * mm});
            skLineSegment(sketch, "E2710", {"start": v(-30.3, 8) * mm, "end": v(-30.26, 8) * mm});
            skLineSegment(sketch, "E2711", {"start": v(-30.26, 8) * mm, "end": v(-30.22, 8) * mm});
            skLineSegment(sketch, "E2712", {"start": v(-30.22, 8) * mm, "end": v(-30.16, 8) * mm});
            skLineSegment(sketch, "E2713", {"start": v(-30.16, 8) * mm, "end": v(-30.09, 8.01) * mm});
            skLineSegment(sketch, "E2714", {"start": v(-30.09, 8.01) * mm, "end": v(-30, 8.02) * mm});
            skLineSegment(sketch, "E2715", {"start": v(-30, 8.02) * mm, "end": v(-29.88, 8.03) * mm});
            skLineSegment(sketch, "E2716", {"start": v(-26.26, 8.26) * mm, "end": v(-26.13, 8.26) * mm});
            skLineSegment(sketch, "E2717", {"start": v(-26.13, 8.26) * mm, "end": v(-25.8, 8.26) * mm});
            skLineSegment(sketch, "E2718", {"start": v(-25.8, 8.26) * mm, "end": v(-25.48, 8.25) * mm});
            skLineSegment(sketch, "E2719", {"start": v(-25.48, 8.25) * mm, "end": v(-25.17, 8.24) * mm});
            skLineSegment(sketch, "E2720", {"start": v(-25.17, 8.24) * mm, "end": v(-24.87, 8.22) * mm});
            skLineSegment(sketch, "E2721", {"start": v(-24.87, 8.22) * mm, "end": v(-24.57, 8.2) * mm});
            skLineSegment(sketch, "E2722", {"start": v(-24.57, 8.2) * mm, "end": v(-24.28, 8.18) * mm});
            skLineSegment(sketch, "E2723", {"start": v(-24.28, 8.18) * mm, "end": v(-24, 8.16) * mm});
            skLineSegment(sketch, "E2724", {"start": v(-24, 8.16) * mm, "end": v(-23.73, 8.13) * mm});
            skLineSegment(sketch, "E2725", {"start": v(-23.73, 8.13) * mm, "end": v(-23.46, 8.1) * mm});
            skLineSegment(sketch, "E2726", {"start": v(-23.46, 8.1) * mm, "end": v(-23.2, 8.07) * mm});
            skLineSegment(sketch, "E2727", {"start": v(-23.2, 8.07) * mm, "end": v(-22.94, 8.03) * mm});
            skLineSegment(sketch, "E2728", {"start": v(-22.94, 8.03) * mm, "end": v(-22.7, 7.99) * mm});
            skLineSegment(sketch, "E2729", {"start": v(-22.7, 7.99) * mm, "end": v(-22.46, 7.94) * mm});
            skLineSegment(sketch, "E2730", {"start": v(-22.46, 7.94) * mm, "end": v(-22.22, 7.9) * mm});
            skLineSegment(sketch, "E2731", {"start": v(-22.22, 7.9) * mm, "end": v(-22, 7.85) * mm});
            skLineSegment(sketch, "E2732", {"start": v(-22, 7.85) * mm, "end": v(-21.77, 7.8) * mm});
            skLineSegment(sketch, "E2733", {"start": v(-21.77, 7.8) * mm, "end": v(-21.55, 7.74) * mm});
            skLineSegment(sketch, "E2734", {"start": v(-21.55, 7.74) * mm, "end": v(-21.34, 7.69) * mm});
            skLineSegment(sketch, "E2735", {"start": v(43.5, 8.22) * mm, "end": v(43.5, 8.22) * mm});
            skLineSegment(sketch, "E2736", {"start": v(43.5, 8.22) * mm, "end": v(43.52, 8.22) * mm});
            skLineSegment(sketch, "E2737", {"start": v(43.52, 8.22) * mm, "end": v(43.53, 8.22) * mm});
            skLineSegment(sketch, "E2738", {"start": v(43.53, 8.22) * mm, "end": v(43.54, 8.22) * mm});
            skLineSegment(sketch, "E2739", {"start": v(43.54, 8.22) * mm, "end": v(43.55, 8.22) * mm});
            skLineSegment(sketch, "E2740", {"start": v(43.55, 8.22) * mm, "end": v(43.56, 8.21) * mm});
            skLineSegment(sketch, "E2741", {"start": v(43.56, 8.21) * mm, "end": v(43.57, 8.21) * mm});
            skLineSegment(sketch, "E2742", {"start": v(43.57, 8.21) * mm, "end": v(43.59, 8.2) * mm});
            skLineSegment(sketch, "E2743", {"start": v(43.59, 8.2) * mm, "end": v(43.6, 8.2) * mm});
            skLineSegment(sketch, "E2744", {"start": v(43.6, 8.2) * mm, "end": v(43.6, 8.2) * mm});
            skLineSegment(sketch, "E2745", {"start": v(43.6, 8.2) * mm, "end": v(43.62, 8.2) * mm});
            skLineSegment(sketch, "E2746", {"start": v(43.62, 8.2) * mm, "end": v(43.63, 8.2) * mm});
            skLineSegment(sketch, "E2747", {"start": v(43.63, 8.2) * mm, "end": v(43.63, 8.19) * mm});
            skLineSegment(sketch, "E2748", {"start": v(43.63, 8.19) * mm, "end": v(43.64, 8.18) * mm});
            skLineSegment(sketch, "E2749", {"start": v(43.64, 8.18) * mm, "end": v(43.65, 8.18) * mm});
            skLineSegment(sketch, "E2750", {"start": v(43.65, 8.18) * mm, "end": v(43.66, 8.17) * mm});
            skLineSegment(sketch, "E2751", {"start": v(43.66, 8.17) * mm, "end": v(43.67, 8.16) * mm});
            skLineSegment(sketch, "E2752", {"start": v(43.67, 8.16) * mm, "end": v(43.68, 8.16) * mm});
            skLineSegment(sketch, "E2753", {"start": v(43.68, 8.16) * mm, "end": v(43.69, 8.15) * mm});
            skLineSegment(sketch, "E2754", {"start": v(43.69, 8.15) * mm, "end": v(43.7, 8.14) * mm});
            skLineSegment(sketch, "E2755", {"start": v(43.7, 8.14) * mm, "end": v(43.7, 8.13) * mm});
            skLineSegment(sketch, "E2756", {"start": v(43.7, 8.13) * mm, "end": v(43.7, 8.12) * mm});
            skLineSegment(sketch, "E2757", {"start": v(43.7, 8.12) * mm, "end": v(43.72, 8.12) * mm});
            skLineSegment(sketch, "E2758", {"start": v(43.72, 8.12) * mm, "end": v(43.72, 8.1) * mm});
            skLineSegment(sketch, "E2759", {"start": v(43.72, 8.1) * mm, "end": v(43.73, 8.1) * mm});
            skLineSegment(sketch, "E2760", {"start": v(43.73, 8.1) * mm, "end": v(43.74, 8.09) * mm});
            skLineSegment(sketch, "E2761", {"start": v(43.74, 8.09) * mm, "end": v(43.74, 8.07) * mm});
            skLineSegment(sketch, "E2762", {"start": v(43.74, 8.07) * mm, "end": v(43.75, 8.06) * mm});
            skLineSegment(sketch, "E2763", {"start": v(43.75, 8.06) * mm, "end": v(43.76, 8.05) * mm});
            skLineSegment(sketch, "E2764", {"start": v(43.76, 8.05) * mm, "end": v(43.76, 8.04) * mm});
            skLineSegment(sketch, "E2765", {"start": v(43.76, 8.04) * mm, "end": v(43.77, 8.03) * mm});
            skLineSegment(sketch, "E2766", {"start": v(43.77, 8.03) * mm, "end": v(43.77, 8.01) * mm});
            skLineSegment(sketch, "E2767", {"start": v(43.77, 8.01) * mm, "end": v(43.78, 8) * mm});
            skLineSegment(sketch, "E2768", {"start": v(43.78, 8) * mm, "end": v(43.78, 7.99) * mm});
            skLineSegment(sketch, "E2769", {"start": v(43.78, 7.99) * mm, "end": v(43.79, 7.97) * mm});
            skLineSegment(sketch, "E2770", {"start": v(43.79, 7.97) * mm, "end": v(43.79, 7.95) * mm});
            skLineSegment(sketch, "E2771", {"start": v(43.79, 7.95) * mm, "end": v(43.8, 7.94) * mm});
            skLineSegment(sketch, "E2772", {"start": v(43.8, 7.94) * mm, "end": v(43.8, 7.92) * mm});
            skLineSegment(sketch, "E2773", {"start": v(43.8, 7.92) * mm, "end": v(43.8, 7.9) * mm});
            skLineSegment(sketch, "E2774", {"start": v(43.8, 7.9) * mm, "end": v(43.8, 7.89) * mm});
            skLineSegment(sketch, "E2775", {"start": v(43.8, 7.89) * mm, "end": v(43.8, 7.87) * mm});
            skLineSegment(sketch, "E2776", {"start": v(43.8, 7.87) * mm, "end": v(43.8, 7.85) * mm});
            skLineSegment(sketch, "E2777", {"start": v(43.8, 7.85) * mm, "end": v(43.8, 7.83) * mm});
            skLineSegment(sketch, "E2778", {"start": v(43.8, 7.83) * mm, "end": v(43.8, 7.8) * mm});
            skLineSegment(sketch, "E2779", {"start": v(43.8, 7.8) * mm, "end": v(43.8, 7.79) * mm});
            skLineSegment(sketch, "E2780", {"start": v(43.8, 7.79) * mm, "end": v(43.8, 7.77) * mm});
            skLineSegment(sketch, "E2781", {"start": v(43.8, 7.77) * mm, "end": v(43.8, 7.76) * mm});
            skLineSegment(sketch, "E2782", {"start": v(-25.15, 12.9) * mm, "end": v(-25.2, 12.91) * mm});
            skLineSegment(sketch, "E2783", {"start": v(-25.2, 12.91) * mm, "end": v(-25.45, 12.94) * mm});
            skLineSegment(sketch, "E2784", {"start": v(-25.45, 12.94) * mm, "end": v(-25.7, 12.97) * mm});
            skLineSegment(sketch, "E2785", {"start": v(-25.7, 12.97) * mm, "end": v(-25.94, 12.99) * mm});
            skLineSegment(sketch, "E2786", {"start": v(-25.94, 12.99) * mm, "end": v(-26.18, 13) * mm});
            skLineSegment(sketch, "E2787", {"start": v(-26.18, 13) * mm, "end": v(-26.43, 13.03) * mm});
            skLineSegment(sketch, "E2788", {"start": v(-26.43, 13.03) * mm, "end": v(-26.67, 13.04) * mm});
            skLineSegment(sketch, "E2789", {"start": v(-26.67, 13.04) * mm, "end": v(-26.8, 13.05) * mm});
            skLineSegment(sketch, "E2790", {"start": v(-26.8, 13.05) * mm, "end": v(-26.92, 13.05) * mm});
            skLineSegment(sketch, "E2791", {"start": v(-26.92, 13.05) * mm, "end": v(-27.17, 13.07) * mm});
            skLineSegment(sketch, "E2792", {"start": v(-27.17, 13.07) * mm, "end": v(-27.41, 13.07) * mm});
            skLineSegment(sketch, "E2793", {"start": v(-27.41, 13.07) * mm, "end": v(-27.66, 13.08) * mm});
            skLineSegment(sketch, "E2794", {"start": v(-27.66, 13.08) * mm, "end": v(-27.91, 13.08) * mm});
            skLineSegment(sketch, "E2795", {"start": v(-27.91, 13.08) * mm, "end": v(-28.17, 13.08) * mm});
            skLineSegment(sketch, "E2796", {"start": v(-22.47, 12.46) * mm, "end": v(-22.67, 12.5) * mm});
            skLineSegment(sketch, "E2797", {"start": v(-22.67, 12.5) * mm, "end": v(-22.91, 12.55) * mm});
            skLineSegment(sketch, "E2798", {"start": v(-22.91, 12.55) * mm, "end": v(-23.16, 12.6) * mm});
            skLineSegment(sketch, "E2799", {"start": v(-23.16, 12.6) * mm, "end": v(-23.41, 12.64) * mm});
            skLineSegment(sketch, "E2800", {"start": v(-23.41, 12.64) * mm, "end": v(-23.66, 12.69) * mm});
            skLineSegment(sketch, "E2801", {"start": v(-23.66, 12.69) * mm, "end": v(-23.9, 12.73) * mm});
            skLineSegment(sketch, "E2802", {"start": v(-23.9, 12.73) * mm, "end": v(-24.16, 12.77) * mm});
            skLineSegment(sketch, "E2803", {"start": v(-24.16, 12.77) * mm, "end": v(-24.4, 12.8) * mm});
            skLineSegment(sketch, "E2804", {"start": v(-24.4, 12.8) * mm, "end": v(-24.65, 12.84) * mm});
            skLineSegment(sketch, "E2805", {"start": v(-24.65, 12.84) * mm, "end": v(-24.9, 12.87) * mm});
            skLineSegment(sketch, "E2806", {"start": v(-24.9, 12.87) * mm, "end": v(-25.15, 12.9) * mm});
            skLineSegment(sketch, "E2807", {"start": v(10.34, -7.06) * mm, "end": v(10.34, -4.68) * mm});
            skLineSegment(sketch, "E2808", {"start": v(21.04, 9.01) * mm, "end": v(21.35, 9.46) * mm});
            skLineSegment(sketch, "E2809", {"start": v(21.35, 9.46) * mm, "end": v(21.63, 9.88) * mm});
            skLineSegment(sketch, "E2810", {"start": v(21.63, 9.88) * mm, "end": v(21.9, 10.27) * mm});
            skLineSegment(sketch, "E2811", {"start": v(21.9, 10.27) * mm, "end": v(22.14, 10.64) * mm});
            skLineSegment(sketch, "E2812", {"start": v(22.14, 10.64) * mm, "end": v(22.36, 10.98) * mm});
            skLineSegment(sketch, "E2813", {"start": v(22.36, 10.98) * mm, "end": v(22.57, 11.3) * mm});
            skLineSegment(sketch, "E2814", {"start": v(22.57, 11.3) * mm, "end": v(22.75, 11.59) * mm});
            skLineSegment(sketch, "E2815", {"start": v(22.75, 11.59) * mm, "end": v(22.92, 11.85) * mm});
            skLineSegment(sketch, "E2816", {"start": v(22.92, 11.85) * mm, "end": v(23.07, 12.1) * mm});
            skLineSegment(sketch, "E2817", {"start": v(19.73, 7.14) * mm, "end": v(21.04, 9.01) * mm});
            skLineSegment(sketch, "E2818", {"start": v(18.7, 5.7) * mm, "end": v(19.73, 7.14) * mm});
            skLineSegment(sketch, "E2819", {"start": v(18.16, 4.93) * mm, "end": v(18.32, 5.15) * mm});
            skLineSegment(sketch, "E2820", {"start": v(18.32, 5.15) * mm, "end": v(18.7, 5.7) * mm});
            skLineSegment(sketch, "E2821", {"start": v(18, 4.71) * mm, "end": v(18.16, 4.93) * mm});
            skLineSegment(sketch, "E2822", {"start": v(17.63, 4.22) * mm, "end": v(18, 4.71) * mm});
            skLineSegment(sketch, "E2823", {"start": v(17.2, 3.66) * mm, "end": v(17.63, 4.22) * mm});
            skLineSegment(sketch, "E2824", {"start": v(16.73, 3.04) * mm, "end": v(17.2, 3.66) * mm});
            skLineSegment(sketch, "E2825", {"start": v(16.2, 2.34) * mm, "end": v(16.73, 3.04) * mm});
            skLineSegment(sketch, "E2826", {"start": v(15.31, 1.22) * mm, "end": v(16.2, 2.34) * mm});
            skLineSegment(sketch, "E2827", {"start": v(14.75, 0.5) * mm, "end": v(15.31, 1.22) * mm});
            skLineSegment(sketch, "E2828", {"start": v(13.41, -1.14) * mm, "end": v(13.67, -0.83) * mm});
            skLineSegment(sketch, "E2829", {"start": v(13.67, -0.83) * mm, "end": v(13.93, -0.51) * mm});
            skLineSegment(sketch, "E2830", {"start": v(13.93, -0.51) * mm, "end": v(14.2, -0.18) * mm});
            skLineSegment(sketch, "E2831", {"start": v(14.2, -0.18) * mm, "end": v(14.75, 0.5) * mm});
            skLineSegment(sketch, "E2832", {"start": v(12.9, -1.75) * mm, "end": v(13.41, -1.14) * mm});
            skLineSegment(sketch, "E2833", {"start": v(12.38, -2.36) * mm, "end": v(12.9, -1.75) * mm});
            skLineSegment(sketch, "E2834", {"start": v(10.34, -4.68) * mm, "end": v(10.65, -4.34) * mm});
            skLineSegment(sketch, "E2835", {"start": v(10.65, -4.34) * mm, "end": v(10.96, -4) * mm});
            skLineSegment(sketch, "E2836", {"start": v(10.96, -4) * mm, "end": v(11.26, -3.66) * mm});
            skLineSegment(sketch, "E2837", {"start": v(11.26, -3.66) * mm, "end": v(11.55, -3.33) * mm});
            skLineSegment(sketch, "E2838", {"start": v(11.55, -3.33) * mm, "end": v(11.83, -3) * mm});
            skLineSegment(sketch, "E2839", {"start": v(11.83, -3) * mm, "end": v(12.38, -2.36) * mm});
            skLineSegment(sketch, "E2840", {"start": v(14.95, -2.22) * mm, "end": v(14.55, -2.6) * mm});
            skLineSegment(sketch, "E2841", {"start": v(14.55, -2.6) * mm, "end": v(14.55, -2.61) * mm});
            skLineSegment(sketch, "E2842", {"start": v(14.55, -2.61) * mm, "end": v(14.13, -3.02) * mm});
            skLineSegment(sketch, "E2843", {"start": v(14.13, -3.02) * mm, "end": v(13.7, -3.46) * mm});
            skLineSegment(sketch, "E2844", {"start": v(13.7, -3.46) * mm, "end": v(13.27, -3.9) * mm});
            skLineSegment(sketch, "E2845", {"start": v(13.27, -3.9) * mm, "end": v(12.82, -4.38) * mm});
            skLineSegment(sketch, "E2846", {"start": v(12.82, -4.38) * mm, "end": v(12.35, -4.88) * mm});
            skLineSegment(sketch, "E2847", {"start": v(12.35, -4.88) * mm, "end": v(11.87, -5.4) * mm});
            skLineSegment(sketch, "E2848", {"start": v(11.87, -5.4) * mm, "end": v(11.37, -5.93) * mm});
            skLineSegment(sketch, "E2849", {"start": v(11.37, -5.93) * mm, "end": v(10.86, -6.48) * mm});
            skLineSegment(sketch, "E2850", {"start": v(10.86, -6.48) * mm, "end": v(10.34, -7.06) * mm});
            skLineSegment(sketch, "E2851", {"start": v(7.98, -6.87) * mm, "end": v(7.07, -7.74) * mm});
            skLineSegment(sketch, "E2852", {"start": v(7.07, -7.74) * mm, "end": v(6.32, -8.46) * mm});
            skLineSegment(sketch, "E2853", {"start": v(6.32, -8.46) * mm, "end": v(5.97, -8.79) * mm});
            skLineSegment(sketch, "E2854", {"start": v(5.97, -8.79) * mm, "end": v(5.64, -9.1) * mm});
            skLineSegment(sketch, "E2855", {"start": v(5.64, -9.1) * mm, "end": v(5.32, -9.4) * mm});
            skLineSegment(sketch, "E2856", {"start": v(5.32, -9.4) * mm, "end": v(5.02, -9.66) * mm});
            skLineSegment(sketch, "E2857", {"start": v(5.02, -9.66) * mm, "end": v(4.75, -9.9) * mm});
            skLineSegment(sketch, "E2858", {"start": v(4.75, -9.9) * mm, "end": v(4.51, -10.1) * mm});
            skLineSegment(sketch, "E2859", {"start": v(4.51, -10.1) * mm, "end": v(4.46, -10.15) * mm});
            skLineSegment(sketch, "E2860", {"start": v(4.46, -10.15) * mm, "end": v(4.28, -10.3) * mm});
            skLineSegment(sketch, "E2861", {"start": v(4.28, -10.3) * mm, "end": v(4.1, -10.45) * mm});
            skLineSegment(sketch, "E2862", {"start": v(4.1, -10.45) * mm, "end": v(3.93, -10.58) * mm});
            skLineSegment(sketch, "E2863", {"start": v(3.93, -10.58) * mm, "end": v(3.77, -10.71) * mm});
            skLineSegment(sketch, "E2864", {"start": v(3.77, -10.71) * mm, "end": v(3.6, -10.84) * mm});
            skLineSegment(sketch, "E2865", {"start": v(3.6, -10.84) * mm, "end": v(3.44, -10.96) * mm});
            skLineSegment(sketch, "E2866", {"start": v(3.44, -10.96) * mm, "end": v(3.29, -11.08) * mm});
            skLineSegment(sketch, "E2867", {"start": v(3.29, -11.08) * mm, "end": v(3.13, -11.18) * mm});
            skLineSegment(sketch, "E2868", {"start": v(3.13, -11.18) * mm, "end": v(2.98, -11.29) * mm});
            skLineSegment(sketch, "E2869", {"start": v(2.98, -11.29) * mm, "end": v(2.83, -11.39) * mm});
            skLineSegment(sketch, "E2870", {"start": v(2.83, -11.39) * mm, "end": v(2.69, -11.48) * mm});
            skLineSegment(sketch, "E2871", {"start": v(2.69, -11.48) * mm, "end": v(2.55, -11.57) * mm});
            skLineSegment(sketch, "E2872", {"start": v(2.55, -11.57) * mm, "end": v(2.4, -11.66) * mm});
            skLineSegment(sketch, "E2873", {"start": v(2.4, -11.66) * mm, "end": v(2.27, -11.74) * mm});
            skLineSegment(sketch, "E2874", {"start": v(2.27, -11.74) * mm, "end": v(2.14, -11.82) * mm});
            skLineSegment(sketch, "E2875", {"start": v(2.14, -11.82) * mm, "end": v(2, -11.89) * mm});
            skLineSegment(sketch, "E2876", {"start": v(16.45, -3.27) * mm, "end": v(16.54, -3.2) * mm});
            skLineSegment(sketch, "E2877", {"start": v(16.54, -3.2) * mm, "end": v(16.64, -3.11) * mm});
            skLineSegment(sketch, "E2878", {"start": v(16.64, -3.11) * mm, "end": v(16.74, -3.04) * mm});
            skLineSegment(sketch, "E2879", {"start": v(16.74, -3.04) * mm, "end": v(16.84, -2.96) * mm});
            skLineSegment(sketch, "E2880", {"start": v(16.84, -2.96) * mm, "end": v(16.94, -2.89) * mm});
            skLineSegment(sketch, "E2881", {"start": v(16.94, -2.89) * mm, "end": v(17.05, -2.81) * mm});
            skLineSegment(sketch, "E2882", {"start": v(17.05, -2.81) * mm, "end": v(17.16, -2.73) * mm});
            skLineSegment(sketch, "E2883", {"start": v(17.16, -2.73) * mm, "end": v(17.27, -2.66) * mm});
            skLineSegment(sketch, "E2884", {"start": v(17.27, -2.66) * mm, "end": v(17.38, -2.58) * mm});
            skLineSegment(sketch, "E2885", {"start": v(17.38, -2.58) * mm, "end": v(17.5, -2.5) * mm});
            skLineSegment(sketch, "E2886", {"start": v(17.5, -2.5) * mm, "end": v(17.62, -2.43) * mm});
            skLineSegment(sketch, "E2887", {"start": v(17.62, -2.43) * mm, "end": v(17.75, -2.35) * mm});
            skLineSegment(sketch, "E2888", {"start": v(17.75, -2.35) * mm, "end": v(17.88, -2.28) * mm});
            skLineSegment(sketch, "E2889", {"start": v(17.88, -2.28) * mm, "end": v(18, -2.2) * mm});
            skLineSegment(sketch, "E2890", {"start": v(18, -2.2) * mm, "end": v(18.14, -2.12) * mm});
            skLineSegment(sketch, "E2891", {"start": v(18.24, 0.62) * mm, "end": v(18.07, 0.5) * mm});
            skLineSegment(sketch, "E2892", {"start": v(18.07, 0.5) * mm, "end": v(17.89, 0.37) * mm});
            skLineSegment(sketch, "E2893", {"start": v(17.89, 0.37) * mm, "end": v(17.7, 0.22) * mm});
            skLineSegment(sketch, "E2894", {"start": v(17.7, 0.22) * mm, "end": v(17.5, 0.07) * mm});
            skLineSegment(sketch, "E2895", {"start": v(17.5, 0.07) * mm, "end": v(17.3, -0.1) * mm});
            skLineSegment(sketch, "E2896", {"start": v(17.3, -0.1) * mm, "end": v(17.08, -0.28) * mm});
            skLineSegment(sketch, "E2897", {"start": v(17.08, -0.28) * mm, "end": v(16.85, -0.47) * mm});
            skLineSegment(sketch, "E2898", {"start": v(16.85, -0.47) * mm, "end": v(16.61, -0.68) * mm});
            skLineSegment(sketch, "E2899", {"start": v(16.61, -0.68) * mm, "end": v(16.36, -0.9) * mm});
            skLineSegment(sketch, "E2900", {"start": v(16.36, -0.9) * mm, "end": v(16.1, -1.14) * mm});
            skLineSegment(sketch, "E2901", {"start": v(16.1, -1.14) * mm, "end": v(15.81, -1.4) * mm});
            skLineSegment(sketch, "E2902", {"start": v(15.81, -1.4) * mm, "end": v(15.52, -1.67) * mm});
            skLineSegment(sketch, "E2903", {"start": v(15.52, -1.67) * mm, "end": v(15.2, -1.97) * mm});
            skLineSegment(sketch, "E2904", {"start": v(15.2, -1.97) * mm, "end": v(14.95, -2.22) * mm});
            skLineSegment(sketch, "E2905", {"start": v(44.34, 11.8) * mm, "end": v(44.22, 11.72) * mm});
            skLineSegment(sketch, "E2906", {"start": v(44.22, 11.72) * mm, "end": v(44.09, 11.64) * mm});
            skLineSegment(sketch, "E2907", {"start": v(44.09, 11.64) * mm, "end": v(43.96, 11.55) * mm});
            skLineSegment(sketch, "E2908", {"start": v(43.96, 11.55) * mm, "end": v(43.83, 11.46) * mm});
            skLineSegment(sketch, "E2909", {"start": v(43.83, 11.46) * mm, "end": v(43.7, 11.36) * mm});
            skLineSegment(sketch, "E2910", {"start": v(43.7, 11.36) * mm, "end": v(43.55, 11.26) * mm});
            skLineSegment(sketch, "E2911", {"start": v(43.55, 11.26) * mm, "end": v(43.41, 11.15) * mm});
            skLineSegment(sketch, "E2912", {"start": v(43.41, 11.15) * mm, "end": v(43.27, 11.03) * mm});
            skLineSegment(sketch, "E2913", {"start": v(43.27, 11.03) * mm, "end": v(43.13, 10.9) * mm});
            skLineSegment(sketch, "E2914", {"start": v(43.13, 10.9) * mm, "end": v(42.98, 10.78) * mm});
            skLineSegment(sketch, "E2915", {"start": v(42.98, 10.78) * mm, "end": v(42.83, 10.64) * mm});
            skLineSegment(sketch, "E2916", {"start": v(42.83, 10.64) * mm, "end": v(42.68, 10.5) * mm});
            skLineSegment(sketch, "E2917", {"start": v(42.68, 10.5) * mm, "end": v(42.52, 10.34) * mm});
            skLineSegment(sketch, "E2918", {"start": v(42.52, 10.34) * mm, "end": v(42.36, 10.18) * mm});
            skLineSegment(sketch, "E2919", {"start": v(42.36, 10.18) * mm, "end": v(42.2, 10.01) * mm});
            skLineSegment(sketch, "E2920", {"start": v(42.2, 10.01) * mm, "end": v(42.04, 9.83) * mm});
            skLineSegment(sketch, "E2921", {"start": v(42.04, 9.83) * mm, "end": v(41.87, 9.65) * mm});
            skLineSegment(sketch, "E2922", {"start": v(41.87, 9.65) * mm, "end": v(41.7, 9.45) * mm});
            skLineSegment(sketch, "E2923", {"start": v(41.7, 9.45) * mm, "end": v(41.52, 9.24) * mm});
            skLineSegment(sketch, "E2924", {"start": v(41.52, 9.24) * mm, "end": v(41.34, 9.03) * mm});
            skLineSegment(sketch, "E2925", {"start": v(41.34, 9.03) * mm, "end": v(41.15, 8.8) * mm});
            skLineSegment(sketch, "E2926", {"start": v(41.15, 8.8) * mm, "end": v(41.15, 8.8) * mm});
            skLineSegment(sketch, "E2927", {"start": v(2, -11.89) * mm, "end": v(1.91, -11.94) * mm});
            skLineSegment(sketch, "E2928", {"start": v(1.91, -11.94) * mm, "end": v(1.81, -11.99) * mm});
            skLineSegment(sketch, "E2929", {"start": v(1.81, -11.99) * mm, "end": v(1.71, -12.04) * mm});
            skLineSegment(sketch, "E2930", {"start": v(1.71, -12.04) * mm, "end": v(1.62, -12.08) * mm});
            skLineSegment(sketch, "E2931", {"start": v(1.62, -12.08) * mm, "end": v(1.52, -12.12) * mm});
            skLineSegment(sketch, "E2932", {"start": v(1.52, -12.12) * mm, "end": v(1.42, -12.16) * mm});
            skLineSegment(sketch, "E2933", {"start": v(1.42, -12.16) * mm, "end": v(1.33, -12.2) * mm});
            skLineSegment(sketch, "E2934", {"start": v(1.33, -12.2) * mm, "end": v(1.24, -12.24) * mm});
            skLineSegment(sketch, "E2935", {"start": v(1.24, -12.24) * mm, "end": v(1.14, -12.27) * mm});
            skLineSegment(sketch, "E2936", {"start": v(1.14, -12.27) * mm, "end": v(1.05, -12.3) * mm});
            skLineSegment(sketch, "E2937", {"start": v(1.05, -12.3) * mm, "end": v(0.96, -12.33) * mm});
            skLineSegment(sketch, "E2938", {"start": v(0.96, -12.33) * mm, "end": v(0.87, -12.36) * mm});
            skLineSegment(sketch, "E2939", {"start": v(0.87, -12.36) * mm, "end": v(0.78, -12.38) * mm});
            skLineSegment(sketch, "E2940", {"start": v(0.78, -12.38) * mm, "end": v(0.69, -12.4) * mm});
            skLineSegment(sketch, "E2941", {"start": v(0.69, -12.4) * mm, "end": v(0.6, -12.43) * mm});
            skLineSegment(sketch, "E2942", {"start": v(0.6, -12.43) * mm, "end": v(0.51, -12.44) * mm});
            skLineSegment(sketch, "E2943", {"start": v(0.51, -12.44) * mm, "end": v(0.42, -12.46) * mm});
            skLineSegment(sketch, "E2944", {"start": v(0.42, -12.46) * mm, "end": v(0.34, -12.48) * mm});
            skLineSegment(sketch, "E2945", {"start": v(0.34, -12.48) * mm, "end": v(0.25, -12.49) * mm});
            skLineSegment(sketch, "E2946", {"start": v(0.25, -12.49) * mm, "end": v(0.16, -12.5) * mm});
            skLineSegment(sketch, "E2947", {"start": v(0.16, -12.5) * mm, "end": v(0.08, -12.5) * mm});
            skLineSegment(sketch, "E2948", {"start": v(0.08, -12.5) * mm, "end": v(0, -12.51) * mm});
            skLineSegment(sketch, "E2949", {"start": v(0, -12.51) * mm, "end": v(-0.1, -12.52) * mm});
            skLineSegment(sketch, "E2950", {"start": v(-0.1, -12.52) * mm, "end": v(-0.17, -12.52) * mm});
            skLineSegment(sketch, "E2951", {"start": v(-0.17, -12.52) * mm, "end": v(-0.26, -12.52) * mm});
            skLineSegment(sketch, "E2952", {"start": v(43.04, 8) * mm, "end": v(43.5, 8.22) * mm});
            skLineSegment(sketch, "E2953", {"start": v(29.74, 2.15) * mm, "end": v(29.59, 2.08) * mm});
            skLineSegment(sketch, "E2954", {"start": v(29.59, 2.08) * mm, "end": v(29.44, 2) * mm});
            skLineSegment(sketch, "E2955", {"start": v(29.44, 2) * mm, "end": v(29.29, 1.94) * mm});
            skLineSegment(sketch, "E2956", {"start": v(29.29, 1.94) * mm, "end": v(29.14, 1.86) * mm});
            skLineSegment(sketch, "E2957", {"start": v(29.14, 1.86) * mm, "end": v(28.98, 1.78) * mm});
            skLineSegment(sketch, "E2958", {"start": v(28.98, 1.78) * mm, "end": v(28.83, 1.7) * mm});
            skLineSegment(sketch, "E2959", {"start": v(28.83, 1.7) * mm, "end": v(28.68, 1.6) * mm});
            skLineSegment(sketch, "E2960", {"start": v(28.68, 1.6) * mm, "end": v(28.52, 1.5) * mm});
            skLineSegment(sketch, "E2961", {"start": v(28.52, 1.5) * mm, "end": v(28.37, 1.41) * mm});
            skLineSegment(sketch, "E2962", {"start": v(28.37, 1.41) * mm, "end": v(28.21, 1.31) * mm});
            skLineSegment(sketch, "E2963", {"start": v(28.21, 1.31) * mm, "end": v(28.05, 1.2) * mm});
            skLineSegment(sketch, "E2964", {"start": v(28.05, 1.2) * mm, "end": v(27.9, 1.1) * mm});
            skLineSegment(sketch, "E2965", {"start": v(27.9, 1.1) * mm, "end": v(27.74, 1) * mm});
            skLineSegment(sketch, "E2966", {"start": v(27.74, 1) * mm, "end": v(27.58, 0.87) * mm});
            skLineSegment(sketch, "E2967", {"start": v(27.58, 0.87) * mm, "end": v(27.42, 0.76) * mm});
            skLineSegment(sketch, "E2968", {"start": v(27.42, 0.76) * mm, "end": v(27.26, 0.63) * mm});
            skLineSegment(sketch, "E2969", {"start": v(27.26, 0.63) * mm, "end": v(27.1, 0.5) * mm});
            skLineSegment(sketch, "E2970", {"start": v(27.1, 0.5) * mm, "end": v(26.95, 0.38) * mm});
            skLineSegment(sketch, "E2971", {"start": v(26.95, 0.38) * mm, "end": v(26.79, 0.24) * mm});
            skLineSegment(sketch, "E2972", {"start": v(26.79, 0.24) * mm, "end": v(26.74, 0.2) * mm});
            skLineSegment(sketch, "E2973", {"start": v(-29.88, 8.03) * mm, "end": v(-29.75, 8.04) * mm});
            skLineSegment(sketch, "E2974", {"start": v(-29.75, 8.04) * mm, "end": v(-28.94, 8.12) * mm});
            skLineSegment(sketch, "E2975", {"start": v(-28.94, 8.12) * mm, "end": v(-28.59, 8.15) * mm});
            skLineSegment(sketch, "E2976", {"start": v(-28.59, 8.15) * mm, "end": v(-28.42, 8.16) * mm});
            skLineSegment(sketch, "E2977", {"start": v(-28.42, 8.16) * mm, "end": v(-28.26, 8.18) * mm});
            skLineSegment(sketch, "E2978", {"start": v(-28.26, 8.18) * mm, "end": v(-28.1, 8.19) * mm});
            skLineSegment(sketch, "E2979", {"start": v(-28.1, 8.19) * mm, "end": v(-27.95, 8.2) * mm});
            skLineSegment(sketch, "E2980", {"start": v(-27.95, 8.2) * mm, "end": v(-27.8, 8.2) * mm});
            skLineSegment(sketch, "E2981", {"start": v(-27.8, 8.2) * mm, "end": v(-27.67, 8.21) * mm});
            skLineSegment(sketch, "E2982", {"start": v(45.28, 12.15) * mm, "end": v(45.25, 12.15) * mm});
            skLineSegment(sketch, "E2983", {"start": v(45.25, 12.15) * mm, "end": v(45.23, 12.15) * mm});
            skLineSegment(sketch, "E2984", {"start": v(45.23, 12.15) * mm, "end": v(45.2, 12.15) * mm});
            skLineSegment(sketch, "E2985", {"start": v(45.2, 12.15) * mm, "end": v(45.18, 12.14) * mm});
            skLineSegment(sketch, "E2986", {"start": v(45.18, 12.14) * mm, "end": v(45.15, 12.14) * mm});
            skLineSegment(sketch, "E2987", {"start": v(45.15, 12.14) * mm, "end": v(45.12, 12.14) * mm});
            skLineSegment(sketch, "E2988", {"start": v(45.12, 12.14) * mm, "end": v(45.1, 12.13) * mm});
            skLineSegment(sketch, "E2989", {"start": v(45.1, 12.13) * mm, "end": v(45.06, 12.12) * mm});
            skLineSegment(sketch, "E2990", {"start": v(45.06, 12.12) * mm, "end": v(45.03, 12.12) * mm});
            skLineSegment(sketch, "E2991", {"start": v(45.03, 12.12) * mm, "end": v(45, 12.1) * mm});
            skLineSegment(sketch, "E2992", {"start": v(45, 12.1) * mm, "end": v(44.97, 12.1) * mm});
            skLineSegment(sketch, "E2993", {"start": v(44.97, 12.1) * mm, "end": v(44.94, 12.09) * mm});
            skLineSegment(sketch, "E2994", {"start": v(44.94, 12.09) * mm, "end": v(44.9, 12.07) * mm});
            skLineSegment(sketch, "E2995", {"start": v(44.9, 12.07) * mm, "end": v(44.86, 12.06) * mm});
            skLineSegment(sketch, "E2996", {"start": v(44.86, 12.06) * mm, "end": v(44.82, 12.04) * mm});
            skLineSegment(sketch, "E2997", {"start": v(44.82, 12.04) * mm, "end": v(44.78, 12.03) * mm});
            skLineSegment(sketch, "E2998", {"start": v(44.78, 12.03) * mm, "end": v(44.74, 12) * mm});
            skLineSegment(sketch, "E2999", {"start": v(44.74, 12) * mm, "end": v(44.7, 11.99) * mm});
            skLineSegment(sketch, "E3000", {"start": v(44.7, 11.99) * mm, "end": v(44.65, 11.97) * mm});
            skLineSegment(sketch, "E3001", {"start": v(44.65, 11.97) * mm, "end": v(44.6, 11.94) * mm});
            skLineSegment(sketch, "E3002", {"start": v(44.6, 11.94) * mm, "end": v(44.56, 11.92) * mm});
            skLineSegment(sketch, "E3003", {"start": v(44.56, 11.92) * mm, "end": v(44.5, 11.89) * mm});
            skLineSegment(sketch, "E3004", {"start": v(44.5, 11.89) * mm, "end": v(44.45, 11.86) * mm});
            skLineSegment(sketch, "E3005", {"start": v(44.45, 11.86) * mm, "end": v(44.39, 11.83) * mm});
            skLineSegment(sketch, "E3006", {"start": v(44.39, 11.83) * mm, "end": v(44.34, 11.8) * mm});
            skLineSegment(sketch, "E3007", {"start": v(-28.17, 13.08) * mm, "end": v(-28.53, 13.08) * mm});
            skLineSegment(sketch, "E3008", {"start": v(-28.53, 13.08) * mm, "end": v(-28.9, 13.08) * mm});
            skLineSegment(sketch, "E3009", {"start": v(-28.9, 13.08) * mm, "end": v(-29.26, 13.07) * mm});
            skLineSegment(sketch, "E3010", {"start": v(-29.26, 13.07) * mm, "end": v(-29.63, 13.05) * mm});
            skLineSegment(sketch, "E3011", {"start": v(-29.63, 13.05) * mm, "end": v(-30, 13.03) * mm});
            skLineSegment(sketch, "E3012", {"start": v(-30, 13.03) * mm, "end": v(-30.38, 13) * mm});
            skLineSegment(sketch, "E3013", {"start": v(-30.38, 13) * mm, "end": v(-30.76, 12.98) * mm});
            skLineSegment(sketch, "E3014", {"start": v(-30.76, 12.98) * mm, "end": v(-31.14, 12.95) * mm});
            skLineSegment(sketch, "E3015", {"start": v(-31.14, 12.95) * mm, "end": v(-31.53, 12.91) * mm});
            skLineSegment(sketch, "E3016", {"start": v(-31.53, 12.91) * mm, "end": v(-31.92, 12.87) * mm});
            skLineSegment(sketch, "E3017", {"start": v(-31.92, 12.87) * mm, "end": v(-32.31, 12.83) * mm});
            skLineSegment(sketch, "E3018", {"start": v(-32.31, 12.83) * mm, "end": v(-32.71, 12.78) * mm});
            skLineSegment(sketch, "E3019", {"start": v(-32.71, 12.78) * mm, "end": v(-33.11, 12.72) * mm});
            skLineSegment(sketch, "E3020", {"start": v(-33.11, 12.72) * mm, "end": v(-33.39, 12.68) * mm});
            skLineSegment(sketch, "E3021", {"start": v(23.62, -10.92) * mm, "end": v(23.68, -11) * mm});
            skLineSegment(sketch, "E3022", {"start": v(23.68, -11) * mm, "end": v(23.74, -11.08) * mm});
            skLineSegment(sketch, "E3023", {"start": v(23.74, -11.08) * mm, "end": v(23.8, -11.15) * mm});
            skLineSegment(sketch, "E3024", {"start": v(23.8, -11.15) * mm, "end": v(23.87, -11.22) * mm});
            skLineSegment(sketch, "E3025", {"start": v(23.87, -11.22) * mm, "end": v(23.93, -11.29) * mm});
            skLineSegment(sketch, "E3026", {"start": v(23.93, -11.29) * mm, "end": v(24, -11.35) * mm});
            skLineSegment(sketch, "E3027", {"start": v(24, -11.35) * mm, "end": v(24.06, -11.42) * mm});
            skLineSegment(sketch, "E3028", {"start": v(24.06, -11.42) * mm, "end": v(24.13, -11.48) * mm});
            skLineSegment(sketch, "E3029", {"start": v(24.13, -11.48) * mm, "end": v(24.2, -11.54) * mm});
            skLineSegment(sketch, "E3030", {"start": v(24.2, -11.54) * mm, "end": v(24.27, -11.6) * mm});
            skLineSegment(sketch, "E3031", {"start": v(24.27, -11.6) * mm, "end": v(24.34, -11.65) * mm});
            skLineSegment(sketch, "E3032", {"start": v(24.34, -11.65) * mm, "end": v(24.41, -11.7) * mm});
            skLineSegment(sketch, "E3033", {"start": v(24.41, -11.7) * mm, "end": v(24.49, -11.75) * mm});
            skLineSegment(sketch, "E3034", {"start": v(24.49, -11.75) * mm, "end": v(24.56, -11.8) * mm});
            skLineSegment(sketch, "E3035", {"start": v(24.56, -11.8) * mm, "end": v(24.64, -11.84) * mm});
            skLineSegment(sketch, "E3036", {"start": v(24.64, -11.84) * mm, "end": v(24.71, -11.88) * mm});
            skLineSegment(sketch, "E3037", {"start": v(24.71, -11.88) * mm, "end": v(24.8, -11.93) * mm});
            skLineSegment(sketch, "E3038", {"start": v(24.8, -11.93) * mm, "end": v(24.87, -11.96) * mm});
            skLineSegment(sketch, "E3039", {"start": v(24.87, -11.96) * mm, "end": v(24.95, -12) * mm});
            skLineSegment(sketch, "E3040", {"start": v(24.95, -12) * mm, "end": v(25.03, -12.03) * mm});
            skLineSegment(sketch, "E3041", {"start": v(25.03, -12.03) * mm, "end": v(25.12, -12.07) * mm});
            skLineSegment(sketch, "E3042", {"start": v(25.12, -12.07) * mm, "end": v(25.2, -12.1) * mm});
            skLineSegment(sketch, "E3043", {"start": v(25.2, -12.1) * mm, "end": v(25.29, -12.12) * mm});
            skLineSegment(sketch, "E3044", {"start": v(25.29, -12.12) * mm, "end": v(25.38, -12.15) * mm});
            skLineSegment(sketch, "E3045", {"start": v(25.38, -12.15) * mm, "end": v(25.46, -12.17) * mm});
            skLineSegment(sketch, "E3046", {"start": v(25.46, -12.17) * mm, "end": v(25.56, -12.2) * mm});
            skLineSegment(sketch, "E3047", {"start": v(25.56, -12.2) * mm, "end": v(25.65, -12.21) * mm});
            skLineSegment(sketch, "E3048", {"start": v(25.65, -12.21) * mm, "end": v(25.74, -12.23) * mm});
            skLineSegment(sketch, "E3049", {"start": v(25.74, -12.23) * mm, "end": v(25.84, -12.24) * mm});
            skLineSegment(sketch, "E3050", {"start": v(25.84, -12.24) * mm, "end": v(25.93, -12.26) * mm});
            skLineSegment(sketch, "E3051", {"start": v(25.93, -12.26) * mm, "end": v(26.03, -12.27) * mm});
            skLineSegment(sketch, "E3052", {"start": v(26.03, -12.27) * mm, "end": v(26.13, -12.28) * mm});
            skLineSegment(sketch, "E3053", {"start": v(26.13, -12.28) * mm, "end": v(26.24, -12.28) * mm});
            skLineSegment(sketch, "E3054", {"start": v(26.24, -12.28) * mm, "end": v(26.34, -12.28) * mm});
            skLineSegment(sketch, "E3055", {"start": v(26.34, -12.28) * mm, "end": v(26.42, -12.28) * mm});
            skLineSegment(sketch, "E3056", {"start": v(14.41, -10.08) * mm, "end": v(14.41, -10.16) * mm});
            skLineSegment(sketch, "E3057", {"start": v(14.41, -10.16) * mm, "end": v(14.41, -10.24) * mm});
            skLineSegment(sketch, "E3058", {"start": v(14.41, -10.24) * mm, "end": v(14.42, -10.33) * mm});
            skLineSegment(sketch, "E3059", {"start": v(14.42, -10.33) * mm, "end": v(14.42, -10.4) * mm});
            skLineSegment(sketch, "E3060", {"start": v(14.42, -10.4) * mm, "end": v(14.43, -10.48) * mm});
            skLineSegment(sketch, "E3061", {"start": v(14.43, -10.48) * mm, "end": v(14.44, -10.56) * mm});
            skLineSegment(sketch, "E3062", {"start": v(14.44, -10.56) * mm, "end": v(14.45, -10.63) * mm});
            skLineSegment(sketch, "E3063", {"start": v(14.45, -10.63) * mm, "end": v(14.46, -10.7) * mm});
            skLineSegment(sketch, "E3064", {"start": v(14.46, -10.7) * mm, "end": v(14.48, -10.76) * mm});
            skLineSegment(sketch, "E3065", {"start": v(14.48, -10.76) * mm, "end": v(14.5, -10.83) * mm});
            skLineSegment(sketch, "E3066", {"start": v(14.5, -10.83) * mm, "end": v(14.5, -10.89) * mm});
            skLineSegment(sketch, "E3067", {"start": v(14.5, -10.89) * mm, "end": v(14.53, -10.95) * mm});
            skLineSegment(sketch, "E3068", {"start": v(14.53, -10.95) * mm, "end": v(14.55, -11) * mm});
            skLineSegment(sketch, "E3069", {"start": v(14.55, -11) * mm, "end": v(14.57, -11.06) * mm});
            skLineSegment(sketch, "E3070", {"start": v(14.57, -11.06) * mm, "end": v(14.59, -11.1) * mm});
            skLineSegment(sketch, "E3071", {"start": v(14.59, -11.1) * mm, "end": v(14.6, -11.16) * mm});
            skLineSegment(sketch, "E3072", {"start": v(14.6, -11.16) * mm, "end": v(14.63, -11.2) * mm});
            skLineSegment(sketch, "E3073", {"start": v(14.63, -11.2) * mm, "end": v(14.66, -11.25) * mm});
            skLineSegment(sketch, "E3074", {"start": v(14.66, -11.25) * mm, "end": v(14.68, -11.3) * mm});
            skLineSegment(sketch, "E3075", {"start": v(14.68, -11.3) * mm, "end": v(14.71, -11.34) * mm});
            skLineSegment(sketch, "E3076", {"start": v(14.71, -11.34) * mm, "end": v(14.74, -11.38) * mm});
            skLineSegment(sketch, "E3077", {"start": v(14.74, -11.38) * mm, "end": v(14.77, -11.42) * mm});
            skLineSegment(sketch, "E3078", {"start": v(14.77, -11.42) * mm, "end": v(14.8, -11.46) * mm});
            skLineSegment(sketch, "E3079", {"start": v(14.8, -11.46) * mm, "end": v(14.83, -11.5) * mm});
            skLineSegment(sketch, "E3080", {"start": v(14.83, -11.5) * mm, "end": v(14.86, -11.52) * mm});
            skLineSegment(sketch, "E3081", {"start": v(14.86, -11.52) * mm, "end": v(14.9, -11.56) * mm});
            skLineSegment(sketch, "E3082", {"start": v(14.9, -11.56) * mm, "end": v(14.91, -11.57) * mm});
            skLineSegment(sketch, "E3083", {"start": v(14.91, -11.57) * mm, "end": v(14.93, -11.59) * mm});
            skLineSegment(sketch, "E3084", {"start": v(14.93, -11.59) * mm, "end": v(14.97, -11.62) * mm});
            skLineSegment(sketch, "E3085", {"start": v(14.97, -11.62) * mm, "end": v(15, -11.65) * mm});
            skLineSegment(sketch, "E3086", {"start": v(15, -11.65) * mm, "end": v(15.04, -11.67) * mm});
            skLineSegment(sketch, "E3087", {"start": v(15.04, -11.67) * mm, "end": v(15.09, -11.7) * mm});
            skLineSegment(sketch, "E3088", {"start": v(15.09, -11.7) * mm, "end": v(15.13, -11.72) * mm});
            skLineSegment(sketch, "E3089", {"start": v(15.13, -11.72) * mm, "end": v(15.17, -11.75) * mm});
            skLineSegment(sketch, "E3090", {"start": v(15.17, -11.75) * mm, "end": v(15.21, -11.77) * mm});
            skLineSegment(sketch, "E3091", {"start": v(15.21, -11.77) * mm, "end": v(15.26, -11.79) * mm});
            skLineSegment(sketch, "E3092", {"start": v(15.26, -11.79) * mm, "end": v(15.3, -11.8) * mm});
            skLineSegment(sketch, "E3093", {"start": v(15.3, -11.8) * mm, "end": v(15.36, -11.82) * mm});
            skLineSegment(sketch, "E3094", {"start": v(15.36, -11.82) * mm, "end": v(15.4, -11.84) * mm});
            skLineSegment(sketch, "E3095", {"start": v(15.4, -11.84) * mm, "end": v(15.46, -11.85) * mm});
            skLineSegment(sketch, "E3096", {"start": v(15.46, -11.85) * mm, "end": v(15.52, -11.86) * mm});
            skLineSegment(sketch, "E3097", {"start": v(15.52, -11.86) * mm, "end": v(15.57, -11.88) * mm});
            skLineSegment(sketch, "E3098", {"start": v(15.57, -11.88) * mm, "end": v(15.63, -11.88) * mm});
            skLineSegment(sketch, "E3099", {"start": v(15.63, -11.88) * mm, "end": v(15.7, -11.9) * mm});
            skLineSegment(sketch, "E3100", {"start": v(15.7, -11.9) * mm, "end": v(15.76, -11.9) * mm});
            skLineSegment(sketch, "E3101", {"start": v(15.76, -11.9) * mm, "end": v(15.82, -11.9) * mm});
            skLineSegment(sketch, "E3102", {"start": v(15.82, -11.9) * mm, "end": v(15.89, -11.9) * mm});
            skLineSegment(sketch, "E3103", {"start": v(15.89, -11.9) * mm, "end": v(15.96, -11.9) * mm});
            skLineSegment(sketch, "E3104", {"start": v(23.07, 12.1) * mm, "end": v(23.08, 12.11) * mm});
            skLineSegment(sketch, "E3105", {"start": v(23.08, 12.11) * mm, "end": v(23.15, 12.23) * mm});
            skLineSegment(sketch, "E3106", {"start": v(23.15, 12.23) * mm, "end": v(23.21, 12.34) * mm});
            skLineSegment(sketch, "E3107", {"start": v(23.21, 12.34) * mm, "end": v(23.27, 12.44) * mm});
            skLineSegment(sketch, "E3108", {"start": v(23.27, 12.44) * mm, "end": v(23.33, 12.54) * mm});
            skLineSegment(sketch, "E3109", {"start": v(23.33, 12.54) * mm, "end": v(23.38, 12.64) * mm});
            skLineSegment(sketch, "E3110", {"start": v(23.38, 12.64) * mm, "end": v(23.42, 12.73) * mm});
            skLineSegment(sketch, "E3111", {"start": v(23.42, 12.73) * mm, "end": v(23.47, 12.81) * mm});
            skLineSegment(sketch, "E3112", {"start": v(23.47, 12.81) * mm, "end": v(23.5, 12.9) * mm});
            skLineSegment(sketch, "E3113", {"start": v(23.5, 12.9) * mm, "end": v(23.54, 12.97) * mm});
            skLineSegment(sketch, "E3114", {"start": v(23.54, 12.97) * mm, "end": v(23.57, 13.05) * mm});
            skLineSegment(sketch, "E3115", {"start": v(23.57, 13.05) * mm, "end": v(23.6, 13.12) * mm});
            skLineSegment(sketch, "E3116", {"start": v(23.6, 13.12) * mm, "end": v(23.63, 13.18) * mm});
            skLineSegment(sketch, "E3117", {"start": v(23.63, 13.18) * mm, "end": v(23.65, 13.25) * mm});
            skLineSegment(sketch, "E3118", {"start": v(23.65, 13.25) * mm, "end": v(23.67, 13.3) * mm});
            skLineSegment(sketch, "E3119", {"start": v(23.67, 13.3) * mm, "end": v(23.7, 13.36) * mm});
            skLineSegment(sketch, "E3120", {"start": v(23.7, 13.36) * mm, "end": v(23.7, 13.41) * mm});
            skLineSegment(sketch, "E3121", {"start": v(23.7, 13.41) * mm, "end": v(23.72, 13.46) * mm});
            skLineSegment(sketch, "E3122", {"start": v(23.72, 13.46) * mm, "end": v(23.73, 13.5) * mm});
            skLineSegment(sketch, "E3123", {"start": v(23.73, 13.5) * mm, "end": v(23.74, 13.55) * mm});
            skLineSegment(sketch, "E3124", {"start": v(23.74, 13.55) * mm, "end": v(23.75, 13.6) * mm});
            skLineSegment(sketch, "E3125", {"start": v(23.75, 13.6) * mm, "end": v(23.75, 13.64) * mm});
            skLineSegment(sketch, "E3126", {"start": v(23.75, 13.64) * mm, "end": v(23.76, 13.67) * mm});
            skLineSegment(sketch, "E3127", {"start": v(23.76, 13.67) * mm, "end": v(23.76, 13.7) * mm});
            skLineSegment(sketch, "E3128", {"start": v(23.76, 13.7) * mm, "end": v(23.76, 13.74) * mm});
            skLineSegment(sketch, "E3129", {"start": v(18.14, -2.12) * mm, "end": v(17.98, -2.35) * mm});
            skLineSegment(sketch, "E3130", {"start": v(17.98, -2.35) * mm, "end": v(17.7, -2.77) * mm});
            skLineSegment(sketch, "E3131", {"start": v(17.7, -2.77) * mm, "end": v(17.44, -3.16) * mm});
            skLineSegment(sketch, "E3132", {"start": v(17.44, -3.16) * mm, "end": v(17.18, -3.55) * mm});
            skLineSegment(sketch, "E3133", {"start": v(17.18, -3.55) * mm, "end": v(16.94, -3.92) * mm});
            skLineSegment(sketch, "E3134", {"start": v(16.94, -3.92) * mm, "end": v(16.72, -4.28) * mm});
            skLineSegment(sketch, "E3135", {"start": v(16.72, -4.28) * mm, "end": v(16.5, -4.62) * mm});
            skLineSegment(sketch, "E3136", {"start": v(16.5, -4.62) * mm, "end": v(16.3, -4.95) * mm});
            skLineSegment(sketch, "E3137", {"start": v(16.3, -4.95) * mm, "end": v(16.12, -5.27) * mm});
            skLineSegment(sketch, "E3138", {"start": v(16.12, -5.27) * mm, "end": v(15.95, -5.58) * mm});
            skLineSegment(sketch, "E3139", {"start": v(15.95, -5.58) * mm, "end": v(15.79, -5.87) * mm});
            skLineSegment(sketch, "E3140", {"start": v(15.79, -5.87) * mm, "end": v(15.64, -6.16) * mm});
            skLineSegment(sketch, "E3141", {"start": v(15.64, -6.16) * mm, "end": v(15.5, -6.43) * mm});
            skLineSegment(sketch, "E3142", {"start": v(15.5, -6.43) * mm, "end": v(15.36, -6.69) * mm});
            skLineSegment(sketch, "E3143", {"start": v(11.3, -9.08) * mm, "end": v(11.78, -8.48) * mm});
            skLineSegment(sketch, "E3144", {"start": v(11.78, -8.48) * mm, "end": v(12.02, -8.18) * mm});
            skLineSegment(sketch, "E3145", {"start": v(12.02, -8.18) * mm, "end": v(12.26, -7.88) * mm});
            skLineSegment(sketch, "E3146", {"start": v(12.26, -7.88) * mm, "end": v(12.5, -7.58) * mm});
            skLineSegment(sketch, "E3147", {"start": v(12.5, -7.58) * mm, "end": v(12.75, -7.28) * mm});
            skLineSegment(sketch, "E3148", {"start": v(12.75, -7.28) * mm, "end": v(13, -6.98) * mm});
            skLineSegment(sketch, "E3149", {"start": v(13, -6.98) * mm, "end": v(13.25, -6.69) * mm});
            skLineSegment(sketch, "E3150", {"start": v(13.25, -6.69) * mm, "end": v(13.5, -6.4) * mm});
            skLineSegment(sketch, "E3151", {"start": v(13.5, -6.4) * mm, "end": v(13.76, -6.1) * mm});
            skLineSegment(sketch, "E3152", {"start": v(14.38, -5.4) * mm, "end": v(15.04, -4.62) * mm});
            skLineSegment(sketch, "E3153", {"start": v(15.04, -4.62) * mm, "end": v(15.11, -4.54) * mm});
            skLineSegment(sketch, "E3154", {"start": v(15.11, -4.54) * mm, "end": v(15.18, -4.45) * mm});
            skLineSegment(sketch, "E3155", {"start": v(15.18, -4.45) * mm, "end": v(15.26, -4.37) * mm});
            skLineSegment(sketch, "E3156", {"start": v(15.26, -4.37) * mm, "end": v(15.34, -4.29) * mm});
            skLineSegment(sketch, "E3157", {"start": v(15.34, -4.29) * mm, "end": v(15.42, -4.2) * mm});
            skLineSegment(sketch, "E3158", {"start": v(15.42, -4.2) * mm, "end": v(15.5, -4.12) * mm});
            skLineSegment(sketch, "E3159", {"start": v(15.5, -4.12) * mm, "end": v(15.6, -4.03) * mm});
            skLineSegment(sketch, "E3160", {"start": v(15.6, -4.03) * mm, "end": v(15.69, -3.94) * mm});
            skLineSegment(sketch, "E3161", {"start": v(15.69, -3.94) * mm, "end": v(15.79, -3.85) * mm});
            skLineSegment(sketch, "E3162", {"start": v(15.79, -3.85) * mm, "end": v(15.89, -3.75) * mm});
            skLineSegment(sketch, "E3163", {"start": v(15.89, -3.75) * mm, "end": v(16, -3.66) * mm});
            skLineSegment(sketch, "E3164", {"start": v(16, -3.66) * mm, "end": v(16.11, -3.56) * mm});
            skLineSegment(sketch, "E3165", {"start": v(16.11, -3.56) * mm, "end": v(16.23, -3.45) * mm});
            skLineSegment(sketch, "E3166", {"start": v(16.23, -3.45) * mm, "end": v(16.36, -3.34) * mm});
            skLineSegment(sketch, "E3167", {"start": v(16.36, -3.34) * mm, "end": v(16.45, -3.27) * mm});
            skLineSegment(sketch, "E3168", {"start": v(13.76, -6.1) * mm, "end": v(14.1, -5.71) * mm});
            skLineSegment(sketch, "E3169", {"start": v(14.1, -5.71) * mm, "end": v(14.19, -5.61) * mm});
            skLineSegment(sketch, "E3170", {"start": v(14.19, -5.61) * mm, "end": v(14.38, -5.4) * mm});
            skLineSegment(sketch, "E3171", {"start": v(9.93, -10.76) * mm, "end": v(10.01, -10.67) * mm});
            skLineSegment(sketch, "E3172", {"start": v(10.01, -10.67) * mm, "end": v(10.11, -10.55) * mm});
            skLineSegment(sketch, "E3173", {"start": v(10.11, -10.55) * mm, "end": v(10.13, -10.54) * mm});
            skLineSegment(sketch, "E3174", {"start": v(10.13, -10.54) * mm, "end": v(10.25, -10.4) * mm});
            skLineSegment(sketch, "E3175", {"start": v(10.25, -10.4) * mm, "end": v(10.38, -10.23) * mm});
            skLineSegment(sketch, "E3176", {"start": v(10.38, -10.23) * mm, "end": v(10.54, -10.04) * mm});
            skLineSegment(sketch, "E3177", {"start": v(10.54, -10.04) * mm, "end": v(10.7, -9.83) * mm});
            skLineSegment(sketch, "E3178", {"start": v(10.7, -9.83) * mm, "end": v(10.89, -9.6) * mm});
            skLineSegment(sketch, "E3179", {"start": v(10.89, -9.6) * mm, "end": v(11.3, -9.08) * mm});
            skLineSegment(sketch, "E3180", {"start": v(30.08, 0.15) * mm, "end": v(30.14, 0.2) * mm});
            skLineSegment(sketch, "E3181", {"start": v(30.14, 0.2) * mm, "end": v(30.22, 0.23) * mm});
            skLineSegment(sketch, "E3182", {"start": v(30.22, 0.23) * mm, "end": v(30.3, 0.28) * mm});
            skLineSegment(sketch, "E3183", {"start": v(30.3, 0.28) * mm, "end": v(30.37, 0.31) * mm});
            skLineSegment(sketch, "E3184", {"start": v(30.37, 0.31) * mm, "end": v(30.44, 0.35) * mm});
            skLineSegment(sketch, "E3185", {"start": v(30.44, 0.35) * mm, "end": v(30.5, 0.38) * mm});
            skLineSegment(sketch, "E3186", {"start": v(30.5, 0.38) * mm, "end": v(30.57, 0.41) * mm});
            skLineSegment(sketch, "E3187", {"start": v(30.57, 0.41) * mm, "end": v(30.63, 0.44) * mm});
            skLineSegment(sketch, "E3188", {"start": v(30.63, 0.44) * mm, "end": v(30.68, 0.46) * mm});
            skLineSegment(sketch, "E3189", {"start": v(30.68, 0.46) * mm, "end": v(30.74, 0.49) * mm});
            skLineSegment(sketch, "E3190", {"start": v(30.74, 0.49) * mm, "end": v(30.79, 0.5) * mm});
            skLineSegment(sketch, "E3191", {"start": v(30.79, 0.5) * mm, "end": v(30.84, 0.53) * mm});
            skLineSegment(sketch, "E3192", {"start": v(30.84, 0.53) * mm, "end": v(30.88, 0.54) * mm});
            skLineSegment(sketch, "E3193", {"start": v(30.88, 0.54) * mm, "end": v(30.93, 0.56) * mm});
            skLineSegment(sketch, "E3194", {"start": v(30.93, 0.56) * mm, "end": v(30.97, 0.57) * mm});
            skLineSegment(sketch, "E3195", {"start": v(30.97, 0.57) * mm, "end": v(31, 0.58) * mm});
            skLineSegment(sketch, "E3196", {"start": v(31, 0.58) * mm, "end": v(31.04, 0.6) * mm});
            skLineSegment(sketch, "E3197", {"start": v(31.04, 0.6) * mm, "end": v(31.08, 0.6) * mm});
            skLineSegment(sketch, "E3198", {"start": v(31.08, 0.6) * mm, "end": v(31.1, 0.6) * mm});
            skLineSegment(sketch, "E3199", {"start": v(31.1, 0.6) * mm, "end": v(31.14, 0.6) * mm});
            skLineSegment(sketch, "E3200", {"start": v(31.14, 0.6) * mm, "end": v(31.17, 0.61) * mm});
            skLineSegment(sketch, "E3201", {"start": v(31.17, 0.61) * mm, "end": v(31.2, 0.62) * mm});
            skLineSegment(sketch, "E3202", {"start": v(31.2, 0.62) * mm, "end": v(31.22, 0.62) * mm});
            skLineSegment(sketch, "E3203", {"start": v(31.22, 0.62) * mm, "end": v(31.24, 0.62) * mm});
            skLineSegment(sketch, "E3204", {"start": v(25.92, -6.21) * mm, "end": v(26, -6.18) * mm});
            skLineSegment(sketch, "E3205", {"start": v(26, -6.18) * mm, "end": v(26.4, -6.01) * mm});
            skLineSegment(sketch, "E3206", {"start": v(26.4, -6.01) * mm, "end": v(26.78, -5.85) * mm});
            skLineSegment(sketch, "E3207", {"start": v(26.78, -5.85) * mm, "end": v(27.15, -5.7) * mm});
            skLineSegment(sketch, "E3208", {"start": v(27.15, -5.7) * mm, "end": v(27.5, -5.53) * mm});
            skLineSegment(sketch, "E3209", {"start": v(27.5, -5.53) * mm, "end": v(27.85, -5.38) * mm});
            skLineSegment(sketch, "E3210", {"start": v(27.85, -5.38) * mm, "end": v(28.18, -5.22) * mm});
            skLineSegment(sketch, "E3211", {"start": v(28.18, -5.22) * mm, "end": v(28.5, -5.07) * mm});
            skLineSegment(sketch, "E3212", {"start": v(28.5, -5.07) * mm, "end": v(28.8, -4.91) * mm});
            skLineSegment(sketch, "E3213", {"start": v(28.8, -4.91) * mm, "end": v(29.09, -4.76) * mm});
            skLineSegment(sketch, "E3214", {"start": v(29.09, -4.76) * mm, "end": v(29.37, -4.6) * mm});
            skLineSegment(sketch, "E3215", {"start": v(29.37, -4.6) * mm, "end": v(29.64, -4.46) * mm});
            skLineSegment(sketch, "E3216", {"start": v(29.64, -4.46) * mm, "end": v(29.9, -4.3) * mm});
            skLineSegment(sketch, "E3217", {"start": v(29.9, -4.3) * mm, "end": v(30.16, -4.16) * mm});
            skLineSegment(sketch, "E3218", {"start": v(30.16, -4.16) * mm, "end": v(30.4, -4.01) * mm});
            skLineSegment(sketch, "E3219", {"start": v(30.4, -4.01) * mm, "end": v(30.63, -3.87) * mm});
            skLineSegment(sketch, "E3220", {"start": v(-36.4, 7) * mm, "end": v(-35.9, 7.12) * mm});
            skLineSegment(sketch, "E3221", {"start": v(-35.9, 7.12) * mm, "end": v(-35.65, 7.17) * mm});
            skLineSegment(sketch, "E3222", {"start": v(-35.65, 7.17) * mm, "end": v(-35.35, 7.22) * mm});
            skLineSegment(sketch, "E3223", {"start": v(-35.35, 7.22) * mm, "end": v(-35.33, 7.23) * mm});
            skLineSegment(sketch, "E3224", {"start": v(-35.33, 7.23) * mm, "end": v(-34.99, 7.29) * mm});
            skLineSegment(sketch, "E3225", {"start": v(-34.99, 7.29) * mm, "end": v(-34.6, 7.35) * mm});
            skLineSegment(sketch, "E3226", {"start": v(-34.6, 7.35) * mm, "end": v(-34.2, 7.42) * mm});
            skLineSegment(sketch, "E3227", {"start": v(-34.2, 7.42) * mm, "end": v(-33.74, 7.5) * mm});
            skLineSegment(sketch, "E3228", {"start": v(-33.74, 7.5) * mm, "end": v(-33.25, 7.57) * mm});
            skLineSegment(sketch, "E3229", {"start": v(-33.25, 7.57) * mm, "end": v(-32.72, 7.64) * mm});
            skLineSegment(sketch, "E3230", {"start": v(-32.72, 7.64) * mm, "end": v(-32.15, 7.72) * mm});
            skLineSegment(sketch, "E3231", {"start": v(-32.15, 7.72) * mm, "end": v(-31.54, 7.8) * mm});
            skLineSegment(sketch, "E3232", {"start": v(-36.87, 6.91) * mm, "end": v(-36.4, 7) * mm});
            skLineSegment(sketch, "E3233", {"start": v(-38.25, 6.64) * mm, "end": v(-37.9, 6.7) * mm});
            skLineSegment(sketch, "E3234", {"start": v(-37.9, 6.7) * mm, "end": v(-36.87, 6.91) * mm});
            skLineSegment(sketch, "E3235", {"start": v(22.21, 14.5) * mm, "end": v(22.18, 14.5) * mm});
            skLineSegment(sketch, "E3236", {"start": v(22.18, 14.5) * mm, "end": v(22.15, 14.5) * mm});
            skLineSegment(sketch, "E3237", {"start": v(22.15, 14.5) * mm, "end": v(22.12, 14.5) * mm});
            skLineSegment(sketch, "E3238", {"start": v(22.12, 14.5) * mm, "end": v(22.09, 14.5) * mm});
            skLineSegment(sketch, "E3239", {"start": v(22.09, 14.5) * mm, "end": v(22.05, 14.49) * mm});
            skLineSegment(sketch, "E3240", {"start": v(22.05, 14.49) * mm, "end": v(22, 14.48) * mm});
            skLineSegment(sketch, "E3241", {"start": v(22, 14.48) * mm, "end": v(21.97, 14.46) * mm});
            skLineSegment(sketch, "E3242", {"start": v(21.97, 14.46) * mm, "end": v(21.92, 14.44) * mm});
            skLineSegment(sketch, "E3243", {"start": v(21.92, 14.44) * mm, "end": v(21.87, 14.42) * mm});
            skLineSegment(sketch, "E3244", {"start": v(21.87, 14.42) * mm, "end": v(21.82, 14.4) * mm});
            skLineSegment(sketch, "E3245", {"start": v(21.82, 14.4) * mm, "end": v(21.76, 14.37) * mm});
            skLineSegment(sketch, "E3246", {"start": v(21.76, 14.37) * mm, "end": v(21.7, 14.33) * mm});
            skLineSegment(sketch, "E3247", {"start": v(21.7, 14.33) * mm, "end": v(21.64, 14.3) * mm});
            skLineSegment(sketch, "E3248", {"start": v(21.64, 14.3) * mm, "end": v(21.57, 14.25) * mm});
            skLineSegment(sketch, "E3249", {"start": v(21.57, 14.25) * mm, "end": v(21.5, 14.2) * mm});
            skLineSegment(sketch, "E3250", {"start": v(21.5, 14.2) * mm, "end": v(21.42, 14.14) * mm});
            skLineSegment(sketch, "E3251", {"start": v(21.42, 14.14) * mm, "end": v(21.33, 14.07) * mm});
            skLineSegment(sketch, "E3252", {"start": v(21.33, 14.07) * mm, "end": v(21.24, 14) * mm});
            skLineSegment(sketch, "E3253", {"start": v(21.24, 14) * mm, "end": v(21.15, 13.93) * mm});
            skLineSegment(sketch, "E3254", {"start": v(21.15, 13.93) * mm, "end": v(21.05, 13.84) * mm});
            skLineSegment(sketch, "E3255", {"start": v(21.05, 13.84) * mm, "end": v(20.94, 13.75) * mm});
            skLineSegment(sketch, "E3256", {"start": v(20.94, 13.75) * mm, "end": v(20.83, 13.65) * mm});
            skLineSegment(sketch, "E3257", {"start": v(20.83, 13.65) * mm, "end": v(20.71, 13.54) * mm});
            skLineSegment(sketch, "E3258", {"start": v(20.71, 13.54) * mm, "end": v(20.59, 13.42) * mm});
            skLineSegment(sketch, "E3259", {"start": v(20.59, 13.42) * mm, "end": v(20.45, 13.29) * mm});
            skLineSegment(sketch, "E3260", {"start": v(20.45, 13.29) * mm, "end": v(20.31, 13.15) * mm});
            skLineSegment(sketch, "E3261", {"start": v(20.31, 13.15) * mm, "end": v(20.16, 13) * mm});
            skLineSegment(sketch, "E3262", {"start": v(20.16, 13) * mm, "end": v(20.02, 12.85) * mm});
            skLineSegment(sketch, "E3263", {"start": v(26.5, -8.54) * mm, "end": v(26.46, -8.5) * mm});
            skLineSegment(sketch, "E3264", {"start": v(26.46, -8.5) * mm, "end": v(26.42, -8.45) * mm});
            skLineSegment(sketch, "E3265", {"start": v(26.42, -8.45) * mm, "end": v(26.4, -8.4) * mm});
            skLineSegment(sketch, "E3266", {"start": v(26.4, -8.4) * mm, "end": v(26.36, -8.36) * mm});
            skLineSegment(sketch, "E3267", {"start": v(26.36, -8.36) * mm, "end": v(26.33, -8.32) * mm});
            skLineSegment(sketch, "E3268", {"start": v(26.33, -8.32) * mm, "end": v(26.3, -8.27) * mm});
            skLineSegment(sketch, "E3269", {"start": v(26.3, -8.27) * mm, "end": v(26.27, -8.23) * mm});
            skLineSegment(sketch, "E3270", {"start": v(26.27, -8.23) * mm, "end": v(26.24, -8.18) * mm});
            skLineSegment(sketch, "E3271", {"start": v(26.24, -8.18) * mm, "end": v(26.21, -8.13) * mm});
            skLineSegment(sketch, "E3272", {"start": v(26.21, -8.13) * mm, "end": v(26.19, -8.08) * mm});
            skLineSegment(sketch, "E3273", {"start": v(26.19, -8.08) * mm, "end": v(26.16, -8.02) * mm});
            skLineSegment(sketch, "E3274", {"start": v(26.16, -8.02) * mm, "end": v(26.14, -7.97) * mm});
            skLineSegment(sketch, "E3275", {"start": v(26.14, -7.97) * mm, "end": v(26.12, -7.92) * mm});
            skLineSegment(sketch, "E3276", {"start": v(26.12, -7.92) * mm, "end": v(26.1, -7.86) * mm});
            skLineSegment(sketch, "E3277", {"start": v(26.1, -7.86) * mm, "end": v(26.08, -7.8) * mm});
            skLineSegment(sketch, "E3278", {"start": v(26.08, -7.8) * mm, "end": v(26.06, -7.74) * mm});
            skLineSegment(sketch, "E3279", {"start": v(26.06, -7.74) * mm, "end": v(26.04, -7.68) * mm});
            skLineSegment(sketch, "E3280", {"start": v(26.04, -7.68) * mm, "end": v(26.03, -7.62) * mm});
            skLineSegment(sketch, "E3281", {"start": v(26.03, -7.62) * mm, "end": v(26.01, -7.56) * mm});
            skLineSegment(sketch, "E3282", {"start": v(26.01, -7.56) * mm, "end": v(26, -7.5) * mm});
            skLineSegment(sketch, "E3283", {"start": v(26, -7.5) * mm, "end": v(25.98, -7.43) * mm});
            skLineSegment(sketch, "E3284", {"start": v(25.98, -7.43) * mm, "end": v(25.97, -7.36) * mm});
            skLineSegment(sketch, "E3285", {"start": v(25.97, -7.36) * mm, "end": v(25.96, -7.29) * mm});
            skLineSegment(sketch, "E3286", {"start": v(25.96, -7.29) * mm, "end": v(25.95, -7.21) * mm});
            skLineSegment(sketch, "E3287", {"start": v(25.95, -7.21) * mm, "end": v(25.94, -7.14) * mm});
            skLineSegment(sketch, "E3288", {"start": v(25.94, -7.14) * mm, "end": v(25.94, -7.06) * mm});
            skLineSegment(sketch, "E3289", {"start": v(25.94, -7.06) * mm, "end": v(25.93, -6.98) * mm});
            skLineSegment(sketch, "E3290", {"start": v(25.93, -6.98) * mm, "end": v(25.93, -6.9) * mm});
            skLineSegment(sketch, "E3291", {"start": v(25.93, -6.9) * mm, "end": v(25.93, -6.81) * mm});
            skLineSegment(sketch, "E3292", {"start": v(25.93, -6.81) * mm, "end": v(25.92, -6.72) * mm});
            skLineSegment(sketch, "E3293", {"start": v(17.63, -7.12) * mm, "end": v(17.63, -7.07) * mm});
            skLineSegment(sketch, "E3294", {"start": v(17.63, -7.07) * mm, "end": v(17.63, -7.02) * mm});
            skLineSegment(sketch, "E3295", {"start": v(17.63, -7.02) * mm, "end": v(17.63, -6.97) * mm});
            skLineSegment(sketch, "E3296", {"start": v(17.63, -6.97) * mm, "end": v(17.64, -6.92) * mm});
            skLineSegment(sketch, "E3297", {"start": v(17.64, -6.92) * mm, "end": v(17.64, -6.87) * mm});
            skLineSegment(sketch, "E3298", {"start": v(17.64, -6.87) * mm, "end": v(17.65, -6.82) * mm});
            skLineSegment(sketch, "E3299", {"start": v(17.65, -6.82) * mm, "end": v(17.66, -6.76) * mm});
            skLineSegment(sketch, "E3300", {"start": v(17.66, -6.76) * mm, "end": v(17.67, -6.7) * mm});
            skLineSegment(sketch, "E3301", {"start": v(17.67, -6.7) * mm, "end": v(17.68, -6.65) * mm});
            skLineSegment(sketch, "E3302", {"start": v(17.68, -6.65) * mm, "end": v(17.7, -6.59) * mm});
            skLineSegment(sketch, "E3303", {"start": v(17.7, -6.59) * mm, "end": v(17.7, -6.53) * mm});
            skLineSegment(sketch, "E3304", {"start": v(17.7, -6.53) * mm, "end": v(17.73, -6.47) * mm});
            skLineSegment(sketch, "E3305", {"start": v(17.73, -6.47) * mm, "end": v(17.74, -6.4) * mm});
            skLineSegment(sketch, "E3306", {"start": v(17.74, -6.4) * mm, "end": v(17.76, -6.34) * mm});
            skLineSegment(sketch, "E3307", {"start": v(17.76, -6.34) * mm, "end": v(17.79, -6.28) * mm});
            skLineSegment(sketch, "E3308", {"start": v(17.79, -6.28) * mm, "end": v(17.8, -6.21) * mm});
            skLineSegment(sketch, "E3309", {"start": v(17.8, -6.21) * mm, "end": v(17.83, -6.14) * mm});
            skLineSegment(sketch, "E3310", {"start": v(17.83, -6.14) * mm, "end": v(17.86, -6.08) * mm});
            skLineSegment(sketch, "E3311", {"start": v(17.86, -6.08) * mm, "end": v(17.9, -6) * mm});
            skLineSegment(sketch, "E3312", {"start": v(17.9, -6) * mm, "end": v(17.92, -5.93) * mm});
            skLineSegment(sketch, "E3313", {"start": v(17.92, -5.93) * mm, "end": v(17.95, -5.86) * mm});
            skLineSegment(sketch, "E3314", {"start": v(17.95, -5.86) * mm, "end": v(18, -5.78) * mm});
            skLineSegment(sketch, "E3315", {"start": v(18, -5.78) * mm, "end": v(18.03, -5.7) * mm});
            skLineSegment(sketch, "E3316", {"start": v(18.03, -5.7) * mm, "end": v(18.07, -5.63) * mm});
            skLineSegment(sketch, "E3317", {"start": v(18.07, -5.63) * mm, "end": v(18.08, -5.61) * mm});
            skLineSegment(sketch, "E3318", {"start": v(15.36, -6.69) * mm, "end": v(15.3, -6.82) * mm});
            skLineSegment(sketch, "E3319", {"start": v(15.3, -6.82) * mm, "end": v(15.22, -7) * mm});
            skLineSegment(sketch, "E3320", {"start": v(15.22, -7) * mm, "end": v(15.14, -7.17) * mm});
            skLineSegment(sketch, "E3321", {"start": v(15.14, -7.17) * mm, "end": v(15.06, -7.34) * mm});
            skLineSegment(sketch, "E3322", {"start": v(15.06, -7.34) * mm, "end": v(15, -7.5) * mm});
            skLineSegment(sketch, "E3323", {"start": v(15, -7.5) * mm, "end": v(14.93, -7.67) * mm});
            skLineSegment(sketch, "E3324", {"start": v(14.93, -7.67) * mm, "end": v(14.87, -7.82) * mm});
            skLineSegment(sketch, "E3325", {"start": v(14.87, -7.82) * mm, "end": v(14.82, -7.98) * mm});
            skLineSegment(sketch, "E3326", {"start": v(14.82, -7.98) * mm, "end": v(14.76, -8.13) * mm});
            skLineSegment(sketch, "E3327", {"start": v(14.76, -8.13) * mm, "end": v(14.72, -8.28) * mm});
            skLineSegment(sketch, "E3328", {"start": v(14.72, -8.28) * mm, "end": v(14.67, -8.43) * mm});
            skLineSegment(sketch, "E3329", {"start": v(14.67, -8.43) * mm, "end": v(14.63, -8.57) * mm});
            skLineSegment(sketch, "E3330", {"start": v(14.63, -8.57) * mm, "end": v(14.6, -8.7) * mm});
            skLineSegment(sketch, "E3331", {"start": v(14.6, -8.7) * mm, "end": v(14.56, -8.85) * mm});
            skLineSegment(sketch, "E3332", {"start": v(14.56, -8.85) * mm, "end": v(14.53, -8.98) * mm});
            skLineSegment(sketch, "E3333", {"start": v(14.53, -8.98) * mm, "end": v(14.5, -9.11) * mm});
            skLineSegment(sketch, "E3334", {"start": v(14.5, -9.11) * mm, "end": v(14.48, -9.24) * mm});
            skLineSegment(sketch, "E3335", {"start": v(14.48, -9.24) * mm, "end": v(14.46, -9.37) * mm});
            skLineSegment(sketch, "E3336", {"start": v(14.46, -9.37) * mm, "end": v(14.45, -9.5) * mm});
            skLineSegment(sketch, "E3337", {"start": v(14.45, -9.5) * mm, "end": v(14.43, -9.62) * mm});
            skLineSegment(sketch, "E3338", {"start": v(14.43, -9.62) * mm, "end": v(14.42, -9.74) * mm});
            skLineSegment(sketch, "E3339", {"start": v(14.42, -9.74) * mm, "end": v(14.42, -9.85) * mm});
            skLineSegment(sketch, "E3340", {"start": v(14.42, -9.85) * mm, "end": v(14.41, -9.97) * mm});
            skLineSegment(sketch, "E3341", {"start": v(14.41, -9.97) * mm, "end": v(14.41, -10.08) * mm});
            skLineSegment(sketch, "E3342", {"start": v(18.08, -5.61) * mm, "end": v(18.13, -5.5) * mm});
            skLineSegment(sketch, "E3343", {"start": v(18.13, -5.5) * mm, "end": v(18.2, -5.4) * mm});
            skLineSegment(sketch, "E3344", {"start": v(18.2, -5.4) * mm, "end": v(18.26, -5.28) * mm});
            skLineSegment(sketch, "E3345", {"start": v(18.26, -5.28) * mm, "end": v(18.33, -5.16) * mm});
            skLineSegment(sketch, "E3346", {"start": v(18.33, -5.16) * mm, "end": v(18.4, -5.03) * mm});
            skLineSegment(sketch, "E3347", {"start": v(18.4, -5.03) * mm, "end": v(18.48, -4.9) * mm});
            skLineSegment(sketch, "E3348", {"start": v(18.48, -4.9) * mm, "end": v(18.57, -4.77) * mm});
            skLineSegment(sketch, "E3349", {"start": v(18.57, -4.77) * mm, "end": v(18.66, -4.63) * mm});
            skLineSegment(sketch, "E3350", {"start": v(18.66, -4.63) * mm, "end": v(18.76, -4.48) * mm});
            skLineSegment(sketch, "E3351", {"start": v(18.76, -4.48) * mm, "end": v(18.87, -4.32) * mm});
            skLineSegment(sketch, "E3352", {"start": v(18.87, -4.32) * mm, "end": v(18.98, -4.16) * mm});
            skLineSegment(sketch, "E3353", {"start": v(18.98, -4.16) * mm, "end": v(19.1, -3.98) * mm});
            skLineSegment(sketch, "E3354", {"start": v(19.1, -3.98) * mm, "end": v(19.24, -3.8) * mm});
            skLineSegment(sketch, "E3355", {"start": v(19.24, -3.8) * mm, "end": v(19.37, -3.6) * mm});
            skLineSegment(sketch, "E3356", {"start": v(19.37, -3.6) * mm, "end": v(19.52, -3.42) * mm});
            skLineSegment(sketch, "E3357", {"start": v(19.52, -3.42) * mm, "end": v(19.68, -3.2) * mm});
            skLineSegment(sketch, "E3358", {"start": v(19.68, -3.2) * mm, "end": v(19.86, -2.97) * mm});
            skLineSegment(sketch, "E3359", {"start": v(19.86, -2.97) * mm, "end": v(19.93, -2.88) * mm});
            skLineSegment(sketch, "E3360", {"start": v(19.93, -2.88) * mm, "end": v(20.14, -2.62) * mm});
            skLineSegment(sketch, "E3361", {"start": v(20.14, -2.62) * mm, "end": v(20.37, -2.34) * mm});
            skLineSegment(sketch, "E3362", {"start": v(20.37, -2.34) * mm, "end": v(20.85, -1.75) * mm});
            skLineSegment(sketch, "E3363", {"start": v(20.85, -1.75) * mm, "end": v(21.66, -0.77) * mm});
            skLineSegment(sketch, "E3364", {"start": v(28.45, -1.03) * mm, "end": v(28.54, -0.96) * mm});
            skLineSegment(sketch, "E3365", {"start": v(28.54, -0.96) * mm, "end": v(28.65, -0.86) * mm});
            skLineSegment(sketch, "E3366", {"start": v(28.65, -0.86) * mm, "end": v(28.76, -0.77) * mm});
            skLineSegment(sketch, "E3367", {"start": v(28.76, -0.77) * mm, "end": v(28.87, -0.68) * mm});
            skLineSegment(sketch, "E3368", {"start": v(28.87, -0.68) * mm, "end": v(28.98, -0.6) * mm});
            skLineSegment(sketch, "E3369", {"start": v(28.98, -0.6) * mm, "end": v(29.08, -0.51) * mm});
            skLineSegment(sketch, "E3370", {"start": v(29.08, -0.51) * mm, "end": v(29.19, -0.44) * mm});
            skLineSegment(sketch, "E3371", {"start": v(29.19, -0.44) * mm, "end": v(29.3, -0.36) * mm});
            skLineSegment(sketch, "E3372", {"start": v(29.3, -0.36) * mm, "end": v(29.4, -0.29) * mm});
            skLineSegment(sketch, "E3373", {"start": v(29.4, -0.29) * mm, "end": v(29.5, -0.22) * mm});
            skLineSegment(sketch, "E3374", {"start": v(29.5, -0.22) * mm, "end": v(29.6, -0.15) * mm});
            skLineSegment(sketch, "E3375", {"start": v(29.6, -0.15) * mm, "end": v(29.7, -0.08) * mm});
            skLineSegment(sketch, "E3376", {"start": v(29.7, -0.08) * mm, "end": v(29.79, -0.02) * mm});
            skLineSegment(sketch, "E3377", {"start": v(29.79, -0.02) * mm, "end": v(29.89, 0.04) * mm});
            skLineSegment(sketch, "E3378", {"start": v(29.89, 0.04) * mm, "end": v(29.98, 0.1) * mm});
            skLineSegment(sketch, "E3379", {"start": v(29.98, 0.1) * mm, "end": v(30.08, 0.15) * mm});
            skLineSegment(sketch, "E3380", {"start": v(26.74, 0.2) * mm, "end": v(26.63, 0.1) * mm});
            skLineSegment(sketch, "E3381", {"start": v(26.63, 0.1) * mm, "end": v(26.4, -0.1) * mm});
            skLineSegment(sketch, "E3382", {"start": v(26.4, -0.1) * mm, "end": v(26.17, -0.3) * mm});
            skLineSegment(sketch, "E3383", {"start": v(26.17, -0.3) * mm, "end": v(25.96, -0.5) * mm});
            skLineSegment(sketch, "E3384", {"start": v(25.96, -0.5) * mm, "end": v(25.75, -0.7) * mm});
            skLineSegment(sketch, "E3385", {"start": v(25.75, -0.7) * mm, "end": v(25.55, -0.9) * mm});
            skLineSegment(sketch, "E3386", {"start": v(25.55, -0.9) * mm, "end": v(25.36, -1.08) * mm});
            skLineSegment(sketch, "E3387", {"start": v(25.36, -1.08) * mm, "end": v(25.19, -1.27) * mm});
            skLineSegment(sketch, "E3388", {"start": v(25.19, -1.27) * mm, "end": v(25.02, -1.45) * mm});
            skLineSegment(sketch, "E3389", {"start": v(25.02, -1.45) * mm, "end": v(24.85, -1.63) * mm});
            skLineSegment(sketch, "E3390", {"start": v(24.85, -1.63) * mm, "end": v(24.7, -1.8) * mm});
            skLineSegment(sketch, "E3391", {"start": v(24.7, -1.8) * mm, "end": v(24.55, -1.97) * mm});
            skLineSegment(sketch, "E3392", {"start": v(24.55, -1.97) * mm, "end": v(24.42, -2.14) * mm});
            skLineSegment(sketch, "E3393", {"start": v(24.42, -2.14) * mm, "end": v(24.29, -2.3) * mm});
            skLineSegment(sketch, "E3394", {"start": v(24.29, -2.3) * mm, "end": v(24.16, -2.47) * mm});
            skLineSegment(sketch, "E3395", {"start": v(24.16, -2.47) * mm, "end": v(24.04, -2.63) * mm});
            skLineSegment(sketch, "E3396", {"start": v(24.04, -2.63) * mm, "end": v(23.93, -2.79) * mm});
            skLineSegment(sketch, "E3397", {"start": v(23.93, -2.79) * mm, "end": v(23.83, -2.94) * mm});
            skLineSegment(sketch, "E3398", {"start": v(23.83, -2.94) * mm, "end": v(23.73, -3.1) * mm});
            skLineSegment(sketch, "E3399", {"start": v(23.73, -3.1) * mm, "end": v(23.64, -3.24) * mm});
            skLineSegment(sketch, "E3400", {"start": v(23.64, -3.24) * mm, "end": v(23.55, -3.39) * mm});
            skLineSegment(sketch, "E3401", {"start": v(22.75, -5.5) * mm, "end": v(22.37, -5.8) * mm});
            skLineSegment(sketch, "E3402", {"start": v(22.37, -5.8) * mm, "end": v(22.03, -6.05) * mm});
            skLineSegment(sketch, "E3403", {"start": v(22.03, -6.05) * mm, "end": v(21.71, -6.29) * mm});
            skLineSegment(sketch, "E3404", {"start": v(21.71, -6.29) * mm, "end": v(21.41, -6.5) * mm});
            skLineSegment(sketch, "E3405", {"start": v(21.41, -6.5) * mm, "end": v(21.14, -6.7) * mm});
            skLineSegment(sketch, "E3406", {"start": v(21.14, -6.7) * mm, "end": v(20.88, -6.88) * mm});
            skLineSegment(sketch, "E3407", {"start": v(20.88, -6.88) * mm, "end": v(20.64, -7.04) * mm});
            skLineSegment(sketch, "E3408", {"start": v(20.64, -7.04) * mm, "end": v(20.42, -7.19) * mm});
            skLineSegment(sketch, "E3409", {"start": v(20.42, -7.19) * mm, "end": v(20.21, -7.32) * mm});
            skLineSegment(sketch, "E3410", {"start": v(20.21, -7.32) * mm, "end": v(20.02, -7.44) * mm});
            skLineSegment(sketch, "E3411", {"start": v(20.02, -7.44) * mm, "end": v(19.84, -7.54) * mm});
            skLineSegment(sketch, "E3412", {"start": v(19.84, -7.54) * mm, "end": v(19.68, -7.63) * mm});
            skLineSegment(sketch, "E3413", {"start": v(19.68, -7.63) * mm, "end": v(19.53, -7.71) * mm});
            skLineSegment(sketch, "E3414", {"start": v(19.53, -7.71) * mm, "end": v(19.4, -7.78) * mm});
            skLineSegment(sketch, "E3415", {"start": v(19.4, -7.78) * mm, "end": v(19.26, -7.84) * mm});
            skLineSegment(sketch, "E3416", {"start": v(19.26, -7.84) * mm, "end": v(19.15, -7.9) * mm});
            skLineSegment(sketch, "E3417", {"start": v(19.15, -7.9) * mm, "end": v(19.04, -7.94) * mm});
            skLineSegment(sketch, "E3418", {"start": v(19.04, -7.94) * mm, "end": v(18.94, -7.97) * mm});
            skLineSegment(sketch, "E3419", {"start": v(18.94, -7.97) * mm, "end": v(18.86, -8) * mm});
            skLineSegment(sketch, "E3420", {"start": v(18.86, -8) * mm, "end": v(18.78, -8.02) * mm});
            skLineSegment(sketch, "E3421", {"start": v(18.78, -8.02) * mm, "end": v(18.7, -8.04) * mm});
            skLineSegment(sketch, "E3422", {"start": v(18.7, -8.04) * mm, "end": v(18.64, -8.05) * mm});
            skLineSegment(sketch, "E3423", {"start": v(18.64, -8.05) * mm, "end": v(18.58, -8.05) * mm});
            skLineSegment(sketch, "E3424", {"start": v(18.58, -8.05) * mm, "end": v(18.52, -8.06) * mm});
            skLineSegment(sketch, "E3425", {"start": v(17.55, -11.34) * mm, "end": v(17.67, -11.26) * mm});
            skLineSegment(sketch, "E3426", {"start": v(17.67, -11.26) * mm, "end": v(17.8, -11.18) * mm});
            skLineSegment(sketch, "E3427", {"start": v(17.8, -11.18) * mm, "end": v(17.92, -11.1) * mm});
            skLineSegment(sketch, "E3428", {"start": v(17.92, -11.1) * mm, "end": v(18.06, -11.01) * mm});
            skLineSegment(sketch, "E3429", {"start": v(18.06, -11.01) * mm, "end": v(18.19, -10.92) * mm});
            skLineSegment(sketch, "E3430", {"start": v(18.19, -10.92) * mm, "end": v(18.33, -10.82) * mm});
            skLineSegment(sketch, "E3431", {"start": v(18.33, -10.82) * mm, "end": v(18.47, -10.71) * mm});
            skLineSegment(sketch, "E3432", {"start": v(18.47, -10.71) * mm, "end": v(18.61, -10.6) * mm});
            skLineSegment(sketch, "E3433", {"start": v(18.61, -10.6) * mm, "end": v(18.76, -10.49) * mm});
            skLineSegment(sketch, "E3434", {"start": v(18.76, -10.49) * mm, "end": v(18.91, -10.37) * mm});
            skLineSegment(sketch, "E3435", {"start": v(18.91, -10.37) * mm, "end": v(19.06, -10.24) * mm});
            skLineSegment(sketch, "E3436", {"start": v(19.06, -10.24) * mm, "end": v(19.22, -10.1) * mm});
            skLineSegment(sketch, "E3437", {"start": v(19.22, -10.1) * mm, "end": v(19.38, -9.97) * mm});
            skLineSegment(sketch, "E3438", {"start": v(19.38, -9.97) * mm, "end": v(19.55, -9.83) * mm});
            skLineSegment(sketch, "E3439", {"start": v(19.55, -9.83) * mm, "end": v(19.71, -9.68) * mm});
            skLineSegment(sketch, "E3440", {"start": v(19.71, -9.68) * mm, "end": v(19.75, -9.64) * mm});
            skLineSegment(sketch, "E3441", {"start": v(-33.39, 12.68) * mm, "end": v(-33.8, 12.62) * mm});
            skLineSegment(sketch, "E3442", {"start": v(-33.8, 12.62) * mm, "end": v(-34.2, 12.55) * mm});
            skLineSegment(sketch, "E3443", {"start": v(-34.2, 12.55) * mm, "end": v(-34.58, 12.49) * mm});
            skLineSegment(sketch, "E3444", {"start": v(-34.58, 12.49) * mm, "end": v(-34.96, 12.42) * mm});
            skLineSegment(sketch, "E3445", {"start": v(-34.96, 12.42) * mm, "end": v(-35.34, 12.34) * mm});
            skLineSegment(sketch, "E3446", {"start": v(-35.34, 12.34) * mm, "end": v(-35.7, 12.27) * mm});
            skLineSegment(sketch, "E3447", {"start": v(-35.7, 12.27) * mm, "end": v(-36.06, 12.2) * mm});
            skLineSegment(sketch, "E3448", {"start": v(-36.06, 12.2) * mm, "end": v(-36.42, 12.11) * mm});
            skLineSegment(sketch, "E3449", {"start": v(-36.42, 12.11) * mm, "end": v(-36.76, 12.03) * mm});
            skLineSegment(sketch, "E3450", {"start": v(-36.76, 12.03) * mm, "end": v(-37.1, 11.94) * mm});
            skLineSegment(sketch, "E3451", {"start": v(-37.1, 11.94) * mm, "end": v(-37.44, 11.86) * mm});
            skLineSegment(sketch, "E3452", {"start": v(-37.44, 11.86) * mm, "end": v(-37.77, 11.77) * mm});
            skLineSegment(sketch, "E3453", {"start": v(-37.77, 11.77) * mm, "end": v(-38.1, 11.68) * mm});
            skLineSegment(sketch, "E3454", {"start": v(21.32, 0.89) * mm, "end": v(21.28, 0.94) * mm});
            skLineSegment(sketch, "E3455", {"start": v(21.28, 0.94) * mm, "end": v(21.25, 0.98) * mm});
            skLineSegment(sketch, "E3456", {"start": v(21.25, 0.98) * mm, "end": v(21.21, 1.02) * mm});
            skLineSegment(sketch, "E3457", {"start": v(21.21, 1.02) * mm, "end": v(21.18, 1.07) * mm});
            skLineSegment(sketch, "E3458", {"start": v(21.18, 1.07) * mm, "end": v(21.15, 1.1) * mm});
            skLineSegment(sketch, "E3459", {"start": v(21.15, 1.1) * mm, "end": v(21.11, 1.14) * mm});
            skLineSegment(sketch, "E3460", {"start": v(21.11, 1.14) * mm, "end": v(21.08, 1.18) * mm});
            skLineSegment(sketch, "E3461", {"start": v(21.08, 1.18) * mm, "end": v(21.05, 1.2) * mm});
            skLineSegment(sketch, "E3462", {"start": v(21.05, 1.2) * mm, "end": v(21.01, 1.24) * mm});
            skLineSegment(sketch, "E3463", {"start": v(21.01, 1.24) * mm, "end": v(20.98, 1.27) * mm});
            skLineSegment(sketch, "E3464", {"start": v(20.98, 1.27) * mm, "end": v(20.95, 1.3) * mm});
            skLineSegment(sketch, "E3465", {"start": v(20.95, 1.3) * mm, "end": v(20.92, 1.33) * mm});
            skLineSegment(sketch, "E3466", {"start": v(20.92, 1.33) * mm, "end": v(20.88, 1.35) * mm});
            skLineSegment(sketch, "E3467", {"start": v(20.88, 1.35) * mm, "end": v(20.85, 1.37) * mm});
            skLineSegment(sketch, "E3468", {"start": v(20.85, 1.37) * mm, "end": v(20.82, 1.4) * mm});
            skLineSegment(sketch, "E3469", {"start": v(20.82, 1.4) * mm, "end": v(20.79, 1.42) * mm});
            skLineSegment(sketch, "E3470", {"start": v(20.79, 1.42) * mm, "end": v(20.76, 1.44) * mm});
            skLineSegment(sketch, "E3471", {"start": v(20.76, 1.44) * mm, "end": v(20.73, 1.45) * mm});
            skLineSegment(sketch, "E3472", {"start": v(20.73, 1.45) * mm, "end": v(20.7, 1.47) * mm});
            skLineSegment(sketch, "E3473", {"start": v(20.7, 1.47) * mm, "end": v(20.66, 1.49) * mm});
            skLineSegment(sketch, "E3474", {"start": v(20.66, 1.49) * mm, "end": v(20.63, 1.5) * mm});
            skLineSegment(sketch, "E3475", {"start": v(20.63, 1.5) * mm, "end": v(20.6, 1.52) * mm});
            skLineSegment(sketch, "E3476", {"start": v(20.6, 1.52) * mm, "end": v(20.57, 1.53) * mm});
            skLineSegment(sketch, "E3477", {"start": v(20.57, 1.53) * mm, "end": v(20.54, 1.54) * mm});
            skLineSegment(sketch, "E3478", {"start": v(20.54, 1.54) * mm, "end": v(20.51, 1.55) * mm});
            skLineSegment(sketch, "E3479", {"start": v(20.51, 1.55) * mm, "end": v(20.48, 1.56) * mm});
            skLineSegment(sketch, "E3480", {"start": v(20.48, 1.56) * mm, "end": v(20.45, 1.57) * mm});
            skLineSegment(sketch, "E3481", {"start": v(20.45, 1.57) * mm, "end": v(20.42, 1.57) * mm});
            skLineSegment(sketch, "E3482", {"start": v(20.42, 1.57) * mm, "end": v(20.39, 1.58) * mm});
            skLineSegment(sketch, "E3483", {"start": v(20.39, 1.58) * mm, "end": v(20.37, 1.58) * mm});
            skLineSegment(sketch, "E3484", {"start": v(20.37, 1.58) * mm, "end": v(20.35, 1.58) * mm});
            skLineSegment(sketch, "E3485", {"start": v(20.35, 1.58) * mm, "end": v(20.32, 1.59) * mm});
            skLineSegment(sketch, "E3486", {"start": v(20.32, 1.59) * mm, "end": v(20.3, 1.59) * mm});
            skLineSegment(sketch, "E3487", {"start": v(20.3, 1.59) * mm, "end": v(20.26, 1.6) * mm});
            skLineSegment(sketch, "E3488", {"start": v(20.26, 1.6) * mm, "end": v(20.23, 1.6) * mm});
            skLineSegment(sketch, "E3489", {"start": v(21.86, -0.27) * mm, "end": v(21.85, -0.25) * mm});
            skLineSegment(sketch, "E3490", {"start": v(21.85, -0.25) * mm, "end": v(21.85, -0.22) * mm});
            skLineSegment(sketch, "E3491", {"start": v(21.85, -0.22) * mm, "end": v(21.85, -0.19) * mm});
            skLineSegment(sketch, "E3492", {"start": v(21.85, -0.19) * mm, "end": v(21.85, -0.16) * mm});
            skLineSegment(sketch, "E3493", {"start": v(21.85, -0.16) * mm, "end": v(21.84, -0.13) * mm});
            skLineSegment(sketch, "E3494", {"start": v(21.84, -0.13) * mm, "end": v(21.84, -0.1) * mm});
            skLineSegment(sketch, "E3495", {"start": v(21.84, -0.1) * mm, "end": v(21.83, -0.06) * mm});
            skLineSegment(sketch, "E3496", {"start": v(21.83, -0.06) * mm, "end": v(21.82, -0.03) * mm});
            skLineSegment(sketch, "E3497", {"start": v(21.82, -0.03) * mm, "end": v(21.81, 0) * mm});
            skLineSegment(sketch, "E3498", {"start": v(21.81, 0) * mm, "end": v(21.8, 0.04) * mm});
            skLineSegment(sketch, "E3499", {"start": v(21.8, 0.04) * mm, "end": v(21.79, 0.08) * mm});
            skLineSegment(sketch, "E3500", {"start": v(21.79, 0.08) * mm, "end": v(21.77, 0.11) * mm});
            skLineSegment(sketch, "E3501", {"start": v(21.77, 0.11) * mm, "end": v(21.76, 0.15) * mm});
            skLineSegment(sketch, "E3502", {"start": v(21.76, 0.15) * mm, "end": v(21.74, 0.2) * mm});
            skLineSegment(sketch, "E3503", {"start": v(21.74, 0.2) * mm, "end": v(21.72, 0.24) * mm});
            skLineSegment(sketch, "E3504", {"start": v(21.72, 0.24) * mm, "end": v(21.7, 0.28) * mm});
            skLineSegment(sketch, "E3505", {"start": v(21.7, 0.28) * mm, "end": v(21.68, 0.32) * mm});
            skLineSegment(sketch, "E3506", {"start": v(21.68, 0.32) * mm, "end": v(21.65, 0.37) * mm});
            skLineSegment(sketch, "E3507", {"start": v(21.65, 0.37) * mm, "end": v(21.63, 0.42) * mm});
            skLineSegment(sketch, "E3508", {"start": v(21.63, 0.42) * mm, "end": v(21.6, 0.47) * mm});
            skLineSegment(sketch, "E3509", {"start": v(21.6, 0.47) * mm, "end": v(21.57, 0.52) * mm});
            skLineSegment(sketch, "E3510", {"start": v(21.57, 0.52) * mm, "end": v(21.54, 0.57) * mm});
            skLineSegment(sketch, "E3511", {"start": v(21.54, 0.57) * mm, "end": v(21.5, 0.63) * mm});
            skLineSegment(sketch, "E3512", {"start": v(21.5, 0.63) * mm, "end": v(21.46, 0.68) * mm});
            skLineSegment(sketch, "E3513", {"start": v(21.46, 0.68) * mm, "end": v(21.42, 0.74) * mm});
            skLineSegment(sketch, "E3514", {"start": v(21.42, 0.74) * mm, "end": v(21.38, 0.8) * mm});
            skLineSegment(sketch, "E3515", {"start": v(21.38, 0.8) * mm, "end": v(21.34, 0.87) * mm});
            skLineSegment(sketch, "E3516", {"start": v(21.34, 0.87) * mm, "end": v(21.32, 0.89) * mm});
            skLineSegment(sketch, "E3517", {"start": v(22.59, -7.16) * mm, "end": v(22.59, -7.23) * mm});
            skLineSegment(sketch, "E3518", {"start": v(22.59, -7.23) * mm, "end": v(22.6, -7.41) * mm});
            skLineSegment(sketch, "E3519", {"start": v(22.6, -7.41) * mm, "end": v(22.6, -7.6) * mm});
            skLineSegment(sketch, "E3520", {"start": v(22.6, -7.6) * mm, "end": v(22.6, -7.76) * mm});
            skLineSegment(sketch, "E3521", {"start": v(22.6, -7.76) * mm, "end": v(22.62, -7.93) * mm});
            skLineSegment(sketch, "E3522", {"start": v(22.62, -7.93) * mm, "end": v(22.63, -8.1) * mm});
            skLineSegment(sketch, "E3523", {"start": v(22.63, -8.1) * mm, "end": v(22.65, -8.26) * mm});
            skLineSegment(sketch, "E3524", {"start": v(22.65, -8.26) * mm, "end": v(22.67, -8.41) * mm});
            skLineSegment(sketch, "E3525", {"start": v(22.67, -8.41) * mm, "end": v(22.7, -8.57) * mm});
            skLineSegment(sketch, "E3526", {"start": v(22.7, -8.57) * mm, "end": v(22.72, -8.71) * mm});
            skLineSegment(sketch, "E3527", {"start": v(22.72, -8.71) * mm, "end": v(22.74, -8.86) * mm});
            skLineSegment(sketch, "E3528", {"start": v(22.74, -8.86) * mm, "end": v(22.77, -9) * mm});
            skLineSegment(sketch, "E3529", {"start": v(22.77, -9) * mm, "end": v(22.8, -9.14) * mm});
            skLineSegment(sketch, "E3530", {"start": v(22.8, -9.14) * mm, "end": v(22.84, -9.27) * mm});
            skLineSegment(sketch, "E3531", {"start": v(22.84, -9.27) * mm, "end": v(22.87, -9.4) * mm});
            skLineSegment(sketch, "E3532", {"start": v(22.87, -9.4) * mm, "end": v(22.91, -9.53) * mm});
            skLineSegment(sketch, "E3533", {"start": v(22.91, -9.53) * mm, "end": v(22.95, -9.65) * mm});
            skLineSegment(sketch, "E3534", {"start": v(22.95, -9.65) * mm, "end": v(23, -9.77) * mm});
            skLineSegment(sketch, "E3535", {"start": v(23, -9.77) * mm, "end": v(23.04, -9.9) * mm});
            skLineSegment(sketch, "E3536", {"start": v(23.04, -9.9) * mm, "end": v(23.1, -10) * mm});
            skLineSegment(sketch, "E3537", {"start": v(23.1, -10) * mm, "end": v(23.14, -10.12) * mm});
            skLineSegment(sketch, "E3538", {"start": v(23.14, -10.12) * mm, "end": v(23.2, -10.23) * mm});
            skLineSegment(sketch, "E3539", {"start": v(23.2, -10.23) * mm, "end": v(23.25, -10.33) * mm});
            skLineSegment(sketch, "E3540", {"start": v(23.25, -10.33) * mm, "end": v(23.3, -10.44) * mm});
            skLineSegment(sketch, "E3541", {"start": v(23.3, -10.44) * mm, "end": v(23.36, -10.54) * mm});
            skLineSegment(sketch, "E3542", {"start": v(23.36, -10.54) * mm, "end": v(23.42, -10.64) * mm});
            skLineSegment(sketch, "E3543", {"start": v(23.42, -10.64) * mm, "end": v(23.48, -10.73) * mm});
            skLineSegment(sketch, "E3544", {"start": v(23.48, -10.73) * mm, "end": v(23.55, -10.83) * mm});
            skLineSegment(sketch, "E3545", {"start": v(23.55, -10.83) * mm, "end": v(23.62, -10.92) * mm});
            skLineSegment(sketch, "E3546", {"start": v(22.75, -6.75) * mm, "end": v(22.75, -5.5) * mm});
            skLineSegment(sketch, "E3547", {"start": v(21.66, -0.77) * mm, "end": v(21.86, -0.27) * mm});
            skLineSegment(sketch, "E3548", {"start": v(23.55, -3.39) * mm, "end": v(23.48, -3.52) * mm});
            skLineSegment(sketch, "E3549", {"start": v(23.48, -3.52) * mm, "end": v(23.4, -3.65) * mm});
            skLineSegment(sketch, "E3550", {"start": v(23.4, -3.65) * mm, "end": v(23.34, -3.79) * mm});
            skLineSegment(sketch, "E3551", {"start": v(23.34, -3.79) * mm, "end": v(23.28, -3.92) * mm});
            skLineSegment(sketch, "E3552", {"start": v(23.28, -3.92) * mm, "end": v(23.22, -4.06) * mm});
            skLineSegment(sketch, "E3553", {"start": v(23.22, -4.06) * mm, "end": v(23.16, -4.2) * mm});
            skLineSegment(sketch, "E3554", {"start": v(23.16, -4.2) * mm, "end": v(23.1, -4.34) * mm});
            skLineSegment(sketch, "E3555", {"start": v(23.1, -4.34) * mm, "end": v(23.05, -4.48) * mm});
            skLineSegment(sketch, "E3556", {"start": v(23.05, -4.48) * mm, "end": v(23, -4.62) * mm});
            skLineSegment(sketch, "E3557", {"start": v(23, -4.62) * mm, "end": v(22.95, -4.76) * mm});
            skLineSegment(sketch, "E3558", {"start": v(22.95, -4.76) * mm, "end": v(22.9, -4.9) * mm});
            skLineSegment(sketch, "E3559", {"start": v(22.9, -4.9) * mm, "end": v(22.87, -5.04) * mm});
            skLineSegment(sketch, "E3560", {"start": v(22.87, -5.04) * mm, "end": v(22.83, -5.2) * mm});
            skLineSegment(sketch, "E3561", {"start": v(22.83, -5.2) * mm, "end": v(22.8, -5.34) * mm});
            skLineSegment(sketch, "E3562", {"start": v(22.8, -5.34) * mm, "end": v(22.76, -5.49) * mm});
            skLineSegment(sketch, "E3563", {"start": v(22.76, -5.49) * mm, "end": v(22.73, -5.64) * mm});
            skLineSegment(sketch, "E3564", {"start": v(22.73, -5.64) * mm, "end": v(22.7, -5.79) * mm});
            skLineSegment(sketch, "E3565", {"start": v(22.7, -5.79) * mm, "end": v(22.68, -5.94) * mm});
            skLineSegment(sketch, "E3566", {"start": v(22.68, -5.94) * mm, "end": v(22.66, -6.1) * mm});
            skLineSegment(sketch, "E3567", {"start": v(22.66, -6.1) * mm, "end": v(22.64, -6.25) * mm});
            skLineSegment(sketch, "E3568", {"start": v(22.64, -6.25) * mm, "end": v(22.62, -6.4) * mm});
            skLineSegment(sketch, "E3569", {"start": v(22.62, -6.4) * mm, "end": v(22.6, -6.57) * mm});
            skLineSegment(sketch, "E3570", {"start": v(22.6, -6.57) * mm, "end": v(22.6, -6.73) * mm});
            skLineSegment(sketch, "E3571", {"start": v(22.6, -6.73) * mm, "end": v(22.6, -6.9) * mm});
            skLineSegment(sketch, "E3572", {"start": v(22.6, -6.9) * mm, "end": v(22.6, -7.06) * mm});
            skLineSegment(sketch, "E3573", {"start": v(22.6, -7.06) * mm, "end": v(22.59, -7.16) * mm});
            skLineSegment(sketch, "E3574", {"start": v(20.05, -9.37) * mm, "end": v(20.32, -9.13) * mm});
            skLineSegment(sketch, "E3575", {"start": v(20.32, -9.13) * mm, "end": v(20.6, -8.87) * mm});
            skLineSegment(sketch, "E3576", {"start": v(20.6, -8.87) * mm, "end": v(20.88, -8.6) * mm});
            skLineSegment(sketch, "E3577", {"start": v(20.88, -8.6) * mm, "end": v(21.18, -8.31) * mm});
            skLineSegment(sketch, "E3578", {"start": v(21.18, -8.31) * mm, "end": v(21.49, -8.01) * mm});
            skLineSegment(sketch, "E3579", {"start": v(21.49, -8.01) * mm, "end": v(21.8, -7.7) * mm});
            skLineSegment(sketch, "E3580", {"start": v(21.8, -7.7) * mm, "end": v(22.12, -7.39) * mm});
            skLineSegment(sketch, "E3581", {"start": v(22.12, -7.39) * mm, "end": v(22.43, -7.07) * mm});
            skLineSegment(sketch, "E3582", {"start": v(22.43, -7.07) * mm, "end": v(22.75, -6.75) * mm});
            skLineSegment(sketch, "E3583", {"start": v(19.75, -9.64) * mm, "end": v(20.05, -9.37) * mm});
            skLineSegment(sketch, "E3584", {"start": v(29.18, -3.2) * mm, "end": v(29.05, -3.3) * mm});
            skLineSegment(sketch, "E3585", {"start": v(29.05, -3.3) * mm, "end": v(28.92, -3.4) * mm});
            skLineSegment(sketch, "E3586", {"start": v(28.92, -3.4) * mm, "end": v(28.79, -3.5) * mm});
            skLineSegment(sketch, "E3587", {"start": v(28.79, -3.5) * mm, "end": v(28.65, -3.6) * mm});
            skLineSegment(sketch, "E3588", {"start": v(28.65, -3.6) * mm, "end": v(28.52, -3.69) * mm});
            skLineSegment(sketch, "E3589", {"start": v(28.52, -3.69) * mm, "end": v(28.38, -3.78) * mm});
            skLineSegment(sketch, "E3590", {"start": v(28.38, -3.78) * mm, "end": v(28.23, -3.87) * mm});
            skLineSegment(sketch, "E3591", {"start": v(28.23, -3.87) * mm, "end": v(28.09, -3.96) * mm});
            skLineSegment(sketch, "E3592", {"start": v(28.09, -3.96) * mm, "end": v(27.94, -4.05) * mm});
            skLineSegment(sketch, "E3593", {"start": v(27.94, -4.05) * mm, "end": v(27.79, -4.14) * mm});
            skLineSegment(sketch, "E3594", {"start": v(27.79, -4.14) * mm, "end": v(27.63, -4.23) * mm});
            skLineSegment(sketch, "E3595", {"start": v(27.63, -4.23) * mm, "end": v(27.48, -4.31) * mm});
            skLineSegment(sketch, "E3596", {"start": v(27.48, -4.31) * mm, "end": v(27.32, -4.4) * mm});
            skLineSegment(sketch, "E3597", {"start": v(27.32, -4.4) * mm, "end": v(27.15, -4.47) * mm});
            skLineSegment(sketch, "E3598", {"start": v(27.15, -4.47) * mm, "end": v(26.99, -4.55) * mm});
            skLineSegment(sketch, "E3599", {"start": v(26.99, -4.55) * mm, "end": v(26.82, -4.63) * mm});
            skLineSegment(sketch, "E3600", {"start": v(26.82, -4.63) * mm, "end": v(26.64, -4.7) * mm});
            skLineSegment(sketch, "E3601", {"start": v(26.64, -4.7) * mm, "end": v(26.47, -4.78) * mm});
            skLineSegment(sketch, "E3602", {"start": v(26.47, -4.78) * mm, "end": v(26.29, -4.86) * mm});
            skLineSegment(sketch, "E3603", {"start": v(26.29, -4.86) * mm, "end": v(26.12, -4.92) * mm});
            skLineSegment(sketch, "E3604", {"start": v(30.63, -3.87) * mm, "end": v(30.83, -3.74) * mm});
            skLineSegment(sketch, "E3605", {"start": v(30.83, -3.74) * mm, "end": v(31.02, -3.6) * mm});
            skLineSegment(sketch, "E3606", {"start": v(31.02, -3.6) * mm, "end": v(31.2, -3.48) * mm});
            skLineSegment(sketch, "E3607", {"start": v(31.2, -3.48) * mm, "end": v(31.39, -3.36) * mm});
            skLineSegment(sketch, "E3608", {"start": v(31.39, -3.36) * mm, "end": v(31.56, -3.23) * mm});
            skLineSegment(sketch, "E3609", {"start": v(31.56, -3.23) * mm, "end": v(31.72, -3.1) * mm});
            skLineSegment(sketch, "E3610", {"start": v(31.72, -3.1) * mm, "end": v(31.88, -2.99) * mm});
            skLineSegment(sketch, "E3611", {"start": v(31.88, -2.99) * mm, "end": v(32.03, -2.87) * mm});
            skLineSegment(sketch, "E3612", {"start": v(32.03, -2.87) * mm, "end": v(32.17, -2.75) * mm});
            skLineSegment(sketch, "E3613", {"start": v(32.17, -2.75) * mm, "end": v(32.31, -2.63) * mm});
            skLineSegment(sketch, "E3614", {"start": v(32.31, -2.63) * mm, "end": v(32.44, -2.51) * mm});
            skLineSegment(sketch, "E3615", {"start": v(32.44, -2.51) * mm, "end": v(32.57, -2.4) * mm});
            skLineSegment(sketch, "E3616", {"start": v(32.57, -2.4) * mm, "end": v(32.7, -2.28) * mm});
            skLineSegment(sketch, "E3617", {"start": v(32.7, -2.28) * mm, "end": v(32.8, -2.17) * mm});
            skLineSegment(sketch, "E3618", {"start": v(32.8, -2.17) * mm, "end": v(32.92, -2.06) * mm});
            skLineSegment(sketch, "E3619", {"start": v(32.92, -2.06) * mm, "end": v(33.02, -1.95) * mm});
            skLineSegment(sketch, "E3620", {"start": v(33.02, -1.95) * mm, "end": v(33.12, -1.84) * mm});
            skLineSegment(sketch, "E3621", {"start": v(33.12, -1.84) * mm, "end": v(33.22, -1.73) * mm});
            skLineSegment(sketch, "E3622", {"start": v(33.22, -1.73) * mm, "end": v(33.31, -1.62) * mm});
            skLineSegment(sketch, "E3623", {"start": v(33.31, -1.62) * mm, "end": v(33.4, -1.5) * mm});
            skLineSegment(sketch, "E3624", {"start": v(33.4, -1.5) * mm, "end": v(33.48, -1.4) * mm});
            skLineSegment(sketch, "E3625", {"start": v(30.02, -8.74) * mm, "end": v(29.93, -8.78) * mm});
            skLineSegment(sketch, "E3626", {"start": v(29.93, -8.78) * mm, "end": v(29.84, -8.82) * mm});
            skLineSegment(sketch, "E3627", {"start": v(29.84, -8.82) * mm, "end": v(29.75, -8.85) * mm});
            skLineSegment(sketch, "E3628", {"start": v(29.75, -8.85) * mm, "end": v(29.66, -8.88) * mm});
            skLineSegment(sketch, "E3629", {"start": v(29.66, -8.88) * mm, "end": v(29.57, -8.92) * mm});
            skLineSegment(sketch, "E3630", {"start": v(29.57, -8.92) * mm, "end": v(29.48, -8.95) * mm});
            skLineSegment(sketch, "E3631", {"start": v(29.48, -8.95) * mm, "end": v(29.39, -8.97) * mm});
            skLineSegment(sketch, "E3632", {"start": v(29.39, -8.97) * mm, "end": v(29.3, -9) * mm});
            skLineSegment(sketch, "E3633", {"start": v(29.3, -9) * mm, "end": v(29.21, -9.03) * mm});
            skLineSegment(sketch, "E3634", {"start": v(29.21, -9.03) * mm, "end": v(29.12, -9.05) * mm});
            skLineSegment(sketch, "E3635", {"start": v(29.12, -9.05) * mm, "end": v(29.03, -9.07) * mm});
            skLineSegment(sketch, "E3636", {"start": v(29.03, -9.07) * mm, "end": v(28.95, -9.09) * mm});
            skLineSegment(sketch, "E3637", {"start": v(28.95, -9.09) * mm, "end": v(28.86, -9.1) * mm});
            skLineSegment(sketch, "E3638", {"start": v(28.86, -9.1) * mm, "end": v(28.77, -9.12) * mm});
            skLineSegment(sketch, "E3639", {"start": v(28.77, -9.12) * mm, "end": v(28.69, -9.14) * mm});
            skLineSegment(sketch, "E3640", {"start": v(28.69, -9.14) * mm, "end": v(28.6, -9.15) * mm});
            skLineSegment(sketch, "E3641", {"start": v(28.6, -9.15) * mm, "end": v(28.51, -9.16) * mm});
            skLineSegment(sketch, "E3642", {"start": v(28.51, -9.16) * mm, "end": v(28.43, -9.17) * mm});
            skLineSegment(sketch, "E3643", {"start": v(28.43, -9.17) * mm, "end": v(28.34, -9.18) * mm});
            skLineSegment(sketch, "E3644", {"start": v(28.34, -9.18) * mm, "end": v(28.26, -9.18) * mm});
            skLineSegment(sketch, "E3645", {"start": v(28.26, -9.18) * mm, "end": v(28.17, -9.18) * mm});
            skLineSegment(sketch, "E3646", {"start": v(28.17, -9.18) * mm, "end": v(28.08, -9.19) * mm});
            skLineSegment(sketch, "E3647", {"start": v(28.08, -9.19) * mm, "end": v(28, -9.19) * mm});
            skLineSegment(sketch, "E3648", {"start": v(33.86, 2.37) * mm, "end": v(33.83, 2.4) * mm});
            skLineSegment(sketch, "E3649", {"start": v(33.83, 2.4) * mm, "end": v(33.8, 2.42) * mm});
            skLineSegment(sketch, "E3650", {"start": v(33.8, 2.42) * mm, "end": v(33.75, 2.45) * mm});
            skLineSegment(sketch, "E3651", {"start": v(33.75, 2.45) * mm, "end": v(33.71, 2.47) * mm});
            skLineSegment(sketch, "E3652", {"start": v(33.71, 2.47) * mm, "end": v(33.67, 2.5) * mm});
            skLineSegment(sketch, "E3653", {"start": v(33.67, 2.5) * mm, "end": v(33.63, 2.52) * mm});
            skLineSegment(sketch, "E3654", {"start": v(33.63, 2.52) * mm, "end": v(33.59, 2.54) * mm});
            skLineSegment(sketch, "E3655", {"start": v(33.59, 2.54) * mm, "end": v(33.54, 2.56) * mm});
            skLineSegment(sketch, "E3656", {"start": v(33.54, 2.56) * mm, "end": v(33.5, 2.59) * mm});
            skLineSegment(sketch, "E3657", {"start": v(33.5, 2.59) * mm, "end": v(33.45, 2.6) * mm});
            skLineSegment(sketch, "E3658", {"start": v(33.45, 2.6) * mm, "end": v(33.4, 2.62) * mm});
            skLineSegment(sketch, "E3659", {"start": v(33.4, 2.62) * mm, "end": v(33.36, 2.64) * mm});
            skLineSegment(sketch, "E3660", {"start": v(33.36, 2.64) * mm, "end": v(33.31, 2.66) * mm});
            skLineSegment(sketch, "E3661", {"start": v(33.31, 2.66) * mm, "end": v(33.26, 2.68) * mm});
            skLineSegment(sketch, "E3662", {"start": v(33.26, 2.68) * mm, "end": v(33.2, 2.7) * mm});
            skLineSegment(sketch, "E3663", {"start": v(33.2, 2.7) * mm, "end": v(33.16, 2.7) * mm});
            skLineSegment(sketch, "E3664", {"start": v(33.16, 2.7) * mm, "end": v(33.1, 2.72) * mm});
            skLineSegment(sketch, "E3665", {"start": v(33.1, 2.72) * mm, "end": v(33.05, 2.73) * mm});
            skLineSegment(sketch, "E3666", {"start": v(33.05, 2.73) * mm, "end": v(33, 2.75) * mm});
            skLineSegment(sketch, "E3667", {"start": v(33, 2.75) * mm, "end": v(32.94, 2.76) * mm});
            skLineSegment(sketch, "E3668", {"start": v(32.94, 2.76) * mm, "end": v(32.88, 2.77) * mm});
            skLineSegment(sketch, "E3669", {"start": v(32.88, 2.77) * mm, "end": v(32.82, 2.77) * mm});
            skLineSegment(sketch, "E3670", {"start": v(32.82, 2.77) * mm, "end": v(32.77, 2.78) * mm});
            skLineSegment(sketch, "E3671", {"start": v(32.77, 2.78) * mm, "end": v(32.7, 2.79) * mm});
            skLineSegment(sketch, "E3672", {"start": v(32.7, 2.79) * mm, "end": v(32.64, 2.8) * mm});
            skLineSegment(sketch, "E3673", {"start": v(32.64, 2.8) * mm, "end": v(32.58, 2.8) * mm});
            skLineSegment(sketch, "E3674", {"start": v(32.58, 2.8) * mm, "end": v(32.52, 2.8) * mm});
            skLineSegment(sketch, "E3675", {"start": v(32.52, 2.8) * mm, "end": v(32.45, 2.8) * mm});
            skLineSegment(sketch, "E3676", {"start": v(32.45, 2.8) * mm, "end": v(32.4, 2.8) * mm});
            skLineSegment(sketch, "E3677", {"start": v(23.76, 13.74) * mm, "end": v(23.76, 13.75) * mm});
            skLineSegment(sketch, "E3678", {"start": v(23.76, 13.75) * mm, "end": v(23.76, 13.76) * mm});
            skLineSegment(sketch, "E3679", {"start": v(23.76, 13.76) * mm, "end": v(23.76, 13.78) * mm});
            skLineSegment(sketch, "E3680", {"start": v(23.76, 13.78) * mm, "end": v(23.76, 13.79) * mm});
            skLineSegment(sketch, "E3681", {"start": v(23.76, 13.79) * mm, "end": v(23.75, 13.8) * mm});
            skLineSegment(sketch, "E3682", {"start": v(23.75, 13.8) * mm, "end": v(23.75, 13.81) * mm});
            skLineSegment(sketch, "E3683", {"start": v(23.75, 13.81) * mm, "end": v(23.75, 13.83) * mm});
            skLineSegment(sketch, "E3684", {"start": v(23.75, 13.83) * mm, "end": v(23.74, 13.84) * mm});
            skLineSegment(sketch, "E3685", {"start": v(23.74, 13.84) * mm, "end": v(23.74, 13.85) * mm});
            skLineSegment(sketch, "E3686", {"start": v(23.74, 13.85) * mm, "end": v(23.73, 13.86) * mm});
            skLineSegment(sketch, "E3687", {"start": v(23.73, 13.86) * mm, "end": v(23.73, 13.88) * mm});
            skLineSegment(sketch, "E3688", {"start": v(23.73, 13.88) * mm, "end": v(23.72, 13.89) * mm});
            skLineSegment(sketch, "E3689", {"start": v(23.72, 13.89) * mm, "end": v(23.72, 13.9) * mm});
            skLineSegment(sketch, "E3690", {"start": v(23.72, 13.9) * mm, "end": v(23.7, 13.91) * mm});
            skLineSegment(sketch, "E3691", {"start": v(23.7, 13.91) * mm, "end": v(23.7, 13.93) * mm});
            skLineSegment(sketch, "E3692", {"start": v(23.7, 13.93) * mm, "end": v(23.7, 13.94) * mm});
            skLineSegment(sketch, "E3693", {"start": v(23.7, 13.94) * mm, "end": v(23.68, 13.95) * mm});
            skLineSegment(sketch, "E3694", {"start": v(23.68, 13.95) * mm, "end": v(23.67, 13.97) * mm});
            skLineSegment(sketch, "E3695", {"start": v(23.67, 13.97) * mm, "end": v(23.66, 13.98) * mm});
            skLineSegment(sketch, "E3696", {"start": v(23.66, 13.98) * mm, "end": v(23.65, 14) * mm});
            skLineSegment(sketch, "E3697", {"start": v(23.65, 14) * mm, "end": v(23.63, 14) * mm});
            skLineSegment(sketch, "E3698", {"start": v(23.63, 14) * mm, "end": v(23.62, 14.02) * mm});
            skLineSegment(sketch, "E3699", {"start": v(23.62, 14.02) * mm, "end": v(23.6, 14.03) * mm});
            skLineSegment(sketch, "E3700", {"start": v(23.6, 14.03) * mm, "end": v(23.6, 14.05) * mm});
            skLineSegment(sketch, "E3701", {"start": v(23.6, 14.05) * mm, "end": v(23.57, 14.06) * mm});
            skLineSegment(sketch, "E3702", {"start": v(23.57, 14.06) * mm, "end": v(23.56, 14.08) * mm});
            skLineSegment(sketch, "E3703", {"start": v(23.56, 14.08) * mm, "end": v(23.54, 14.1) * mm});
            skLineSegment(sketch, "E3704", {"start": v(23.54, 14.1) * mm, "end": v(23.52, 14.1) * mm});
            skLineSegment(sketch, "E3705", {"start": v(23.52, 14.1) * mm, "end": v(23.5, 14.12) * mm});
            skLineSegment(sketch, "E3706", {"start": v(23.5, 14.12) * mm, "end": v(23.48, 14.13) * mm});
            skLineSegment(sketch, "E3707", {"start": v(23.48, 14.13) * mm, "end": v(23.45, 14.15) * mm});
            skLineSegment(sketch, "E3708", {"start": v(23.45, 14.15) * mm, "end": v(23.43, 14.17) * mm});
            skLineSegment(sketch, "E3709", {"start": v(23.43, 14.17) * mm, "end": v(23.4, 14.18) * mm});
            skLineSegment(sketch, "E3710", {"start": v(23.4, 14.18) * mm, "end": v(23.38, 14.2) * mm});
            skLineSegment(sketch, "E3711", {"start": v(23.38, 14.2) * mm, "end": v(23.35, 14.21) * mm});
            skLineSegment(sketch, "E3712", {"start": v(23.35, 14.21) * mm, "end": v(23.32, 14.23) * mm});
            skLineSegment(sketch, "E3713", {"start": v(25.92, -6.72) * mm, "end": v(25.92, -6.21) * mm});
            skLineSegment(sketch, "E3714", {"start": v(26.98, -2.76) * mm, "end": v(27.02, -2.7) * mm});
            skLineSegment(sketch, "E3715", {"start": v(27.02, -2.7) * mm, "end": v(27.1, -2.59) * mm});
            skLineSegment(sketch, "E3716", {"start": v(27.1, -2.59) * mm, "end": v(27.17, -2.48) * mm});
            skLineSegment(sketch, "E3717", {"start": v(27.17, -2.48) * mm, "end": v(27.25, -2.37) * mm});
            skLineSegment(sketch, "E3718", {"start": v(27.25, -2.37) * mm, "end": v(27.33, -2.26) * mm});
            skLineSegment(sketch, "E3719", {"start": v(27.33, -2.26) * mm, "end": v(27.4, -2.16) * mm});
            skLineSegment(sketch, "E3720", {"start": v(27.4, -2.16) * mm, "end": v(27.48, -2.06) * mm});
            skLineSegment(sketch, "E3721", {"start": v(27.48, -2.06) * mm, "end": v(27.56, -1.96) * mm});
            skLineSegment(sketch, "E3722", {"start": v(27.56, -1.96) * mm, "end": v(27.64, -1.87) * mm});
            skLineSegment(sketch, "E3723", {"start": v(27.64, -1.87) * mm, "end": v(27.72, -1.77) * mm});
            skLineSegment(sketch, "E3724", {"start": v(27.72, -1.77) * mm, "end": v(27.8, -1.68) * mm});
            skLineSegment(sketch, "E3725", {"start": v(27.8, -1.68) * mm, "end": v(27.88, -1.6) * mm});
            skLineSegment(sketch, "E3726", {"start": v(27.88, -1.6) * mm, "end": v(27.96, -1.5) * mm});
            skLineSegment(sketch, "E3727", {"start": v(27.96, -1.5) * mm, "end": v(28.04, -1.43) * mm});
            skLineSegment(sketch, "E3728", {"start": v(28.04, -1.43) * mm, "end": v(28.12, -1.34) * mm});
            skLineSegment(sketch, "E3729", {"start": v(28.12, -1.34) * mm, "end": v(28.2, -1.26) * mm});
            skLineSegment(sketch, "E3730", {"start": v(28.2, -1.26) * mm, "end": v(28.28, -1.19) * mm});
            skLineSegment(sketch, "E3731", {"start": v(28.28, -1.19) * mm, "end": v(28.37, -1.1) * mm});
            skLineSegment(sketch, "E3732", {"start": v(28.37, -1.1) * mm, "end": v(28.45, -1.03) * mm});
            skLineSegment(sketch, "E3733", {"start": v(32.1, -7.52) * mm, "end": v(31.98, -7.61) * mm});
            skLineSegment(sketch, "E3734", {"start": v(31.98, -7.61) * mm, "end": v(31.85, -7.7) * mm});
            skLineSegment(sketch, "E3735", {"start": v(31.85, -7.7) * mm, "end": v(31.73, -7.78) * mm});
            skLineSegment(sketch, "E3736", {"start": v(31.73, -7.78) * mm, "end": v(31.6, -7.87) * mm});
            skLineSegment(sketch, "E3737", {"start": v(31.6, -7.87) * mm, "end": v(31.48, -7.95) * mm});
            skLineSegment(sketch, "E3738", {"start": v(31.48, -7.95) * mm, "end": v(31.36, -8.03) * mm});
            skLineSegment(sketch, "E3739", {"start": v(31.36, -8.03) * mm, "end": v(31.24, -8.1) * mm});
            skLineSegment(sketch, "E3740", {"start": v(31.24, -8.1) * mm, "end": v(31.11, -8.18) * mm});
            skLineSegment(sketch, "E3741", {"start": v(31.11, -8.18) * mm, "end": v(30.99, -8.25) * mm});
            skLineSegment(sketch, "E3742", {"start": v(30.99, -8.25) * mm, "end": v(30.86, -8.32) * mm});
            skLineSegment(sketch, "E3743", {"start": v(30.86, -8.32) * mm, "end": v(30.74, -8.39) * mm});
            skLineSegment(sketch, "E3744", {"start": v(30.74, -8.39) * mm, "end": v(30.6, -8.45) * mm});
            skLineSegment(sketch, "E3745", {"start": v(30.6, -8.45) * mm, "end": v(30.48, -8.52) * mm});
            skLineSegment(sketch, "E3746", {"start": v(30.48, -8.52) * mm, "end": v(30.35, -8.58) * mm});
            skLineSegment(sketch, "E3747", {"start": v(30.35, -8.58) * mm, "end": v(30.23, -8.64) * mm});
            skLineSegment(sketch, "E3748", {"start": v(30.23, -8.64) * mm, "end": v(30.1, -8.7) * mm});
            skLineSegment(sketch, "E3749", {"start": v(30.1, -8.7) * mm, "end": v(30.02, -8.74) * mm});
            skLineSegment(sketch, "E3750", {"start": v(23.32, 14.23) * mm, "end": v(23.29, 14.25) * mm});
            skLineSegment(sketch, "E3751", {"start": v(23.29, 14.25) * mm, "end": v(23.25, 14.26) * mm});
            skLineSegment(sketch, "E3752", {"start": v(23.25, 14.26) * mm, "end": v(23.21, 14.28) * mm});
            skLineSegment(sketch, "E3753", {"start": v(23.21, 14.28) * mm, "end": v(23.18, 14.3) * mm});
            skLineSegment(sketch, "E3754", {"start": v(23.18, 14.3) * mm, "end": v(23.14, 14.31) * mm});
            skLineSegment(sketch, "E3755", {"start": v(23.14, 14.31) * mm, "end": v(23.1, 14.33) * mm});
            skLineSegment(sketch, "E3756", {"start": v(23.1, 14.33) * mm, "end": v(23.05, 14.34) * mm});
            skLineSegment(sketch, "E3757", {"start": v(23.05, 14.34) * mm, "end": v(23, 14.36) * mm});
            skLineSegment(sketch, "E3758", {"start": v(23, 14.36) * mm, "end": v(22.96, 14.37) * mm});
            skLineSegment(sketch, "E3759", {"start": v(22.96, 14.37) * mm, "end": v(22.92, 14.39) * mm});
            skLineSegment(sketch, "E3760", {"start": v(22.92, 14.39) * mm, "end": v(22.87, 14.4) * mm});
            skLineSegment(sketch, "E3761", {"start": v(22.87, 14.4) * mm, "end": v(22.82, 14.41) * mm});
            skLineSegment(sketch, "E3762", {"start": v(22.82, 14.41) * mm, "end": v(22.77, 14.43) * mm});
            skLineSegment(sketch, "E3763", {"start": v(22.77, 14.43) * mm, "end": v(22.72, 14.44) * mm});
            skLineSegment(sketch, "E3764", {"start": v(22.72, 14.44) * mm, "end": v(22.67, 14.45) * mm});
            skLineSegment(sketch, "E3765", {"start": v(22.67, 14.45) * mm, "end": v(22.61, 14.46) * mm});
            skLineSegment(sketch, "E3766", {"start": v(22.61, 14.46) * mm, "end": v(22.56, 14.47) * mm});
            skLineSegment(sketch, "E3767", {"start": v(22.56, 14.47) * mm, "end": v(22.5, 14.48) * mm});
            skLineSegment(sketch, "E3768", {"start": v(22.5, 14.48) * mm, "end": v(22.44, 14.48) * mm});
            skLineSegment(sketch, "E3769", {"start": v(22.44, 14.48) * mm, "end": v(22.38, 14.5) * mm});
            skLineSegment(sketch, "E3770", {"start": v(22.38, 14.5) * mm, "end": v(22.32, 14.5) * mm});
            skLineSegment(sketch, "E3771", {"start": v(22.32, 14.5) * mm, "end": v(22.26, 14.5) * mm});
            skLineSegment(sketch, "E3772", {"start": v(22.26, 14.5) * mm, "end": v(22.21, 14.5) * mm});
            skLineSegment(sketch, "E3773", {"start": v(35.13, -10.72) * mm, "end": v(35.17, -10.8) * mm});
            skLineSegment(sketch, "E3774", {"start": v(35.17, -10.8) * mm, "end": v(35.22, -10.88) * mm});
            skLineSegment(sketch, "E3775", {"start": v(35.22, -10.88) * mm, "end": v(35.27, -10.96) * mm});
            skLineSegment(sketch, "E3776", {"start": v(35.27, -10.96) * mm, "end": v(35.32, -11.04) * mm});
            skLineSegment(sketch, "E3777", {"start": v(35.32, -11.04) * mm, "end": v(35.37, -11.11) * mm});
            skLineSegment(sketch, "E3778", {"start": v(35.37, -11.11) * mm, "end": v(35.42, -11.18) * mm});
            skLineSegment(sketch, "E3779", {"start": v(35.42, -11.18) * mm, "end": v(35.47, -11.25) * mm});
            skLineSegment(sketch, "E3780", {"start": v(35.47, -11.25) * mm, "end": v(35.52, -11.32) * mm});
            skLineSegment(sketch, "E3781", {"start": v(35.52, -11.32) * mm, "end": v(35.57, -11.38) * mm});
            skLineSegment(sketch, "E3782", {"start": v(35.57, -11.38) * mm, "end": v(35.62, -11.44) * mm});
            skLineSegment(sketch, "E3783", {"start": v(35.62, -11.44) * mm, "end": v(35.67, -11.5) * mm});
            skLineSegment(sketch, "E3784", {"start": v(35.67, -11.5) * mm, "end": v(35.72, -11.56) * mm});
            skLineSegment(sketch, "E3785", {"start": v(35.72, -11.56) * mm, "end": v(35.78, -11.61) * mm});
            skLineSegment(sketch, "E3786", {"start": v(35.78, -11.61) * mm, "end": v(35.83, -11.66) * mm});
            skLineSegment(sketch, "E3787", {"start": v(35.83, -11.66) * mm, "end": v(35.89, -11.71) * mm});
            skLineSegment(sketch, "E3788", {"start": v(35.89, -11.71) * mm, "end": v(35.94, -11.76) * mm});
            skLineSegment(sketch, "E3789", {"start": v(35.94, -11.76) * mm, "end": v(36, -11.8) * mm});
            skLineSegment(sketch, "E3790", {"start": v(36, -11.8) * mm, "end": v(36.05, -11.84) * mm});
            skLineSegment(sketch, "E3791", {"start": v(36.05, -11.84) * mm, "end": v(36.11, -11.88) * mm});
            skLineSegment(sketch, "E3792", {"start": v(36.11, -11.88) * mm, "end": v(36.17, -11.92) * mm});
            skLineSegment(sketch, "E3793", {"start": v(36.17, -11.92) * mm, "end": v(36.23, -11.95) * mm});
            skLineSegment(sketch, "E3794", {"start": v(36.23, -11.95) * mm, "end": v(36.28, -11.99) * mm});
            skLineSegment(sketch, "E3795", {"start": v(36.28, -11.99) * mm, "end": v(36.34, -12.02) * mm});
            skLineSegment(sketch, "E3796", {"start": v(36.34, -12.02) * mm, "end": v(36.4, -12.05) * mm});
            skLineSegment(sketch, "E3797", {"start": v(36.4, -12.05) * mm, "end": v(36.47, -12.07) * mm});
            skLineSegment(sketch, "E3798", {"start": v(36.47, -12.07) * mm, "end": v(36.53, -12.1) * mm});
            skLineSegment(sketch, "E3799", {"start": v(36.53, -12.1) * mm, "end": v(36.6, -12.12) * mm});
            skLineSegment(sketch, "E3800", {"start": v(36.6, -12.12) * mm, "end": v(36.66, -12.14) * mm});
            skLineSegment(sketch, "E3801", {"start": v(36.66, -12.14) * mm, "end": v(36.72, -12.16) * mm});
            skLineSegment(sketch, "E3802", {"start": v(36.72, -12.16) * mm, "end": v(36.79, -12.18) * mm});
            skLineSegment(sketch, "E3803", {"start": v(36.79, -12.18) * mm, "end": v(36.85, -12.2) * mm});
            skLineSegment(sketch, "E3804", {"start": v(36.85, -12.2) * mm, "end": v(36.92, -12.2) * mm});
            skLineSegment(sketch, "E3805", {"start": v(36.92, -12.2) * mm, "end": v(37, -12.22) * mm});
            skLineSegment(sketch, "E3806", {"start": v(37, -12.22) * mm, "end": v(37.06, -12.23) * mm});
            skLineSegment(sketch, "E3807", {"start": v(37.06, -12.23) * mm, "end": v(37.13, -12.24) * mm});
            skLineSegment(sketch, "E3808", {"start": v(37.13, -12.24) * mm, "end": v(37.2, -12.24) * mm});
            skLineSegment(sketch, "E3809", {"start": v(37.2, -12.24) * mm, "end": v(37.28, -12.24) * mm});
            skLineSegment(sketch, "E3810", {"start": v(37.28, -12.24) * mm, "end": v(37.36, -12.24) * mm});
            skLineSegment(sketch, "E3811", {"start": v(26.12, -4.92) * mm, "end": v(26.14, -4.83) * mm});
            skLineSegment(sketch, "E3812", {"start": v(26.14, -4.83) * mm, "end": v(26.16, -4.73) * mm});
            skLineSegment(sketch, "E3813", {"start": v(26.16, -4.73) * mm, "end": v(26.17, -4.64) * mm});
            skLineSegment(sketch, "E3814", {"start": v(26.17, -4.64) * mm, "end": v(26.2, -4.54) * mm});
            skLineSegment(sketch, "E3815", {"start": v(26.2, -4.54) * mm, "end": v(26.22, -4.45) * mm});
            skLineSegment(sketch, "E3816", {"start": v(26.22, -4.45) * mm, "end": v(26.24, -4.36) * mm});
            skLineSegment(sketch, "E3817", {"start": v(26.24, -4.36) * mm, "end": v(26.27, -4.26) * mm});
            skLineSegment(sketch, "E3818", {"start": v(26.27, -4.26) * mm, "end": v(26.3, -4.17) * mm});
            skLineSegment(sketch, "E3819", {"start": v(26.3, -4.17) * mm, "end": v(26.33, -4.08) * mm});
            skLineSegment(sketch, "E3820", {"start": v(26.33, -4.08) * mm, "end": v(26.36, -3.99) * mm});
            skLineSegment(sketch, "E3821", {"start": v(26.36, -3.99) * mm, "end": v(26.4, -3.9) * mm});
            skLineSegment(sketch, "E3822", {"start": v(26.4, -3.9) * mm, "end": v(26.43, -3.8) * mm});
            skLineSegment(sketch, "E3823", {"start": v(26.43, -3.8) * mm, "end": v(26.47, -3.7) * mm});
            skLineSegment(sketch, "E3824", {"start": v(26.47, -3.7) * mm, "end": v(26.5, -3.62) * mm});
            skLineSegment(sketch, "E3825", {"start": v(26.5, -3.62) * mm, "end": v(26.55, -3.52) * mm});
            skLineSegment(sketch, "E3826", {"start": v(26.55, -3.52) * mm, "end": v(26.6, -3.43) * mm});
            skLineSegment(sketch, "E3827", {"start": v(26.6, -3.43) * mm, "end": v(26.64, -3.34) * mm});
            skLineSegment(sketch, "E3828", {"start": v(26.64, -3.34) * mm, "end": v(26.69, -3.25) * mm});
            skLineSegment(sketch, "E3829", {"start": v(26.69, -3.25) * mm, "end": v(26.74, -3.16) * mm});
            skLineSegment(sketch, "E3830", {"start": v(26.74, -3.16) * mm, "end": v(26.8, -3.06) * mm});
            skLineSegment(sketch, "E3831", {"start": v(26.8, -3.06) * mm, "end": v(26.85, -2.97) * mm});
            skLineSegment(sketch, "E3832", {"start": v(26.85, -2.97) * mm, "end": v(26.9, -2.88) * mm});
            skLineSegment(sketch, "E3833", {"start": v(26.9, -2.88) * mm, "end": v(26.96, -2.78) * mm});
            skLineSegment(sketch, "E3834", {"start": v(26.96, -2.78) * mm, "end": v(26.98, -2.76) * mm});
            skLineSegment(sketch, "E3835", {"start": v(31.05, -1.23) * mm, "end": v(31, -1.31) * mm});
            skLineSegment(sketch, "E3836", {"start": v(31, -1.31) * mm, "end": v(30.94, -1.4) * mm});
            skLineSegment(sketch, "E3837", {"start": v(30.94, -1.4) * mm, "end": v(30.88, -1.48) * mm});
            skLineSegment(sketch, "E3838", {"start": v(30.88, -1.48) * mm, "end": v(30.81, -1.57) * mm});
            skLineSegment(sketch, "E3839", {"start": v(30.81, -1.57) * mm, "end": v(30.75, -1.66) * mm});
            skLineSegment(sketch, "E3840", {"start": v(30.75, -1.66) * mm, "end": v(30.67, -1.74) * mm});
            skLineSegment(sketch, "E3841", {"start": v(30.67, -1.74) * mm, "end": v(30.6, -1.84) * mm});
            skLineSegment(sketch, "E3842", {"start": v(30.6, -1.84) * mm, "end": v(30.52, -1.93) * mm});
            skLineSegment(sketch, "E3843", {"start": v(30.52, -1.93) * mm, "end": v(30.44, -2.02) * mm});
            skLineSegment(sketch, "E3844", {"start": v(30.44, -2.02) * mm, "end": v(30.35, -2.12) * mm});
            skLineSegment(sketch, "E3845", {"start": v(30.35, -2.12) * mm, "end": v(30.26, -2.22) * mm});
            skLineSegment(sketch, "E3846", {"start": v(30.26, -2.22) * mm, "end": v(30.16, -2.31) * mm});
            skLineSegment(sketch, "E3847", {"start": v(30.16, -2.31) * mm, "end": v(30.06, -2.42) * mm});
            skLineSegment(sketch, "E3848", {"start": v(30.06, -2.42) * mm, "end": v(29.95, -2.52) * mm});
            skLineSegment(sketch, "E3849", {"start": v(29.95, -2.52) * mm, "end": v(29.84, -2.62) * mm});
            skLineSegment(sketch, "E3850", {"start": v(29.84, -2.62) * mm, "end": v(29.72, -2.73) * mm});
            skLineSegment(sketch, "E3851", {"start": v(29.72, -2.73) * mm, "end": v(29.6, -2.84) * mm});
            skLineSegment(sketch, "E3852", {"start": v(29.6, -2.84) * mm, "end": v(29.48, -2.95) * mm});
            skLineSegment(sketch, "E3853", {"start": v(29.48, -2.95) * mm, "end": v(29.34, -3.06) * mm});
            skLineSegment(sketch, "E3854", {"start": v(29.34, -3.06) * mm, "end": v(29.2, -3.18) * mm});
            skLineSegment(sketch, "E3855", {"start": v(29.2, -3.18) * mm, "end": v(29.18, -3.2) * mm});
            skLineSegment(sketch, "E3856", {"start": v(33.48, -1.4) * mm, "end": v(33.52, -1.35) * mm});
            skLineSegment(sketch, "E3857", {"start": v(33.52, -1.35) * mm, "end": v(33.58, -1.26) * mm});
            skLineSegment(sketch, "E3858", {"start": v(33.58, -1.26) * mm, "end": v(33.65, -1.17) * mm});
            skLineSegment(sketch, "E3859", {"start": v(33.65, -1.17) * mm, "end": v(33.71, -1.07) * mm});
            skLineSegment(sketch, "E3860", {"start": v(33.71, -1.07) * mm, "end": v(33.77, -0.98) * mm});
            skLineSegment(sketch, "E3861", {"start": v(33.77, -0.98) * mm, "end": v(33.83, -0.9) * mm});
            skLineSegment(sketch, "E3862", {"start": v(33.83, -0.9) * mm, "end": v(33.88, -0.8) * mm});
            skLineSegment(sketch, "E3863", {"start": v(33.88, -0.8) * mm, "end": v(33.93, -0.7) * mm});
            skLineSegment(sketch, "E3864", {"start": v(33.93, -0.7) * mm, "end": v(33.98, -0.62) * mm});
            skLineSegment(sketch, "E3865", {"start": v(33.98, -0.62) * mm, "end": v(34.02, -0.53) * mm});
            skLineSegment(sketch, "E3866", {"start": v(34.02, -0.53) * mm, "end": v(34.06, -0.44) * mm});
            skLineSegment(sketch, "E3867", {"start": v(34.06, -0.44) * mm, "end": v(34.1, -0.35) * mm});
            skLineSegment(sketch, "E3868", {"start": v(34.1, -0.35) * mm, "end": v(34.14, -0.27) * mm});
            skLineSegment(sketch, "E3869", {"start": v(34.14, -0.27) * mm, "end": v(34.17, -0.18) * mm});
            skLineSegment(sketch, "E3870", {"start": v(34.17, -0.18) * mm, "end": v(34.2, -0.1) * mm});
            skLineSegment(sketch, "E3871", {"start": v(34.2, -0.1) * mm, "end": v(34.24, 0) * mm});
            skLineSegment(sketch, "E3872", {"start": v(34.24, 0) * mm, "end": v(34.26, 0.08) * mm});
            skLineSegment(sketch, "E3873", {"start": v(34.26, 0.08) * mm, "end": v(34.29, 0.17) * mm});
            skLineSegment(sketch, "E3874", {"start": v(34.29, 0.17) * mm, "end": v(34.31, 0.25) * mm});
            skLineSegment(sketch, "E3875", {"start": v(34.31, 0.25) * mm, "end": v(34.33, 0.34) * mm});
            skLineSegment(sketch, "E3876", {"start": v(34.33, 0.34) * mm, "end": v(34.35, 0.42) * mm});
            skLineSegment(sketch, "E3877", {"start": v(34.35, 0.42) * mm, "end": v(34.37, 0.5) * mm});
            skLineSegment(sketch, "E3878", {"start": v(34.37, 0.5) * mm, "end": v(34.38, 0.6) * mm});
            skLineSegment(sketch, "E3879", {"start": v(34.38, 0.6) * mm, "end": v(34.4, 0.68) * mm});
            skLineSegment(sketch, "E3880", {"start": v(34.4, 0.68) * mm, "end": v(34.4, 0.76) * mm});
            skLineSegment(sketch, "E3881", {"start": v(34.4, 0.76) * mm, "end": v(34.41, 0.84) * mm});
            skLineSegment(sketch, "E3882", {"start": v(34.41, 0.84) * mm, "end": v(34.42, 0.93) * mm});
            skLineSegment(sketch, "E3883", {"start": v(34.42, 0.93) * mm, "end": v(34.42, 1.01) * mm});
            skLineSegment(sketch, "E3884", {"start": v(34.42, 1.01) * mm, "end": v(34.42, 1.1) * mm});
            skLineSegment(sketch, "E3885", {"start": v(41.15, 8.8) * mm, "end": v(40.93, 8.52) * mm});
            skLineSegment(sketch, "E3886", {"start": v(40.93, 8.52) * mm, "end": v(40.7, 8.23) * mm});
            skLineSegment(sketch, "E3887", {"start": v(40.7, 8.23) * mm, "end": v(40.49, 7.94) * mm});
            skLineSegment(sketch, "E3888", {"start": v(40.49, 7.94) * mm, "end": v(40.26, 7.63) * mm});
            skLineSegment(sketch, "E3889", {"start": v(40.26, 7.63) * mm, "end": v(40.04, 7.32) * mm});
            skLineSegment(sketch, "E3890", {"start": v(40.04, 7.32) * mm, "end": v(39.81, 7) * mm});
            skLineSegment(sketch, "E3891", {"start": v(39.81, 7) * mm, "end": v(39.59, 6.66) * mm});
            skLineSegment(sketch, "E3892", {"start": v(39.59, 6.66) * mm, "end": v(39.36, 6.31) * mm});
            skLineSegment(sketch, "E3893", {"start": v(39.36, 6.31) * mm, "end": v(39.13, 5.96) * mm});
            skLineSegment(sketch, "E3894", {"start": v(39.13, 5.96) * mm, "end": v(38.9, 5.59) * mm});
            skLineSegment(sketch, "E3895", {"start": v(38.9, 5.59) * mm, "end": v(38.66, 5.2) * mm});
            skLineSegment(sketch, "E3896", {"start": v(38.66, 5.2) * mm, "end": v(38.42, 4.8) * mm});
            skLineSegment(sketch, "E3897", {"start": v(38.42, 4.8) * mm, "end": v(38.18, 4.4) * mm});
            skLineSegment(sketch, "E3898", {"start": v(38.18, 4.4) * mm, "end": v(37.94, 3.98) * mm});
            skLineSegment(sketch, "E3899", {"start": v(37.94, 3.98) * mm, "end": v(37.83, 3.8) * mm});
            skLineSegment(sketch, "E3900", {"start": v(34.62, -5.5) * mm, "end": v(34.33, -5.74) * mm});
            skLineSegment(sketch, "E3901", {"start": v(34.33, -5.74) * mm, "end": v(34.04, -5.99) * mm});
            skLineSegment(sketch, "E3902", {"start": v(34.04, -5.99) * mm, "end": v(33.76, -6.22) * mm});
            skLineSegment(sketch, "E3903", {"start": v(33.76, -6.22) * mm, "end": v(33.5, -6.43) * mm});
            skLineSegment(sketch, "E3904", {"start": v(33.5, -6.43) * mm, "end": v(33.24, -6.64) * mm});
            skLineSegment(sketch, "E3905", {"start": v(33.24, -6.64) * mm, "end": v(33, -6.84) * mm});
            skLineSegment(sketch, "E3906", {"start": v(33, -6.84) * mm, "end": v(32.75, -7.03) * mm});
            skLineSegment(sketch, "E3907", {"start": v(32.75, -7.03) * mm, "end": v(32.52, -7.2) * mm});
            skLineSegment(sketch, "E3908", {"start": v(32.52, -7.2) * mm, "end": v(32.3, -7.37) * mm});
            skLineSegment(sketch, "E3909", {"start": v(32.3, -7.37) * mm, "end": v(32.1, -7.52) * mm});
            skLineSegment(sketch, "E3910", {"start": v(30.4, -10.85) * mm, "end": v(30.6, -10.7) * mm});
            skLineSegment(sketch, "E3911", {"start": v(30.6, -10.7) * mm, "end": v(30.8, -10.55) * mm});
            skLineSegment(sketch, "E3912", {"start": v(30.8, -10.55) * mm, "end": v(31.01, -10.39) * mm});
            skLineSegment(sketch, "E3913", {"start": v(31.01, -10.39) * mm, "end": v(31.22, -10.21) * mm});
            skLineSegment(sketch, "E3914", {"start": v(31.22, -10.21) * mm, "end": v(31.43, -10.03) * mm});
            skLineSegment(sketch, "E3915", {"start": v(31.43, -10.03) * mm, "end": v(31.65, -9.84) * mm});
            skLineSegment(sketch, "E3916", {"start": v(31.65, -9.84) * mm, "end": v(31.88, -9.64) * mm});
            skLineSegment(sketch, "E3917", {"start": v(31.88, -9.64) * mm, "end": v(32.1, -9.42) * mm});
            skLineSegment(sketch, "E3918", {"start": v(32.1, -9.42) * mm, "end": v(32.34, -9.2) * mm});
            skLineSegment(sketch, "E3919", {"start": v(32.34, -9.2) * mm, "end": v(32.58, -8.96) * mm});
            skLineSegment(sketch, "E3920", {"start": v(32.58, -8.96) * mm, "end": v(32.83, -8.7) * mm});
            skLineSegment(sketch, "E3921", {"start": v(32.83, -8.7) * mm, "end": v(33.08, -8.45) * mm});
            skLineSegment(sketch, "E3922", {"start": v(33.08, -8.45) * mm, "end": v(33.34, -8.17) * mm});
            skLineSegment(sketch, "E3923", {"start": v(33.34, -8.17) * mm, "end": v(33.6, -7.88) * mm});
            skLineSegment(sketch, "E3924", {"start": v(33.6, -7.88) * mm, "end": v(33.88, -7.57) * mm});
            skLineSegment(sketch, "E3925", {"start": v(33.88, -7.57) * mm, "end": v(34.16, -7.25) * mm});
            skLineSegment(sketch, "E3926", {"start": v(34.16, -7.25) * mm, "end": v(34.45, -6.9) * mm});
            skLineSegment(sketch, "E3927", {"start": v(34.45, -6.9) * mm, "end": v(34.62, -6.7) * mm});
            skLineSegment(sketch, "E3928", {"start": v(37.81, -8.12) * mm, "end": v(37.77, -8.06) * mm});
            skLineSegment(sketch, "E3929", {"start": v(37.77, -8.06) * mm, "end": v(37.74, -8) * mm});
            skLineSegment(sketch, "E3930", {"start": v(37.74, -8) * mm, "end": v(37.7, -7.95) * mm});
            skLineSegment(sketch, "E3931", {"start": v(37.7, -7.95) * mm, "end": v(37.67, -7.9) * mm});
            skLineSegment(sketch, "E3932", {"start": v(37.67, -7.9) * mm, "end": v(37.64, -7.83) * mm});
            skLineSegment(sketch, "E3933", {"start": v(37.64, -7.83) * mm, "end": v(37.61, -7.77) * mm});
            skLineSegment(sketch, "E3934", {"start": v(37.61, -7.77) * mm, "end": v(37.58, -7.71) * mm});
            skLineSegment(sketch, "E3935", {"start": v(37.58, -7.71) * mm, "end": v(37.56, -7.65) * mm});
            skLineSegment(sketch, "E3936", {"start": v(37.56, -7.65) * mm, "end": v(37.53, -7.58) * mm});
            skLineSegment(sketch, "E3937", {"start": v(37.53, -7.58) * mm, "end": v(37.5, -7.51) * mm});
            skLineSegment(sketch, "E3938", {"start": v(37.5, -7.51) * mm, "end": v(37.48, -7.44) * mm});
            skLineSegment(sketch, "E3939", {"start": v(37.48, -7.44) * mm, "end": v(37.46, -7.37) * mm});
            skLineSegment(sketch, "E3940", {"start": v(37.46, -7.37) * mm, "end": v(37.44, -7.3) * mm});
            skLineSegment(sketch, "E3941", {"start": v(37.44, -7.3) * mm, "end": v(37.42, -7.23) * mm});
            skLineSegment(sketch, "E3942", {"start": v(37.42, -7.23) * mm, "end": v(37.4, -7.15) * mm});
            skLineSegment(sketch, "E3943", {"start": v(37.4, -7.15) * mm, "end": v(37.38, -7.07) * mm});
            skLineSegment(sketch, "E3944", {"start": v(37.38, -7.07) * mm, "end": v(37.36, -7) * mm});
            skLineSegment(sketch, "E3945", {"start": v(37.36, -7) * mm, "end": v(37.35, -6.91) * mm});
            skLineSegment(sketch, "E3946", {"start": v(37.35, -6.91) * mm, "end": v(37.33, -6.83) * mm});
            skLineSegment(sketch, "E3947", {"start": v(37.33, -6.83) * mm, "end": v(37.32, -6.74) * mm});
            skLineSegment(sketch, "E3948", {"start": v(37.32, -6.74) * mm, "end": v(37.31, -6.65) * mm});
            skLineSegment(sketch, "E3949", {"start": v(37.31, -6.65) * mm, "end": v(37.3, -6.56) * mm});
            skLineSegment(sketch, "E3950", {"start": v(37.3, -6.56) * mm, "end": v(37.3, -6.47) * mm});
            skLineSegment(sketch, "E3951", {"start": v(37.3, -6.47) * mm, "end": v(37.29, -6.38) * mm});
            skLineSegment(sketch, "E3952", {"start": v(37.29, -6.38) * mm, "end": v(37.28, -6.28) * mm});
            skLineSegment(sketch, "E3953", {"start": v(37.28, -6.28) * mm, "end": v(37.28, -6.19) * mm});
            skLineSegment(sketch, "E3954", {"start": v(37.28, -6.19) * mm, "end": v(37.28, -6.09) * mm});
            skLineSegment(sketch, "E3955", {"start": v(37.28, -6.09) * mm, "end": v(37.28, -6.05) * mm});
            skLineSegment(sketch, "E3956", {"start": v(31.66, 0.16) * mm, "end": v(31.66, 0.13) * mm});
            skLineSegment(sketch, "E3957", {"start": v(31.66, 0.13) * mm, "end": v(31.66, 0.1) * mm});
            skLineSegment(sketch, "E3958", {"start": v(31.66, 0.1) * mm, "end": v(31.66, 0.07) * mm});
            skLineSegment(sketch, "E3959", {"start": v(31.66, 0.07) * mm, "end": v(31.65, 0.04) * mm});
            skLineSegment(sketch, "E3960", {"start": v(31.65, 0.04) * mm, "end": v(31.64, 0) * mm});
            skLineSegment(sketch, "E3961", {"start": v(31.64, 0) * mm, "end": v(31.64, -0.03) * mm});
            skLineSegment(sketch, "E3962", {"start": v(31.64, -0.03) * mm, "end": v(31.63, -0.07) * mm});
            skLineSegment(sketch, "E3963", {"start": v(31.63, -0.07) * mm, "end": v(31.62, -0.1) * mm});
            skLineSegment(sketch, "E3964", {"start": v(31.62, -0.1) * mm, "end": v(31.6, -0.15) * mm});
            skLineSegment(sketch, "E3965", {"start": v(31.6, -0.15) * mm, "end": v(31.59, -0.2) * mm});
            skLineSegment(sketch, "E3966", {"start": v(31.59, -0.2) * mm, "end": v(31.57, -0.24) * mm});
            skLineSegment(sketch, "E3967", {"start": v(31.57, -0.24) * mm, "end": v(31.55, -0.3) * mm});
            skLineSegment(sketch, "E3968", {"start": v(31.55, -0.3) * mm, "end": v(31.53, -0.34) * mm});
            skLineSegment(sketch, "E3969", {"start": v(31.53, -0.34) * mm, "end": v(31.5, -0.4) * mm});
            skLineSegment(sketch, "E3970", {"start": v(31.5, -0.4) * mm, "end": v(31.48, -0.46) * mm});
            skLineSegment(sketch, "E3971", {"start": v(31.48, -0.46) * mm, "end": v(31.45, -0.52) * mm});
            skLineSegment(sketch, "E3972", {"start": v(31.45, -0.52) * mm, "end": v(31.41, -0.59) * mm});
            skLineSegment(sketch, "E3973", {"start": v(31.41, -0.59) * mm, "end": v(31.38, -0.66) * mm});
            skLineSegment(sketch, "E3974", {"start": v(31.38, -0.66) * mm, "end": v(31.34, -0.74) * mm});
            skLineSegment(sketch, "E3975", {"start": v(31.34, -0.74) * mm, "end": v(31.3, -0.82) * mm});
            skLineSegment(sketch, "E3976", {"start": v(31.3, -0.82) * mm, "end": v(31.24, -0.9) * mm});
            skLineSegment(sketch, "E3977", {"start": v(31.24, -0.9) * mm, "end": v(31.19, -1) * mm});
            skLineSegment(sketch, "E3978", {"start": v(31.19, -1) * mm, "end": v(31.13, -1.1) * mm});
            skLineSegment(sketch, "E3979", {"start": v(31.13, -1.1) * mm, "end": v(31.06, -1.2) * mm});
            skLineSegment(sketch, "E3980", {"start": v(31.06, -1.2) * mm, "end": v(31.05, -1.23) * mm});
            skLineSegment(sketch, "E3981", {"start": v(37.83, 3.8) * mm, "end": v(37.63, 3.43) * mm});
            skLineSegment(sketch, "E3982", {"start": v(37.63, 3.43) * mm, "end": v(37.43, 3.06) * mm});
            skLineSegment(sketch, "E3983", {"start": v(37.43, 3.06) * mm, "end": v(37.24, 2.69) * mm});
            skLineSegment(sketch, "E3984", {"start": v(37.24, 2.69) * mm, "end": v(37.05, 2.32) * mm});
            skLineSegment(sketch, "E3985", {"start": v(37.05, 2.32) * mm, "end": v(36.87, 1.95) * mm});
            skLineSegment(sketch, "E3986", {"start": v(36.87, 1.95) * mm, "end": v(36.69, 1.58) * mm});
            skLineSegment(sketch, "E3987", {"start": v(36.69, 1.58) * mm, "end": v(36.52, 1.2) * mm});
            skLineSegment(sketch, "E3988", {"start": v(36.52, 1.2) * mm, "end": v(36.35, 0.83) * mm});
            skLineSegment(sketch, "E3989", {"start": v(36.35, 0.83) * mm, "end": v(36.19, 0.46) * mm});
            skLineSegment(sketch, "E3990", {"start": v(36.19, 0.46) * mm, "end": v(36.03, 0.09) * mm});
            skLineSegment(sketch, "E3991", {"start": v(36.03, 0.09) * mm, "end": v(35.88, -0.28) * mm});
            skLineSegment(sketch, "E3992", {"start": v(35.88, -0.28) * mm, "end": v(35.73, -0.66) * mm});
            skLineSegment(sketch, "E3993", {"start": v(35.73, -0.66) * mm, "end": v(35.59, -1.03) * mm});
            skLineSegment(sketch, "E3994", {"start": v(35.59, -1.03) * mm, "end": v(35.45, -1.4) * mm});
            skLineSegment(sketch, "E3995", {"start": v(35.45, -1.4) * mm, "end": v(35.32, -1.78) * mm});
            skLineSegment(sketch, "E3996", {"start": v(35.32, -1.78) * mm, "end": v(35.28, -1.9) * mm});
            skLineSegment(sketch, "E3997", {"start": v(40.16, 0.6) * mm, "end": v(40.04, 0.43) * mm});
            skLineSegment(sketch, "E3998", {"start": v(40.04, 0.43) * mm, "end": v(39.9, 0.26) * mm});
            skLineSegment(sketch, "E3999", {"start": v(39.9, 0.26) * mm, "end": v(39.78, 0.1) * mm});
            skLineSegment(sketch, "E4000", {"start": v(39.78, 0.1) * mm, "end": v(39.65, -0.07) * mm});
            skLineSegment(sketch, "E4001", {"start": v(39.65, -0.07) * mm, "end": v(39.51, -0.24) * mm});
            skLineSegment(sketch, "E4002", {"start": v(39.51, -0.24) * mm, "end": v(39.38, -0.4) * mm});
            skLineSegment(sketch, "E4003", {"start": v(39.38, -0.4) * mm, "end": v(39.23, -0.56) * mm});
            skLineSegment(sketch, "E4004", {"start": v(39.23, -0.56) * mm, "end": v(39.1, -0.73) * mm});
            skLineSegment(sketch, "E4005", {"start": v(39.1, -0.73) * mm, "end": v(38.94, -0.9) * mm});
            skLineSegment(sketch, "E4006", {"start": v(38.94, -0.9) * mm, "end": v(38.8, -1.06) * mm});
            skLineSegment(sketch, "E4007", {"start": v(38.8, -1.06) * mm, "end": v(38.64, -1.22) * mm});
            skLineSegment(sketch, "E4008", {"start": v(38.64, -1.22) * mm, "end": v(38.48, -1.39) * mm});
            skLineSegment(sketch, "E4009", {"start": v(38.48, -1.39) * mm, "end": v(38.32, -1.56) * mm});
            skLineSegment(sketch, "E4010", {"start": v(38.32, -1.56) * mm, "end": v(38.17, -1.7) * mm});
            skLineSegment(sketch, "E4011", {"start": v(37.48, -4.46) * mm, "end": v(37.85, -4.07) * mm});
            skLineSegment(sketch, "E4012", {"start": v(37.85, -4.07) * mm, "end": v(38.3, -3.58) * mm});
            skLineSegment(sketch, "E4013", {"start": v(38.3, -3.58) * mm, "end": v(38.74, -3.1) * mm});
            skLineSegment(sketch, "E4014", {"start": v(38.74, -3.1) * mm, "end": v(39.17, -2.61) * mm});
            skLineSegment(sketch, "E4015", {"start": v(39.17, -2.61) * mm, "end": v(39.58, -2.13) * mm});
            skLineSegment(sketch, "E4016", {"start": v(39.58, -2.13) * mm, "end": v(39.98, -1.66) * mm});
            skLineSegment(sketch, "E4017", {"start": v(39.98, -1.66) * mm, "end": v(40.36, -1.2) * mm});
            skLineSegment(sketch, "E4018", {"start": v(40.36, -1.2) * mm, "end": v(40.73, -0.72) * mm});
            skLineSegment(sketch, "E4019", {"start": v(40.73, -0.72) * mm, "end": v(41.08, -0.26) * mm});
            skLineSegment(sketch, "E4020", {"start": v(41.08, -0.26) * mm, "end": v(41.43, 0.2) * mm});
            skLineSegment(sketch, "E4021", {"start": v(41.43, 0.2) * mm, "end": v(41.76, 0.65) * mm});
            skLineSegment(sketch, "E4022", {"start": v(41.76, 0.65) * mm, "end": v(42.07, 1.1) * mm});
            skLineSegment(sketch, "E4023", {"start": v(42.07, 1.1) * mm, "end": v(42.38, 1.55) * mm});
            skLineSegment(sketch, "E4024", {"start": v(42.38, 1.55) * mm, "end": v(42.67, 2) * mm});
            skLineSegment(sketch, "E4025", {"start": v(42.67, 2) * mm, "end": v(42.95, 2.44) * mm});
            skLineSegment(sketch, "E4026", {"start": v(42.95, 2.44) * mm, "end": v(43.22, 2.87) * mm});
            skLineSegment(sketch, "E4027", {"start": v(43.22, 2.87) * mm, "end": v(43.48, 3.3) * mm});
            skLineSegment(sketch, "E4028", {"start": v(43.48, 3.3) * mm, "end": v(43.72, 3.74) * mm});
            skLineSegment(sketch, "E4029", {"start": v(40.41, -8.53) * mm, "end": v(40.4, -8.53) * mm});
            skLineSegment(sketch, "E4030", {"start": v(40.4, -8.53) * mm, "end": v(40.36, -8.56) * mm});
            skLineSegment(sketch, "E4031", {"start": v(40.36, -8.56) * mm, "end": v(40.32, -8.59) * mm});
            skLineSegment(sketch, "E4032", {"start": v(40.32, -8.59) * mm, "end": v(40.27, -8.62) * mm});
            skLineSegment(sketch, "E4033", {"start": v(40.27, -8.62) * mm, "end": v(40.23, -8.64) * mm});
            skLineSegment(sketch, "E4034", {"start": v(40.23, -8.64) * mm, "end": v(40.19, -8.67) * mm});
            skLineSegment(sketch, "E4035", {"start": v(40.19, -8.67) * mm, "end": v(40.14, -8.69) * mm});
            skLineSegment(sketch, "E4036", {"start": v(40.14, -8.69) * mm, "end": v(40.1, -8.71) * mm});
            skLineSegment(sketch, "E4037", {"start": v(40.1, -8.71) * mm, "end": v(40.06, -8.73) * mm});
            skLineSegment(sketch, "E4038", {"start": v(40.06, -8.73) * mm, "end": v(40.02, -8.75) * mm});
            skLineSegment(sketch, "E4039", {"start": v(40.02, -8.75) * mm, "end": v(39.98, -8.77) * mm});
            skLineSegment(sketch, "E4040", {"start": v(39.98, -8.77) * mm, "end": v(39.93, -8.79) * mm});
            skLineSegment(sketch, "E4041", {"start": v(39.93, -8.79) * mm, "end": v(39.9, -8.8) * mm});
            skLineSegment(sketch, "E4042", {"start": v(39.9, -8.8) * mm, "end": v(39.85, -8.82) * mm});
            skLineSegment(sketch, "E4043", {"start": v(39.85, -8.82) * mm, "end": v(39.82, -8.83) * mm});
            skLineSegment(sketch, "E4044", {"start": v(39.82, -8.83) * mm, "end": v(39.78, -8.84) * mm});
            skLineSegment(sketch, "E4045", {"start": v(39.78, -8.84) * mm, "end": v(39.74, -8.85) * mm});
            skLineSegment(sketch, "E4046", {"start": v(39.74, -8.85) * mm, "end": v(39.7, -8.86) * mm});
            skLineSegment(sketch, "E4047", {"start": v(39.7, -8.86) * mm, "end": v(39.66, -8.87) * mm});
            skLineSegment(sketch, "E4048", {"start": v(39.66, -8.87) * mm, "end": v(39.63, -8.88) * mm});
            skLineSegment(sketch, "E4049", {"start": v(39.63, -8.88) * mm, "end": v(39.59, -8.89) * mm});
            skLineSegment(sketch, "E4050", {"start": v(39.59, -8.89) * mm, "end": v(39.55, -8.9) * mm});
            skLineSegment(sketch, "E4051", {"start": v(39.55, -8.9) * mm, "end": v(39.52, -8.9) * mm});
            skLineSegment(sketch, "E4052", {"start": v(39.52, -8.9) * mm, "end": v(39.48, -8.9) * mm});
            skLineSegment(sketch, "E4053", {"start": v(39.48, -8.9) * mm, "end": v(39.45, -8.9) * mm});
            skLineSegment(sketch, "E4054", {"start": v(39.45, -8.9) * mm, "end": v(39.41, -8.9) * mm});
            skLineSegment(sketch, "E4055", {"start": v(39.41, -8.9) * mm, "end": v(39.38, -8.9) * mm});
            skLineSegment(sketch, "E4056", {"start": v(39.38, -8.9) * mm, "end": v(39.34, -8.9) * mm});
            skLineSegment(sketch, "E4057", {"start": v(34.42, 1.1) * mm, "end": v(34.42, 1.1) * mm});
            skLineSegment(sketch, "E4058", {"start": v(34.42, 1.1) * mm, "end": v(34.42, 1.16) * mm});
            skLineSegment(sketch, "E4059", {"start": v(34.42, 1.16) * mm, "end": v(34.42, 1.2) * mm});
            skLineSegment(sketch, "E4060", {"start": v(34.42, 1.2) * mm, "end": v(34.41, 1.26) * mm});
            skLineSegment(sketch, "E4061", {"start": v(34.41, 1.26) * mm, "end": v(34.41, 1.3) * mm});
            skLineSegment(sketch, "E4062", {"start": v(34.41, 1.3) * mm, "end": v(34.4, 1.35) * mm});
            skLineSegment(sketch, "E4063", {"start": v(34.4, 1.35) * mm, "end": v(34.4, 1.4) * mm});
            skLineSegment(sketch, "E4064", {"start": v(34.4, 1.4) * mm, "end": v(34.4, 1.44) * mm});
            skLineSegment(sketch, "E4065", {"start": v(34.4, 1.44) * mm, "end": v(34.38, 1.49) * mm});
            skLineSegment(sketch, "E4066", {"start": v(34.38, 1.49) * mm, "end": v(34.38, 1.53) * mm});
            skLineSegment(sketch, "E4067", {"start": v(34.38, 1.53) * mm, "end": v(34.37, 1.57) * mm});
            skLineSegment(sketch, "E4068", {"start": v(34.37, 1.57) * mm, "end": v(34.35, 1.61) * mm});
            skLineSegment(sketch, "E4069", {"start": v(34.35, 1.61) * mm, "end": v(34.34, 1.65) * mm});
            skLineSegment(sketch, "E4070", {"start": v(34.34, 1.65) * mm, "end": v(34.33, 1.7) * mm});
            skLineSegment(sketch, "E4071", {"start": v(34.33, 1.7) * mm, "end": v(34.32, 1.73) * mm});
            skLineSegment(sketch, "E4072", {"start": v(34.32, 1.73) * mm, "end": v(34.3, 1.77) * mm});
            skLineSegment(sketch, "E4073", {"start": v(34.3, 1.77) * mm, "end": v(34.29, 1.81) * mm});
            skLineSegment(sketch, "E4074", {"start": v(34.29, 1.81) * mm, "end": v(34.27, 1.85) * mm});
            skLineSegment(sketch, "E4075", {"start": v(34.27, 1.85) * mm, "end": v(34.25, 1.89) * mm});
            skLineSegment(sketch, "E4076", {"start": v(34.25, 1.89) * mm, "end": v(34.23, 1.92) * mm});
            skLineSegment(sketch, "E4077", {"start": v(34.23, 1.92) * mm, "end": v(34.22, 1.96) * mm});
            skLineSegment(sketch, "E4078", {"start": v(34.22, 1.96) * mm, "end": v(34.2, 1.99) * mm});
            skLineSegment(sketch, "E4079", {"start": v(34.2, 1.99) * mm, "end": v(34.18, 2.02) * mm});
            skLineSegment(sketch, "E4080", {"start": v(34.18, 2.02) * mm, "end": v(34.15, 2.06) * mm});
            skLineSegment(sketch, "E4081", {"start": v(34.15, 2.06) * mm, "end": v(34.13, 2.09) * mm});
            skLineSegment(sketch, "E4082", {"start": v(34.13, 2.09) * mm, "end": v(34.1, 2.12) * mm});
            skLineSegment(sketch, "E4083", {"start": v(34.1, 2.12) * mm, "end": v(34.09, 2.15) * mm});
            skLineSegment(sketch, "E4084", {"start": v(34.09, 2.15) * mm, "end": v(34.06, 2.18) * mm});
            skLineSegment(sketch, "E4085", {"start": v(34.06, 2.18) * mm, "end": v(34.05, 2.2) * mm});
            skLineSegment(sketch, "E4086", {"start": v(34.05, 2.2) * mm, "end": v(34.03, 2.2) * mm});
            skLineSegment(sketch, "E4087", {"start": v(34.03, 2.2) * mm, "end": v(34, 2.24) * mm});
            skLineSegment(sketch, "E4088", {"start": v(34, 2.24) * mm, "end": v(33.98, 2.26) * mm});
            skLineSegment(sketch, "E4089", {"start": v(33.98, 2.26) * mm, "end": v(33.95, 2.29) * mm});
            skLineSegment(sketch, "E4090", {"start": v(33.95, 2.29) * mm, "end": v(33.92, 2.32) * mm});
            skLineSegment(sketch, "E4091", {"start": v(33.92, 2.32) * mm, "end": v(33.9, 2.34) * mm});
            skLineSegment(sketch, "E4092", {"start": v(33.9, 2.34) * mm, "end": v(33.86, 2.37) * mm});
            skLineSegment(sketch, "E4093", {"start": v(34.34, -6.67) * mm, "end": v(34.34, -6.75) * mm});
            skLineSegment(sketch, "E4094", {"start": v(34.34, -6.75) * mm, "end": v(34.34, -6.97) * mm});
            skLineSegment(sketch, "E4095", {"start": v(34.34, -6.97) * mm, "end": v(34.35, -7.19) * mm});
            skLineSegment(sketch, "E4096", {"start": v(34.35, -7.19) * mm, "end": v(34.36, -7.4) * mm});
            skLineSegment(sketch, "E4097", {"start": v(34.36, -7.4) * mm, "end": v(34.37, -7.6) * mm});
            skLineSegment(sketch, "E4098", {"start": v(34.37, -7.6) * mm, "end": v(34.39, -7.8) * mm});
            skLineSegment(sketch, "E4099", {"start": v(34.39, -7.8) * mm, "end": v(34.4, -8) * mm});
            skLineSegment(sketch, "E4100", {"start": v(34.4, -8) * mm, "end": v(34.42, -8.2) * mm});
            skLineSegment(sketch, "E4101", {"start": v(34.42, -8.2) * mm, "end": v(34.45, -8.38) * mm});
            skLineSegment(sketch, "E4102", {"start": v(34.45, -8.38) * mm, "end": v(34.47, -8.56) * mm});
            skLineSegment(sketch, "E4103", {"start": v(34.47, -8.56) * mm, "end": v(34.5, -8.73) * mm});
            skLineSegment(sketch, "E4104", {"start": v(34.5, -8.73) * mm, "end": v(34.53, -8.9) * mm});
            skLineSegment(sketch, "E4105", {"start": v(34.53, -8.9) * mm, "end": v(34.56, -9.06) * mm});
            skLineSegment(sketch, "E4106", {"start": v(34.56, -9.06) * mm, "end": v(34.6, -9.22) * mm});
            skLineSegment(sketch, "E4107", {"start": v(34.6, -9.22) * mm, "end": v(34.64, -9.38) * mm});
            skLineSegment(sketch, "E4108", {"start": v(34.64, -9.38) * mm, "end": v(34.68, -9.53) * mm});
            skLineSegment(sketch, "E4109", {"start": v(34.68, -9.53) * mm, "end": v(34.72, -9.68) * mm});
            skLineSegment(sketch, "E4110", {"start": v(34.72, -9.68) * mm, "end": v(34.76, -9.82) * mm});
            skLineSegment(sketch, "E4111", {"start": v(34.76, -9.82) * mm, "end": v(34.81, -9.96) * mm});
            skLineSegment(sketch, "E4112", {"start": v(34.81, -9.96) * mm, "end": v(34.86, -10.1) * mm});
            skLineSegment(sketch, "E4113", {"start": v(34.86, -10.1) * mm, "end": v(34.91, -10.23) * mm});
            skLineSegment(sketch, "E4114", {"start": v(34.91, -10.23) * mm, "end": v(34.96, -10.35) * mm});
            skLineSegment(sketch, "E4115", {"start": v(34.96, -10.35) * mm, "end": v(35.02, -10.48) * mm});
            skLineSegment(sketch, "E4116", {"start": v(35.02, -10.48) * mm, "end": v(35.08, -10.6) * mm});
            skLineSegment(sketch, "E4117", {"start": v(35.08, -10.6) * mm, "end": v(35.13, -10.72) * mm});
            skLineSegment(sketch, "E4118", {"start": v(34.62, -6.7) * mm, "end": v(34.62, -5.5) * mm});
            skLineSegment(sketch, "E4119", {"start": v(35.28, -1.9) * mm, "end": v(35.18, -2.2) * mm});
            skLineSegment(sketch, "E4120", {"start": v(35.18, -2.2) * mm, "end": v(35.09, -2.5) * mm});
            skLineSegment(sketch, "E4121", {"start": v(35.09, -2.5) * mm, "end": v(35, -2.78) * mm});
            skLineSegment(sketch, "E4122", {"start": v(35, -2.78) * mm, "end": v(34.92, -3.06) * mm});
            skLineSegment(sketch, "E4123", {"start": v(34.92, -3.06) * mm, "end": v(34.84, -3.34) * mm});
            skLineSegment(sketch, "E4124", {"start": v(34.84, -3.34) * mm, "end": v(34.77, -3.6) * mm});
            skLineSegment(sketch, "E4125", {"start": v(34.77, -3.6) * mm, "end": v(34.71, -3.86) * mm});
            skLineSegment(sketch, "E4126", {"start": v(34.71, -3.86) * mm, "end": v(34.65, -4.11) * mm});
            skLineSegment(sketch, "E4127", {"start": v(34.65, -4.11) * mm, "end": v(34.6, -4.35) * mm});
            skLineSegment(sketch, "E4128", {"start": v(34.6, -4.35) * mm, "end": v(34.55, -4.6) * mm});
            skLineSegment(sketch, "E4129", {"start": v(34.55, -4.6) * mm, "end": v(34.51, -4.82) * mm});
            skLineSegment(sketch, "E4130", {"start": v(34.51, -4.82) * mm, "end": v(34.47, -5.05) * mm});
            skLineSegment(sketch, "E4131", {"start": v(34.47, -5.05) * mm, "end": v(34.44, -5.27) * mm});
            skLineSegment(sketch, "E4132", {"start": v(34.44, -5.27) * mm, "end": v(34.41, -5.49) * mm});
            skLineSegment(sketch, "E4133", {"start": v(34.41, -5.49) * mm, "end": v(34.4, -5.7) * mm});
            skLineSegment(sketch, "E4134", {"start": v(34.4, -5.7) * mm, "end": v(34.37, -5.9) * mm});
            skLineSegment(sketch, "E4135", {"start": v(34.37, -5.9) * mm, "end": v(34.36, -6.1) * mm});
            skLineSegment(sketch, "E4136", {"start": v(34.36, -6.1) * mm, "end": v(34.35, -6.3) * mm});
            skLineSegment(sketch, "E4137", {"start": v(34.35, -6.3) * mm, "end": v(34.34, -6.48) * mm});
            skLineSegment(sketch, "E4138", {"start": v(34.34, -6.48) * mm, "end": v(34.34, -6.67) * mm});
            skLineSegment(sketch, "E4139", {"start": v(40.3, 4.12) * mm, "end": v(40.4, 4.28) * mm});
            skLineSegment(sketch, "E4140", {"start": v(40.4, 4.28) * mm, "end": v(40.55, 4.58) * mm});
            skLineSegment(sketch, "E4141", {"start": v(40.55, 4.58) * mm, "end": v(40.7, 4.86) * mm});
            skLineSegment(sketch, "E4142", {"start": v(40.7, 4.86) * mm, "end": v(40.86, 5.13) * mm});
            skLineSegment(sketch, "E4143", {"start": v(40.86, 5.13) * mm, "end": v(41, 5.38) * mm});
            skLineSegment(sketch, "E4144", {"start": v(41, 5.38) * mm, "end": v(41.15, 5.62) * mm});
            skLineSegment(sketch, "E4145", {"start": v(41.15, 5.62) * mm, "end": v(41.3, 5.85) * mm});
            skLineSegment(sketch, "E4146", {"start": v(41.3, 5.85) * mm, "end": v(41.43, 6.07) * mm});
            skLineSegment(sketch, "E4147", {"start": v(41.43, 6.07) * mm, "end": v(41.57, 6.27) * mm});
            skLineSegment(sketch, "E4148", {"start": v(41.57, 6.27) * mm, "end": v(41.7, 6.46) * mm});
            skLineSegment(sketch, "E4149", {"start": v(41.7, 6.46) * mm, "end": v(41.82, 6.64) * mm});
            skLineSegment(sketch, "E4150", {"start": v(41.82, 6.64) * mm, "end": v(41.95, 6.81) * mm});
            skLineSegment(sketch, "E4151", {"start": v(41.95, 6.81) * mm, "end": v(42.07, 6.97) * mm});
            skLineSegment(sketch, "E4152", {"start": v(42.07, 6.97) * mm, "end": v(42.19, 7.12) * mm});
            skLineSegment(sketch, "E4153", {"start": v(42.19, 7.12) * mm, "end": v(42.3, 7.26) * mm});
            skLineSegment(sketch, "E4154", {"start": v(42.3, 7.26) * mm, "end": v(42.42, 7.4) * mm});
            skLineSegment(sketch, "E4155", {"start": v(42.42, 7.4) * mm, "end": v(42.53, 7.52) * mm});
            skLineSegment(sketch, "E4156", {"start": v(42.53, 7.52) * mm, "end": v(42.63, 7.63) * mm});
            skLineSegment(sketch, "E4157", {"start": v(42.63, 7.63) * mm, "end": v(42.74, 7.73) * mm});
            skLineSegment(sketch, "E4158", {"start": v(42.74, 7.73) * mm, "end": v(42.84, 7.83) * mm});
            skLineSegment(sketch, "E4159", {"start": v(42.84, 7.83) * mm, "end": v(42.94, 7.92) * mm});
            skLineSegment(sketch, "E4160", {"start": v(42.94, 7.92) * mm, "end": v(43.04, 8) * mm});
            skLineSegment(sketch, "E4161", {"start": v(42.15, 3.65) * mm, "end": v(41.98, 3.36) * mm});
            skLineSegment(sketch, "E4162", {"start": v(41.98, 3.36) * mm, "end": v(41.85, 3.14) * mm});
            skLineSegment(sketch, "E4163", {"start": v(41.85, 3.14) * mm, "end": v(41.72, 2.91) * mm});
            skLineSegment(sketch, "E4164", {"start": v(41.72, 2.91) * mm, "end": v(41.58, 2.69) * mm});
            skLineSegment(sketch, "E4165", {"start": v(41.58, 2.69) * mm, "end": v(41.44, 2.46) * mm});
            skLineSegment(sketch, "E4166", {"start": v(41.44, 2.46) * mm, "end": v(41.3, 2.23) * mm});
            skLineSegment(sketch, "E4167", {"start": v(41.3, 2.23) * mm, "end": v(41.15, 2) * mm});
            skLineSegment(sketch, "E4168", {"start": v(41.15, 2) * mm, "end": v(41, 1.78) * mm});
            skLineSegment(sketch, "E4169", {"start": v(41, 1.78) * mm, "end": v(40.84, 1.54) * mm});
            skLineSegment(sketch, "E4170", {"start": v(40.84, 1.54) * mm, "end": v(40.67, 1.3) * mm});
            skLineSegment(sketch, "E4171", {"start": v(40.67, 1.3) * mm, "end": v(40.5, 1.07) * mm});
            skLineSegment(sketch, "E4172", {"start": v(40.5, 1.07) * mm, "end": v(40.33, 0.83) * mm});
            skLineSegment(sketch, "E4173", {"start": v(40.33, 0.83) * mm, "end": v(40.16, 0.6) * mm});
            skLineSegment(sketch, "E4174", {"start": v(44.1, -5.28) * mm, "end": v(43.1, -6.2) * mm});
            skLineSegment(sketch, "E4175", {"start": v(43.1, -6.2) * mm, "end": v(42.33, -6.93) * mm});
            skLineSegment(sketch, "E4176", {"start": v(42.33, -6.93) * mm, "end": v(41.63, -7.56) * mm});
            skLineSegment(sketch, "E4177", {"start": v(41.63, -7.56) * mm, "end": v(41.56, -7.62) * mm});
            skLineSegment(sketch, "E4178", {"start": v(41.56, -7.62) * mm, "end": v(41.46, -7.7) * mm});
            skLineSegment(sketch, "E4179", {"start": v(41.46, -7.7) * mm, "end": v(41.36, -7.8) * mm});
            skLineSegment(sketch, "E4180", {"start": v(41.36, -7.8) * mm, "end": v(41.26, -7.88) * mm});
            skLineSegment(sketch, "E4181", {"start": v(41.26, -7.88) * mm, "end": v(41.17, -7.96) * mm});
            skLineSegment(sketch, "E4182", {"start": v(41.17, -7.96) * mm, "end": v(41.08, -8.03) * mm});
            skLineSegment(sketch, "E4183", {"start": v(41.08, -8.03) * mm, "end": v(41, -8.1) * mm});
            skLineSegment(sketch, "E4184", {"start": v(41, -8.1) * mm, "end": v(40.9, -8.17) * mm});
            skLineSegment(sketch, "E4185", {"start": v(40.9, -8.17) * mm, "end": v(40.82, -8.24) * mm});
            skLineSegment(sketch, "E4186", {"start": v(40.82, -8.24) * mm, "end": v(40.73, -8.3) * mm});
            skLineSegment(sketch, "E4187", {"start": v(40.73, -8.3) * mm, "end": v(40.65, -8.36) * mm});
            skLineSegment(sketch, "E4188", {"start": v(40.65, -8.36) * mm, "end": v(40.57, -8.42) * mm});
            skLineSegment(sketch, "E4189", {"start": v(40.57, -8.42) * mm, "end": v(40.5, -8.47) * mm});
            skLineSegment(sketch, "E4190", {"start": v(40.5, -8.47) * mm, "end": v(40.41, -8.53) * mm});
            skLineSegment(sketch, "E4191", {"start": v(37.28, -6.05) * mm, "end": v(37.28, -5.99) * mm});
            skLineSegment(sketch, "E4192", {"start": v(37.28, -5.99) * mm, "end": v(37.28, -5.91) * mm});
            skLineSegment(sketch, "E4193", {"start": v(37.28, -5.91) * mm, "end": v(37.28, -5.84) * mm});
            skLineSegment(sketch, "E4194", {"start": v(37.28, -5.84) * mm, "end": v(37.29, -5.76) * mm});
            skLineSegment(sketch, "E4195", {"start": v(37.29, -5.76) * mm, "end": v(37.3, -5.67) * mm});
            skLineSegment(sketch, "E4196", {"start": v(37.3, -5.67) * mm, "end": v(37.3, -5.58) * mm});
            skLineSegment(sketch, "E4197", {"start": v(37.3, -5.58) * mm, "end": v(37.31, -5.48) * mm});
            skLineSegment(sketch, "E4198", {"start": v(37.31, -5.48) * mm, "end": v(37.33, -5.38) * mm});
            skLineSegment(sketch, "E4199", {"start": v(37.33, -5.38) * mm, "end": v(37.34, -5.27) * mm});
            skLineSegment(sketch, "E4200", {"start": v(37.34, -5.27) * mm, "end": v(37.36, -5.15) * mm});
            skLineSegment(sketch, "E4201", {"start": v(37.36, -5.15) * mm, "end": v(37.37, -5.04) * mm});
            skLineSegment(sketch, "E4202", {"start": v(37.37, -5.04) * mm, "end": v(37.4, -4.91) * mm});
            skLineSegment(sketch, "E4203", {"start": v(37.4, -4.91) * mm, "end": v(37.42, -4.78) * mm});
            skLineSegment(sketch, "E4204", {"start": v(37.42, -4.78) * mm, "end": v(37.44, -4.65) * mm});
            skLineSegment(sketch, "E4205", {"start": v(37.44, -4.65) * mm, "end": v(37.45, -4.6) * mm});
            skLineSegment(sketch, "E4206", {"start": v(37.45, -4.6) * mm, "end": v(37.48, -4.46) * mm});
            skLineSegment(sketch, "E4207", {"start": v(38.17, -1.7) * mm, "end": v(38.24, -1.4) * mm});
            skLineSegment(sketch, "E4208", {"start": v(38.24, -1.4) * mm, "end": v(38.32, -1.08) * mm});
            skLineSegment(sketch, "E4209", {"start": v(38.32, -1.08) * mm, "end": v(38.4, -0.77) * mm});
            skLineSegment(sketch, "E4210", {"start": v(38.4, -0.77) * mm, "end": v(38.48, -0.46) * mm});
            skLineSegment(sketch, "E4211", {"start": v(38.48, -0.46) * mm, "end": v(38.57, -0.14) * mm});
            skLineSegment(sketch, "E4212", {"start": v(38.57, -0.14) * mm, "end": v(38.67, 0.17) * mm});
            skLineSegment(sketch, "E4213", {"start": v(38.67, 0.17) * mm, "end": v(38.77, 0.49) * mm});
            skLineSegment(sketch, "E4214", {"start": v(38.77, 0.49) * mm, "end": v(38.87, 0.8) * mm});
            skLineSegment(sketch, "E4215", {"start": v(38.87, 0.8) * mm, "end": v(38.99, 1.12) * mm});
            skLineSegment(sketch, "E4216", {"start": v(38.99, 1.12) * mm, "end": v(39.1, 1.44) * mm});
            skLineSegment(sketch, "E4217", {"start": v(39.1, 1.44) * mm, "end": v(39.23, 1.75) * mm});
            skLineSegment(sketch, "E4218", {"start": v(39.23, 1.75) * mm, "end": v(39.35, 2.07) * mm});
            skLineSegment(sketch, "E4219", {"start": v(39.35, 2.07) * mm, "end": v(39.49, 2.4) * mm});
            skLineSegment(sketch, "E4220", {"start": v(39.49, 2.4) * mm, "end": v(39.63, 2.71) * mm});
            skLineSegment(sketch, "E4221", {"start": v(39.63, 2.71) * mm, "end": v(39.77, 3.03) * mm});
            skLineSegment(sketch, "E4222", {"start": v(39.77, 3.03) * mm, "end": v(39.93, 3.35) * mm});
            skLineSegment(sketch, "E4223", {"start": v(39.93, 3.35) * mm, "end": v(40.08, 3.67) * mm});
            skLineSegment(sketch, "E4224", {"start": v(40.08, 3.67) * mm, "end": v(40.25, 4) * mm});
            skLineSegment(sketch, "E4225", {"start": v(40.25, 4) * mm, "end": v(40.3, 4.12) * mm});
            skLineSegment(sketch, "E4226", {"start": v(43.32, 6) * mm, "end": v(43.25, 5.84) * mm});
            skLineSegment(sketch, "E4227", {"start": v(43.25, 5.84) * mm, "end": v(43.18, 5.68) * mm});
            skLineSegment(sketch, "E4228", {"start": v(43.18, 5.68) * mm, "end": v(43.11, 5.52) * mm});
            skLineSegment(sketch, "E4229", {"start": v(43.11, 5.52) * mm, "end": v(43.03, 5.35) * mm});
            skLineSegment(sketch, "E4230", {"start": v(43.03, 5.35) * mm, "end": v(42.95, 5.17) * mm});
            skLineSegment(sketch, "E4231", {"start": v(42.95, 5.17) * mm, "end": v(42.86, 4.98) * mm});
            skLineSegment(sketch, "E4232", {"start": v(42.86, 4.98) * mm, "end": v(42.76, 4.79) * mm});
            skLineSegment(sketch, "E4233", {"start": v(42.76, 4.79) * mm, "end": v(42.65, 4.58) * mm});
            skLineSegment(sketch, "E4234", {"start": v(42.65, 4.58) * mm, "end": v(42.54, 4.37) * mm});
            skLineSegment(sketch, "E4235", {"start": v(42.54, 4.37) * mm, "end": v(42.42, 4.14) * mm});
            skLineSegment(sketch, "E4236", {"start": v(42.42, 4.14) * mm, "end": v(42.29, 3.9) * mm});
            skLineSegment(sketch, "E4237", {"start": v(42.29, 3.9) * mm, "end": v(42.15, 3.65) * mm});
            skLineSegment(sketch, "E4238", {"start": v(43.72, 3.74) * mm, "end": v(43.9, 4.06) * mm});
            skLineSegment(sketch, "E4239", {"start": v(43.9, 4.06) * mm, "end": v(44.09, 4.41) * mm});
            skLineSegment(sketch, "E4240", {"start": v(44.09, 4.41) * mm, "end": v(44.27, 4.76) * mm});
            skLineSegment(sketch, "E4241", {"start": v(44.27, 4.76) * mm, "end": v(44.44, 5.1) * mm});
            skLineSegment(sketch, "E4242", {"start": v(44.44, 5.1) * mm, "end": v(44.6, 5.43) * mm});
            skLineSegment(sketch, "E4243", {"start": v(44.6, 5.43) * mm, "end": v(44.74, 5.75) * mm});
            skLineSegment(sketch, "E4244", {"start": v(44.74, 5.75) * mm, "end": v(44.88, 6.06) * mm});
            skLineSegment(sketch, "E4245", {"start": v(44.88, 6.06) * mm, "end": v(45, 6.37) * mm});
            skLineSegment(sketch, "E4246", {"start": v(45, 6.37) * mm, "end": v(45.13, 6.67) * mm});
            skLineSegment(sketch, "E4247", {"start": v(45.13, 6.67) * mm, "end": v(45.24, 6.96) * mm});
            skLineSegment(sketch, "E4248", {"start": v(45.24, 6.96) * mm, "end": v(45.34, 7.24) * mm});
            skLineSegment(sketch, "E4249", {"start": v(45.34, 7.24) * mm, "end": v(45.43, 7.51) * mm});
            skLineSegment(sketch, "E4250", {"start": v(45.43, 7.51) * mm, "end": v(45.52, 7.78) * mm});
            skLineSegment(sketch, "E4251", {"start": v(45.52, 7.78) * mm, "end": v(45.6, 8.04) * mm});
            skLineSegment(sketch, "E4252", {"start": v(45.6, 8.04) * mm, "end": v(45.66, 8.3) * mm});
            skLineSegment(sketch, "E4253", {"start": v(45.66, 8.3) * mm, "end": v(45.72, 8.55) * mm});
            skLineSegment(sketch, "E4254", {"start": v(45.72, 8.55) * mm, "end": v(45.78, 8.8) * mm});
            skLineSegment(sketch, "E4255", {"start": v(45.78, 8.8) * mm, "end": v(45.83, 9.03) * mm});
            skLineSegment(sketch, "E4256", {"start": v(45.83, 9.03) * mm, "end": v(45.87, 9.26) * mm});
            skLineSegment(sketch, "E4257", {"start": v(45.87, 9.26) * mm, "end": v(45.9, 9.48) * mm});
            skLineSegment(sketch, "E4258", {"start": v(45.9, 9.48) * mm, "end": v(45.93, 9.7) * mm});
            skLineSegment(sketch, "E4259", {"start": v(45.93, 9.7) * mm, "end": v(45.95, 9.91) * mm});
            skLineSegment(sketch, "E4260", {"start": v(45.95, 9.91) * mm, "end": v(45.96, 10.12) * mm});
            skLineSegment(sketch, "E4261", {"start": v(45.96, 10.12) * mm, "end": v(45.97, 10.33) * mm});
            skLineSegment(sketch, "E4262", {"start": v(45.97, 10.33) * mm, "end": v(45.97, 10.52) * mm});
            skLineSegment(sketch, "E4263", {"start": v(45.97, 10.52) * mm, "end": v(45.97, 10.56) * mm});
            skLineSegment(sketch, "E4264", {"start": v(45.97, 10.56) * mm, "end": v(45.97, 10.65) * mm});
            skLineSegment(sketch, "E4265", {"start": v(45.97, 10.65) * mm, "end": v(45.97, 10.74) * mm});
            skLineSegment(sketch, "E4266", {"start": v(45.97, 10.74) * mm, "end": v(45.97, 10.82) * mm});
            skLineSegment(sketch, "E4267", {"start": v(45.97, 10.82) * mm, "end": v(45.96, 10.9) * mm});
            skLineSegment(sketch, "E4268", {"start": v(45.96, 10.9) * mm, "end": v(45.96, 10.98) * mm});
            skLineSegment(sketch, "E4269", {"start": v(45.96, 10.98) * mm, "end": v(45.95, 11.06) * mm});
            skLineSegment(sketch, "E4270", {"start": v(45.95, 11.06) * mm, "end": v(45.95, 11.13) * mm});
            skLineSegment(sketch, "E4271", {"start": v(45.95, 11.13) * mm, "end": v(45.94, 11.2) * mm});
            skLineSegment(sketch, "E4272", {"start": v(45.94, 11.2) * mm, "end": v(45.93, 11.26) * mm});
            skLineSegment(sketch, "E4273", {"start": v(45.93, 11.26) * mm, "end": v(45.93, 11.33) * mm});
            skLineSegment(sketch, "E4274", {"start": v(45.93, 11.33) * mm, "end": v(45.92, 11.38) * mm});
            skLineSegment(sketch, "E4275", {"start": v(45.92, 11.38) * mm, "end": v(45.9, 11.44) * mm});
            skLineSegment(sketch, "E4276", {"start": v(45.9, 11.44) * mm, "end": v(45.9, 11.5) * mm});
            skLineSegment(sketch, "E4277", {"start": v(45.9, 11.5) * mm, "end": v(45.9, 11.54) * mm});
            skLineSegment(sketch, "E4278", {"start": v(45.9, 11.54) * mm, "end": v(45.88, 11.59) * mm});
            skLineSegment(sketch, "E4279", {"start": v(45.88, 11.59) * mm, "end": v(45.87, 11.63) * mm});
            skLineSegment(sketch, "E4280", {"start": v(45.87, 11.63) * mm, "end": v(45.86, 11.67) * mm});
            skLineSegment(sketch, "E4281", {"start": v(45.86, 11.67) * mm, "end": v(45.85, 11.7) * mm});
            skLineSegment(sketch, "E4282", {"start": v(45.85, 11.7) * mm, "end": v(45.84, 11.74) * mm});
            skLineSegment(sketch, "E4283", {"start": v(45.84, 11.74) * mm, "end": v(45.83, 11.77) * mm});
            skLineSegment(sketch, "E4284", {"start": v(44.1, -6.75) * mm, "end": v(44.1, -5.28) * mm});
            skLineSegment(sketch, "E4285", {"start": v(43.8, 7.76) * mm, "end": v(43.8, 7.72) * mm});
            skLineSegment(sketch, "E4286", {"start": v(43.8, 7.72) * mm, "end": v(43.8, 7.67) * mm});
            skLineSegment(sketch, "E4287", {"start": v(43.8, 7.67) * mm, "end": v(43.8, 7.62) * mm});
            skLineSegment(sketch, "E4288", {"start": v(43.8, 7.62) * mm, "end": v(43.8, 7.57) * mm});
            skLineSegment(sketch, "E4289", {"start": v(43.8, 7.57) * mm, "end": v(43.79, 7.51) * mm});
            skLineSegment(sketch, "E4290", {"start": v(43.79, 7.51) * mm, "end": v(43.78, 7.45) * mm});
            skLineSegment(sketch, "E4291", {"start": v(43.78, 7.45) * mm, "end": v(43.77, 7.39) * mm});
            skLineSegment(sketch, "E4292", {"start": v(43.77, 7.39) * mm, "end": v(43.76, 7.32) * mm});
            skLineSegment(sketch, "E4293", {"start": v(43.76, 7.32) * mm, "end": v(43.74, 7.25) * mm});
            skLineSegment(sketch, "E4294", {"start": v(43.74, 7.25) * mm, "end": v(43.72, 7.17) * mm});
            skLineSegment(sketch, "E4295", {"start": v(43.72, 7.17) * mm, "end": v(43.7, 7.1) * mm});
            skLineSegment(sketch, "E4296", {"start": v(43.7, 7.1) * mm, "end": v(43.68, 7) * mm});
            skLineSegment(sketch, "E4297", {"start": v(43.68, 7) * mm, "end": v(43.65, 6.92) * mm});
            skLineSegment(sketch, "E4298", {"start": v(43.65, 6.92) * mm, "end": v(43.62, 6.82) * mm});
            skLineSegment(sketch, "E4299", {"start": v(43.62, 6.82) * mm, "end": v(43.59, 6.72) * mm});
            skLineSegment(sketch, "E4300", {"start": v(43.59, 6.72) * mm, "end": v(43.55, 6.61) * mm});
            skLineSegment(sketch, "E4301", {"start": v(43.55, 6.61) * mm, "end": v(43.5, 6.5) * mm});
            skLineSegment(sketch, "E4302", {"start": v(43.5, 6.5) * mm, "end": v(43.46, 6.38) * mm});
            skLineSegment(sketch, "E4303", {"start": v(43.46, 6.38) * mm, "end": v(43.42, 6.25) * mm});
            skLineSegment(sketch, "E4304", {"start": v(43.42, 6.25) * mm, "end": v(43.36, 6.1) * mm});
            skLineSegment(sketch, "E4305", {"start": v(43.36, 6.1) * mm, "end": v(43.32, 6) * mm});
            skLineSegment(sketch, "E4306", {"start": v(45.83, 11.77) * mm, "end": v(45.82, 11.78) * mm});
            skLineSegment(sketch, "E4307", {"start": v(45.82, 11.78) * mm, "end": v(45.82, 11.8) * mm});
            skLineSegment(sketch, "E4308", {"start": v(45.82, 11.8) * mm, "end": v(45.8, 11.81) * mm});
            skLineSegment(sketch, "E4309", {"start": v(45.8, 11.81) * mm, "end": v(45.8, 11.83) * mm});
            skLineSegment(sketch, "E4310", {"start": v(45.8, 11.83) * mm, "end": v(45.8, 11.85) * mm});
            skLineSegment(sketch, "E4311", {"start": v(45.8, 11.85) * mm, "end": v(45.78, 11.87) * mm});
            skLineSegment(sketch, "E4312", {"start": v(45.78, 11.87) * mm, "end": v(45.77, 11.88) * mm});
            skLineSegment(sketch, "E4313", {"start": v(45.77, 11.88) * mm, "end": v(45.76, 11.9) * mm});
            skLineSegment(sketch, "E4314", {"start": v(45.76, 11.9) * mm, "end": v(45.75, 11.91) * mm});
            skLineSegment(sketch, "E4315", {"start": v(45.75, 11.91) * mm, "end": v(45.74, 11.93) * mm});
            skLineSegment(sketch, "E4316", {"start": v(45.74, 11.93) * mm, "end": v(45.73, 11.94) * mm});
            skLineSegment(sketch, "E4317", {"start": v(45.73, 11.94) * mm, "end": v(45.72, 11.96) * mm});
            skLineSegment(sketch, "E4318", {"start": v(45.72, 11.96) * mm, "end": v(45.71, 11.97) * mm});
            skLineSegment(sketch, "E4319", {"start": v(45.71, 11.97) * mm, "end": v(45.7, 11.98) * mm});
            skLineSegment(sketch, "E4320", {"start": v(45.7, 11.98) * mm, "end": v(45.69, 12) * mm});
            skLineSegment(sketch, "E4321", {"start": v(45.69, 12) * mm, "end": v(45.68, 12) * mm});
            skLineSegment(sketch, "E4322", {"start": v(45.68, 12) * mm, "end": v(45.67, 12.02) * mm});
            skLineSegment(sketch, "E4323", {"start": v(45.67, 12.02) * mm, "end": v(45.65, 12.03) * mm});
            skLineSegment(sketch, "E4324", {"start": v(45.65, 12.03) * mm, "end": v(45.64, 12.04) * mm});
            skLineSegment(sketch, "E4325", {"start": v(45.64, 12.04) * mm, "end": v(45.63, 12.05) * mm});
            skLineSegment(sketch, "E4326", {"start": v(45.63, 12.05) * mm, "end": v(45.61, 12.06) * mm});
            skLineSegment(sketch, "E4327", {"start": v(45.61, 12.06) * mm, "end": v(45.6, 12.07) * mm});
            skLineSegment(sketch, "E4328", {"start": v(45.6, 12.07) * mm, "end": v(45.59, 12.07) * mm});
            skLineSegment(sketch, "E4329", {"start": v(45.59, 12.07) * mm, "end": v(45.57, 12.08) * mm});
            skLineSegment(sketch, "E4330", {"start": v(45.57, 12.08) * mm, "end": v(45.56, 12.09) * mm});
            skLineSegment(sketch, "E4331", {"start": v(45.56, 12.09) * mm, "end": v(45.54, 12.1) * mm});
            skLineSegment(sketch, "E4332", {"start": v(45.54, 12.1) * mm, "end": v(45.53, 12.1) * mm});
            skLineSegment(sketch, "E4333", {"start": v(45.53, 12.1) * mm, "end": v(45.51, 12.11) * mm});
            skLineSegment(sketch, "E4334", {"start": v(45.51, 12.11) * mm, "end": v(45.5, 12.12) * mm});
            skLineSegment(sketch, "E4335", {"start": v(45.5, 12.12) * mm, "end": v(45.48, 12.12) * mm});
            skLineSegment(sketch, "E4336", {"start": v(45.48, 12.12) * mm, "end": v(45.47, 12.13) * mm});
            skLineSegment(sketch, "E4337", {"start": v(45.47, 12.13) * mm, "end": v(45.45, 12.13) * mm});
            skLineSegment(sketch, "E4338", {"start": v(45.45, 12.13) * mm, "end": v(45.43, 12.14) * mm});
            skLineSegment(sketch, "E4339", {"start": v(45.43, 12.14) * mm, "end": v(45.41, 12.14) * mm});
            skLineSegment(sketch, "E4340", {"start": v(45.41, 12.14) * mm, "end": v(45.4, 12.14) * mm});
            skLineSegment(sketch, "E4341", {"start": v(45.4, 12.14) * mm, "end": v(45.38, 12.15) * mm});
            skLineSegment(sketch, "E4342", {"start": v(45.38, 12.15) * mm, "end": v(45.36, 12.15) * mm});
            skLineSegment(sketch, "E4343", {"start": v(45.36, 12.15) * mm, "end": v(45.34, 12.15) * mm});
            skLineSegment(sketch, "E4344", {"start": v(45.34, 12.15) * mm, "end": v(45.32, 12.15) * mm});
            skLineSegment(sketch, "E4345", {"start": v(45.32, 12.15) * mm, "end": v(45.3, 12.15) * mm});
            skLineSegment(sketch, "E4346", {"start": v(45.3, 12.15) * mm, "end": v(45.28, 12.15) * mm});
            skSolve(sketch);
        }
        {
            var Q0;
            Q0=makeQuery(id+"F0.imprint","IMPRINT",FACE,{"disambiguationData":[TD([[makeQuery(id+"F0.imprint","IMPRINT",EDGE,{"derivedFrom":sQuery(id+"F0.wireOp",EDGE,"E0")}),1.0]])]});
            var Q1;
            Q1=makeQuery(id+"F0.imprint","IMPRINT",FACE,{"disambiguationData":[TD([[makeQuery(id+"F0.imprint","IMPRINT",EDGE,{"derivedFrom":sQuery(id+"F0.wireOp",EDGE,"E1021")}),1.0]])]});
            var Q2;
            Q2=makeQuery(id+"F0.imprint","IMPRINT",FACE,{"disambiguationData":[TD([[makeQuery(id+"F0.imprint","IMPRINT",EDGE,{"derivedFrom":sQuery(id+"F0.wireOp",EDGE,"E946")}),1.0]])]});
            var Q3;
            Q3=makeQuery(id+"F0.imprint","IMPRINT",FACE,{"disambiguationData":[TD([[makeQuery(id+"F0.imprint","IMPRINT",EDGE,{"derivedFrom":sQuery(id+"F0.wireOp",EDGE,"E1242")}),1.0]])]});
            var Q4;
            Q4=makeQuery(id+"F0.imprint","IMPRINT",FACE,{"disambiguationData":[TD([[makeQuery(id+"F0.imprint","IMPRINT",EDGE,{"derivedFrom":sQuery(id+"F0.wireOp",EDGE,"E1050")}),-1.0]])]});
            var Q5;
            Q5=makeQuery(id+"F0.imprint","IMPRINT",FACE,{"disambiguationData":[TD([[makeQuery(id+"F0.imprint","IMPRINT",EDGE,{"derivedFrom":sQuery(id+"F0.wireOp",EDGE,"E597")}),-1.0]])]});
            extrude(context, id + "F1", {"entities" : qUnion([Q0, Q1, Q2, Q3, Q4, Q5]), "endBound" : BoundingType.SYMMETRIC, "depth" : 12.7 * mm, "offsetDistance" : 25.4 * mm});
        }
    });
